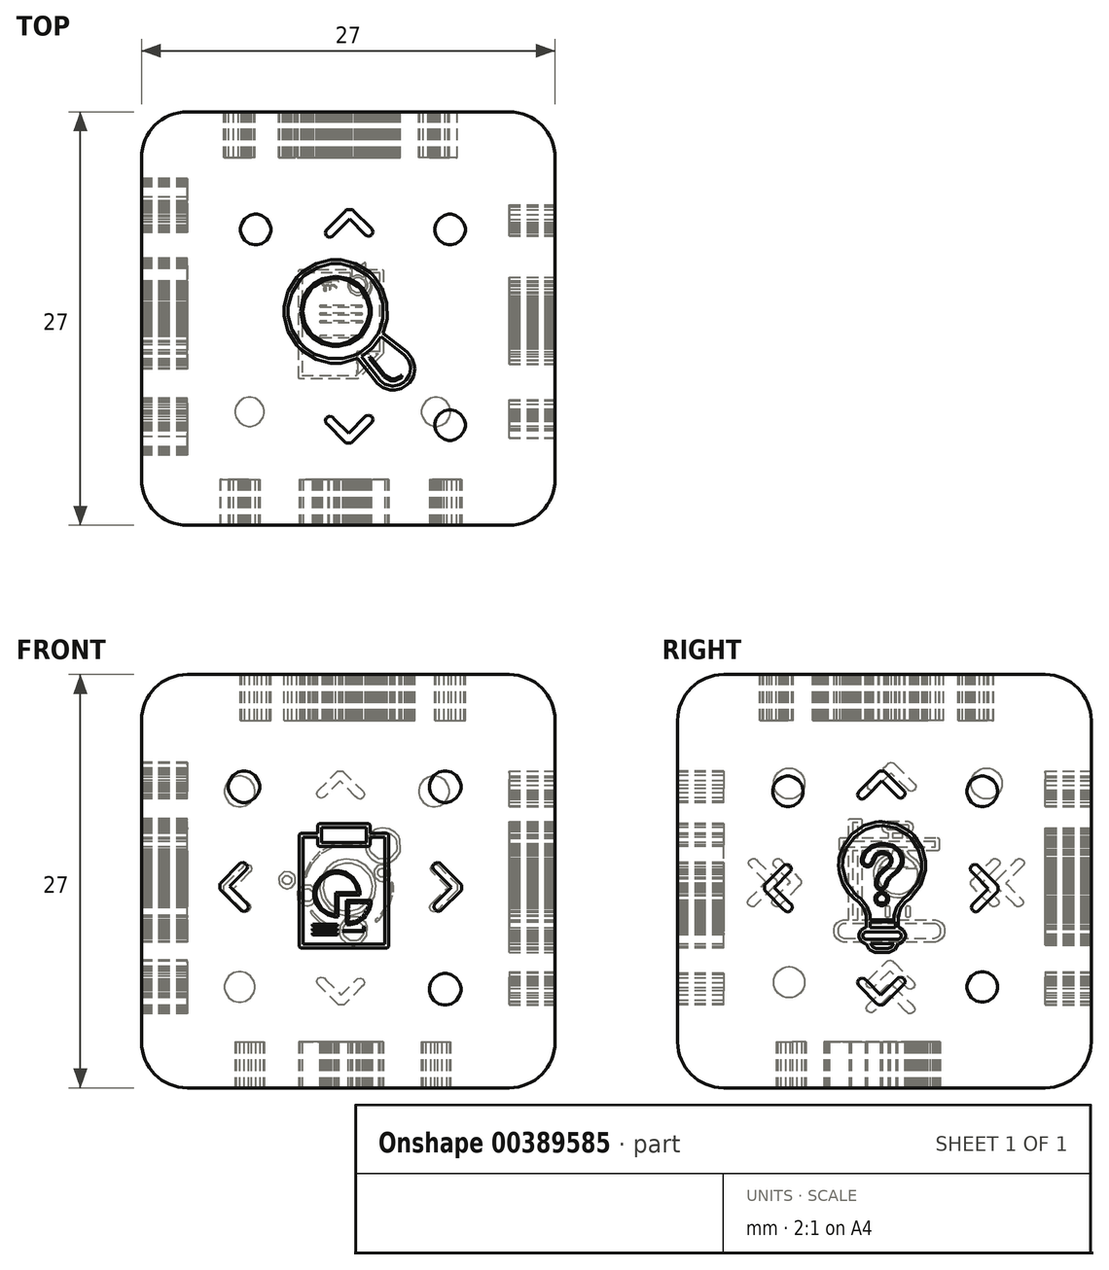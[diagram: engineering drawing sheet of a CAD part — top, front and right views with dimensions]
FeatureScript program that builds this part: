
annotation { "Feature Type Name" : "Feature", "Feature Type Description" : "" }
export const myFeature = defineFeature(function(context is Context, id is Id, definition is map)
    precondition{}
    {
        {
            var Q0;
            Q0=qCreatedBy(makeId("Front.planeOp"),FACE);
            var sketch = newSketch(context, id + "F0", { "sketchPlane" : qUnion([Q0])});
            skLineSegment(sketch, "E0.bottom", {"start": v(-13, 13.95) * mm, "end": v(14, 13.95) * mm});
            skLineSegment(sketch, "E0.top", {"start": v(-13, -13.05) * mm, "end": v(14, -13.05) * mm});
            skLineSegment(sketch, "E0.left", {"start": v(-13, 13.95) * mm, "end": v(-13, -13.05) * mm});
            skLineSegment(sketch, "E0.right", {"start": v(14, 13.95) * mm, "end": v(14, -13.05) * mm});
            skSolve(sketch);
        }
        {
            var Q0;
            Q0=makeQuery(id+"F0.imprint","IMPRINT",FACE,{"disambiguationData":[TD([[makeQuery(id+"F0.imprint","IMPRINT",EDGE,{"derivedFrom":sQuery(id+"F0.wireOp",EDGE,"E0.bottom")}),-1.0]])]});
            extrude(context, id + "F1", {"entities" : qUnion([Q0]), "depth" : 27 * mm});
        }
        {
            var Q0;
            Q0=makeQuery(id+"F1.opExtrude","SWEPT_EDGE",EDGE,{"disambiguationData":[OSD([sQuery(id+"F0.wireOp",EDGE,"E0.bottom"),sQuery(id+"F0.wireOp",EDGE,"E0.right")])]});
            var Q1;
            Q1=makeQuery(id+"F1.opExtrude","CAP_EDGE",EDGE,{"disambiguationData":[OSD([sQuery(id+"F0.wireOp",EDGE,"E0.bottom")])],"isStart":true});
            var Q2;
            Q2=makeQuery(id+"F1.opExtrude","CAP_EDGE",EDGE,{"disambiguationData":[OSD([sQuery(id+"F0.wireOp",EDGE,"E0.right")])],"isStart":true});
            var Q3;
            Q3=makeQuery(id+"F1.opExtrude","CAP_EDGE",EDGE,{"disambiguationData":[OSD([sQuery(id+"F0.wireOp",EDGE,"E0.left")])],"isStart":true});
            var Q4;
            Q4=makeQuery(id+"F1.opExtrude","CAP_EDGE",EDGE,{"disambiguationData":[OSD([sQuery(id+"F0.wireOp",EDGE,"E0.top")])],"isStart":true});
            var Q5;
            Q5=makeQuery(id+"F1.opExtrude","SWEPT_EDGE",EDGE,{"disambiguationData":[OSD([sQuery(id+"F0.wireOp",EDGE,"E0.top"),sQuery(id+"F0.wireOp",EDGE,"E0.left")])]});
            var Q6;
            Q6=makeQuery(id+"F1.opExtrude","SWEPT_EDGE",EDGE,{"disambiguationData":[OSD([sQuery(id+"F0.wireOp",EDGE,"E0.bottom"),sQuery(id+"F0.wireOp",EDGE,"E0.left")])]});
            var Q7;
            Q7=makeQuery(id+"F1.opExtrude","CAP_EDGE",EDGE,{"disambiguationData":[OSD([sQuery(id+"F0.wireOp",EDGE,"E0.left")])],"isStart":false});
            var Q8;
            Q8=makeQuery(id+"F1.opExtrude","CAP_EDGE",EDGE,{"disambiguationData":[OSD([sQuery(id+"F0.wireOp",EDGE,"E0.right")])],"isStart":false});
            var Q9;
            Q9=makeQuery(id+"F1.opExtrude","CAP_EDGE",EDGE,{"disambiguationData":[OSD([sQuery(id+"F0.wireOp",EDGE,"E0.top")])],"isStart":false});
            var Q10;
            Q10=makeQuery(id+"F1.opExtrude","SWEPT_EDGE",EDGE,{"disambiguationData":[OSD([sQuery(id+"F0.wireOp",EDGE,"E0.top"),sQuery(id+"F0.wireOp",EDGE,"E0.right")])]});
            var Q11;
            Q11=makeQuery(id+"F1.opExtrude","CAP_EDGE",EDGE,{"disambiguationData":[OSD([sQuery(id+"F0.wireOp",EDGE,"E0.bottom")])],"isStart":false});
            fillet(context, id + "F2", {"entities" : qUnion([Q0, Q1, Q2, Q3, Q4, Q5, Q6, Q7, Q8, Q9, Q10, Q11]), "radius" : 3 * mm, "tangentPropagation" : true, "allowEdgeOverflow" : false});
        }
        {
            var Q0;
            Q0=makeQuery(id+"F1.opExtrude","CAP_FACE",FACE,{"disambiguationData":[OSD([sQuery(id+"F0.wireOp",EDGE,"E0.bottom"),sQuery(id+"F0.wireOp",EDGE,"E0.top"),sQuery(id+"F0.wireOp",EDGE,"E0.left"),sQuery(id+"F0.wireOp",EDGE,"E0.right")])],"isStart":false});
            var sketch = newSketch(context, id + "F3", { "sketchPlane" : qUnion([Q0])});
            skLineSegment(sketch, "E1", {"start": v(-2.45, -3.67) * mm, "end": v(2.88, -3.67) * mm});
            skLineSegment(sketch, "E2", {"start": v(2.88, -3.67) * mm, "end": v(2.88, 3.33) * mm});
            skLineSegment(sketch, "E3", {"start": v(2.88, 3.33) * mm, "end": v(1.94, 3.33) * mm});
            skLineSegment(sketch, "E4", {"start": v(1.94, 3.33) * mm, "end": v(1.94, 2.84) * mm});
            skLineSegment(sketch, "E5", {"start": v(1.94, 2.84) * mm, "end": v(1.94, 2.8) * mm});
            skLineSegment(sketch, "E6", {"start": v(1.94, 2.8) * mm, "end": v(1.84, 2.7) * mm});
            skLineSegment(sketch, "E7", {"start": v(1.84, 2.7) * mm, "end": v(1.81, 2.7) * mm});
            skLineSegment(sketch, "E8", {"start": v(1.81, 2.7) * mm, "end": v(-1.38, 2.7) * mm});
            skLineSegment(sketch, "E9", {"start": v(-1.38, 2.7) * mm, "end": v(-1.4, 2.7) * mm});
            skLineSegment(sketch, "E10", {"start": v(-1.4, 2.7) * mm, "end": v(-1.5, 2.8) * mm});
            skLineSegment(sketch, "E11", {"start": v(-1.5, 2.8) * mm, "end": v(-1.5, 2.84) * mm});
            skLineSegment(sketch, "E12", {"start": v(-1.5, 2.84) * mm, "end": v(-1.5, 3.33) * mm});
            skLineSegment(sketch, "E13", {"start": v(-1.5, 3.33) * mm, "end": v(-2.45, 3.33) * mm});
            skLineSegment(sketch, "E14", {"start": v(-2.45, 3.33) * mm, "end": v(-2.45, -3.67) * mm});
            skLineSegment(sketch, "E15", {"start": v(3, -3.92) * mm, "end": v(-2.58, -3.92) * mm});
            skLineSegment(sketch, "E16", {"start": v(-2.58, -3.92) * mm, "end": v(-2.6, -3.92) * mm});
            skLineSegment(sketch, "E17", {"start": v(-2.6, -3.92) * mm, "end": v(-2.7, -3.83) * mm});
            skLineSegment(sketch, "E18", {"start": v(-2.7, -3.83) * mm, "end": v(-2.7, -3.8) * mm});
            skLineSegment(sketch, "E19", {"start": v(-2.7, -3.8) * mm, "end": v(-2.7, 3.46) * mm});
            skLineSegment(sketch, "E20", {"start": v(-2.7, 3.46) * mm, "end": v(-2.7, 3.49) * mm});
            skLineSegment(sketch, "E21", {"start": v(-2.7, 3.49) * mm, "end": v(-2.6, 3.59) * mm});
            skLineSegment(sketch, "E22", {"start": v(-2.6, 3.59) * mm, "end": v(-2.58, 3.59) * mm});
            skLineSegment(sketch, "E23", {"start": v(-2.58, 3.59) * mm, "end": v(-1.38, 3.59) * mm});
            skLineSegment(sketch, "E24", {"start": v(-1.38, 3.59) * mm, "end": v(-1.35, 3.59) * mm});
            skLineSegment(sketch, "E25", {"start": v(-1.35, 3.59) * mm, "end": v(-1.25, 3.49) * mm});
            skLineSegment(sketch, "E26", {"start": v(-1.25, 3.49) * mm, "end": v(-1.25, 3.46) * mm});
            skLineSegment(sketch, "E27", {"start": v(-1.25, 3.46) * mm, "end": v(-1.25, 2.97) * mm});
            skLineSegment(sketch, "E28", {"start": v(-1.25, 2.97) * mm, "end": v(1.68, 2.97) * mm});
            skLineSegment(sketch, "E29", {"start": v(1.68, 2.97) * mm, "end": v(1.68, 3.46) * mm});
            skLineSegment(sketch, "E30", {"start": v(1.68, 3.46) * mm, "end": v(1.68, 3.49) * mm});
            skLineSegment(sketch, "E31", {"start": v(1.68, 3.49) * mm, "end": v(1.78, 3.59) * mm});
            skLineSegment(sketch, "E32", {"start": v(1.78, 3.59) * mm, "end": v(1.81, 3.59) * mm});
            skLineSegment(sketch, "E33", {"start": v(1.81, 3.59) * mm, "end": v(3, 3.59) * mm});
            skLineSegment(sketch, "E34", {"start": v(3, 3.59) * mm, "end": v(3.04, 3.59) * mm});
            skLineSegment(sketch, "E35", {"start": v(3.04, 3.59) * mm, "end": v(3.14, 3.49) * mm});
            skLineSegment(sketch, "E36", {"start": v(3.14, 3.49) * mm, "end": v(3.14, 3.46) * mm});
            skLineSegment(sketch, "E37", {"start": v(3.14, 3.46) * mm, "end": v(3.14, -3.8) * mm});
            skLineSegment(sketch, "E38", {"start": v(3.14, -3.8) * mm, "end": v(3.14, -3.83) * mm});
            skLineSegment(sketch, "E39", {"start": v(3.14, -3.83) * mm, "end": v(3.04, -3.92) * mm});
            skLineSegment(sketch, "E40", {"start": v(3.04, -3.92) * mm, "end": v(3, -3.92) * mm});
            skLineSegment(sketch, "E41", {"start": v(1.68, 2.97) * mm, "end": v(1.68, 3.97) * mm});
            skLineSegment(sketch, "E42", {"start": v(1.68, 3.97) * mm, "end": v(-1.25, 3.97) * mm});
            skLineSegment(sketch, "E43", {"start": v(-1.25, 3.97) * mm, "end": v(-1.25, 2.97) * mm});
            skLineSegment(sketch, "E44", {"start": v(-1.5, 2.84) * mm, "end": v(-1.5, 4.1) * mm});
            skLineSegment(sketch, "E45", {"start": v(-1.5, 4.1) * mm, "end": v(-1.5, 4.13) * mm});
            skLineSegment(sketch, "E46", {"start": v(-1.5, 4.13) * mm, "end": v(-1.4, 4.23) * mm});
            skLineSegment(sketch, "E47", {"start": v(-1.4, 4.23) * mm, "end": v(-1.38, 4.23) * mm});
            skLineSegment(sketch, "E48", {"start": v(-1.38, 4.23) * mm, "end": v(1.81, 4.23) * mm});
            skLineSegment(sketch, "E49", {"start": v(1.81, 4.23) * mm, "end": v(1.84, 4.23) * mm});
            skLineSegment(sketch, "E50", {"start": v(1.84, 4.23) * mm, "end": v(1.94, 4.13) * mm});
            skLineSegment(sketch, "E51", {"start": v(1.94, 4.13) * mm, "end": v(1.94, 4.1) * mm});
            skLineSegment(sketch, "E52", {"start": v(1.94, 4.1) * mm, "end": v(1.94, 2.84) * mm});
            skLineSegment(sketch, "E53", {"start": v(-0.26, 0.99) * mm, "end": v(-0.39, 0.99) * mm});
            skLineSegment(sketch, "E54", {"start": v(-0.39, 0.99) * mm, "end": v(-0.78, 0.88) * mm});
            skLineSegment(sketch, "E55", {"start": v(-0.78, 0.88) * mm, "end": v(-1.22, 0.59) * mm});
            skLineSegment(sketch, "E56", {"start": v(-1.22, 0.59) * mm, "end": v(-1.5, 0.16) * mm});
            skLineSegment(sketch, "E57", {"start": v(-1.5, 0.16) * mm, "end": v(-1.61, -0.24) * mm});
            skLineSegment(sketch, "E58", {"start": v(-1.61, -0.24) * mm, "end": v(-1.61, -0.37) * mm});
            skLineSegment(sketch, "E59", {"start": v(-1.61, -0.37) * mm, "end": v(-1.61, -0.5) * mm});
            skLineSegment(sketch, "E60", {"start": v(-1.61, -0.5) * mm, "end": v(-1.51, -0.88) * mm});
            skLineSegment(sketch, "E61", {"start": v(-1.51, -0.88) * mm, "end": v(-1.24, -1.3) * mm});
            skLineSegment(sketch, "E62", {"start": v(-1.24, -1.3) * mm, "end": v(-0.83, -1.6) * mm});
            skLineSegment(sketch, "E63", {"start": v(-0.83, -1.6) * mm, "end": v(-0.46, -1.72) * mm});
            skLineSegment(sketch, "E64", {"start": v(-0.46, -1.72) * mm, "end": v(-0.33, -1.73) * mm});
            skLineSegment(sketch, "E65", {"start": v(-0.33, -1.73) * mm, "end": v(-0.33, -0.3) * mm});
            skLineSegment(sketch, "E66", {"start": v(-0.33, -0.3) * mm, "end": v(1.1, -0.3) * mm});
            skLineSegment(sketch, "E67", {"start": v(1.1, -0.3) * mm, "end": v(1.1, -0.17) * mm});
            skLineSegment(sketch, "E68", {"start": v(1.1, -0.17) * mm, "end": v(0.97, 0.2) * mm});
            skLineSegment(sketch, "E69", {"start": v(0.97, 0.2) * mm, "end": v(0.68, 0.61) * mm});
            skLineSegment(sketch, "E70", {"start": v(0.68, 0.61) * mm, "end": v(0.26, 0.89) * mm});
            skLineSegment(sketch, "E71", {"start": v(0.26, 0.89) * mm, "end": v(-0.13, 0.99) * mm});
            skLineSegment(sketch, "E72", {"start": v(-0.13, 0.99) * mm, "end": v(-0.26, 0.99) * mm});
            skLineSegment(sketch, "E73", {"start": v(-0.18, -1.88) * mm, "end": v(-0.26, -1.88) * mm});
            skLineSegment(sketch, "E74", {"start": v(-0.26, -1.88) * mm, "end": v(-0.4, -1.88) * mm});
            skLineSegment(sketch, "E75", {"start": v(-0.4, -1.88) * mm, "end": v(-0.84, -1.76) * mm});
            skLineSegment(sketch, "E76", {"start": v(-0.84, -1.76) * mm, "end": v(-1.32, -1.44) * mm});
            skLineSegment(sketch, "E77", {"start": v(-1.32, -1.44) * mm, "end": v(-1.65, -0.96) * mm});
            skLineSegment(sketch, "E78", {"start": v(-1.65, -0.96) * mm, "end": v(-1.77, -0.52) * mm});
            skLineSegment(sketch, "E79", {"start": v(-1.77, -0.52) * mm, "end": v(-1.77, -0.37) * mm});
            skLineSegment(sketch, "E80", {"start": v(-1.77, -0.37) * mm, "end": v(-1.77, -0.22) * mm});
            skLineSegment(sketch, "E81", {"start": v(-1.77, -0.22) * mm, "end": v(-1.65, 0.22) * mm});
            skLineSegment(sketch, "E82", {"start": v(-1.65, 0.22) * mm, "end": v(-1.32, 0.7) * mm});
            skLineSegment(sketch, "E83", {"start": v(-1.32, 0.7) * mm, "end": v(-0.84, 1.02) * mm});
            skLineSegment(sketch, "E84", {"start": v(-0.84, 1.02) * mm, "end": v(-0.4, 1.14) * mm});
            skLineSegment(sketch, "E85", {"start": v(-0.4, 1.14) * mm, "end": v(-0.26, 1.14) * mm});
            skLineSegment(sketch, "E86", {"start": v(-0.26, 1.14) * mm, "end": v(-0.1, 1.14) * mm});
            skLineSegment(sketch, "E87", {"start": v(-0.1, 1.14) * mm, "end": v(0.33, 1.02) * mm});
            skLineSegment(sketch, "E88", {"start": v(0.33, 1.02) * mm, "end": v(0.81, 0.7) * mm});
            skLineSegment(sketch, "E89", {"start": v(0.81, 0.7) * mm, "end": v(1.14, 0.22) * mm});
            skLineSegment(sketch, "E90", {"start": v(1.14, 0.22) * mm, "end": v(1.26, -0.22) * mm});
            skLineSegment(sketch, "E91", {"start": v(1.26, -0.22) * mm, "end": v(1.26, -0.37) * mm});
            skLineSegment(sketch, "E92", {"start": v(1.26, -0.37) * mm, "end": v(1.26, -0.45) * mm});
            skLineSegment(sketch, "E93", {"start": v(1.26, -0.45) * mm, "end": v(-0.18, -0.45) * mm});
            skLineSegment(sketch, "E94", {"start": v(-0.18, -0.45) * mm, "end": v(-0.18, -1.88) * mm});
            skLineSegment(sketch, "E95", {"start": v(-0.47, 1.34) * mm, "end": v(-0.48, 1.34) * mm});
            skLineSegment(sketch, "E96", {"start": v(-0.48, 1.34) * mm, "end": v(-0.5, 1.37) * mm});
            skLineSegment(sketch, "E97", {"start": v(-0.5, 1.37) * mm, "end": v(-0.5, 1.37) * mm});
            skLineSegment(sketch, "E98", {"start": v(-0.5, 1.37) * mm, "end": v(-0.5, 2.1) * mm});
            skLineSegment(sketch, "E99", {"start": v(-0.5, 2.1) * mm, "end": v(-0.17, 2.1) * mm});
            skLineSegment(sketch, "E100", {"start": v(-0.17, 2.1) * mm, "end": v(-0.16, 2.1) * mm});
            skLineSegment(sketch, "E101", {"start": v(-0.16, 2.1) * mm, "end": v(-0.14, 2.09) * mm});
            skLineSegment(sketch, "E102", {"start": v(-0.14, 2.09) * mm, "end": v(-0.14, 2.08) * mm});
            skLineSegment(sketch, "E103", {"start": v(-0.14, 2.08) * mm, "end": v(-0.14, 2.07) * mm});
            skLineSegment(sketch, "E104", {"start": v(-0.14, 2.07) * mm, "end": v(-0.16, 2.05) * mm});
            skLineSegment(sketch, "E105", {"start": v(-0.16, 2.05) * mm, "end": v(-0.17, 2.05) * mm});
            skLineSegment(sketch, "E106", {"start": v(-0.17, 2.05) * mm, "end": v(-0.44, 2.05) * mm});
            skLineSegment(sketch, "E107", {"start": v(-0.44, 2.05) * mm, "end": v(-0.44, 1.37) * mm});
            skLineSegment(sketch, "E108", {"start": v(-0.44, 1.37) * mm, "end": v(-0.44, 1.37) * mm});
            skLineSegment(sketch, "E109", {"start": v(-0.44, 1.37) * mm, "end": v(-0.46, 1.34) * mm});
            skLineSegment(sketch, "E110", {"start": v(-0.46, 1.34) * mm, "end": v(-0.47, 1.34) * mm});
            skLineSegment(sketch, "E111", {"start": v(1.54, -2.84) * mm, "end": v(0.16, -2.84) * mm});
            skLineSegment(sketch, "E112", {"start": v(0.16, -2.84) * mm, "end": v(0.16, -2.84) * mm});
            skLineSegment(sketch, "E113", {"start": v(0.16, -2.84) * mm, "end": v(0.13, -2.82) * mm});
            skLineSegment(sketch, "E114", {"start": v(0.13, -2.82) * mm, "end": v(0.13, -2.81) * mm});
            skLineSegment(sketch, "E115", {"start": v(0.13, -2.81) * mm, "end": v(0.13, -2.8) * mm});
            skLineSegment(sketch, "E116", {"start": v(0.13, -2.8) * mm, "end": v(0.16, -2.78) * mm});
            skLineSegment(sketch, "E117", {"start": v(0.16, -2.78) * mm, "end": v(0.16, -2.78) * mm});
            skLineSegment(sketch, "E118", {"start": v(0.16, -2.78) * mm, "end": v(1.49, -2.78) * mm});
            skLineSegment(sketch, "E119", {"start": v(1.49, -2.78) * mm, "end": v(1.49, -2.51) * mm});
            skLineSegment(sketch, "E120", {"start": v(1.49, -2.51) * mm, "end": v(1.49, -2.5) * mm});
            skLineSegment(sketch, "E121", {"start": v(1.49, -2.5) * mm, "end": v(1.5, -2.48) * mm});
            skLineSegment(sketch, "E122", {"start": v(1.5, -2.48) * mm, "end": v(1.51, -2.48) * mm});
            skLineSegment(sketch, "E123", {"start": v(1.51, -2.48) * mm, "end": v(1.52, -2.48) * mm});
            skLineSegment(sketch, "E124", {"start": v(1.52, -2.48) * mm, "end": v(1.54, -2.5) * mm});
            skLineSegment(sketch, "E125", {"start": v(1.54, -2.5) * mm, "end": v(1.54, -2.51) * mm});
            skLineSegment(sketch, "E126", {"start": v(1.54, -2.51) * mm, "end": v(1.54, -2.84) * mm});
            skLineSegment(sketch, "E127", {"start": v(1.93, 2) * mm, "end": v(0.4, 2) * mm});
            skLineSegment(sketch, "E128", {"start": v(0.4, 2) * mm, "end": v(0.38, 2) * mm});
            skLineSegment(sketch, "E129", {"start": v(0.38, 2) * mm, "end": v(0.33, 2.05) * mm});
            skLineSegment(sketch, "E130", {"start": v(0.33, 2.05) * mm, "end": v(0.33, 2.07) * mm});
            skLineSegment(sketch, "E131", {"start": v(0.33, 2.07) * mm, "end": v(0.33, 2.08) * mm});
            skLineSegment(sketch, "E132", {"start": v(0.33, 2.08) * mm, "end": v(0.38, 2.13) * mm});
            skLineSegment(sketch, "E133", {"start": v(0.38, 2.13) * mm, "end": v(0.4, 2.13) * mm});
            skLineSegment(sketch, "E134", {"start": v(0.4, 2.13) * mm, "end": v(1.93, 2.13) * mm});
            skLineSegment(sketch, "E135", {"start": v(1.93, 2.13) * mm, "end": v(1.95, 2.13) * mm});
            skLineSegment(sketch, "E136", {"start": v(1.95, 2.13) * mm, "end": v(2, 2.08) * mm});
            skLineSegment(sketch, "E137", {"start": v(2, 2.08) * mm, "end": v(2, 2.07) * mm});
            skLineSegment(sketch, "E138", {"start": v(2, 2.07) * mm, "end": v(2, 2.05) * mm});
            skLineSegment(sketch, "E139", {"start": v(2, 2.05) * mm, "end": v(1.95, 2) * mm});
            skLineSegment(sketch, "E140", {"start": v(1.95, 2) * mm, "end": v(1.93, 2) * mm});
            skLineSegment(sketch, "E141", {"start": v(1.93, 1.72) * mm, "end": v(0.4, 1.72) * mm});
            skLineSegment(sketch, "E142", {"start": v(0.4, 1.72) * mm, "end": v(0.38, 1.72) * mm});
            skLineSegment(sketch, "E143", {"start": v(0.38, 1.72) * mm, "end": v(0.33, 1.76) * mm});
            skLineSegment(sketch, "E144", {"start": v(0.33, 1.76) * mm, "end": v(0.33, 1.78) * mm});
            skLineSegment(sketch, "E145", {"start": v(0.33, 1.78) * mm, "end": v(0.33, 1.8) * mm});
            skLineSegment(sketch, "E146", {"start": v(0.33, 1.8) * mm, "end": v(0.38, 1.84) * mm});
            skLineSegment(sketch, "E147", {"start": v(0.38, 1.84) * mm, "end": v(0.4, 1.84) * mm});
            skLineSegment(sketch, "E148", {"start": v(0.4, 1.84) * mm, "end": v(1.93, 1.84) * mm});
            skLineSegment(sketch, "E149", {"start": v(1.93, 1.84) * mm, "end": v(1.95, 1.84) * mm});
            skLineSegment(sketch, "E150", {"start": v(1.95, 1.84) * mm, "end": v(2, 1.8) * mm});
            skLineSegment(sketch, "E151", {"start": v(2, 1.8) * mm, "end": v(2, 1.78) * mm});
            skLineSegment(sketch, "E152", {"start": v(2, 1.78) * mm, "end": v(2, 1.76) * mm});
            skLineSegment(sketch, "E153", {"start": v(2, 1.76) * mm, "end": v(1.95, 1.72) * mm});
            skLineSegment(sketch, "E154", {"start": v(1.95, 1.72) * mm, "end": v(1.93, 1.72) * mm});
            skLineSegment(sketch, "E155", {"start": v(1.93, 1.43) * mm, "end": v(0.4, 1.43) * mm});
            skLineSegment(sketch, "E156", {"start": v(0.4, 1.43) * mm, "end": v(0.38, 1.43) * mm});
            skLineSegment(sketch, "E157", {"start": v(0.38, 1.43) * mm, "end": v(0.33, 1.48) * mm});
            skLineSegment(sketch, "E158", {"start": v(0.33, 1.48) * mm, "end": v(0.33, 1.5) * mm});
            skLineSegment(sketch, "E159", {"start": v(0.33, 1.5) * mm, "end": v(0.33, 1.5) * mm});
            skLineSegment(sketch, "E160", {"start": v(0.33, 1.5) * mm, "end": v(0.38, 1.56) * mm});
            skLineSegment(sketch, "E161", {"start": v(0.38, 1.56) * mm, "end": v(0.4, 1.56) * mm});
            skLineSegment(sketch, "E162", {"start": v(0.4, 1.56) * mm, "end": v(1.93, 1.56) * mm});
            skLineSegment(sketch, "E163", {"start": v(1.93, 1.56) * mm, "end": v(1.95, 1.56) * mm});
            skLineSegment(sketch, "E164", {"start": v(1.95, 1.56) * mm, "end": v(2, 1.5) * mm});
            skLineSegment(sketch, "E165", {"start": v(2, 1.5) * mm, "end": v(2, 1.5) * mm});
            skLineSegment(sketch, "E166", {"start": v(2, 1.5) * mm, "end": v(2, 1.48) * mm});
            skLineSegment(sketch, "E167", {"start": v(2, 1.48) * mm, "end": v(1.95, 1.43) * mm});
            skLineSegment(sketch, "E168", {"start": v(1.95, 1.43) * mm, "end": v(1.93, 1.43) * mm});
            skLineSegment(sketch, "E169", {"start": v(-0.26, -2.5) * mm, "end": v(-1.8, -2.5) * mm});
            skLineSegment(sketch, "E170", {"start": v(-1.8, -2.5) * mm, "end": v(-1.8, -2.5) * mm});
            skLineSegment(sketch, "E171", {"start": v(-1.8, -2.5) * mm, "end": v(-1.85, -2.44) * mm});
            skLineSegment(sketch, "E172", {"start": v(-1.85, -2.44) * mm, "end": v(-1.85, -2.43) * mm});
            skLineSegment(sketch, "E173", {"start": v(-1.85, -2.43) * mm, "end": v(-1.85, -2.41) * mm});
            skLineSegment(sketch, "E174", {"start": v(-1.85, -2.41) * mm, "end": v(-1.8, -2.36) * mm});
            skLineSegment(sketch, "E175", {"start": v(-1.8, -2.36) * mm, "end": v(-1.8, -2.36) * mm});
            skLineSegment(sketch, "E176", {"start": v(-1.8, -2.36) * mm, "end": v(-0.26, -2.36) * mm});
            skLineSegment(sketch, "E177", {"start": v(-0.26, -2.36) * mm, "end": v(-0.24, -2.36) * mm});
            skLineSegment(sketch, "E178", {"start": v(-0.24, -2.36) * mm, "end": v(-0.2, -2.41) * mm});
            skLineSegment(sketch, "E179", {"start": v(-0.2, -2.41) * mm, "end": v(-0.2, -2.43) * mm});
            skLineSegment(sketch, "E180", {"start": v(-0.2, -2.43) * mm, "end": v(-0.2, -2.44) * mm});
            skLineSegment(sketch, "E181", {"start": v(-0.2, -2.44) * mm, "end": v(-0.24, -2.5) * mm});
            skLineSegment(sketch, "E182", {"start": v(-0.24, -2.5) * mm, "end": v(-0.26, -2.5) * mm});
            skLineSegment(sketch, "E183", {"start": v(-0.26, -2.78) * mm, "end": v(-1.8, -2.78) * mm});
            skLineSegment(sketch, "E184", {"start": v(-1.8, -2.78) * mm, "end": v(-1.8, -2.78) * mm});
            skLineSegment(sketch, "E185", {"start": v(-1.8, -2.78) * mm, "end": v(-1.85, -2.73) * mm});
            skLineSegment(sketch, "E186", {"start": v(-1.85, -2.73) * mm, "end": v(-1.85, -2.71) * mm});
            skLineSegment(sketch, "E187", {"start": v(-1.85, -2.71) * mm, "end": v(-1.85, -2.7) * mm});
            skLineSegment(sketch, "E188", {"start": v(-1.85, -2.7) * mm, "end": v(-1.8, -2.65) * mm});
            skLineSegment(sketch, "E189", {"start": v(-1.8, -2.65) * mm, "end": v(-1.8, -2.65) * mm});
            skLineSegment(sketch, "E190", {"start": v(-1.8, -2.65) * mm, "end": v(-0.26, -2.65) * mm});
            skLineSegment(sketch, "E191", {"start": v(-0.26, -2.65) * mm, "end": v(-0.24, -2.65) * mm});
            skLineSegment(sketch, "E192", {"start": v(-0.24, -2.65) * mm, "end": v(-0.2, -2.7) * mm});
            skLineSegment(sketch, "E193", {"start": v(-0.2, -2.7) * mm, "end": v(-0.2, -2.71) * mm});
            skLineSegment(sketch, "E194", {"start": v(-0.2, -2.71) * mm, "end": v(-0.2, -2.73) * mm});
            skLineSegment(sketch, "E195", {"start": v(-0.2, -2.73) * mm, "end": v(-0.24, -2.78) * mm});
            skLineSegment(sketch, "E196", {"start": v(-0.24, -2.78) * mm, "end": v(-0.26, -2.78) * mm});
            skLineSegment(sketch, "E197", {"start": v(-0.26, -3.07) * mm, "end": v(-1.8, -3.07) * mm});
            skLineSegment(sketch, "E198", {"start": v(-1.8, -3.07) * mm, "end": v(-1.8, -3.07) * mm});
            skLineSegment(sketch, "E199", {"start": v(-1.8, -3.07) * mm, "end": v(-1.85, -3.02) * mm});
            skLineSegment(sketch, "E200", {"start": v(-1.85, -3.02) * mm, "end": v(-1.85, -3) * mm});
            skLineSegment(sketch, "E201", {"start": v(-1.85, -3) * mm, "end": v(-1.85, -2.98) * mm});
            skLineSegment(sketch, "E202", {"start": v(-1.85, -2.98) * mm, "end": v(-1.8, -2.94) * mm});
            skLineSegment(sketch, "E203", {"start": v(-1.8, -2.94) * mm, "end": v(-1.8, -2.94) * mm});
            skLineSegment(sketch, "E204", {"start": v(-1.8, -2.94) * mm, "end": v(-0.26, -2.94) * mm});
            skLineSegment(sketch, "E205", {"start": v(-0.26, -2.94) * mm, "end": v(-0.24, -2.94) * mm});
            skLineSegment(sketch, "E206", {"start": v(-0.24, -2.94) * mm, "end": v(-0.2, -2.98) * mm});
            skLineSegment(sketch, "E207", {"start": v(-0.2, -2.98) * mm, "end": v(-0.2, -3) * mm});
            skLineSegment(sketch, "E208", {"start": v(-0.2, -3) * mm, "end": v(-0.2, -3.02) * mm});
            skLineSegment(sketch, "E209", {"start": v(-0.2, -3.02) * mm, "end": v(-0.24, -3.07) * mm});
            skLineSegment(sketch, "E210", {"start": v(-0.24, -3.07) * mm, "end": v(-0.26, -3.07) * mm});
            skLineSegment(sketch, "E211", {"start": v(0.52, -0.97) * mm, "end": v(0.52, -1.08) * mm});
            skLineSegment(sketch, "E212", {"start": v(0.52, -1.08) * mm, "end": v(0.53, -1.7) * mm});
            skLineSegment(sketch, "E213", {"start": v(0.53, -1.7) * mm, "end": v(0.53, -2.2) * mm});
            skLineSegment(sketch, "E214", {"start": v(0.53, -2.2) * mm, "end": v(0.54, -2.25) * mm});
            skLineSegment(sketch, "E215", {"start": v(0.54, -2.25) * mm, "end": v(0.66, -2.24) * mm});
            skLineSegment(sketch, "E216", {"start": v(0.66, -2.24) * mm, "end": v(1.03, -2.13) * mm});
            skLineSegment(sketch, "E217", {"start": v(1.03, -2.13) * mm, "end": v(1.43, -1.86) * mm});
            skLineSegment(sketch, "E218", {"start": v(1.43, -1.86) * mm, "end": v(1.7, -1.46) * mm});
            skLineSegment(sketch, "E219", {"start": v(1.7, -1.46) * mm, "end": v(1.82, -1.1) * mm});
            skLineSegment(sketch, "E220", {"start": v(1.82, -1.1) * mm, "end": v(1.83, -0.97) * mm});
            skLineSegment(sketch, "E221", {"start": v(1.83, -0.97) * mm, "end": v(0.52, -0.97) * mm});
            skLineSegment(sketch, "E222", {"start": v(0.47, -2.4) * mm, "end": v(0.44, -2.4) * mm});
            skLineSegment(sketch, "E223", {"start": v(0.44, -2.4) * mm, "end": v(0.42, -2.38) * mm});
            skLineSegment(sketch, "E224", {"start": v(0.42, -2.38) * mm, "end": v(0.4, -2.37) * mm});
            skLineSegment(sketch, "E225", {"start": v(0.4, -2.37) * mm, "end": v(0.4, -2.34) * mm});
            skLineSegment(sketch, "E226", {"start": v(0.4, -2.34) * mm, "end": v(0.38, -2.17) * mm});
            skLineSegment(sketch, "E227", {"start": v(0.38, -2.17) * mm, "end": v(0.37, -1.73) * mm});
            skLineSegment(sketch, "E228", {"start": v(0.37, -1.73) * mm, "end": v(0.37, -1.1) * mm});
            skLineSegment(sketch, "E229", {"start": v(0.37, -1.1) * mm, "end": v(0.37, -0.9) * mm});
            skLineSegment(sketch, "E230", {"start": v(0.37, -0.9) * mm, "end": v(0.37, -0.82) * mm});
            skLineSegment(sketch, "E231", {"start": v(0.37, -0.82) * mm, "end": v(1.98, -0.82) * mm});
            skLineSegment(sketch, "E232", {"start": v(1.98, -0.82) * mm, "end": v(1.98, -0.9) * mm});
            skLineSegment(sketch, "E233", {"start": v(1.98, -0.9) * mm, "end": v(1.98, -1.04) * mm});
            skLineSegment(sketch, "E234", {"start": v(1.98, -1.04) * mm, "end": v(1.86, -1.48) * mm});
            skLineSegment(sketch, "E235", {"start": v(1.86, -1.48) * mm, "end": v(1.54, -1.96) * mm});
            skLineSegment(sketch, "E236", {"start": v(1.54, -1.96) * mm, "end": v(1.06, -2.28) * mm});
            skLineSegment(sketch, "E237", {"start": v(1.06, -2.28) * mm, "end": v(0.62, -2.4) * mm});
            skLineSegment(sketch, "E238", {"start": v(0.62, -2.4) * mm, "end": v(0.47, -2.4) * mm});
            skLineSegment(sketch, "E239", {"start": v(0.76, -2.33) * mm, "end": v(0.75, -2.33) * mm});
            skLineSegment(sketch, "E240", {"start": v(0.75, -2.33) * mm, "end": v(0.74, -2.32) * mm});
            skLineSegment(sketch, "E241", {"start": v(0.74, -2.32) * mm, "end": v(0.74, -2.32) * mm});
            skLineSegment(sketch, "E242", {"start": v(0.74, -2.32) * mm, "end": v(0.42, -2) * mm});
            skLineSegment(sketch, "E243", {"start": v(0.42, -2) * mm, "end": v(0.42, -2) * mm});
            skLineSegment(sketch, "E244", {"start": v(0.42, -2) * mm, "end": v(0.42, -1.96) * mm});
            skLineSegment(sketch, "E245", {"start": v(0.42, -1.96) * mm, "end": v(0.42, -1.96) * mm});
            skLineSegment(sketch, "E246", {"start": v(0.42, -1.96) * mm, "end": v(0.46, -1.96) * mm});
            skLineSegment(sketch, "E247", {"start": v(0.46, -1.96) * mm, "end": v(0.46, -1.96) * mm});
            skLineSegment(sketch, "E248", {"start": v(0.46, -1.96) * mm, "end": v(0.78, -2.28) * mm});
            skLineSegment(sketch, "E249", {"start": v(0.78, -2.28) * mm, "end": v(0.78, -2.28) * mm});
            skLineSegment(sketch, "E250", {"start": v(0.78, -2.28) * mm, "end": v(0.78, -2.31) * mm});
            skLineSegment(sketch, "E251", {"start": v(0.78, -2.31) * mm, "end": v(0.78, -2.32) * mm});
            skLineSegment(sketch, "E252", {"start": v(0.78, -2.32) * mm, "end": v(0.78, -2.32) * mm});
            skLineSegment(sketch, "E253", {"start": v(0.78, -2.32) * mm, "end": v(0.76, -2.33) * mm});
            skLineSegment(sketch, "E254", {"start": v(0.76, -2.33) * mm, "end": v(0.76, -2.33) * mm});
            skLineSegment(sketch, "E255", {"start": v(1.83, -1.25) * mm, "end": v(1.82, -1.25) * mm});
            skLineSegment(sketch, "E256", {"start": v(1.82, -1.25) * mm, "end": v(1.8, -1.25) * mm});
            skLineSegment(sketch, "E257", {"start": v(1.8, -1.25) * mm, "end": v(1.8, -1.25) * mm});
            skLineSegment(sketch, "E258", {"start": v(1.8, -1.25) * mm, "end": v(1.5, -0.93) * mm});
            skLineSegment(sketch, "E259", {"start": v(1.5, -0.93) * mm, "end": v(1.49, -0.93) * mm});
            skLineSegment(sketch, "E260", {"start": v(1.49, -0.93) * mm, "end": v(1.49, -0.9) * mm});
            skLineSegment(sketch, "E261", {"start": v(1.49, -0.9) * mm, "end": v(1.5, -0.89) * mm});
            skLineSegment(sketch, "E262", {"start": v(1.5, -0.89) * mm, "end": v(1.5, -0.88) * mm});
            skLineSegment(sketch, "E263", {"start": v(1.5, -0.88) * mm, "end": v(1.53, -0.88) * mm});
            skLineSegment(sketch, "E264", {"start": v(1.53, -0.88) * mm, "end": v(1.53, -0.89) * mm});
            skLineSegment(sketch, "E265", {"start": v(1.53, -0.89) * mm, "end": v(1.85, -1.2) * mm});
            skLineSegment(sketch, "E266", {"start": v(1.85, -1.2) * mm, "end": v(1.85, -1.2) * mm});
            skLineSegment(sketch, "E267", {"start": v(1.85, -1.2) * mm, "end": v(1.85, -1.24) * mm});
            skLineSegment(sketch, "E268", {"start": v(1.85, -1.24) * mm, "end": v(1.85, -1.25) * mm});
            skLineSegment(sketch, "E269", {"start": v(1.85, -1.25) * mm, "end": v(1.85, -1.25) * mm});
            skLineSegment(sketch, "E270", {"start": v(1.85, -1.25) * mm, "end": v(1.83, -1.25) * mm});
            skLineSegment(sketch, "E271", {"start": v(1.83, -1.25) * mm, "end": v(1.83, -1.25) * mm});
            skLineSegment(sketch, "E272", {"start": v(1.04, -2.28) * mm, "end": v(1.04, -2.28) * mm});
            skLineSegment(sketch, "E273", {"start": v(1.04, -2.28) * mm, "end": v(1.02, -2.27) * mm});
            skLineSegment(sketch, "E274", {"start": v(1.02, -2.27) * mm, "end": v(1.02, -2.27) * mm});
            skLineSegment(sketch, "E275", {"start": v(1.02, -2.27) * mm, "end": v(0.48, -1.73) * mm});
            skLineSegment(sketch, "E276", {"start": v(0.48, -1.73) * mm, "end": v(0.48, -1.73) * mm});
            skLineSegment(sketch, "E277", {"start": v(0.48, -1.73) * mm, "end": v(0.48, -1.69) * mm});
            skLineSegment(sketch, "E278", {"start": v(0.48, -1.69) * mm, "end": v(0.48, -1.69) * mm});
            skLineSegment(sketch, "E279", {"start": v(0.48, -1.69) * mm, "end": v(0.49, -1.68) * mm});
            skLineSegment(sketch, "E280", {"start": v(0.49, -1.68) * mm, "end": v(0.52, -1.68) * mm});
            skLineSegment(sketch, "E281", {"start": v(0.52, -1.68) * mm, "end": v(0.53, -1.69) * mm});
            skLineSegment(sketch, "E282", {"start": v(0.53, -1.69) * mm, "end": v(1.06, -2.22) * mm});
            skLineSegment(sketch, "E283", {"start": v(1.06, -2.22) * mm, "end": v(1.07, -2.23) * mm});
            skLineSegment(sketch, "E284", {"start": v(1.07, -2.23) * mm, "end": v(1.07, -2.26) * mm});
            skLineSegment(sketch, "E285", {"start": v(1.07, -2.26) * mm, "end": v(1.06, -2.27) * mm});
            skLineSegment(sketch, "E286", {"start": v(1.06, -2.27) * mm, "end": v(1.06, -2.27) * mm});
            skLineSegment(sketch, "E287", {"start": v(1.06, -2.27) * mm, "end": v(1.05, -2.28) * mm});
            skLineSegment(sketch, "E288", {"start": v(1.05, -2.28) * mm, "end": v(1.04, -2.28) * mm});
            skLineSegment(sketch, "E289", {"start": v(1.25, -2.13) * mm, "end": v(1.25, -2.13) * mm});
            skLineSegment(sketch, "E290", {"start": v(1.25, -2.13) * mm, "end": v(1.23, -2.12) * mm});
            skLineSegment(sketch, "E291", {"start": v(1.23, -2.12) * mm, "end": v(1.23, -2.12) * mm});
            skLineSegment(sketch, "E292", {"start": v(1.23, -2.12) * mm, "end": v(0.43, -1.3) * mm});
            skLineSegment(sketch, "E293", {"start": v(0.43, -1.3) * mm, "end": v(0.43, -1.3) * mm});
            skLineSegment(sketch, "E294", {"start": v(0.43, -1.3) * mm, "end": v(0.43, -1.26) * mm});
            skLineSegment(sketch, "E295", {"start": v(0.43, -1.26) * mm, "end": v(0.43, -1.26) * mm});
            skLineSegment(sketch, "E296", {"start": v(0.43, -1.26) * mm, "end": v(0.44, -1.26) * mm});
            skLineSegment(sketch, "E297", {"start": v(0.44, -1.26) * mm, "end": v(0.47, -1.26) * mm});
            skLineSegment(sketch, "E298", {"start": v(0.47, -1.26) * mm, "end": v(0.48, -1.26) * mm});
            skLineSegment(sketch, "E299", {"start": v(0.48, -1.26) * mm, "end": v(1.28, -2.08) * mm});
            skLineSegment(sketch, "E300", {"start": v(1.28, -2.08) * mm, "end": v(1.28, -2.08) * mm});
            skLineSegment(sketch, "E301", {"start": v(1.28, -2.08) * mm, "end": v(1.28, -2.11) * mm});
            skLineSegment(sketch, "E302", {"start": v(1.28, -2.11) * mm, "end": v(1.28, -2.12) * mm});
            skLineSegment(sketch, "E303", {"start": v(1.28, -2.12) * mm, "end": v(1.27, -2.12) * mm});
            skLineSegment(sketch, "E304", {"start": v(1.27, -2.12) * mm, "end": v(1.26, -2.13) * mm});
            skLineSegment(sketch, "E305", {"start": v(1.26, -2.13) * mm, "end": v(1.25, -2.13) * mm});
            skLineSegment(sketch, "E306", {"start": v(1.47, -2) * mm, "end": v(1.46, -2) * mm});
            skLineSegment(sketch, "E307", {"start": v(1.46, -2) * mm, "end": v(1.45, -1.98) * mm});
            skLineSegment(sketch, "E308", {"start": v(1.45, -1.98) * mm, "end": v(1.45, -1.98) * mm});
            skLineSegment(sketch, "E309", {"start": v(1.45, -1.98) * mm, "end": v(0.47, -1) * mm});
            skLineSegment(sketch, "E310", {"start": v(0.47, -1) * mm, "end": v(0.47, -1) * mm});
            skLineSegment(sketch, "E311", {"start": v(0.47, -1) * mm, "end": v(0.47, -0.97) * mm});
            skLineSegment(sketch, "E312", {"start": v(0.47, -0.97) * mm, "end": v(0.47, -0.97) * mm});
            skLineSegment(sketch, "E313", {"start": v(0.47, -0.97) * mm, "end": v(0.47, -0.96) * mm});
            skLineSegment(sketch, "E314", {"start": v(0.47, -0.96) * mm, "end": v(0.5, -0.96) * mm});
            skLineSegment(sketch, "E315", {"start": v(0.5, -0.96) * mm, "end": v(0.51, -0.97) * mm});
            skLineSegment(sketch, "E316", {"start": v(0.51, -0.97) * mm, "end": v(1.49, -1.94) * mm});
            skLineSegment(sketch, "E317", {"start": v(1.49, -1.94) * mm, "end": v(1.5, -1.94) * mm});
            skLineSegment(sketch, "E318", {"start": v(1.5, -1.94) * mm, "end": v(1.5, -1.98) * mm});
            skLineSegment(sketch, "E319", {"start": v(1.5, -1.98) * mm, "end": v(1.49, -1.98) * mm});
            skLineSegment(sketch, "E320", {"start": v(1.49, -1.98) * mm, "end": v(1.49, -1.98) * mm});
            skLineSegment(sketch, "E321", {"start": v(1.49, -1.98) * mm, "end": v(1.47, -2) * mm});
            skLineSegment(sketch, "E322", {"start": v(1.47, -2) * mm, "end": v(1.47, -2) * mm});
            skLineSegment(sketch, "E323", {"start": v(1.66, -1.8) * mm, "end": v(1.65, -1.8) * mm});
            skLineSegment(sketch, "E324", {"start": v(1.65, -1.8) * mm, "end": v(1.64, -1.8) * mm});
            skLineSegment(sketch, "E325", {"start": v(1.64, -1.8) * mm, "end": v(1.63, -1.8) * mm});
            skLineSegment(sketch, "E326", {"start": v(1.63, -1.8) * mm, "end": v(0.85, -1) * mm});
            skLineSegment(sketch, "E327", {"start": v(0.85, -1) * mm, "end": v(0.84, -1) * mm});
            skLineSegment(sketch, "E328", {"start": v(0.84, -1) * mm, "end": v(0.84, -0.95) * mm});
            skLineSegment(sketch, "E329", {"start": v(0.84, -0.95) * mm, "end": v(0.85, -0.95) * mm});
            skLineSegment(sketch, "E330", {"start": v(0.85, -0.95) * mm, "end": v(0.85, -0.95) * mm});
            skLineSegment(sketch, "E331", {"start": v(0.85, -0.95) * mm, "end": v(0.89, -0.95) * mm});
            skLineSegment(sketch, "E332", {"start": v(0.89, -0.95) * mm, "end": v(0.89, -0.95) * mm});
            skLineSegment(sketch, "E333", {"start": v(0.89, -0.95) * mm, "end": v(1.68, -1.75) * mm});
            skLineSegment(sketch, "E334", {"start": v(1.68, -1.75) * mm, "end": v(1.68, -1.76) * mm});
            skLineSegment(sketch, "E335", {"start": v(1.68, -1.76) * mm, "end": v(1.68, -1.8) * mm});
            skLineSegment(sketch, "E336", {"start": v(1.68, -1.8) * mm, "end": v(1.68, -1.8) * mm});
            skLineSegment(sketch, "E337", {"start": v(1.68, -1.8) * mm, "end": v(1.67, -1.8) * mm});
            skLineSegment(sketch, "E338", {"start": v(1.67, -1.8) * mm, "end": v(1.66, -1.8) * mm});
            skLineSegment(sketch, "E339", {"start": v(1.66, -1.8) * mm, "end": v(1.66, -1.8) * mm});
            skLineSegment(sketch, "E340", {"start": v(1.78, -1.58) * mm, "end": v(1.77, -1.58) * mm});
            skLineSegment(sketch, "E341", {"start": v(1.77, -1.58) * mm, "end": v(1.76, -1.57) * mm});
            skLineSegment(sketch, "E342", {"start": v(1.76, -1.57) * mm, "end": v(1.76, -1.57) * mm});
            skLineSegment(sketch, "E343", {"start": v(1.76, -1.57) * mm, "end": v(1.09, -0.9) * mm});
            skLineSegment(sketch, "E344", {"start": v(1.09, -0.9) * mm, "end": v(1.08, -0.9) * mm});
            skLineSegment(sketch, "E345", {"start": v(1.08, -0.9) * mm, "end": v(1.08, -0.86) * mm});
            skLineSegment(sketch, "E346", {"start": v(1.08, -0.86) * mm, "end": v(1.09, -0.86) * mm});
            skLineSegment(sketch, "E347", {"start": v(1.09, -0.86) * mm, "end": v(1.09, -0.85) * mm});
            skLineSegment(sketch, "E348", {"start": v(1.09, -0.85) * mm, "end": v(1.12, -0.85) * mm});
            skLineSegment(sketch, "E349", {"start": v(1.12, -0.85) * mm, "end": v(1.13, -0.86) * mm});
            skLineSegment(sketch, "E350", {"start": v(1.13, -0.86) * mm, "end": v(1.8, -1.53) * mm});
            skLineSegment(sketch, "E351", {"start": v(1.8, -1.53) * mm, "end": v(1.8, -1.53) * mm});
            skLineSegment(sketch, "E352", {"start": v(1.8, -1.53) * mm, "end": v(1.8, -1.57) * mm});
            skLineSegment(sketch, "E353", {"start": v(1.8, -1.57) * mm, "end": v(1.8, -1.57) * mm});
            skLineSegment(sketch, "E354", {"start": v(1.8, -1.57) * mm, "end": v(1.78, -1.58) * mm});
            skLineSegment(sketch, "E355", {"start": v(1.78, -1.58) * mm, "end": v(1.78, -1.58) * mm});
            skLineSegment(sketch, "E356", {"start": v(-6.1, -1.03) * mm, "end": v(-6.2, -0.92) * mm});
            skLineSegment(sketch, "E357", {"start": v(-6.2, -0.92) * mm, "end": v(-7.33, 0.2) * mm});
            skLineSegment(sketch, "E358", {"start": v(-7.33, 0.2) * mm, "end": v(-7.44, 0.32) * mm});
            skLineSegment(sketch, "E359", {"start": v(-7.44, 0.32) * mm, "end": v(-7.44, -0.1) * mm});
            skLineSegment(sketch, "E360", {"start": v(-7.44, -0.1) * mm, "end": v(-6.16, 1.18) * mm});
            skLineSegment(sketch, "E361", {"start": v(-6.16, 1.18) * mm, "end": v(-6.13, 1.22) * mm});
            skLineSegment(sketch, "E362", {"start": v(-6.13, 1.22) * mm, "end": v(-6.08, 1.4) * mm});
            skLineSegment(sketch, "E363", {"start": v(-6.08, 1.4) * mm, "end": v(-6.17, 1.59) * mm});
            skLineSegment(sketch, "E364", {"start": v(-6.17, 1.59) * mm, "end": v(-6.36, 1.68) * mm});
            skLineSegment(sketch, "E365", {"start": v(-6.36, 1.68) * mm, "end": v(-6.54, 1.63) * mm});
            skLineSegment(sketch, "E366", {"start": v(-6.54, 1.63) * mm, "end": v(-6.58, 1.6) * mm});
            skLineSegment(sketch, "E367", {"start": v(-6.58, 1.6) * mm, "end": v(-7.86, 0.32) * mm});
            skLineSegment(sketch, "E368", {"start": v(-7.86, 0.32) * mm, "end": v(-7.89, 0.29) * mm});
            skLineSegment(sketch, "E369", {"start": v(-7.89, 0.29) * mm, "end": v(-7.89, -0.07) * mm});
            skLineSegment(sketch, "E370", {"start": v(-7.89, -0.07) * mm, "end": v(-7.86, -0.1) * mm});
            skLineSegment(sketch, "E371", {"start": v(-7.86, -0.1) * mm, "end": v(-7.75, -0.21) * mm});
            skLineSegment(sketch, "E372", {"start": v(-7.75, -0.21) * mm, "end": v(-6.62, -1.34) * mm});
            skLineSegment(sketch, "E373", {"start": v(-6.62, -1.34) * mm, "end": v(-6.51, -1.45) * mm});
            skLineSegment(sketch, "E374", {"start": v(-6.51, -1.45) * mm, "end": v(-6.47, -1.49) * mm});
            skLineSegment(sketch, "E375", {"start": v(-6.47, -1.49) * mm, "end": v(-6.3, -1.53) * mm});
            skLineSegment(sketch, "E376", {"start": v(-6.3, -1.53) * mm, "end": v(-6.1, -1.44) * mm});
            skLineSegment(sketch, "E377", {"start": v(-6.1, -1.44) * mm, "end": v(-6, -1.25) * mm});
            skLineSegment(sketch, "E378", {"start": v(-6, -1.25) * mm, "end": v(-6.06, -1.07) * mm});
            skLineSegment(sketch, "E379", {"start": v(-6.06, -1.07) * mm, "end": v(-6.1, -1.03) * mm});
            skLineSegment(sketch, "E380", {"start": v(6.1, 1.18) * mm, "end": v(6.2, 1.07) * mm});
            skLineSegment(sketch, "E381", {"start": v(6.2, 1.07) * mm, "end": v(7.33, -0.06) * mm});
            skLineSegment(sketch, "E382", {"start": v(7.33, -0.06) * mm, "end": v(7.44, -0.17) * mm});
            skLineSegment(sketch, "E383", {"start": v(7.44, -0.17) * mm, "end": v(7.44, 0.25) * mm});
            skLineSegment(sketch, "E384", {"start": v(7.44, 0.25) * mm, "end": v(6.16, -1.03) * mm});
            skLineSegment(sketch, "E385", {"start": v(6.16, -1.03) * mm, "end": v(6.13, -1.07) * mm});
            skLineSegment(sketch, "E386", {"start": v(6.13, -1.07) * mm, "end": v(6.08, -1.25) * mm});
            skLineSegment(sketch, "E387", {"start": v(6.08, -1.25) * mm, "end": v(6.17, -1.44) * mm});
            skLineSegment(sketch, "E388", {"start": v(6.17, -1.44) * mm, "end": v(6.36, -1.54) * mm});
            skLineSegment(sketch, "E389", {"start": v(6.36, -1.54) * mm, "end": v(6.54, -1.49) * mm});
            skLineSegment(sketch, "E390", {"start": v(6.54, -1.49) * mm, "end": v(6.58, -1.45) * mm});
            skLineSegment(sketch, "E391", {"start": v(6.58, -1.45) * mm, "end": v(7.86, -0.17) * mm});
            skLineSegment(sketch, "E392", {"start": v(7.86, -0.17) * mm, "end": v(7.89, -0.14) * mm});
            skLineSegment(sketch, "E393", {"start": v(7.89, -0.14) * mm, "end": v(7.89, 0.22) * mm});
            skLineSegment(sketch, "E394", {"start": v(7.89, 0.22) * mm, "end": v(7.86, 0.25) * mm});
            skLineSegment(sketch, "E395", {"start": v(7.86, 0.25) * mm, "end": v(7.75, 0.36) * mm});
            skLineSegment(sketch, "E396", {"start": v(7.75, 0.36) * mm, "end": v(6.62, 1.48) * mm});
            skLineSegment(sketch, "E397", {"start": v(6.62, 1.48) * mm, "end": v(6.51, 1.6) * mm});
            skLineSegment(sketch, "E398", {"start": v(6.51, 1.6) * mm, "end": v(6.47, 1.63) * mm});
            skLineSegment(sketch, "E399", {"start": v(6.47, 1.63) * mm, "end": v(6.3, 1.68) * mm});
            skLineSegment(sketch, "E400", {"start": v(6.3, 1.68) * mm, "end": v(6.1, 1.59) * mm});
            skLineSegment(sketch, "E401", {"start": v(6.1, 1.59) * mm, "end": v(6, 1.4) * mm});
            skLineSegment(sketch, "E402", {"start": v(6, 1.4) * mm, "end": v(6.06, 1.22) * mm});
            skLineSegment(sketch, "E403", {"start": v(6.06, 1.22) * mm, "end": v(6.1, 1.18) * mm});
            skLineSegment(sketch, "E404", {"start": v(-5.28, 6.6) * mm, "end": v(-5.28, 6.5) * mm});
            skLineSegment(sketch, "E405", {"start": v(-5.28, 6.5) * mm, "end": v(-5.36, 6.2) * mm});
            skLineSegment(sketch, "E406", {"start": v(-5.36, 6.2) * mm, "end": v(-5.58, 5.88) * mm});
            skLineSegment(sketch, "E407", {"start": v(-5.58, 5.88) * mm, "end": v(-5.9, 5.66) * mm});
            skLineSegment(sketch, "E408", {"start": v(-5.9, 5.66) * mm, "end": v(-6.2, 5.58) * mm});
            skLineSegment(sketch, "E409", {"start": v(-6.2, 5.58) * mm, "end": v(-6.3, 5.58) * mm});
            skLineSegment(sketch, "E410", {"start": v(-6.3, 5.58) * mm, "end": v(-6.41, 5.58) * mm});
            skLineSegment(sketch, "E411", {"start": v(-6.41, 5.58) * mm, "end": v(-6.71, 5.66) * mm});
            skLineSegment(sketch, "E412", {"start": v(-6.71, 5.66) * mm, "end": v(-7.04, 5.88) * mm});
            skLineSegment(sketch, "E413", {"start": v(-7.04, 5.88) * mm, "end": v(-7.26, 6.2) * mm});
            skLineSegment(sketch, "E414", {"start": v(-7.26, 6.2) * mm, "end": v(-7.34, 6.5) * mm});
            skLineSegment(sketch, "E415", {"start": v(-7.34, 6.5) * mm, "end": v(-7.34, 6.6) * mm});
            skLineSegment(sketch, "E416", {"start": v(-7.34, 6.6) * mm, "end": v(-7.34, 6.71) * mm});
            skLineSegment(sketch, "E417", {"start": v(-7.34, 6.71) * mm, "end": v(-7.26, 7.01) * mm});
            skLineSegment(sketch, "E418", {"start": v(-7.26, 7.01) * mm, "end": v(-7.04, 7.34) * mm});
            skLineSegment(sketch, "E419", {"start": v(-7.04, 7.34) * mm, "end": v(-6.71, 7.56) * mm});
            skLineSegment(sketch, "E420", {"start": v(-6.71, 7.56) * mm, "end": v(-6.41, 7.64) * mm});
            skLineSegment(sketch, "E421", {"start": v(-6.41, 7.64) * mm, "end": v(-6.3, 7.64) * mm});
            skLineSegment(sketch, "E422", {"start": v(-6.3, 7.64) * mm, "end": v(-6.2, 7.64) * mm});
            skLineSegment(sketch, "E423", {"start": v(-6.2, 7.64) * mm, "end": v(-5.9, 7.56) * mm});
            skLineSegment(sketch, "E424", {"start": v(-5.9, 7.56) * mm, "end": v(-5.58, 7.34) * mm});
            skLineSegment(sketch, "E425", {"start": v(-5.58, 7.34) * mm, "end": v(-5.36, 7.01) * mm});
            skLineSegment(sketch, "E426", {"start": v(-5.36, 7.01) * mm, "end": v(-5.28, 6.71) * mm});
            skLineSegment(sketch, "E427", {"start": v(-5.28, 6.71) * mm, "end": v(-5.28, 6.6) * mm});
            skLineSegment(sketch, "E428", {"start": v(7.85, 6.6) * mm, "end": v(7.85, 6.5) * mm});
            skLineSegment(sketch, "E429", {"start": v(7.85, 6.5) * mm, "end": v(7.77, 6.2) * mm});
            skLineSegment(sketch, "E430", {"start": v(7.77, 6.2) * mm, "end": v(7.55, 5.88) * mm});
            skLineSegment(sketch, "E431", {"start": v(7.55, 5.88) * mm, "end": v(7.22, 5.66) * mm});
            skLineSegment(sketch, "E432", {"start": v(7.22, 5.66) * mm, "end": v(6.92, 5.58) * mm});
            skLineSegment(sketch, "E433", {"start": v(6.92, 5.58) * mm, "end": v(6.82, 5.58) * mm});
            skLineSegment(sketch, "E434", {"start": v(6.82, 5.58) * mm, "end": v(6.72, 5.58) * mm});
            skLineSegment(sketch, "E435", {"start": v(6.72, 5.58) * mm, "end": v(6.42, 5.66) * mm});
            skLineSegment(sketch, "E436", {"start": v(6.42, 5.66) * mm, "end": v(6.1, 5.88) * mm});
            skLineSegment(sketch, "E437", {"start": v(6.1, 5.88) * mm, "end": v(5.87, 6.2) * mm});
            skLineSegment(sketch, "E438", {"start": v(5.87, 6.2) * mm, "end": v(5.79, 6.5) * mm});
            skLineSegment(sketch, "E439", {"start": v(5.79, 6.5) * mm, "end": v(5.79, 6.6) * mm});
            skLineSegment(sketch, "E440", {"start": v(5.79, 6.6) * mm, "end": v(5.79, 6.71) * mm});
            skLineSegment(sketch, "E441", {"start": v(5.79, 6.71) * mm, "end": v(5.87, 7.01) * mm});
            skLineSegment(sketch, "E442", {"start": v(5.87, 7.01) * mm, "end": v(6.1, 7.34) * mm});
            skLineSegment(sketch, "E443", {"start": v(6.1, 7.34) * mm, "end": v(6.42, 7.56) * mm});
            skLineSegment(sketch, "E444", {"start": v(6.42, 7.56) * mm, "end": v(6.72, 7.64) * mm});
            skLineSegment(sketch, "E445", {"start": v(6.72, 7.64) * mm, "end": v(6.82, 7.64) * mm});
            skLineSegment(sketch, "E446", {"start": v(6.82, 7.64) * mm, "end": v(6.92, 7.64) * mm});
            skLineSegment(sketch, "E447", {"start": v(6.92, 7.64) * mm, "end": v(7.22, 7.56) * mm});
            skLineSegment(sketch, "E448", {"start": v(7.22, 7.56) * mm, "end": v(7.55, 7.34) * mm});
            skLineSegment(sketch, "E449", {"start": v(7.55, 7.34) * mm, "end": v(7.77, 7.01) * mm});
            skLineSegment(sketch, "E450", {"start": v(7.77, 7.01) * mm, "end": v(7.85, 6.71) * mm});
            skLineSegment(sketch, "E451", {"start": v(7.85, 6.71) * mm, "end": v(7.85, 6.6) * mm});
            skLineSegment(sketch, "E452", {"start": v(7.85, -6.6) * mm, "end": v(7.85, -6.7) * mm});
            skLineSegment(sketch, "E453", {"start": v(7.85, -6.7) * mm, "end": v(7.77, -7) * mm});
            skLineSegment(sketch, "E454", {"start": v(7.77, -7) * mm, "end": v(7.55, -7.34) * mm});
            skLineSegment(sketch, "E455", {"start": v(7.55, -7.34) * mm, "end": v(7.22, -7.56) * mm});
            skLineSegment(sketch, "E456", {"start": v(7.22, -7.56) * mm, "end": v(6.92, -7.64) * mm});
            skLineSegment(sketch, "E457", {"start": v(6.92, -7.64) * mm, "end": v(6.82, -7.64) * mm});
            skLineSegment(sketch, "E458", {"start": v(6.82, -7.64) * mm, "end": v(6.72, -7.64) * mm});
            skLineSegment(sketch, "E459", {"start": v(6.72, -7.64) * mm, "end": v(6.42, -7.56) * mm});
            skLineSegment(sketch, "E460", {"start": v(6.42, -7.56) * mm, "end": v(6.1, -7.34) * mm});
            skLineSegment(sketch, "E461", {"start": v(6.1, -7.34) * mm, "end": v(5.87, -7) * mm});
            skLineSegment(sketch, "E462", {"start": v(5.87, -7) * mm, "end": v(5.79, -6.7) * mm});
            skLineSegment(sketch, "E463", {"start": v(5.79, -6.7) * mm, "end": v(5.79, -6.6) * mm});
            skLineSegment(sketch, "E464", {"start": v(5.79, -6.6) * mm, "end": v(5.79, -6.5) * mm});
            skLineSegment(sketch, "E465", {"start": v(5.79, -6.5) * mm, "end": v(5.87, -6.2) * mm});
            skLineSegment(sketch, "E466", {"start": v(5.87, -6.2) * mm, "end": v(6.1, -5.88) * mm});
            skLineSegment(sketch, "E467", {"start": v(6.1, -5.88) * mm, "end": v(6.42, -5.66) * mm});
            skLineSegment(sketch, "E468", {"start": v(6.42, -5.66) * mm, "end": v(6.72, -5.58) * mm});
            skLineSegment(sketch, "E469", {"start": v(6.72, -5.58) * mm, "end": v(6.82, -5.58) * mm});
            skLineSegment(sketch, "E470", {"start": v(6.82, -5.58) * mm, "end": v(6.92, -5.58) * mm});
            skLineSegment(sketch, "E471", {"start": v(6.92, -5.58) * mm, "end": v(7.22, -5.66) * mm});
            skLineSegment(sketch, "E472", {"start": v(7.22, -5.66) * mm, "end": v(7.55, -5.88) * mm});
            skLineSegment(sketch, "E473", {"start": v(7.55, -5.88) * mm, "end": v(7.77, -6.2) * mm});
            skLineSegment(sketch, "E474", {"start": v(7.77, -6.2) * mm, "end": v(7.85, -6.5) * mm});
            skLineSegment(sketch, "E475", {"start": v(7.85, -6.5) * mm, "end": v(7.85, -6.6) * mm});
            skSolve(sketch);
        }
        {
            var Q0;
            Q0 = qSketchRegion(id + "F3", true);
            var Q1;
            Q1=makeQuery(id+"F3.imprint","IMPRINT",FACE,{"disambiguationData":[TD([[makeQuery(id+"F3.imprint","IMPRINT",EDGE,{"derivedFrom":sQuery(id+"F3.wireOp",EDGE,"E53")}),-1.0]])]});
            var Q2;
            {var subQ71=sQuery(id+"F3.wireOp",EDGE,"E214");Q2=makeQuery(id+"F3.imprint","IMPRINT",FACE,{"disambiguationData":[TD([[makeQuery(id+"F3.imprint","IMPRINT",EDGE,{"derivedFrom":subQ71}),-1.0]])]});}
            var Q3;
            Q3=makeQuery(id+"F3.imprint","IMPRINT",FACE,{"disambiguationData":[TD([[makeQuery(id+"F3.imprint","IMPRINT",EDGE,{"derivedFrom":sQuery(id+"F3.wireOp",EDGE,"E169")}),-1.0]])]});
            var Q4;
            Q4=makeQuery(id+"F3.imprint","IMPRINT",FACE,{"disambiguationData":[TD([[makeQuery(id+"F3.imprint","IMPRINT",EDGE,{"derivedFrom":sQuery(id+"F3.wireOp",EDGE,"E183")}),-1.0]])]});
            var Q5;
            Q5=makeQuery(id+"F3.imprint","IMPRINT",FACE,{"disambiguationData":[TD([[makeQuery(id+"F3.imprint","IMPRINT",EDGE,{"derivedFrom":sQuery(id+"F3.wireOp",EDGE,"E197")}),-1.0]])]});
            var Q6;
            Q6=makeQuery(id+"F3.imprint","IMPRINT",FACE,{"disambiguationData":[TD([[makeQuery(id+"F3.imprint","IMPRINT",EDGE,{"derivedFrom":sQuery(id+"F3.wireOp",EDGE,"E111")}),-1.0]])]});
            extrude(context, id + "F4", {"entities" : qUnion([Q0, Q1, Q2, Q3, Q4, Q5, Q6]), "operationType" : NewBodyOperationType.REMOVE, "oppositeDirection" : true, "depth" : 3 * mm});
        }
        {
            var Q0;
            Q0=makeQuery(id+"F1.opExtrude","SWEPT_FACE",FACE,{"disambiguationData":[OSD([sQuery(id+"F0.wireOp",EDGE,"E0.left")])]});
            var sketch = newSketch(context, id + "F5", { "sketchPlane" : qUnion([Q0])});
            skLineSegment(sketch, "E476", {"start": v(16.54, -2.84) * mm, "end": v(16.54, -2.86) * mm});
            skLineSegment(sketch, "E477", {"start": v(16.54, -2.86) * mm, "end": v(16.53, -2.92) * mm});
            skLineSegment(sketch, "E478", {"start": v(16.53, -2.92) * mm, "end": v(16.5, -3) * mm});
            skLineSegment(sketch, "E479", {"start": v(16.5, -3) * mm, "end": v(16.47, -3.08) * mm});
            skLineSegment(sketch, "E480", {"start": v(16.47, -3.08) * mm, "end": v(16.42, -3.14) * mm});
            skLineSegment(sketch, "E481", {"start": v(16.42, -3.14) * mm, "end": v(16.35, -3.2) * mm});
            skLineSegment(sketch, "E482", {"start": v(16.35, -3.2) * mm, "end": v(16.28, -3.23) * mm});
            skLineSegment(sketch, "E483", {"start": v(16.28, -3.23) * mm, "end": v(16.2, -3.26) * mm});
            skLineSegment(sketch, "E484", {"start": v(16.2, -3.26) * mm, "end": v(16.13, -3.27) * mm});
            skLineSegment(sketch, "E485", {"start": v(16.13, -3.27) * mm, "end": v(16.11, -3.27) * mm});
            skLineSegment(sketch, "E486", {"start": v(16.11, -3.27) * mm, "end": v(10.25, -3.27) * mm});
            skLineSegment(sketch, "E487", {"start": v(10.25, -3.27) * mm, "end": v(10.23, -3.27) * mm});
            skLineSegment(sketch, "E488", {"start": v(10.23, -3.27) * mm, "end": v(10.17, -3.26) * mm});
            skLineSegment(sketch, "E489", {"start": v(10.17, -3.26) * mm, "end": v(10.08, -3.23) * mm});
            skLineSegment(sketch, "E490", {"start": v(10.08, -3.23) * mm, "end": v(10.01, -3.2) * mm});
            skLineSegment(sketch, "E491", {"start": v(10.01, -3.2) * mm, "end": v(9.95, -3.14) * mm});
            skLineSegment(sketch, "E492", {"start": v(9.95, -3.14) * mm, "end": v(9.9, -3.08) * mm});
            skLineSegment(sketch, "E493", {"start": v(9.9, -3.08) * mm, "end": v(9.86, -3) * mm});
            skLineSegment(sketch, "E494", {"start": v(9.86, -3) * mm, "end": v(9.83, -2.92) * mm});
            skLineSegment(sketch, "E495", {"start": v(9.83, -2.92) * mm, "end": v(9.82, -2.86) * mm});
            skLineSegment(sketch, "E496", {"start": v(9.82, -2.86) * mm, "end": v(9.82, -2.84) * mm});
            skLineSegment(sketch, "E497", {"start": v(9.82, -2.84) * mm, "end": v(9.82, -2.76) * mm});
            skLineSegment(sketch, "E498", {"start": v(9.82, -2.76) * mm, "end": v(9.82, -2.74) * mm});
            skLineSegment(sketch, "E499", {"start": v(9.82, -2.74) * mm, "end": v(9.83, -2.67) * mm});
            skLineSegment(sketch, "E500", {"start": v(9.83, -2.67) * mm, "end": v(9.86, -2.6) * mm});
            skLineSegment(sketch, "E501", {"start": v(9.86, -2.6) * mm, "end": v(9.9, -2.52) * mm});
            skLineSegment(sketch, "E502", {"start": v(9.9, -2.52) * mm, "end": v(9.95, -2.45) * mm});
            skLineSegment(sketch, "E503", {"start": v(9.95, -2.45) * mm, "end": v(10.01, -2.4) * mm});
            skLineSegment(sketch, "E504", {"start": v(10.01, -2.4) * mm, "end": v(10.08, -2.36) * mm});
            skLineSegment(sketch, "E505", {"start": v(10.08, -2.36) * mm, "end": v(10.17, -2.34) * mm});
            skLineSegment(sketch, "E506", {"start": v(10.17, -2.34) * mm, "end": v(10.23, -2.33) * mm});
            skLineSegment(sketch, "E507", {"start": v(10.23, -2.33) * mm, "end": v(10.25, -2.33) * mm});
            skLineSegment(sketch, "E508", {"start": v(10.25, -2.33) * mm, "end": v(15.08, -2.33) * mm});
            skLineSegment(sketch, "E509", {"start": v(15.08, -2.33) * mm, "end": v(15.7, -2.33) * mm});
            skLineSegment(sketch, "E510", {"start": v(15.7, -2.33) * mm, "end": v(16.11, -2.33) * mm});
            skLineSegment(sketch, "E511", {"start": v(16.11, -2.33) * mm, "end": v(16.13, -2.33) * mm});
            skLineSegment(sketch, "E512", {"start": v(16.13, -2.33) * mm, "end": v(16.2, -2.34) * mm});
            skLineSegment(sketch, "E513", {"start": v(16.2, -2.34) * mm, "end": v(16.28, -2.36) * mm});
            skLineSegment(sketch, "E514", {"start": v(16.28, -2.36) * mm, "end": v(16.35, -2.4) * mm});
            skLineSegment(sketch, "E515", {"start": v(16.35, -2.4) * mm, "end": v(16.42, -2.45) * mm});
            skLineSegment(sketch, "E516", {"start": v(16.42, -2.45) * mm, "end": v(16.47, -2.52) * mm});
            skLineSegment(sketch, "E517", {"start": v(16.47, -2.52) * mm, "end": v(16.5, -2.6) * mm});
            skLineSegment(sketch, "E518", {"start": v(16.5, -2.6) * mm, "end": v(16.53, -2.67) * mm});
            skLineSegment(sketch, "E519", {"start": v(16.53, -2.67) * mm, "end": v(16.54, -2.74) * mm});
            skLineSegment(sketch, "E520", {"start": v(16.54, -2.74) * mm, "end": v(16.54, -2.76) * mm});
            skLineSegment(sketch, "E521", {"start": v(16.54, -2.76) * mm, "end": v(16.54, -2.84) * mm});
            skLineSegment(sketch, "E522", {"start": v(15.21, 2.42) * mm, "end": v(15.58, 2.42) * mm});
            skLineSegment(sketch, "E523", {"start": v(15.58, 2.42) * mm, "end": v(15.58, -2.07) * mm});
            skLineSegment(sketch, "E524", {"start": v(15.58, -2.07) * mm, "end": v(15.21, -2.07) * mm});
            skLineSegment(sketch, "E525", {"start": v(15.21, -2.07) * mm, "end": v(15.21, 2.42) * mm});
            skLineSegment(sketch, "E526", {"start": v(13.31, 1.9) * mm, "end": v(13.36, 1.88) * mm});
            skLineSegment(sketch, "E527", {"start": v(13.36, 1.88) * mm, "end": v(13.5, 1.78) * mm});
            skLineSegment(sketch, "E528", {"start": v(13.5, 1.78) * mm, "end": v(13.64, 1.66) * mm});
            skLineSegment(sketch, "E529", {"start": v(13.64, 1.66) * mm, "end": v(13.75, 1.52) * mm});
            skLineSegment(sketch, "E530", {"start": v(13.75, 1.52) * mm, "end": v(13.82, 1.42) * mm});
            skLineSegment(sketch, "E531", {"start": v(13.82, 1.42) * mm, "end": v(13.84, 1.38) * mm});
            skLineSegment(sketch, "E532", {"start": v(13.84, 1.38) * mm, "end": v(11.41, 1.38) * mm});
            skLineSegment(sketch, "E533", {"start": v(11.41, 1.38) * mm, "end": v(11.43, 1.42) * mm});
            skLineSegment(sketch, "E534", {"start": v(11.43, 1.42) * mm, "end": v(11.5, 1.52) * mm});
            skLineSegment(sketch, "E535", {"start": v(11.5, 1.52) * mm, "end": v(11.61, 1.65) * mm});
            skLineSegment(sketch, "E536", {"start": v(11.61, 1.65) * mm, "end": v(11.75, 1.78) * mm});
            skLineSegment(sketch, "E537", {"start": v(11.75, 1.78) * mm, "end": v(11.88, 1.87) * mm});
            skLineSegment(sketch, "E538", {"start": v(11.88, 1.87) * mm, "end": v(11.92, 1.9) * mm});
            skLineSegment(sketch, "E539", {"start": v(11.92, 1.9) * mm, "end": v(11.96, 1.92) * mm});
            skLineSegment(sketch, "E540", {"start": v(11.96, 1.92) * mm, "end": v(12.06, 2) * mm});
            skLineSegment(sketch, "E541", {"start": v(12.06, 2) * mm, "end": v(12.16, 2.13) * mm});
            skLineSegment(sketch, "E542", {"start": v(12.16, 2.13) * mm, "end": v(12.24, 2.27) * mm});
            skLineSegment(sketch, "E543", {"start": v(12.24, 2.27) * mm, "end": v(12.27, 2.38) * mm});
            skLineSegment(sketch, "E544", {"start": v(12.27, 2.38) * mm, "end": v(12.28, 2.42) * mm});
            skLineSegment(sketch, "E545", {"start": v(12.28, 2.42) * mm, "end": v(12.97, 2.42) * mm});
            skLineSegment(sketch, "E546", {"start": v(12.97, 2.42) * mm, "end": v(12.98, 2.38) * mm});
            skLineSegment(sketch, "E547", {"start": v(12.98, 2.38) * mm, "end": v(13.01, 2.27) * mm});
            skLineSegment(sketch, "E548", {"start": v(13.01, 2.27) * mm, "end": v(13.09, 2.13) * mm});
            skLineSegment(sketch, "E549", {"start": v(13.09, 2.13) * mm, "end": v(13.19, 2) * mm});
            skLineSegment(sketch, "E550", {"start": v(13.19, 2) * mm, "end": v(13.28, 1.93) * mm});
            skLineSegment(sketch, "E551", {"start": v(13.28, 1.93) * mm, "end": v(13.31, 1.9) * mm});
            skLineSegment(sketch, "E552", {"start": v(13.52, -0.04) * mm, "end": v(13.47, -0.08) * mm});
            skLineSegment(sketch, "E553", {"start": v(13.47, -0.08) * mm, "end": v(13.3, -0.2) * mm});
            skLineSegment(sketch, "E554", {"start": v(13.3, -0.2) * mm, "end": v(13.06, -0.31) * mm});
            skLineSegment(sketch, "E555", {"start": v(13.06, -0.31) * mm, "end": v(12.8, -0.38) * mm});
            skLineSegment(sketch, "E556", {"start": v(12.8, -0.38) * mm, "end": v(12.6, -0.4) * mm});
            skLineSegment(sketch, "E557", {"start": v(12.6, -0.4) * mm, "end": v(12.53, -0.39) * mm});
            skLineSegment(sketch, "E558", {"start": v(12.53, -0.39) * mm, "end": v(12.47, -0.38) * mm});
            skLineSegment(sketch, "E559", {"start": v(12.47, -0.38) * mm, "end": v(12.3, -0.35) * mm});
            skLineSegment(sketch, "E560", {"start": v(12.3, -0.35) * mm, "end": v(12.07, -0.27) * mm});
            skLineSegment(sketch, "E561", {"start": v(12.07, -0.27) * mm, "end": v(11.87, -0.15) * mm});
            skLineSegment(sketch, "E562", {"start": v(11.87, -0.15) * mm, "end": v(11.7, 0) * mm});
            skLineSegment(sketch, "E563", {"start": v(11.7, 0) * mm, "end": v(11.55, 0.17) * mm});
            skLineSegment(sketch, "E564", {"start": v(11.55, 0.17) * mm, "end": v(11.43, 0.37) * mm});
            skLineSegment(sketch, "E565", {"start": v(11.43, 0.37) * mm, "end": v(11.35, 0.6) * mm});
            skLineSegment(sketch, "E566", {"start": v(11.35, 0.6) * mm, "end": v(11.32, 0.77) * mm});
            skLineSegment(sketch, "E567", {"start": v(11.32, 0.77) * mm, "end": v(11.31, 0.83) * mm});
            skLineSegment(sketch, "E568", {"start": v(11.31, 0.83) * mm, "end": v(11.31, 0.87) * mm});
            skLineSegment(sketch, "E569", {"start": v(11.31, 0.87) * mm, "end": v(11.32, 1.05) * mm});
            skLineSegment(sketch, "E570", {"start": v(11.32, 1.05) * mm, "end": v(11.35, 1.22) * mm});
            skLineSegment(sketch, "E571", {"start": v(11.35, 1.22) * mm, "end": v(11.36, 1.25) * mm});
            skLineSegment(sketch, "E572", {"start": v(11.36, 1.25) * mm, "end": v(13.9, 1.25) * mm});
            skLineSegment(sketch, "E573", {"start": v(13.9, 1.25) * mm, "end": v(13.9, 1.23) * mm});
            skLineSegment(sketch, "E574", {"start": v(13.9, 1.23) * mm, "end": v(13.93, 1.1) * mm});
            skLineSegment(sketch, "E575", {"start": v(13.93, 1.1) * mm, "end": v(13.94, 0.97) * mm});
            skLineSegment(sketch, "E576", {"start": v(13.94, 0.97) * mm, "end": v(13.94, 0.92) * mm});
            skLineSegment(sketch, "E577", {"start": v(13.94, 0.92) * mm, "end": v(13.94, 0.86) * mm});
            skLineSegment(sketch, "E578", {"start": v(13.94, 0.86) * mm, "end": v(13.91, 0.66) * mm});
            skLineSegment(sketch, "E579", {"start": v(13.91, 0.66) * mm, "end": v(13.83, 0.4) * mm});
            skLineSegment(sketch, "E580", {"start": v(13.83, 0.4) * mm, "end": v(13.7, 0.17) * mm});
            skLineSegment(sketch, "E581", {"start": v(13.7, 0.17) * mm, "end": v(13.57, 0) * mm});
            skLineSegment(sketch, "E582", {"start": v(13.57, 0) * mm, "end": v(13.52, -0.04) * mm});
            skLineSegment(sketch, "E583", {"start": v(10.18, 3.05) * mm, "end": v(12.16, 3.05) * mm});
            skLineSegment(sketch, "E584", {"start": v(12.16, 3.05) * mm, "end": v(13.09, 3.05) * mm});
            skLineSegment(sketch, "E585", {"start": v(13.09, 3.05) * mm, "end": v(15.08, 3.05) * mm});
            skLineSegment(sketch, "E586", {"start": v(15.08, 3.05) * mm, "end": v(15.7, 3.05) * mm});
            skLineSegment(sketch, "E587", {"start": v(15.7, 3.05) * mm, "end": v(16.18, 3.05) * mm});
            skLineSegment(sketch, "E588", {"start": v(16.18, 3.05) * mm, "end": v(16.18, 2.68) * mm});
            skLineSegment(sketch, "E589", {"start": v(16.18, 2.68) * mm, "end": v(15.7, 2.68) * mm});
            skLineSegment(sketch, "E590", {"start": v(15.7, 2.68) * mm, "end": v(15.08, 2.68) * mm});
            skLineSegment(sketch, "E591", {"start": v(15.08, 2.68) * mm, "end": v(13.09, 2.68) * mm});
            skLineSegment(sketch, "E592", {"start": v(13.09, 2.68) * mm, "end": v(12.16, 2.68) * mm});
            skLineSegment(sketch, "E593", {"start": v(12.16, 2.68) * mm, "end": v(10.18, 2.68) * mm});
            skLineSegment(sketch, "E594", {"start": v(10.18, 2.68) * mm, "end": v(10.18, 3.05) * mm});
            skLineSegment(sketch, "E595", {"start": v(12.3, 3.57) * mm, "end": v(12.96, 3.57) * mm});
            skLineSegment(sketch, "E596", {"start": v(12.96, 3.57) * mm, "end": v(12.96, 3.3) * mm});
            skLineSegment(sketch, "E597", {"start": v(12.96, 3.3) * mm, "end": v(12.3, 3.3) * mm});
            skLineSegment(sketch, "E598", {"start": v(12.3, 3.3) * mm, "end": v(12.3, 3.57) * mm});
            skLineSegment(sketch, "E599", {"start": v(11.88, 3.95) * mm, "end": v(11.88, 3.99) * mm});
            skLineSegment(sketch, "E600", {"start": v(11.88, 3.99) * mm, "end": v(11.88, 4) * mm});
            skLineSegment(sketch, "E601", {"start": v(11.88, 4) * mm, "end": v(11.89, 4.04) * mm});
            skLineSegment(sketch, "E602", {"start": v(11.89, 4.04) * mm, "end": v(11.92, 4.08) * mm});
            skLineSegment(sketch, "E603", {"start": v(11.92, 4.08) * mm, "end": v(11.96, 4.1) * mm});
            skLineSegment(sketch, "E604", {"start": v(11.96, 4.1) * mm, "end": v(12, 4.11) * mm});
            skLineSegment(sketch, "E605", {"start": v(12, 4.11) * mm, "end": v(12, 4.11) * mm});
            skLineSegment(sketch, "E606", {"start": v(12, 4.11) * mm, "end": v(13.25, 4.11) * mm});
            skLineSegment(sketch, "E607", {"start": v(13.25, 4.11) * mm, "end": v(13.26, 4.11) * mm});
            skLineSegment(sketch, "E608", {"start": v(13.26, 4.11) * mm, "end": v(13.3, 4.1) * mm});
            skLineSegment(sketch, "E609", {"start": v(13.3, 4.1) * mm, "end": v(13.33, 4.08) * mm});
            skLineSegment(sketch, "E610", {"start": v(13.33, 4.08) * mm, "end": v(13.36, 4.04) * mm});
            skLineSegment(sketch, "E611", {"start": v(13.36, 4.04) * mm, "end": v(13.37, 4) * mm});
            skLineSegment(sketch, "E612", {"start": v(13.37, 4) * mm, "end": v(13.37, 3.99) * mm});
            skLineSegment(sketch, "E613", {"start": v(13.37, 3.99) * mm, "end": v(13.37, 3.95) * mm});
            skLineSegment(sketch, "E614", {"start": v(13.37, 3.95) * mm, "end": v(13.37, 3.94) * mm});
            skLineSegment(sketch, "E615", {"start": v(13.37, 3.94) * mm, "end": v(13.36, 3.9) * mm});
            skLineSegment(sketch, "E616", {"start": v(13.36, 3.9) * mm, "end": v(13.33, 3.86) * mm});
            skLineSegment(sketch, "E617", {"start": v(13.33, 3.86) * mm, "end": v(13.3, 3.84) * mm});
            skLineSegment(sketch, "E618", {"start": v(13.3, 3.84) * mm, "end": v(13.26, 3.83) * mm});
            skLineSegment(sketch, "E619", {"start": v(13.26, 3.83) * mm, "end": v(13.25, 3.83) * mm});
            skLineSegment(sketch, "E620", {"start": v(13.25, 3.83) * mm, "end": v(13.09, 3.83) * mm});
            skLineSegment(sketch, "E621", {"start": v(13.09, 3.83) * mm, "end": v(12.16, 3.83) * mm});
            skLineSegment(sketch, "E622", {"start": v(12.16, 3.83) * mm, "end": v(12, 3.83) * mm});
            skLineSegment(sketch, "E623", {"start": v(12, 3.83) * mm, "end": v(12, 3.83) * mm});
            skLineSegment(sketch, "E624", {"start": v(12, 3.83) * mm, "end": v(11.96, 3.84) * mm});
            skLineSegment(sketch, "E625", {"start": v(11.96, 3.84) * mm, "end": v(11.92, 3.86) * mm});
            skLineSegment(sketch, "E626", {"start": v(11.92, 3.86) * mm, "end": v(11.89, 3.9) * mm});
            skLineSegment(sketch, "E627", {"start": v(11.89, 3.9) * mm, "end": v(11.88, 3.94) * mm});
            skLineSegment(sketch, "E628", {"start": v(11.88, 3.94) * mm, "end": v(11.88, 3.95) * mm});
            skLineSegment(sketch, "E629", {"start": v(15.21, 4.28) * mm, "end": v(15.58, 4.28) * mm});
            skLineSegment(sketch, "E630", {"start": v(15.58, 4.28) * mm, "end": v(15.58, 3.3) * mm});
            skLineSegment(sketch, "E631", {"start": v(15.58, 3.3) * mm, "end": v(15.21, 3.3) * mm});
            skLineSegment(sketch, "E632", {"start": v(15.21, 3.3) * mm, "end": v(15.21, 4.28) * mm});
            skLineSegment(sketch, "E633", {"start": v(16.11, -2.07) * mm, "end": v(15.83, -2.07) * mm});
            skLineSegment(sketch, "E634", {"start": v(15.83, -2.07) * mm, "end": v(15.83, 2.42) * mm});
            skLineSegment(sketch, "E635", {"start": v(15.83, 2.42) * mm, "end": v(16.3, 2.42) * mm});
            skLineSegment(sketch, "E636", {"start": v(16.3, 2.42) * mm, "end": v(16.32, 2.42) * mm});
            skLineSegment(sketch, "E637", {"start": v(16.32, 2.42) * mm, "end": v(16.36, 2.43) * mm});
            skLineSegment(sketch, "E638", {"start": v(16.36, 2.43) * mm, "end": v(16.4, 2.46) * mm});
            skLineSegment(sketch, "E639", {"start": v(16.4, 2.46) * mm, "end": v(16.42, 2.5) * mm});
            skLineSegment(sketch, "E640", {"start": v(16.42, 2.5) * mm, "end": v(16.43, 2.54) * mm});
            skLineSegment(sketch, "E641", {"start": v(16.43, 2.54) * mm, "end": v(16.43, 2.55) * mm});
            skLineSegment(sketch, "E642", {"start": v(16.43, 2.55) * mm, "end": v(16.43, 3.17) * mm});
            skLineSegment(sketch, "E643", {"start": v(16.43, 3.17) * mm, "end": v(16.43, 3.19) * mm});
            skLineSegment(sketch, "E644", {"start": v(16.43, 3.19) * mm, "end": v(16.42, 3.22) * mm});
            skLineSegment(sketch, "E645", {"start": v(16.42, 3.22) * mm, "end": v(16.4, 3.26) * mm});
            skLineSegment(sketch, "E646", {"start": v(16.4, 3.26) * mm, "end": v(16.36, 3.3) * mm});
            skLineSegment(sketch, "E647", {"start": v(16.36, 3.3) * mm, "end": v(16.32, 3.3) * mm});
            skLineSegment(sketch, "E648", {"start": v(16.32, 3.3) * mm, "end": v(16.3, 3.3) * mm});
            skLineSegment(sketch, "E649", {"start": v(16.3, 3.3) * mm, "end": v(15.83, 3.3) * mm});
            skLineSegment(sketch, "E650", {"start": v(15.83, 3.3) * mm, "end": v(15.83, 4.4) * mm});
            skLineSegment(sketch, "E651", {"start": v(15.83, 4.4) * mm, "end": v(15.83, 4.42) * mm});
            skLineSegment(sketch, "E652", {"start": v(15.83, 4.42) * mm, "end": v(15.82, 4.46) * mm});
            skLineSegment(sketch, "E653", {"start": v(15.82, 4.46) * mm, "end": v(15.8, 4.5) * mm});
            skLineSegment(sketch, "E654", {"start": v(15.8, 4.5) * mm, "end": v(15.76, 4.53) * mm});
            skLineSegment(sketch, "E655", {"start": v(15.76, 4.53) * mm, "end": v(15.72, 4.54) * mm});
            skLineSegment(sketch, "E656", {"start": v(15.72, 4.54) * mm, "end": v(15.7, 4.54) * mm});
            skLineSegment(sketch, "E657", {"start": v(15.7, 4.54) * mm, "end": v(15.08, 4.54) * mm});
            skLineSegment(sketch, "E658", {"start": v(15.08, 4.54) * mm, "end": v(15.07, 4.54) * mm});
            skLineSegment(sketch, "E659", {"start": v(15.07, 4.54) * mm, "end": v(15.03, 4.53) * mm});
            skLineSegment(sketch, "E660", {"start": v(15.03, 4.53) * mm, "end": v(15, 4.5) * mm});
            skLineSegment(sketch, "E661", {"start": v(15, 4.5) * mm, "end": v(14.97, 4.46) * mm});
            skLineSegment(sketch, "E662", {"start": v(14.97, 4.46) * mm, "end": v(14.96, 4.42) * mm});
            skLineSegment(sketch, "E663", {"start": v(14.96, 4.42) * mm, "end": v(14.96, 4.4) * mm});
            skLineSegment(sketch, "E664", {"start": v(14.96, 4.4) * mm, "end": v(14.96, 3.3) * mm});
            skLineSegment(sketch, "E665", {"start": v(14.96, 3.3) * mm, "end": v(13.21, 3.3) * mm});
            skLineSegment(sketch, "E666", {"start": v(13.21, 3.3) * mm, "end": v(13.21, 3.57) * mm});
            skLineSegment(sketch, "E667", {"start": v(13.21, 3.57) * mm, "end": v(13.25, 3.57) * mm});
            skLineSegment(sketch, "E668", {"start": v(13.25, 3.57) * mm, "end": v(13.28, 3.57) * mm});
            skLineSegment(sketch, "E669", {"start": v(13.28, 3.57) * mm, "end": v(13.4, 3.6) * mm});
            skLineSegment(sketch, "E670", {"start": v(13.4, 3.6) * mm, "end": v(13.51, 3.68) * mm});
            skLineSegment(sketch, "E671", {"start": v(13.51, 3.68) * mm, "end": v(13.6, 3.8) * mm});
            skLineSegment(sketch, "E672", {"start": v(13.6, 3.8) * mm, "end": v(13.62, 3.92) * mm});
            skLineSegment(sketch, "E673", {"start": v(13.62, 3.92) * mm, "end": v(13.62, 3.95) * mm});
            skLineSegment(sketch, "E674", {"start": v(13.62, 3.95) * mm, "end": v(13.62, 3.99) * mm});
            skLineSegment(sketch, "E675", {"start": v(13.62, 3.99) * mm, "end": v(13.62, 4.03) * mm});
            skLineSegment(sketch, "E676", {"start": v(13.62, 4.03) * mm, "end": v(13.6, 4.14) * mm});
            skLineSegment(sketch, "E677", {"start": v(13.6, 4.14) * mm, "end": v(13.51, 4.26) * mm});
            skLineSegment(sketch, "E678", {"start": v(13.51, 4.26) * mm, "end": v(13.4, 4.34) * mm});
            skLineSegment(sketch, "E679", {"start": v(13.4, 4.34) * mm, "end": v(13.28, 4.37) * mm});
            skLineSegment(sketch, "E680", {"start": v(13.28, 4.37) * mm, "end": v(13.25, 4.37) * mm});
            skLineSegment(sketch, "E681", {"start": v(13.25, 4.37) * mm, "end": v(12, 4.37) * mm});
            skLineSegment(sketch, "E682", {"start": v(12, 4.37) * mm, "end": v(11.97, 4.37) * mm});
            skLineSegment(sketch, "E683", {"start": v(11.97, 4.37) * mm, "end": v(11.86, 4.34) * mm});
            skLineSegment(sketch, "E684", {"start": v(11.86, 4.34) * mm, "end": v(11.74, 4.26) * mm});
            skLineSegment(sketch, "E685", {"start": v(11.74, 4.26) * mm, "end": v(11.66, 4.14) * mm});
            skLineSegment(sketch, "E686", {"start": v(11.66, 4.14) * mm, "end": v(11.63, 4.03) * mm});
            skLineSegment(sketch, "E687", {"start": v(11.63, 4.03) * mm, "end": v(11.63, 3.99) * mm});
            skLineSegment(sketch, "E688", {"start": v(11.63, 3.99) * mm, "end": v(11.63, 3.95) * mm});
            skLineSegment(sketch, "E689", {"start": v(11.63, 3.95) * mm, "end": v(11.63, 3.92) * mm});
            skLineSegment(sketch, "E690", {"start": v(11.63, 3.92) * mm, "end": v(11.66, 3.8) * mm});
            skLineSegment(sketch, "E691", {"start": v(11.66, 3.8) * mm, "end": v(11.74, 3.68) * mm});
            skLineSegment(sketch, "E692", {"start": v(11.74, 3.68) * mm, "end": v(11.86, 3.6) * mm});
            skLineSegment(sketch, "E693", {"start": v(11.86, 3.6) * mm, "end": v(11.97, 3.57) * mm});
            skLineSegment(sketch, "E694", {"start": v(11.97, 3.57) * mm, "end": v(12, 3.57) * mm});
            skLineSegment(sketch, "E695", {"start": v(12, 3.57) * mm, "end": v(12.04, 3.57) * mm});
            skLineSegment(sketch, "E696", {"start": v(12.04, 3.57) * mm, "end": v(12.04, 3.3) * mm});
            skLineSegment(sketch, "E697", {"start": v(12.04, 3.3) * mm, "end": v(10.06, 3.3) * mm});
            skLineSegment(sketch, "E698", {"start": v(10.06, 3.3) * mm, "end": v(10.04, 3.3) * mm});
            skLineSegment(sketch, "E699", {"start": v(10.04, 3.3) * mm, "end": v(10, 3.3) * mm});
            skLineSegment(sketch, "E700", {"start": v(10, 3.3) * mm, "end": v(9.97, 3.26) * mm});
            skLineSegment(sketch, "E701", {"start": v(9.97, 3.26) * mm, "end": v(9.94, 3.22) * mm});
            skLineSegment(sketch, "E702", {"start": v(9.94, 3.22) * mm, "end": v(9.93, 3.19) * mm});
            skLineSegment(sketch, "E703", {"start": v(9.93, 3.19) * mm, "end": v(9.93, 3.17) * mm});
            skLineSegment(sketch, "E704", {"start": v(9.93, 3.17) * mm, "end": v(9.93, 2.55) * mm});
            skLineSegment(sketch, "E705", {"start": v(9.93, 2.55) * mm, "end": v(9.93, 2.54) * mm});
            skLineSegment(sketch, "E706", {"start": v(9.93, 2.54) * mm, "end": v(9.94, 2.5) * mm});
            skLineSegment(sketch, "E707", {"start": v(9.94, 2.5) * mm, "end": v(9.97, 2.46) * mm});
            skLineSegment(sketch, "E708", {"start": v(9.97, 2.46) * mm, "end": v(10, 2.43) * mm});
            skLineSegment(sketch, "E709", {"start": v(10, 2.43) * mm, "end": v(10.04, 2.42) * mm});
            skLineSegment(sketch, "E710", {"start": v(10.04, 2.42) * mm, "end": v(10.06, 2.42) * mm});
            skLineSegment(sketch, "E711", {"start": v(10.06, 2.42) * mm, "end": v(12.02, 2.42) * mm});
            skLineSegment(sketch, "E712", {"start": v(12.02, 2.42) * mm, "end": v(12.01, 2.4) * mm});
            skLineSegment(sketch, "E713", {"start": v(12.01, 2.4) * mm, "end": v(11.94, 2.25) * mm});
            skLineSegment(sketch, "E714", {"start": v(11.94, 2.25) * mm, "end": v(11.82, 2.13) * mm});
            skLineSegment(sketch, "E715", {"start": v(11.82, 2.13) * mm, "end": v(11.79, 2.11) * mm});
            skLineSegment(sketch, "E716", {"start": v(11.79, 2.11) * mm, "end": v(11.7, 2.06) * mm});
            skLineSegment(sketch, "E717", {"start": v(11.7, 2.06) * mm, "end": v(11.45, 1.85) * mm});
            skLineSegment(sketch, "E718", {"start": v(11.45, 1.85) * mm, "end": v(11.21, 1.54) * mm});
            skLineSegment(sketch, "E719", {"start": v(11.21, 1.54) * mm, "end": v(11.09, 1.2) * mm});
            skLineSegment(sketch, "E720", {"start": v(11.09, 1.2) * mm, "end": v(11.05, 0.9) * mm});
            skLineSegment(sketch, "E721", {"start": v(11.05, 0.9) * mm, "end": v(11.06, 0.81) * mm});
            skLineSegment(sketch, "E722", {"start": v(11.06, 0.81) * mm, "end": v(11.07, 0.74) * mm});
            skLineSegment(sketch, "E723", {"start": v(11.07, 0.74) * mm, "end": v(11.1, 0.53) * mm});
            skLineSegment(sketch, "E724", {"start": v(11.1, 0.53) * mm, "end": v(11.2, 0.27) * mm});
            skLineSegment(sketch, "E725", {"start": v(11.2, 0.27) * mm, "end": v(11.34, 0.03) * mm});
            skLineSegment(sketch, "E726", {"start": v(11.34, 0.03) * mm, "end": v(11.52, -0.18) * mm});
            skLineSegment(sketch, "E727", {"start": v(11.52, -0.18) * mm, "end": v(11.73, -0.36) * mm});
            skLineSegment(sketch, "E728", {"start": v(11.73, -0.36) * mm, "end": v(11.97, -0.5) * mm});
            skLineSegment(sketch, "E729", {"start": v(11.97, -0.5) * mm, "end": v(12.23, -0.6) * mm});
            skLineSegment(sketch, "E730", {"start": v(12.23, -0.6) * mm, "end": v(12.44, -0.63) * mm});
            skLineSegment(sketch, "E731", {"start": v(12.44, -0.63) * mm, "end": v(12.51, -0.64) * mm});
            skLineSegment(sketch, "E732", {"start": v(12.51, -0.64) * mm, "end": v(12.52, -0.64) * mm});
            skLineSegment(sketch, "E733", {"start": v(12.52, -0.64) * mm, "end": v(12.6, -0.64) * mm});
            skLineSegment(sketch, "E734", {"start": v(12.6, -0.64) * mm, "end": v(12.63, -0.64) * mm});
            skLineSegment(sketch, "E735", {"start": v(12.63, -0.64) * mm, "end": v(12.7, -0.64) * mm});
            skLineSegment(sketch, "E736", {"start": v(12.7, -0.64) * mm, "end": v(12.92, -0.62) * mm});
            skLineSegment(sketch, "E737", {"start": v(12.92, -0.62) * mm, "end": v(13.2, -0.54) * mm});
            skLineSegment(sketch, "E738", {"start": v(13.2, -0.54) * mm, "end": v(13.46, -0.4) * mm});
            skLineSegment(sketch, "E739", {"start": v(13.46, -0.4) * mm, "end": v(13.64, -0.27) * mm});
            skLineSegment(sketch, "E740", {"start": v(13.64, -0.27) * mm, "end": v(13.7, -0.22) * mm});
            skLineSegment(sketch, "E741", {"start": v(13.7, -0.22) * mm, "end": v(13.75, -0.17) * mm});
            skLineSegment(sketch, "E742", {"start": v(13.75, -0.17) * mm, "end": v(13.9, 0.02) * mm});
            skLineSegment(sketch, "E743", {"start": v(13.9, 0.02) * mm, "end": v(14.06, 0.3) * mm});
            skLineSegment(sketch, "E744", {"start": v(14.06, 0.3) * mm, "end": v(14.16, 0.6) * mm});
            skLineSegment(sketch, "E745", {"start": v(14.16, 0.6) * mm, "end": v(14.2, 0.84) * mm});
            skLineSegment(sketch, "E746", {"start": v(14.2, 0.84) * mm, "end": v(14.2, 0.92) * mm});
            skLineSegment(sketch, "E747", {"start": v(14.2, 0.92) * mm, "end": v(14.2, 0.98) * mm});
            skLineSegment(sketch, "E748", {"start": v(14.2, 0.98) * mm, "end": v(14.17, 1.16) * mm});
            skLineSegment(sketch, "E749", {"start": v(14.17, 1.16) * mm, "end": v(14.12, 1.36) * mm});
            skLineSegment(sketch, "E750", {"start": v(14.12, 1.36) * mm, "end": v(14.04, 1.54) * mm});
            skLineSegment(sketch, "E751", {"start": v(14.04, 1.54) * mm, "end": v(13.94, 1.7) * mm});
            skLineSegment(sketch, "E752", {"start": v(13.94, 1.7) * mm, "end": v(13.82, 1.83) * mm});
            skLineSegment(sketch, "E753", {"start": v(13.82, 1.83) * mm, "end": v(13.7, 1.95) * mm});
            skLineSegment(sketch, "E754", {"start": v(13.7, 1.95) * mm, "end": v(13.57, 2.04) * mm});
            skLineSegment(sketch, "E755", {"start": v(13.57, 2.04) * mm, "end": v(13.48, 2.1) * mm});
            skLineSegment(sketch, "E756", {"start": v(13.48, 2.1) * mm, "end": v(13.45, 2.12) * mm});
            skLineSegment(sketch, "E757", {"start": v(13.45, 2.12) * mm, "end": v(13.42, 2.14) * mm});
            skLineSegment(sketch, "E758", {"start": v(13.42, 2.14) * mm, "end": v(13.3, 2.25) * mm});
            skLineSegment(sketch, "E759", {"start": v(13.3, 2.25) * mm, "end": v(13.24, 2.4) * mm});
            skLineSegment(sketch, "E760", {"start": v(13.24, 2.4) * mm, "end": v(13.23, 2.42) * mm});
            skLineSegment(sketch, "E761", {"start": v(13.23, 2.42) * mm, "end": v(14.96, 2.42) * mm});
            skLineSegment(sketch, "E762", {"start": v(14.96, 2.42) * mm, "end": v(14.96, -2.07) * mm});
            skLineSegment(sketch, "E763", {"start": v(14.96, -2.07) * mm, "end": v(10.25, -2.07) * mm});
            skLineSegment(sketch, "E764", {"start": v(10.25, -2.07) * mm, "end": v(10.19, -2.07) * mm});
            skLineSegment(sketch, "E765", {"start": v(10.19, -2.07) * mm, "end": v(9.99, -2.13) * mm});
            skLineSegment(sketch, "E766", {"start": v(9.99, -2.13) * mm, "end": v(9.77, -2.27) * mm});
            skLineSegment(sketch, "E767", {"start": v(9.77, -2.27) * mm, "end": v(9.62, -2.5) * mm});
            skLineSegment(sketch, "E768", {"start": v(9.62, -2.5) * mm, "end": v(9.57, -2.7) * mm});
            skLineSegment(sketch, "E769", {"start": v(9.57, -2.7) * mm, "end": v(9.57, -2.76) * mm});
            skLineSegment(sketch, "E770", {"start": v(9.57, -2.76) * mm, "end": v(9.57, -2.84) * mm});
            skLineSegment(sketch, "E771", {"start": v(9.57, -2.84) * mm, "end": v(9.57, -2.9) * mm});
            skLineSegment(sketch, "E772", {"start": v(9.57, -2.9) * mm, "end": v(9.62, -3.1) * mm});
            skLineSegment(sketch, "E773", {"start": v(9.62, -3.1) * mm, "end": v(9.77, -3.32) * mm});
            skLineSegment(sketch, "E774", {"start": v(9.77, -3.32) * mm, "end": v(9.99, -3.47) * mm});
            skLineSegment(sketch, "E775", {"start": v(9.99, -3.47) * mm, "end": v(10.19, -3.52) * mm});
            skLineSegment(sketch, "E776", {"start": v(10.19, -3.52) * mm, "end": v(10.25, -3.52) * mm});
            skLineSegment(sketch, "E777", {"start": v(10.25, -3.52) * mm, "end": v(16.11, -3.52) * mm});
            skLineSegment(sketch, "E778", {"start": v(16.11, -3.52) * mm, "end": v(16.18, -3.52) * mm});
            skLineSegment(sketch, "E779", {"start": v(16.18, -3.52) * mm, "end": v(16.38, -3.47) * mm});
            skLineSegment(sketch, "E780", {"start": v(16.38, -3.47) * mm, "end": v(16.6, -3.32) * mm});
            skLineSegment(sketch, "E781", {"start": v(16.6, -3.32) * mm, "end": v(16.74, -3.1) * mm});
            skLineSegment(sketch, "E782", {"start": v(16.74, -3.1) * mm, "end": v(16.8, -2.9) * mm});
            skLineSegment(sketch, "E783", {"start": v(16.8, -2.9) * mm, "end": v(16.8, -2.84) * mm});
            skLineSegment(sketch, "E784", {"start": v(16.8, -2.84) * mm, "end": v(16.8, -2.76) * mm});
            skLineSegment(sketch, "E785", {"start": v(16.8, -2.76) * mm, "end": v(16.8, -2.7) * mm});
            skLineSegment(sketch, "E786", {"start": v(16.8, -2.7) * mm, "end": v(16.74, -2.5) * mm});
            skLineSegment(sketch, "E787", {"start": v(16.74, -2.5) * mm, "end": v(16.6, -2.27) * mm});
            skLineSegment(sketch, "E788", {"start": v(16.6, -2.27) * mm, "end": v(16.38, -2.13) * mm});
            skLineSegment(sketch, "E789", {"start": v(16.38, -2.13) * mm, "end": v(16.18, -2.07) * mm});
            skLineSegment(sketch, "E790", {"start": v(16.18, -2.07) * mm, "end": v(16.11, -2.07) * mm});
            skLineSegment(sketch, "E791", {"start": v(13.42, -1.8) * mm, "end": v(13.42, -1.29) * mm});
            skLineSegment(sketch, "E792", {"start": v(13.42, -1.29) * mm, "end": v(13.42, -1.27) * mm});
            skLineSegment(sketch, "E793", {"start": v(13.42, -1.27) * mm, "end": v(13.4, -1.24) * mm});
            skLineSegment(sketch, "E794", {"start": v(13.4, -1.24) * mm, "end": v(13.38, -1.2) * mm});
            skLineSegment(sketch, "E795", {"start": v(13.38, -1.2) * mm, "end": v(13.34, -1.17) * mm});
            skLineSegment(sketch, "E796", {"start": v(13.34, -1.17) * mm, "end": v(13.3, -1.16) * mm});
            skLineSegment(sketch, "E797", {"start": v(13.3, -1.16) * mm, "end": v(13.3, -1.16) * mm});
            skLineSegment(sketch, "E798", {"start": v(13.3, -1.16) * mm, "end": v(13.28, -1.16) * mm});
            skLineSegment(sketch, "E799", {"start": v(13.28, -1.16) * mm, "end": v(13.24, -1.17) * mm});
            skLineSegment(sketch, "E800", {"start": v(13.24, -1.17) * mm, "end": v(13.2, -1.2) * mm});
            skLineSegment(sketch, "E801", {"start": v(13.2, -1.2) * mm, "end": v(13.18, -1.24) * mm});
            skLineSegment(sketch, "E802", {"start": v(13.18, -1.24) * mm, "end": v(13.17, -1.27) * mm});
            skLineSegment(sketch, "E803", {"start": v(13.17, -1.27) * mm, "end": v(13.17, -1.29) * mm});
            skLineSegment(sketch, "E804", {"start": v(13.17, -1.29) * mm, "end": v(13.17, -1.8) * mm});
            skLineSegment(sketch, "E805", {"start": v(13.17, -1.8) * mm, "end": v(13.17, -1.8) * mm});
            skLineSegment(sketch, "E806", {"start": v(13.17, -1.8) * mm, "end": v(13.18, -1.84) * mm});
            skLineSegment(sketch, "E807", {"start": v(13.18, -1.84) * mm, "end": v(13.2, -1.88) * mm});
            skLineSegment(sketch, "E808", {"start": v(13.2, -1.88) * mm, "end": v(13.24, -1.9) * mm});
            skLineSegment(sketch, "E809", {"start": v(13.24, -1.9) * mm, "end": v(13.28, -1.92) * mm});
            skLineSegment(sketch, "E810", {"start": v(13.28, -1.92) * mm, "end": v(13.3, -1.92) * mm});
            skLineSegment(sketch, "E811", {"start": v(13.3, -1.92) * mm, "end": v(13.3, -1.92) * mm});
            skLineSegment(sketch, "E812", {"start": v(13.3, -1.92) * mm, "end": v(13.34, -1.9) * mm});
            skLineSegment(sketch, "E813", {"start": v(13.34, -1.9) * mm, "end": v(13.38, -1.88) * mm});
            skLineSegment(sketch, "E814", {"start": v(13.38, -1.88) * mm, "end": v(13.4, -1.84) * mm});
            skLineSegment(sketch, "E815", {"start": v(13.4, -1.84) * mm, "end": v(13.42, -1.8) * mm});
            skLineSegment(sketch, "E816", {"start": v(13.42, -1.8) * mm, "end": v(13.42, -1.8) * mm});
            skLineSegment(sketch, "E817", {"start": v(12.75, -1.8) * mm, "end": v(12.75, -1.29) * mm});
            skLineSegment(sketch, "E818", {"start": v(12.75, -1.29) * mm, "end": v(12.75, -1.27) * mm});
            skLineSegment(sketch, "E819", {"start": v(12.75, -1.27) * mm, "end": v(12.74, -1.24) * mm});
            skLineSegment(sketch, "E820", {"start": v(12.74, -1.24) * mm, "end": v(12.71, -1.2) * mm});
            skLineSegment(sketch, "E821", {"start": v(12.71, -1.2) * mm, "end": v(12.67, -1.17) * mm});
            skLineSegment(sketch, "E822", {"start": v(12.67, -1.17) * mm, "end": v(12.64, -1.16) * mm});
            skLineSegment(sketch, "E823", {"start": v(12.64, -1.16) * mm, "end": v(12.63, -1.16) * mm});
            skLineSegment(sketch, "E824", {"start": v(12.63, -1.16) * mm, "end": v(12.61, -1.16) * mm});
            skLineSegment(sketch, "E825", {"start": v(12.61, -1.16) * mm, "end": v(12.58, -1.17) * mm});
            skLineSegment(sketch, "E826", {"start": v(12.58, -1.17) * mm, "end": v(12.54, -1.2) * mm});
            skLineSegment(sketch, "E827", {"start": v(12.54, -1.2) * mm, "end": v(12.5, -1.24) * mm});
            skLineSegment(sketch, "E828", {"start": v(12.5, -1.24) * mm, "end": v(12.5, -1.27) * mm});
            skLineSegment(sketch, "E829", {"start": v(12.5, -1.27) * mm, "end": v(12.5, -1.29) * mm});
            skLineSegment(sketch, "E830", {"start": v(12.5, -1.29) * mm, "end": v(12.5, -1.8) * mm});
            skLineSegment(sketch, "E831", {"start": v(12.5, -1.8) * mm, "end": v(12.5, -1.8) * mm});
            skLineSegment(sketch, "E832", {"start": v(12.5, -1.8) * mm, "end": v(12.5, -1.84) * mm});
            skLineSegment(sketch, "E833", {"start": v(12.5, -1.84) * mm, "end": v(12.54, -1.88) * mm});
            skLineSegment(sketch, "E834", {"start": v(12.54, -1.88) * mm, "end": v(12.58, -1.9) * mm});
            skLineSegment(sketch, "E835", {"start": v(12.58, -1.9) * mm, "end": v(12.61, -1.92) * mm});
            skLineSegment(sketch, "E836", {"start": v(12.61, -1.92) * mm, "end": v(12.63, -1.92) * mm});
            skLineSegment(sketch, "E837", {"start": v(12.63, -1.92) * mm, "end": v(12.64, -1.92) * mm});
            skLineSegment(sketch, "E838", {"start": v(12.64, -1.92) * mm, "end": v(12.67, -1.9) * mm});
            skLineSegment(sketch, "E839", {"start": v(12.67, -1.9) * mm, "end": v(12.71, -1.88) * mm});
            skLineSegment(sketch, "E840", {"start": v(12.71, -1.88) * mm, "end": v(12.74, -1.84) * mm});
            skLineSegment(sketch, "E841", {"start": v(12.74, -1.84) * mm, "end": v(12.75, -1.8) * mm});
            skLineSegment(sketch, "E842", {"start": v(12.75, -1.8) * mm, "end": v(12.75, -1.8) * mm});
            skLineSegment(sketch, "E843", {"start": v(12.08, -1.8) * mm, "end": v(12.08, -1.29) * mm});
            skLineSegment(sketch, "E844", {"start": v(12.08, -1.29) * mm, "end": v(12.08, -1.27) * mm});
            skLineSegment(sketch, "E845", {"start": v(12.08, -1.27) * mm, "end": v(12.07, -1.24) * mm});
            skLineSegment(sketch, "E846", {"start": v(12.07, -1.24) * mm, "end": v(12.05, -1.2) * mm});
            skLineSegment(sketch, "E847", {"start": v(12.05, -1.2) * mm, "end": v(12, -1.17) * mm});
            skLineSegment(sketch, "E848", {"start": v(12, -1.17) * mm, "end": v(11.97, -1.16) * mm});
            skLineSegment(sketch, "E849", {"start": v(11.97, -1.16) * mm, "end": v(11.96, -1.16) * mm});
            skLineSegment(sketch, "E850", {"start": v(11.96, -1.16) * mm, "end": v(11.95, -1.16) * mm});
            skLineSegment(sketch, "E851", {"start": v(11.95, -1.16) * mm, "end": v(11.9, -1.17) * mm});
            skLineSegment(sketch, "E852", {"start": v(11.9, -1.17) * mm, "end": v(11.87, -1.2) * mm});
            skLineSegment(sketch, "E853", {"start": v(11.87, -1.2) * mm, "end": v(11.84, -1.24) * mm});
            skLineSegment(sketch, "E854", {"start": v(11.84, -1.24) * mm, "end": v(11.83, -1.27) * mm});
            skLineSegment(sketch, "E855", {"start": v(11.83, -1.27) * mm, "end": v(11.83, -1.29) * mm});
            skLineSegment(sketch, "E856", {"start": v(11.83, -1.29) * mm, "end": v(11.83, -1.8) * mm});
            skLineSegment(sketch, "E857", {"start": v(11.83, -1.8) * mm, "end": v(11.83, -1.8) * mm});
            skLineSegment(sketch, "E858", {"start": v(11.83, -1.8) * mm, "end": v(11.84, -1.84) * mm});
            skLineSegment(sketch, "E859", {"start": v(11.84, -1.84) * mm, "end": v(11.87, -1.88) * mm});
            skLineSegment(sketch, "E860", {"start": v(11.87, -1.88) * mm, "end": v(11.9, -1.9) * mm});
            skLineSegment(sketch, "E861", {"start": v(11.9, -1.9) * mm, "end": v(11.95, -1.92) * mm});
            skLineSegment(sketch, "E862", {"start": v(11.95, -1.92) * mm, "end": v(11.96, -1.92) * mm});
            skLineSegment(sketch, "E863", {"start": v(11.96, -1.92) * mm, "end": v(11.97, -1.92) * mm});
            skLineSegment(sketch, "E864", {"start": v(11.97, -1.92) * mm, "end": v(12, -1.9) * mm});
            skLineSegment(sketch, "E865", {"start": v(12, -1.9) * mm, "end": v(12.05, -1.88) * mm});
            skLineSegment(sketch, "E866", {"start": v(12.05, -1.88) * mm, "end": v(12.07, -1.84) * mm});
            skLineSegment(sketch, "E867", {"start": v(12.07, -1.84) * mm, "end": v(12.08, -1.8) * mm});
            skLineSegment(sketch, "E868", {"start": v(12.08, -1.8) * mm, "end": v(12.08, -1.8) * mm});
            skLineSegment(sketch, "E869", {"start": v(11.94, 6.4) * mm, "end": v(12.03, 6.49) * mm});
            skLineSegment(sketch, "E870", {"start": v(12.03, 6.49) * mm, "end": v(12.97, 7.42) * mm});
            skLineSegment(sketch, "E871", {"start": v(12.97, 7.42) * mm, "end": v(13.06, 7.51) * mm});
            skLineSegment(sketch, "E872", {"start": v(13.06, 7.51) * mm, "end": v(13.15, 7.42) * mm});
            skLineSegment(sketch, "E873", {"start": v(13.15, 7.42) * mm, "end": v(14.02, 6.55) * mm});
            skLineSegment(sketch, "E874", {"start": v(14.02, 6.55) * mm, "end": v(14.11, 6.46) * mm});
            skLineSegment(sketch, "E875", {"start": v(14.11, 6.46) * mm, "end": v(14.13, 6.44) * mm});
            skLineSegment(sketch, "E876", {"start": v(14.13, 6.44) * mm, "end": v(14.22, 6.4) * mm});
            skLineSegment(sketch, "E877", {"start": v(14.22, 6.4) * mm, "end": v(14.32, 6.38) * mm});
            skLineSegment(sketch, "E878", {"start": v(14.32, 6.38) * mm, "end": v(14.43, 6.4) * mm});
            skLineSegment(sketch, "E879", {"start": v(14.43, 6.4) * mm, "end": v(14.51, 6.47) * mm});
            skLineSegment(sketch, "E880", {"start": v(14.51, 6.47) * mm, "end": v(14.58, 6.55) * mm});
            skLineSegment(sketch, "E881", {"start": v(14.58, 6.55) * mm, "end": v(14.6, 6.66) * mm});
            skLineSegment(sketch, "E882", {"start": v(14.6, 6.66) * mm, "end": v(14.59, 6.76) * mm});
            skLineSegment(sketch, "E883", {"start": v(14.59, 6.76) * mm, "end": v(14.54, 6.85) * mm});
            skLineSegment(sketch, "E884", {"start": v(14.54, 6.85) * mm, "end": v(14.52, 6.87) * mm});
            skLineSegment(sketch, "E885", {"start": v(14.52, 6.87) * mm, "end": v(14.42, 6.97) * mm});
            skLineSegment(sketch, "E886", {"start": v(14.42, 6.97) * mm, "end": v(13.37, 8.02) * mm});
            skLineSegment(sketch, "E887", {"start": v(13.37, 8.02) * mm, "end": v(13.26, 8.13) * mm});
            skLineSegment(sketch, "E888", {"start": v(13.26, 8.13) * mm, "end": v(13.24, 8.15) * mm});
            skLineSegment(sketch, "E889", {"start": v(13.24, 8.15) * mm, "end": v(13.17, 8.19) * mm});
            skLineSegment(sketch, "E890", {"start": v(13.17, 8.19) * mm, "end": v(13.06, 8.2) * mm});
            skLineSegment(sketch, "E891", {"start": v(13.06, 8.2) * mm, "end": v(12.95, 8.19) * mm});
            skLineSegment(sketch, "E892", {"start": v(12.95, 8.19) * mm, "end": v(12.87, 8.15) * mm});
            skLineSegment(sketch, "E893", {"start": v(12.87, 8.15) * mm, "end": v(12.86, 8.13) * mm});
            skLineSegment(sketch, "E894", {"start": v(12.86, 8.13) * mm, "end": v(12.74, 8.02) * mm});
            skLineSegment(sketch, "E895", {"start": v(12.74, 8.02) * mm, "end": v(11.64, 6.91) * mm});
            skLineSegment(sketch, "E896", {"start": v(11.64, 6.91) * mm, "end": v(11.53, 6.8) * mm});
            skLineSegment(sketch, "E897", {"start": v(11.53, 6.8) * mm, "end": v(11.5, 6.78) * mm});
            skLineSegment(sketch, "E898", {"start": v(11.5, 6.78) * mm, "end": v(11.46, 6.7) * mm});
            skLineSegment(sketch, "E899", {"start": v(11.46, 6.7) * mm, "end": v(11.45, 6.59) * mm});
            skLineSegment(sketch, "E900", {"start": v(11.45, 6.59) * mm, "end": v(11.47, 6.49) * mm});
            skLineSegment(sketch, "E901", {"start": v(11.47, 6.49) * mm, "end": v(11.54, 6.4) * mm});
            skLineSegment(sketch, "E902", {"start": v(11.54, 6.4) * mm, "end": v(11.62, 6.34) * mm});
            skLineSegment(sketch, "E903", {"start": v(11.62, 6.34) * mm, "end": v(11.73, 6.3) * mm});
            skLineSegment(sketch, "E904", {"start": v(11.73, 6.3) * mm, "end": v(11.83, 6.32) * mm});
            skLineSegment(sketch, "E905", {"start": v(11.83, 6.32) * mm, "end": v(11.92, 6.37) * mm});
            skLineSegment(sketch, "E906", {"start": v(11.92, 6.37) * mm, "end": v(11.94, 6.4) * mm});
            skLineSegment(sketch, "E907", {"start": v(6.83, 5.81) * mm, "end": v(6.88, 5.81) * mm});
            skLineSegment(sketch, "E908", {"start": v(6.88, 5.81) * mm, "end": v(7.03, 5.83) * mm});
            skLineSegment(sketch, "E909", {"start": v(7.03, 5.83) * mm, "end": v(7.22, 5.9) * mm});
            skLineSegment(sketch, "E910", {"start": v(7.22, 5.9) * mm, "end": v(7.4, 5.99) * mm});
            skLineSegment(sketch, "E911", {"start": v(7.4, 5.99) * mm, "end": v(7.55, 6.11) * mm});
            skLineSegment(sketch, "E912", {"start": v(7.55, 6.11) * mm, "end": v(7.67, 6.26) * mm});
            skLineSegment(sketch, "E913", {"start": v(7.67, 6.26) * mm, "end": v(7.76, 6.43) * mm});
            skLineSegment(sketch, "E914", {"start": v(7.76, 6.43) * mm, "end": v(7.82, 6.62) * mm});
            skLineSegment(sketch, "E915", {"start": v(7.82, 6.62) * mm, "end": v(7.84, 6.78) * mm});
            skLineSegment(sketch, "E916", {"start": v(7.84, 6.78) * mm, "end": v(7.84, 6.83) * mm});
            skLineSegment(sketch, "E917", {"start": v(7.84, 6.83) * mm, "end": v(7.84, 6.88) * mm});
            skLineSegment(sketch, "E918", {"start": v(7.84, 6.88) * mm, "end": v(7.82, 7.03) * mm});
            skLineSegment(sketch, "E919", {"start": v(7.82, 7.03) * mm, "end": v(7.76, 7.22) * mm});
            skLineSegment(sketch, "E920", {"start": v(7.76, 7.22) * mm, "end": v(7.67, 7.4) * mm});
            skLineSegment(sketch, "E921", {"start": v(7.67, 7.4) * mm, "end": v(7.55, 7.54) * mm});
            skLineSegment(sketch, "E922", {"start": v(7.55, 7.54) * mm, "end": v(7.4, 7.67) * mm});
            skLineSegment(sketch, "E923", {"start": v(7.4, 7.67) * mm, "end": v(7.22, 7.76) * mm});
            skLineSegment(sketch, "E924", {"start": v(7.22, 7.76) * mm, "end": v(7.03, 7.82) * mm});
            skLineSegment(sketch, "E925", {"start": v(7.03, 7.82) * mm, "end": v(6.88, 7.84) * mm});
            skLineSegment(sketch, "E926", {"start": v(6.88, 7.84) * mm, "end": v(6.83, 7.84) * mm});
            skLineSegment(sketch, "E927", {"start": v(6.83, 7.84) * mm, "end": v(6.78, 7.84) * mm});
            skLineSegment(sketch, "E928", {"start": v(6.78, 7.84) * mm, "end": v(6.63, 7.82) * mm});
            skLineSegment(sketch, "E929", {"start": v(6.63, 7.82) * mm, "end": v(6.44, 7.76) * mm});
            skLineSegment(sketch, "E930", {"start": v(6.44, 7.76) * mm, "end": v(6.26, 7.67) * mm});
            skLineSegment(sketch, "E931", {"start": v(6.26, 7.67) * mm, "end": v(6.11, 7.54) * mm});
            skLineSegment(sketch, "E932", {"start": v(6.11, 7.54) * mm, "end": v(6, 7.4) * mm});
            skLineSegment(sketch, "E933", {"start": v(6, 7.4) * mm, "end": v(5.9, 7.22) * mm});
            skLineSegment(sketch, "E934", {"start": v(5.9, 7.22) * mm, "end": v(5.84, 7.03) * mm});
            skLineSegment(sketch, "E935", {"start": v(5.84, 7.03) * mm, "end": v(5.82, 6.88) * mm});
            skLineSegment(sketch, "E936", {"start": v(5.82, 6.88) * mm, "end": v(5.82, 6.83) * mm});
            skLineSegment(sketch, "E937", {"start": v(5.82, 6.83) * mm, "end": v(5.82, 6.78) * mm});
            skLineSegment(sketch, "E938", {"start": v(5.82, 6.78) * mm, "end": v(5.84, 6.62) * mm});
            skLineSegment(sketch, "E939", {"start": v(5.84, 6.62) * mm, "end": v(5.9, 6.43) * mm});
            skLineSegment(sketch, "E940", {"start": v(5.9, 6.43) * mm, "end": v(6, 6.26) * mm});
            skLineSegment(sketch, "E941", {"start": v(6, 6.26) * mm, "end": v(6.11, 6.11) * mm});
            skLineSegment(sketch, "E942", {"start": v(6.11, 6.11) * mm, "end": v(6.26, 5.99) * mm});
            skLineSegment(sketch, "E943", {"start": v(6.26, 5.99) * mm, "end": v(6.44, 5.9) * mm});
            skLineSegment(sketch, "E944", {"start": v(6.44, 5.9) * mm, "end": v(6.63, 5.83) * mm});
            skLineSegment(sketch, "E945", {"start": v(6.63, 5.83) * mm, "end": v(6.78, 5.81) * mm});
            skLineSegment(sketch, "E946", {"start": v(6.78, 5.81) * mm, "end": v(6.83, 5.81) * mm});
            skLineSegment(sketch, "E947", {"start": v(19.72, 5.81) * mm, "end": v(19.77, 5.81) * mm});
            skLineSegment(sketch, "E948", {"start": v(19.77, 5.81) * mm, "end": v(19.93, 5.83) * mm});
            skLineSegment(sketch, "E949", {"start": v(19.93, 5.83) * mm, "end": v(20.12, 5.9) * mm});
            skLineSegment(sketch, "E950", {"start": v(20.12, 5.9) * mm, "end": v(20.29, 5.99) * mm});
            skLineSegment(sketch, "E951", {"start": v(20.29, 5.99) * mm, "end": v(20.44, 6.11) * mm});
            skLineSegment(sketch, "E952", {"start": v(20.44, 6.11) * mm, "end": v(20.56, 6.26) * mm});
            skLineSegment(sketch, "E953", {"start": v(20.56, 6.26) * mm, "end": v(20.65, 6.43) * mm});
            skLineSegment(sketch, "E954", {"start": v(20.65, 6.43) * mm, "end": v(20.71, 6.62) * mm});
            skLineSegment(sketch, "E955", {"start": v(20.71, 6.62) * mm, "end": v(20.73, 6.78) * mm});
            skLineSegment(sketch, "E956", {"start": v(20.73, 6.78) * mm, "end": v(20.73, 6.83) * mm});
            skLineSegment(sketch, "E957", {"start": v(20.73, 6.83) * mm, "end": v(20.73, 6.88) * mm});
            skLineSegment(sketch, "E958", {"start": v(20.73, 6.88) * mm, "end": v(20.71, 7.03) * mm});
            skLineSegment(sketch, "E959", {"start": v(20.71, 7.03) * mm, "end": v(20.65, 7.22) * mm});
            skLineSegment(sketch, "E960", {"start": v(20.65, 7.22) * mm, "end": v(20.56, 7.4) * mm});
            skLineSegment(sketch, "E961", {"start": v(20.56, 7.4) * mm, "end": v(20.44, 7.54) * mm});
            skLineSegment(sketch, "E962", {"start": v(20.44, 7.54) * mm, "end": v(20.29, 7.67) * mm});
            skLineSegment(sketch, "E963", {"start": v(20.29, 7.67) * mm, "end": v(20.12, 7.76) * mm});
            skLineSegment(sketch, "E964", {"start": v(20.12, 7.76) * mm, "end": v(19.93, 7.82) * mm});
            skLineSegment(sketch, "E965", {"start": v(19.93, 7.82) * mm, "end": v(19.77, 7.84) * mm});
            skLineSegment(sketch, "E966", {"start": v(19.77, 7.84) * mm, "end": v(19.72, 7.84) * mm});
            skLineSegment(sketch, "E967", {"start": v(19.72, 7.84) * mm, "end": v(19.67, 7.84) * mm});
            skLineSegment(sketch, "E968", {"start": v(19.67, 7.84) * mm, "end": v(19.52, 7.82) * mm});
            skLineSegment(sketch, "E969", {"start": v(19.52, 7.82) * mm, "end": v(19.33, 7.76) * mm});
            skLineSegment(sketch, "E970", {"start": v(19.33, 7.76) * mm, "end": v(19.16, 7.67) * mm});
            skLineSegment(sketch, "E971", {"start": v(19.16, 7.67) * mm, "end": v(19, 7.54) * mm});
            skLineSegment(sketch, "E972", {"start": v(19, 7.54) * mm, "end": v(18.88, 7.4) * mm});
            skLineSegment(sketch, "E973", {"start": v(18.88, 7.4) * mm, "end": v(18.79, 7.22) * mm});
            skLineSegment(sketch, "E974", {"start": v(18.79, 7.22) * mm, "end": v(18.73, 7.03) * mm});
            skLineSegment(sketch, "E975", {"start": v(18.73, 7.03) * mm, "end": v(18.71, 6.88) * mm});
            skLineSegment(sketch, "E976", {"start": v(18.71, 6.88) * mm, "end": v(18.71, 6.83) * mm});
            skLineSegment(sketch, "E977", {"start": v(18.71, 6.83) * mm, "end": v(18.71, 6.78) * mm});
            skLineSegment(sketch, "E978", {"start": v(18.71, 6.78) * mm, "end": v(18.73, 6.62) * mm});
            skLineSegment(sketch, "E979", {"start": v(18.73, 6.62) * mm, "end": v(18.79, 6.43) * mm});
            skLineSegment(sketch, "E980", {"start": v(18.79, 6.43) * mm, "end": v(18.88, 6.26) * mm});
            skLineSegment(sketch, "E981", {"start": v(18.88, 6.26) * mm, "end": v(19, 6.11) * mm});
            skLineSegment(sketch, "E982", {"start": v(19, 6.11) * mm, "end": v(19.16, 5.99) * mm});
            skLineSegment(sketch, "E983", {"start": v(19.16, 5.99) * mm, "end": v(19.33, 5.9) * mm});
            skLineSegment(sketch, "E984", {"start": v(19.33, 5.9) * mm, "end": v(19.52, 5.83) * mm});
            skLineSegment(sketch, "E985", {"start": v(19.52, 5.83) * mm, "end": v(19.67, 5.81) * mm});
            skLineSegment(sketch, "E986", {"start": v(19.67, 5.81) * mm, "end": v(19.72, 5.81) * mm});
            skLineSegment(sketch, "E987", {"start": v(19.72, -5.14) * mm, "end": v(19.67, -5.14) * mm});
            skLineSegment(sketch, "E988", {"start": v(19.67, -5.14) * mm, "end": v(19.52, -5.16) * mm});
            skLineSegment(sketch, "E989", {"start": v(19.52, -5.16) * mm, "end": v(19.33, -5.22) * mm});
            skLineSegment(sketch, "E990", {"start": v(19.33, -5.22) * mm, "end": v(19.16, -5.31) * mm});
            skLineSegment(sketch, "E991", {"start": v(19.16, -5.31) * mm, "end": v(19, -5.44) * mm});
            skLineSegment(sketch, "E992", {"start": v(19, -5.44) * mm, "end": v(18.88, -5.59) * mm});
            skLineSegment(sketch, "E993", {"start": v(18.88, -5.59) * mm, "end": v(18.79, -5.76) * mm});
            skLineSegment(sketch, "E994", {"start": v(18.79, -5.76) * mm, "end": v(18.73, -5.95) * mm});
            skLineSegment(sketch, "E995", {"start": v(18.73, -5.95) * mm, "end": v(18.71, -6.1) * mm});
            skLineSegment(sketch, "E996", {"start": v(18.71, -6.1) * mm, "end": v(18.71, -6.15) * mm});
            skLineSegment(sketch, "E997", {"start": v(18.71, -6.15) * mm, "end": v(18.71, -6.2) * mm});
            skLineSegment(sketch, "E998", {"start": v(18.71, -6.2) * mm, "end": v(18.73, -6.36) * mm});
            skLineSegment(sketch, "E999", {"start": v(18.73, -6.36) * mm, "end": v(18.79, -6.55) * mm});
            skLineSegment(sketch, "E1000", {"start": v(18.79, -6.55) * mm, "end": v(18.88, -6.72) * mm});
            skLineSegment(sketch, "E1001", {"start": v(18.88, -6.72) * mm, "end": v(19, -6.87) * mm});
            skLineSegment(sketch, "E1002", {"start": v(19, -6.87) * mm, "end": v(19.16, -7) * mm});
            skLineSegment(sketch, "E1003", {"start": v(19.16, -7) * mm, "end": v(19.33, -7.08) * mm});
            skLineSegment(sketch, "E1004", {"start": v(19.33, -7.08) * mm, "end": v(19.52, -7.14) * mm});
            skLineSegment(sketch, "E1005", {"start": v(19.52, -7.14) * mm, "end": v(19.67, -7.16) * mm});
            skLineSegment(sketch, "E1006", {"start": v(19.67, -7.16) * mm, "end": v(19.72, -7.16) * mm});
            skLineSegment(sketch, "E1007", {"start": v(19.72, -7.16) * mm, "end": v(19.77, -7.16) * mm});
            skLineSegment(sketch, "E1008", {"start": v(19.77, -7.16) * mm, "end": v(19.93, -7.14) * mm});
            skLineSegment(sketch, "E1009", {"start": v(19.93, -7.14) * mm, "end": v(20.12, -7.08) * mm});
            skLineSegment(sketch, "E1010", {"start": v(20.12, -7.08) * mm, "end": v(20.29, -7) * mm});
            skLineSegment(sketch, "E1011", {"start": v(20.29, -7) * mm, "end": v(20.44, -6.87) * mm});
            skLineSegment(sketch, "E1012", {"start": v(20.44, -6.87) * mm, "end": v(20.56, -6.72) * mm});
            skLineSegment(sketch, "E1013", {"start": v(20.56, -6.72) * mm, "end": v(20.65, -6.55) * mm});
            skLineSegment(sketch, "E1014", {"start": v(20.65, -6.55) * mm, "end": v(20.71, -6.36) * mm});
            skLineSegment(sketch, "E1015", {"start": v(20.71, -6.36) * mm, "end": v(20.73, -6.2) * mm});
            skLineSegment(sketch, "E1016", {"start": v(20.73, -6.2) * mm, "end": v(20.73, -6.15) * mm});
            skLineSegment(sketch, "E1017", {"start": v(20.73, -6.15) * mm, "end": v(20.73, -6.1) * mm});
            skLineSegment(sketch, "E1018", {"start": v(20.73, -6.1) * mm, "end": v(20.71, -5.95) * mm});
            skLineSegment(sketch, "E1019", {"start": v(20.71, -5.95) * mm, "end": v(20.65, -5.76) * mm});
            skLineSegment(sketch, "E1020", {"start": v(20.65, -5.76) * mm, "end": v(20.56, -5.59) * mm});
            skLineSegment(sketch, "E1021", {"start": v(20.56, -5.59) * mm, "end": v(20.44, -5.44) * mm});
            skLineSegment(sketch, "E1022", {"start": v(20.44, -5.44) * mm, "end": v(20.29, -5.31) * mm});
            skLineSegment(sketch, "E1023", {"start": v(20.29, -5.31) * mm, "end": v(20.12, -5.22) * mm});
            skLineSegment(sketch, "E1024", {"start": v(20.12, -5.22) * mm, "end": v(19.93, -5.16) * mm});
            skLineSegment(sketch, "E1025", {"start": v(19.93, -5.16) * mm, "end": v(19.77, -5.14) * mm});
            skLineSegment(sketch, "E1026", {"start": v(19.77, -5.14) * mm, "end": v(19.72, -5.14) * mm});
            skLineSegment(sketch, "E1027", {"start": v(13.34, -6.4) * mm, "end": v(13.32, -6.37) * mm});
            skLineSegment(sketch, "E1028", {"start": v(13.32, -6.37) * mm, "end": v(13.24, -6.33) * mm});
            skLineSegment(sketch, "E1029", {"start": v(13.24, -6.33) * mm, "end": v(13.13, -6.3) * mm});
            skLineSegment(sketch, "E1030", {"start": v(13.13, -6.3) * mm, "end": v(13.02, -6.33) * mm});
            skLineSegment(sketch, "E1031", {"start": v(13.02, -6.33) * mm, "end": v(12.95, -6.37) * mm});
            skLineSegment(sketch, "E1032", {"start": v(12.95, -6.37) * mm, "end": v(12.93, -6.4) * mm});
            skLineSegment(sketch, "E1033", {"start": v(12.93, -6.4) * mm, "end": v(12.82, -6.5) * mm});
            skLineSegment(sketch, "E1034", {"start": v(12.82, -6.5) * mm, "end": v(11.71, -7.6) * mm});
            skLineSegment(sketch, "E1035", {"start": v(11.71, -7.6) * mm, "end": v(11.6, -7.72) * mm});
            skLineSegment(sketch, "E1036", {"start": v(11.6, -7.72) * mm, "end": v(11.58, -7.74) * mm});
            skLineSegment(sketch, "E1037", {"start": v(11.58, -7.74) * mm, "end": v(11.54, -7.82) * mm});
            skLineSegment(sketch, "E1038", {"start": v(11.54, -7.82) * mm, "end": v(11.52, -7.93) * mm});
            skLineSegment(sketch, "E1039", {"start": v(11.52, -7.93) * mm, "end": v(11.55, -8.03) * mm});
            skLineSegment(sketch, "E1040", {"start": v(11.55, -8.03) * mm, "end": v(11.61, -8.12) * mm});
            skLineSegment(sketch, "E1041", {"start": v(11.61, -8.12) * mm, "end": v(11.7, -8.18) * mm});
            skLineSegment(sketch, "E1042", {"start": v(11.7, -8.18) * mm, "end": v(11.8, -8.2) * mm});
            skLineSegment(sketch, "E1043", {"start": v(11.8, -8.2) * mm, "end": v(11.9, -8.2) * mm});
            skLineSegment(sketch, "E1044", {"start": v(11.9, -8.2) * mm, "end": v(12, -8.15) * mm});
            skLineSegment(sketch, "E1045", {"start": v(12, -8.15) * mm, "end": v(12.01, -8.12) * mm});
            skLineSegment(sketch, "E1046", {"start": v(12.01, -8.12) * mm, "end": v(12.1, -8.03) * mm});
            skLineSegment(sketch, "E1047", {"start": v(12.1, -8.03) * mm, "end": v(13.04, -7.1) * mm});
            skLineSegment(sketch, "E1048", {"start": v(13.04, -7.1) * mm, "end": v(13.13, -7) * mm});
            skLineSegment(sketch, "E1049", {"start": v(13.13, -7) * mm, "end": v(13.22, -7.1) * mm});
            skLineSegment(sketch, "E1050", {"start": v(13.22, -7.1) * mm, "end": v(14.1, -7.97) * mm});
            skLineSegment(sketch, "E1051", {"start": v(14.1, -7.97) * mm, "end": v(14.19, -8.06) * mm});
            skLineSegment(sketch, "E1052", {"start": v(14.19, -8.06) * mm, "end": v(14.2, -8.08) * mm});
            skLineSegment(sketch, "E1053", {"start": v(14.2, -8.08) * mm, "end": v(14.3, -8.13) * mm});
            skLineSegment(sketch, "E1054", {"start": v(14.3, -8.13) * mm, "end": v(14.4, -8.14) * mm});
            skLineSegment(sketch, "E1055", {"start": v(14.4, -8.14) * mm, "end": v(14.5, -8.11) * mm});
            skLineSegment(sketch, "E1056", {"start": v(14.5, -8.11) * mm, "end": v(14.59, -8.05) * mm});
            skLineSegment(sketch, "E1057", {"start": v(14.59, -8.05) * mm, "end": v(14.65, -7.96) * mm});
            skLineSegment(sketch, "E1058", {"start": v(14.65, -7.96) * mm, "end": v(14.68, -7.86) * mm});
            skLineSegment(sketch, "E1059", {"start": v(14.68, -7.86) * mm, "end": v(14.66, -7.75) * mm});
            skLineSegment(sketch, "E1060", {"start": v(14.66, -7.75) * mm, "end": v(14.62, -7.67) * mm});
            skLineSegment(sketch, "E1061", {"start": v(14.62, -7.67) * mm, "end": v(14.6, -7.65) * mm});
            skLineSegment(sketch, "E1062", {"start": v(14.6, -7.65) * mm, "end": v(13.34, -6.4) * mm});
            skLineSegment(sketch, "E1063", {"start": v(12.01, -6.53) * mm, "end": v(12.1, -6.44) * mm});
            skLineSegment(sketch, "E1064", {"start": v(12.1, -6.44) * mm, "end": v(13.04, -5.5) * mm});
            skLineSegment(sketch, "E1065", {"start": v(13.04, -5.5) * mm, "end": v(13.13, -5.41) * mm});
            skLineSegment(sketch, "E1066", {"start": v(13.13, -5.41) * mm, "end": v(13.22, -5.5) * mm});
            skLineSegment(sketch, "E1067", {"start": v(13.22, -5.5) * mm, "end": v(14.1, -6.38) * mm});
            skLineSegment(sketch, "E1068", {"start": v(14.1, -6.38) * mm, "end": v(14.19, -6.46) * mm});
            skLineSegment(sketch, "E1069", {"start": v(14.19, -6.46) * mm, "end": v(14.2, -6.49) * mm});
            skLineSegment(sketch, "E1070", {"start": v(14.2, -6.49) * mm, "end": v(14.3, -6.53) * mm});
            skLineSegment(sketch, "E1071", {"start": v(14.3, -6.53) * mm, "end": v(14.4, -6.55) * mm});
            skLineSegment(sketch, "E1072", {"start": v(14.4, -6.55) * mm, "end": v(14.5, -6.52) * mm});
            skLineSegment(sketch, "E1073", {"start": v(14.5, -6.52) * mm, "end": v(14.59, -6.46) * mm});
            skLineSegment(sketch, "E1074", {"start": v(14.59, -6.46) * mm, "end": v(14.65, -6.37) * mm});
            skLineSegment(sketch, "E1075", {"start": v(14.65, -6.37) * mm, "end": v(14.68, -6.27) * mm});
            skLineSegment(sketch, "E1076", {"start": v(14.68, -6.27) * mm, "end": v(14.66, -6.16) * mm});
            skLineSegment(sketch, "E1077", {"start": v(14.66, -6.16) * mm, "end": v(14.62, -6.08) * mm});
            skLineSegment(sketch, "E1078", {"start": v(14.62, -6.08) * mm, "end": v(14.6, -6.06) * mm});
            skLineSegment(sketch, "E1079", {"start": v(14.6, -6.06) * mm, "end": v(14.5, -5.95) * mm});
            skLineSegment(sketch, "E1080", {"start": v(14.5, -5.95) * mm, "end": v(13.44, -4.9) * mm});
            skLineSegment(sketch, "E1081", {"start": v(13.44, -4.9) * mm, "end": v(13.34, -4.8) * mm});
            skLineSegment(sketch, "E1082", {"start": v(13.34, -4.8) * mm, "end": v(13.32, -4.78) * mm});
            skLineSegment(sketch, "E1083", {"start": v(13.32, -4.78) * mm, "end": v(13.24, -4.74) * mm});
            skLineSegment(sketch, "E1084", {"start": v(13.24, -4.74) * mm, "end": v(13.13, -4.72) * mm});
            skLineSegment(sketch, "E1085", {"start": v(13.13, -4.72) * mm, "end": v(13.02, -4.74) * mm});
            skLineSegment(sketch, "E1086", {"start": v(13.02, -4.74) * mm, "end": v(12.95, -4.78) * mm});
            skLineSegment(sketch, "E1087", {"start": v(12.95, -4.78) * mm, "end": v(12.93, -4.8) * mm});
            skLineSegment(sketch, "E1088", {"start": v(12.93, -4.8) * mm, "end": v(12.82, -4.9) * mm});
            skLineSegment(sketch, "E1089", {"start": v(12.82, -4.9) * mm, "end": v(11.71, -6.01) * mm});
            skLineSegment(sketch, "E1090", {"start": v(11.71, -6.01) * mm, "end": v(11.6, -6.12) * mm});
            skLineSegment(sketch, "E1091", {"start": v(11.6, -6.12) * mm, "end": v(11.58, -6.14) * mm});
            skLineSegment(sketch, "E1092", {"start": v(11.58, -6.14) * mm, "end": v(11.54, -6.23) * mm});
            skLineSegment(sketch, "E1093", {"start": v(11.54, -6.23) * mm, "end": v(11.52, -6.34) * mm});
            skLineSegment(sketch, "E1094", {"start": v(11.52, -6.34) * mm, "end": v(11.55, -6.44) * mm});
            skLineSegment(sketch, "E1095", {"start": v(11.55, -6.44) * mm, "end": v(11.61, -6.53) * mm});
            skLineSegment(sketch, "E1096", {"start": v(11.61, -6.53) * mm, "end": v(11.7, -6.59) * mm});
            skLineSegment(sketch, "E1097", {"start": v(11.7, -6.59) * mm, "end": v(11.8, -6.62) * mm});
            skLineSegment(sketch, "E1098", {"start": v(11.8, -6.62) * mm, "end": v(11.9, -6.6) * mm});
            skLineSegment(sketch, "E1099", {"start": v(11.9, -6.6) * mm, "end": v(12, -6.55) * mm});
            skLineSegment(sketch, "E1100", {"start": v(12, -6.55) * mm, "end": v(12.01, -6.53) * mm});
            skLineSegment(sketch, "E1101", {"start": v(6.2, 0.52) * mm, "end": v(6.08, 0.63) * mm});
            skLineSegment(sketch, "E1102", {"start": v(6.08, 0.63) * mm, "end": v(4.98, 1.73) * mm});
            skLineSegment(sketch, "E1103", {"start": v(4.98, 1.73) * mm, "end": v(4.87, 1.84) * mm});
            skLineSegment(sketch, "E1104", {"start": v(4.87, 1.84) * mm, "end": v(4.84, 1.87) * mm});
            skLineSegment(sketch, "E1105", {"start": v(4.84, 1.87) * mm, "end": v(4.76, 1.91) * mm});
            skLineSegment(sketch, "E1106", {"start": v(4.76, 1.91) * mm, "end": v(4.65, 1.93) * mm});
            skLineSegment(sketch, "E1107", {"start": v(4.65, 1.93) * mm, "end": v(4.55, 1.9) * mm});
            skLineSegment(sketch, "E1108", {"start": v(4.55, 1.9) * mm, "end": v(4.46, 1.84) * mm});
            skLineSegment(sketch, "E1109", {"start": v(4.46, 1.84) * mm, "end": v(4.4, 1.75) * mm});
            skLineSegment(sketch, "E1110", {"start": v(4.4, 1.75) * mm, "end": v(4.37, 1.65) * mm});
            skLineSegment(sketch, "E1111", {"start": v(4.37, 1.65) * mm, "end": v(4.39, 1.54) * mm});
            skLineSegment(sketch, "E1112", {"start": v(4.39, 1.54) * mm, "end": v(4.44, 1.46) * mm});
            skLineSegment(sketch, "E1113", {"start": v(4.44, 1.46) * mm, "end": v(4.46, 1.44) * mm});
            skLineSegment(sketch, "E1114", {"start": v(4.46, 1.44) * mm, "end": v(4.55, 1.34) * mm});
            skLineSegment(sketch, "E1115", {"start": v(4.55, 1.34) * mm, "end": v(5.49, 0.4) * mm});
            skLineSegment(sketch, "E1116", {"start": v(5.49, 0.4) * mm, "end": v(5.58, 0.32) * mm});
            skLineSegment(sketch, "E1117", {"start": v(5.58, 0.32) * mm, "end": v(5.5, 0.23) * mm});
            skLineSegment(sketch, "E1118", {"start": v(5.5, 0.23) * mm, "end": v(4.61, -0.65) * mm});
            skLineSegment(sketch, "E1119", {"start": v(4.61, -0.65) * mm, "end": v(4.53, -0.74) * mm});
            skLineSegment(sketch, "E1120", {"start": v(4.53, -0.74) * mm, "end": v(4.5, -0.76) * mm});
            skLineSegment(sketch, "E1121", {"start": v(4.5, -0.76) * mm, "end": v(4.46, -0.84) * mm});
            skLineSegment(sketch, "E1122", {"start": v(4.46, -0.84) * mm, "end": v(4.44, -0.95) * mm});
            skLineSegment(sketch, "E1123", {"start": v(4.44, -0.95) * mm, "end": v(4.47, -1.05) * mm});
            skLineSegment(sketch, "E1124", {"start": v(4.47, -1.05) * mm, "end": v(4.53, -1.14) * mm});
            skLineSegment(sketch, "E1125", {"start": v(4.53, -1.14) * mm, "end": v(4.62, -1.2) * mm});
            skLineSegment(sketch, "E1126", {"start": v(4.62, -1.2) * mm, "end": v(4.72, -1.23) * mm});
            skLineSegment(sketch, "E1127", {"start": v(4.72, -1.23) * mm, "end": v(4.83, -1.22) * mm});
            skLineSegment(sketch, "E1128", {"start": v(4.83, -1.22) * mm, "end": v(4.91, -1.17) * mm});
            skLineSegment(sketch, "E1129", {"start": v(4.91, -1.17) * mm, "end": v(4.93, -1.15) * mm});
            skLineSegment(sketch, "E1130", {"start": v(4.93, -1.15) * mm, "end": v(5.04, -1.04) * mm});
            skLineSegment(sketch, "E1131", {"start": v(5.04, -1.04) * mm, "end": v(6.09, 0) * mm});
            skLineSegment(sketch, "E1132", {"start": v(6.09, 0) * mm, "end": v(6.2, 0.11) * mm});
            skLineSegment(sketch, "E1133", {"start": v(6.2, 0.11) * mm, "end": v(6.21, 0.13) * mm});
            skLineSegment(sketch, "E1134", {"start": v(6.21, 0.13) * mm, "end": v(6.25, 0.2) * mm});
            skLineSegment(sketch, "E1135", {"start": v(6.25, 0.2) * mm, "end": v(6.27, 0.32) * mm});
            skLineSegment(sketch, "E1136", {"start": v(6.27, 0.32) * mm, "end": v(6.25, 0.42) * mm});
            skLineSegment(sketch, "E1137", {"start": v(6.25, 0.42) * mm, "end": v(6.21, 0.5) * mm});
            skLineSegment(sketch, "E1138", {"start": v(6.21, 0.5) * mm, "end": v(6.2, 0.52) * mm});
            skLineSegment(sketch, "E1139", {"start": v(6.46, 1.84) * mm, "end": v(6.44, 1.87) * mm});
            skLineSegment(sketch, "E1140", {"start": v(6.44, 1.87) * mm, "end": v(6.35, 1.91) * mm});
            skLineSegment(sketch, "E1141", {"start": v(6.35, 1.91) * mm, "end": v(6.25, 1.93) * mm});
            skLineSegment(sketch, "E1142", {"start": v(6.25, 1.93) * mm, "end": v(6.14, 1.9) * mm});
            skLineSegment(sketch, "E1143", {"start": v(6.14, 1.9) * mm, "end": v(6.06, 1.84) * mm});
            skLineSegment(sketch, "E1144", {"start": v(6.06, 1.84) * mm, "end": v(6, 1.75) * mm});
            skLineSegment(sketch, "E1145", {"start": v(6, 1.75) * mm, "end": v(5.97, 1.65) * mm});
            skLineSegment(sketch, "E1146", {"start": v(5.97, 1.65) * mm, "end": v(5.98, 1.54) * mm});
            skLineSegment(sketch, "E1147", {"start": v(5.98, 1.54) * mm, "end": v(6.03, 1.46) * mm});
            skLineSegment(sketch, "E1148", {"start": v(6.03, 1.46) * mm, "end": v(6.05, 1.44) * mm});
            skLineSegment(sketch, "E1149", {"start": v(6.05, 1.44) * mm, "end": v(6.14, 1.34) * mm});
            skLineSegment(sketch, "E1150", {"start": v(6.14, 1.34) * mm, "end": v(7.08, 0.4) * mm});
            skLineSegment(sketch, "E1151", {"start": v(7.08, 0.4) * mm, "end": v(7.17, 0.32) * mm});
            skLineSegment(sketch, "E1152", {"start": v(7.17, 0.32) * mm, "end": v(7.08, 0.23) * mm});
            skLineSegment(sketch, "E1153", {"start": v(7.08, 0.23) * mm, "end": v(6.2, -0.65) * mm});
            skLineSegment(sketch, "E1154", {"start": v(6.2, -0.65) * mm, "end": v(6.12, -0.74) * mm});
            skLineSegment(sketch, "E1155", {"start": v(6.12, -0.74) * mm, "end": v(6.1, -0.76) * mm});
            skLineSegment(sketch, "E1156", {"start": v(6.1, -0.76) * mm, "end": v(6.05, -0.84) * mm});
            skLineSegment(sketch, "E1157", {"start": v(6.05, -0.84) * mm, "end": v(6.03, -0.95) * mm});
            skLineSegment(sketch, "E1158", {"start": v(6.03, -0.95) * mm, "end": v(6.06, -1.05) * mm});
            skLineSegment(sketch, "E1159", {"start": v(6.06, -1.05) * mm, "end": v(6.12, -1.14) * mm});
            skLineSegment(sketch, "E1160", {"start": v(6.12, -1.14) * mm, "end": v(6.21, -1.2) * mm});
            skLineSegment(sketch, "E1161", {"start": v(6.21, -1.2) * mm, "end": v(6.31, -1.23) * mm});
            skLineSegment(sketch, "E1162", {"start": v(6.31, -1.23) * mm, "end": v(6.42, -1.22) * mm});
            skLineSegment(sketch, "E1163", {"start": v(6.42, -1.22) * mm, "end": v(6.5, -1.17) * mm});
            skLineSegment(sketch, "E1164", {"start": v(6.5, -1.17) * mm, "end": v(6.53, -1.15) * mm});
            skLineSegment(sketch, "E1165", {"start": v(6.53, -1.15) * mm, "end": v(6.63, -1.04) * mm});
            skLineSegment(sketch, "E1166", {"start": v(6.63, -1.04) * mm, "end": v(7.68, 0) * mm});
            skLineSegment(sketch, "E1167", {"start": v(7.68, 0) * mm, "end": v(7.78, 0.11) * mm});
            skLineSegment(sketch, "E1168", {"start": v(7.78, 0.11) * mm, "end": v(7.8, 0.13) * mm});
            skLineSegment(sketch, "E1169", {"start": v(7.8, 0.13) * mm, "end": v(7.85, 0.2) * mm});
            skLineSegment(sketch, "E1170", {"start": v(7.85, 0.2) * mm, "end": v(7.87, 0.32) * mm});
            skLineSegment(sketch, "E1171", {"start": v(7.87, 0.32) * mm, "end": v(7.85, 0.42) * mm});
            skLineSegment(sketch, "E1172", {"start": v(7.85, 0.42) * mm, "end": v(7.8, 0.5) * mm});
            skLineSegment(sketch, "E1173", {"start": v(7.8, 0.5) * mm, "end": v(7.78, 0.52) * mm});
            skLineSegment(sketch, "E1174", {"start": v(7.78, 0.52) * mm, "end": v(7.67, 0.63) * mm});
            skLineSegment(sketch, "E1175", {"start": v(7.67, 0.63) * mm, "end": v(6.57, 1.73) * mm});
            skLineSegment(sketch, "E1176", {"start": v(6.57, 1.73) * mm, "end": v(6.46, 1.84) * mm});
            skLineSegment(sketch, "E1177", {"start": v(22.34, -0.74) * mm, "end": v(22.25, -0.64) * mm});
            skLineSegment(sketch, "E1178", {"start": v(22.25, -0.64) * mm, "end": v(21.31, 0.29) * mm});
            skLineSegment(sketch, "E1179", {"start": v(21.31, 0.29) * mm, "end": v(21.22, 0.38) * mm});
            skLineSegment(sketch, "E1180", {"start": v(21.22, 0.38) * mm, "end": v(21.3, 0.47) * mm});
            skLineSegment(sketch, "E1181", {"start": v(21.3, 0.47) * mm, "end": v(22.18, 1.35) * mm});
            skLineSegment(sketch, "E1182", {"start": v(22.18, 1.35) * mm, "end": v(22.27, 1.44) * mm});
            skLineSegment(sketch, "E1183", {"start": v(22.27, 1.44) * mm, "end": v(22.3, 1.46) * mm});
            skLineSegment(sketch, "E1184", {"start": v(22.3, 1.46) * mm, "end": v(22.34, 1.54) * mm});
            skLineSegment(sketch, "E1185", {"start": v(22.34, 1.54) * mm, "end": v(22.36, 1.65) * mm});
            skLineSegment(sketch, "E1186", {"start": v(22.36, 1.65) * mm, "end": v(22.33, 1.75) * mm});
            skLineSegment(sketch, "E1187", {"start": v(22.33, 1.75) * mm, "end": v(22.26, 1.84) * mm});
            skLineSegment(sketch, "E1188", {"start": v(22.26, 1.84) * mm, "end": v(22.18, 1.9) * mm});
            skLineSegment(sketch, "E1189", {"start": v(22.18, 1.9) * mm, "end": v(22.07, 1.93) * mm});
            skLineSegment(sketch, "E1190", {"start": v(22.07, 1.93) * mm, "end": v(21.97, 1.91) * mm});
            skLineSegment(sketch, "E1191", {"start": v(21.97, 1.91) * mm, "end": v(21.88, 1.87) * mm});
            skLineSegment(sketch, "E1192", {"start": v(21.88, 1.87) * mm, "end": v(21.86, 1.84) * mm});
            skLineSegment(sketch, "E1193", {"start": v(21.86, 1.84) * mm, "end": v(21.76, 1.74) * mm});
            skLineSegment(sketch, "E1194", {"start": v(21.76, 1.74) * mm, "end": v(20.7, 0.7) * mm});
            skLineSegment(sketch, "E1195", {"start": v(20.7, 0.7) * mm, "end": v(20.6, 0.59) * mm});
            skLineSegment(sketch, "E1196", {"start": v(20.6, 0.59) * mm, "end": v(20.59, 0.57) * mm});
            skLineSegment(sketch, "E1197", {"start": v(20.59, 0.57) * mm, "end": v(20.54, 0.5) * mm});
            skLineSegment(sketch, "E1198", {"start": v(20.54, 0.5) * mm, "end": v(20.52, 0.38) * mm});
            skLineSegment(sketch, "E1199", {"start": v(20.52, 0.38) * mm, "end": v(20.54, 0.27) * mm});
            skLineSegment(sketch, "E1200", {"start": v(20.54, 0.27) * mm, "end": v(20.59, 0.2) * mm});
            skLineSegment(sketch, "E1201", {"start": v(20.59, 0.2) * mm, "end": v(20.6, 0.18) * mm});
            skLineSegment(sketch, "E1202", {"start": v(20.6, 0.18) * mm, "end": v(20.72, 0.07) * mm});
            skLineSegment(sketch, "E1203", {"start": v(20.72, 0.07) * mm, "end": v(21.82, -1.04) * mm});
            skLineSegment(sketch, "E1204", {"start": v(21.82, -1.04) * mm, "end": v(21.93, -1.15) * mm});
            skLineSegment(sketch, "E1205", {"start": v(21.93, -1.15) * mm, "end": v(21.95, -1.17) * mm});
            skLineSegment(sketch, "E1206", {"start": v(21.95, -1.17) * mm, "end": v(22.03, -1.22) * mm});
            skLineSegment(sketch, "E1207", {"start": v(22.03, -1.22) * mm, "end": v(22.14, -1.23) * mm});
            skLineSegment(sketch, "E1208", {"start": v(22.14, -1.23) * mm, "end": v(22.24, -1.2) * mm});
            skLineSegment(sketch, "E1209", {"start": v(22.24, -1.2) * mm, "end": v(22.33, -1.14) * mm});
            skLineSegment(sketch, "E1210", {"start": v(22.33, -1.14) * mm, "end": v(22.4, -1.05) * mm});
            skLineSegment(sketch, "E1211", {"start": v(22.4, -1.05) * mm, "end": v(22.42, -0.95) * mm});
            skLineSegment(sketch, "E1212", {"start": v(22.42, -0.95) * mm, "end": v(22.4, -0.84) * mm});
            skLineSegment(sketch, "E1213", {"start": v(22.4, -0.84) * mm, "end": v(22.36, -0.76) * mm});
            skLineSegment(sketch, "E1214", {"start": v(22.36, -0.76) * mm, "end": v(22.34, -0.74) * mm});
            skLineSegment(sketch, "E1215", {"start": v(19.63, 0.38) * mm, "end": v(19.71, 0.47) * mm});
            skLineSegment(sketch, "E1216", {"start": v(19.71, 0.47) * mm, "end": v(20.6, 1.35) * mm});
            skLineSegment(sketch, "E1217", {"start": v(20.6, 1.35) * mm, "end": v(20.68, 1.44) * mm});
            skLineSegment(sketch, "E1218", {"start": v(20.68, 1.44) * mm, "end": v(20.7, 1.46) * mm});
            skLineSegment(sketch, "E1219", {"start": v(20.7, 1.46) * mm, "end": v(20.75, 1.54) * mm});
            skLineSegment(sketch, "E1220", {"start": v(20.75, 1.54) * mm, "end": v(20.76, 1.65) * mm});
            skLineSegment(sketch, "E1221", {"start": v(20.76, 1.65) * mm, "end": v(20.73, 1.75) * mm});
            skLineSegment(sketch, "E1222", {"start": v(20.73, 1.75) * mm, "end": v(20.67, 1.84) * mm});
            skLineSegment(sketch, "E1223", {"start": v(20.67, 1.84) * mm, "end": v(20.58, 1.9) * mm});
            skLineSegment(sketch, "E1224", {"start": v(20.58, 1.9) * mm, "end": v(20.48, 1.93) * mm});
            skLineSegment(sketch, "E1225", {"start": v(20.48, 1.93) * mm, "end": v(20.37, 1.91) * mm});
            skLineSegment(sketch, "E1226", {"start": v(20.37, 1.91) * mm, "end": v(20.3, 1.87) * mm});
            skLineSegment(sketch, "E1227", {"start": v(20.3, 1.87) * mm, "end": v(20.27, 1.84) * mm});
            skLineSegment(sketch, "E1228", {"start": v(20.27, 1.84) * mm, "end": v(20.16, 1.74) * mm});
            skLineSegment(sketch, "E1229", {"start": v(20.16, 1.74) * mm, "end": v(19.12, 0.7) * mm});
            skLineSegment(sketch, "E1230", {"start": v(19.12, 0.7) * mm, "end": v(19.01, 0.59) * mm});
            skLineSegment(sketch, "E1231", {"start": v(19.01, 0.59) * mm, "end": v(19, 0.57) * mm});
            skLineSegment(sketch, "E1232", {"start": v(19, 0.57) * mm, "end": v(18.95, 0.5) * mm});
            skLineSegment(sketch, "E1233", {"start": v(18.95, 0.5) * mm, "end": v(18.93, 0.38) * mm});
            skLineSegment(sketch, "E1234", {"start": v(18.93, 0.38) * mm, "end": v(18.95, 0.27) * mm});
            skLineSegment(sketch, "E1235", {"start": v(18.95, 0.27) * mm, "end": v(19, 0.2) * mm});
            skLineSegment(sketch, "E1236", {"start": v(19, 0.2) * mm, "end": v(19.01, 0.18) * mm});
            skLineSegment(sketch, "E1237", {"start": v(19.01, 0.18) * mm, "end": v(19.12, 0.07) * mm});
            skLineSegment(sketch, "E1238", {"start": v(19.12, 0.07) * mm, "end": v(20.23, -1.04) * mm});
            skLineSegment(sketch, "E1239", {"start": v(20.23, -1.04) * mm, "end": v(20.34, -1.15) * mm});
            skLineSegment(sketch, "E1240", {"start": v(20.34, -1.15) * mm, "end": v(20.36, -1.17) * mm});
            skLineSegment(sketch, "E1241", {"start": v(20.36, -1.17) * mm, "end": v(20.44, -1.22) * mm});
            skLineSegment(sketch, "E1242", {"start": v(20.44, -1.22) * mm, "end": v(20.55, -1.23) * mm});
            skLineSegment(sketch, "E1243", {"start": v(20.55, -1.23) * mm, "end": v(20.65, -1.2) * mm});
            skLineSegment(sketch, "E1244", {"start": v(20.65, -1.2) * mm, "end": v(20.74, -1.14) * mm});
            skLineSegment(sketch, "E1245", {"start": v(20.74, -1.14) * mm, "end": v(20.8, -1.05) * mm});
            skLineSegment(sketch, "E1246", {"start": v(20.8, -1.05) * mm, "end": v(20.83, -0.95) * mm});
            skLineSegment(sketch, "E1247", {"start": v(20.83, -0.95) * mm, "end": v(20.82, -0.84) * mm});
            skLineSegment(sketch, "E1248", {"start": v(20.82, -0.84) * mm, "end": v(20.77, -0.76) * mm});
            skLineSegment(sketch, "E1249", {"start": v(20.77, -0.76) * mm, "end": v(20.75, -0.74) * mm});
            skLineSegment(sketch, "E1250", {"start": v(20.75, -0.74) * mm, "end": v(20.65, -0.64) * mm});
            skLineSegment(sketch, "E1251", {"start": v(20.65, -0.64) * mm, "end": v(19.72, 0.29) * mm});
            skLineSegment(sketch, "E1252", {"start": v(19.72, 0.29) * mm, "end": v(19.63, 0.38) * mm});
            skSolve(sketch);
        }
        {
            var Q0;
            Q0 = qSketchRegion(id + "F5", true);
            extrude(context, id + "F6", {"entities" : qUnion([Q0]), "operationType" : NewBodyOperationType.REMOVE, "oppositeDirection" : true, "depth" : 3 * mm});
        }
        {
            var Q0;
            Q0=makeQuery(id+"F1.opExtrude","CAP_FACE",FACE,{"disambiguationData":[OSD([sQuery(id+"F0.wireOp",EDGE,"E0.bottom"),sQuery(id+"F0.wireOp",EDGE,"E0.top"),sQuery(id+"F0.wireOp",EDGE,"E0.left"),sQuery(id+"F0.wireOp",EDGE,"E0.right")])],"isStart":true});
            var sketch = newSketch(context, id + "F7", { "sketchPlane" : qUnion([Q0])});
            skLineSegment(sketch, "E1253", {"start": v(-0.47, 1.64) * mm, "end": v(-0.68, 1.64) * mm});
            skLineSegment(sketch, "E1254", {"start": v(-0.68, 1.64) * mm, "end": v(-1.3, 1.4) * mm});
            skLineSegment(sketch, "E1255", {"start": v(-1.3, 1.4) * mm, "end": v(-1.83, 0.89) * mm});
            skLineSegment(sketch, "E1256", {"start": v(-1.83, 0.89) * mm, "end": v(-1.9, 0.74) * mm});
            skLineSegment(sketch, "E1257", {"start": v(-1.9, 0.74) * mm, "end": v(-1.94, 0.65) * mm});
            skLineSegment(sketch, "E1258", {"start": v(-1.94, 0.65) * mm, "end": v(-2.05, 0.14) * mm});
            skLineSegment(sketch, "E1259", {"start": v(-2.05, 0.14) * mm, "end": v(-2, -0.37) * mm});
            skLineSegment(sketch, "E1260", {"start": v(-2, -0.37) * mm, "end": v(-1.97, -0.47) * mm});
            skLineSegment(sketch, "E1261", {"start": v(-1.97, -0.47) * mm, "end": v(-1.93, -0.57) * mm});
            skLineSegment(sketch, "E1262", {"start": v(-1.93, -0.57) * mm, "end": v(-1.65, -1) * mm});
            skLineSegment(sketch, "E1263", {"start": v(-1.65, -1) * mm, "end": v(-1.25, -1.33) * mm});
            skLineSegment(sketch, "E1264", {"start": v(-1.25, -1.33) * mm, "end": v(-1.16, -1.37) * mm});
            skLineSegment(sketch, "E1265", {"start": v(-1.16, -1.37) * mm, "end": v(-1.06, -1.42) * mm});
            skLineSegment(sketch, "E1266", {"start": v(-1.06, -1.42) * mm, "end": v(-0.56, -1.53) * mm});
            skLineSegment(sketch, "E1267", {"start": v(-0.56, -1.53) * mm, "end": v(-0.05, -1.47) * mm});
            skLineSegment(sketch, "E1268", {"start": v(-0.05, -1.47) * mm, "end": v(0.05, -1.44) * mm});
            skLineSegment(sketch, "E1269", {"start": v(0.05, -1.44) * mm, "end": v(0.15, -1.4) * mm});
            skLineSegment(sketch, "E1270", {"start": v(0.15, -1.4) * mm, "end": v(0.59, -1.13) * mm});
            skLineSegment(sketch, "E1271", {"start": v(0.59, -1.13) * mm, "end": v(0.91, -0.73) * mm});
            skLineSegment(sketch, "E1272", {"start": v(0.91, -0.73) * mm, "end": v(0.96, -0.63) * mm});
            skLineSegment(sketch, "E1273", {"start": v(0.96, -0.63) * mm, "end": v(1, -0.54) * mm});
            skLineSegment(sketch, "E1274", {"start": v(1, -0.54) * mm, "end": v(1.11, -0.03) * mm});
            skLineSegment(sketch, "E1275", {"start": v(1.11, -0.03) * mm, "end": v(1.06, 0.48) * mm});
            skLineSegment(sketch, "E1276", {"start": v(1.06, 0.48) * mm, "end": v(1.03, 0.58) * mm});
            skLineSegment(sketch, "E1277", {"start": v(1.03, 0.58) * mm, "end": v(1, 0.68) * mm});
            skLineSegment(sketch, "E1278", {"start": v(1, 0.68) * mm, "end": v(0.71, 1.11) * mm});
            skLineSegment(sketch, "E1279", {"start": v(0.71, 1.11) * mm, "end": v(0.31, 1.44) * mm});
            skLineSegment(sketch, "E1280", {"start": v(0.31, 1.44) * mm, "end": v(0.22, 1.48) * mm});
            skLineSegment(sketch, "E1281", {"start": v(0.22, 1.48) * mm, "end": v(0.16, 1.51) * mm});
            skLineSegment(sketch, "E1282", {"start": v(0.16, 1.51) * mm, "end": v(-0.31, 1.64) * mm});
            skLineSegment(sketch, "E1283", {"start": v(-0.31, 1.64) * mm, "end": v(-0.47, 1.64) * mm});
            skLineSegment(sketch, "E1284", {"start": v(-0.47, -1.78) * mm, "end": v(-0.67, -1.78) * mm});
            skLineSegment(sketch, "E1285", {"start": v(-0.67, -1.78) * mm, "end": v(-1.2, -1.63) * mm});
            skLineSegment(sketch, "E1286", {"start": v(-1.2, -1.63) * mm, "end": v(-1.27, -1.6) * mm});
            skLineSegment(sketch, "E1287", {"start": v(-1.27, -1.6) * mm, "end": v(-1.43, -1.52) * mm});
            skLineSegment(sketch, "E1288", {"start": v(-1.43, -1.52) * mm, "end": v(-1.85, -1.16) * mm});
            skLineSegment(sketch, "E1289", {"start": v(-1.85, -1.16) * mm, "end": v(-2.2, -0.55) * mm});
            skLineSegment(sketch, "E1290", {"start": v(-2.2, -0.55) * mm, "end": v(-2.3, 0.15) * mm});
            skLineSegment(sketch, "E1291", {"start": v(-2.3, 0.15) * mm, "end": v(-2.2, 0.7) * mm});
            skLineSegment(sketch, "E1292", {"start": v(-2.2, 0.7) * mm, "end": v(-2.13, 0.85) * mm});
            skLineSegment(sketch, "E1293", {"start": v(-2.13, 0.85) * mm, "end": v(-2.05, 1.01) * mm});
            skLineSegment(sketch, "E1294", {"start": v(-2.05, 1.01) * mm, "end": v(-1.69, 1.43) * mm});
            skLineSegment(sketch, "E1295", {"start": v(-1.69, 1.43) * mm, "end": v(-1.08, 1.79) * mm});
            skLineSegment(sketch, "E1296", {"start": v(-1.08, 1.79) * mm, "end": v(-0.38, 1.9) * mm});
            skLineSegment(sketch, "E1297", {"start": v(-0.38, 1.9) * mm, "end": v(0.17, 1.79) * mm});
            skLineSegment(sketch, "E1298", {"start": v(0.17, 1.79) * mm, "end": v(0.33, 1.71) * mm});
            skLineSegment(sketch, "E1299", {"start": v(0.33, 1.71) * mm, "end": v(0.44, 1.66) * mm});
            skLineSegment(sketch, "E1300", {"start": v(0.44, 1.66) * mm, "end": v(0.9, 1.28) * mm});
            skLineSegment(sketch, "E1301", {"start": v(0.9, 1.28) * mm, "end": v(1.22, 0.78) * mm});
            skLineSegment(sketch, "E1302", {"start": v(1.22, 0.78) * mm, "end": v(1.26, 0.66) * mm});
            skLineSegment(sketch, "E1303", {"start": v(1.26, 0.66) * mm, "end": v(1.3, 0.55) * mm});
            skLineSegment(sketch, "E1304", {"start": v(1.3, 0.55) * mm, "end": v(1.36, -0.05) * mm});
            skLineSegment(sketch, "E1305", {"start": v(1.36, -0.05) * mm, "end": v(1.24, -0.63) * mm});
            skLineSegment(sketch, "E1306", {"start": v(1.24, -0.63) * mm, "end": v(1.19, -0.74) * mm});
            skLineSegment(sketch, "E1307", {"start": v(1.19, -0.74) * mm, "end": v(1.13, -0.85) * mm});
            skLineSegment(sketch, "E1308", {"start": v(1.13, -0.85) * mm, "end": v(0.76, -1.31) * mm});
            skLineSegment(sketch, "E1309", {"start": v(0.76, -1.31) * mm, "end": v(0.25, -1.64) * mm});
            skLineSegment(sketch, "E1310", {"start": v(0.25, -1.64) * mm, "end": v(0.14, -1.68) * mm});
            skLineSegment(sketch, "E1311", {"start": v(0.14, -1.68) * mm, "end": v(0.09, -1.7) * mm});
            skLineSegment(sketch, "E1312", {"start": v(0.09, -1.7) * mm, "end": v(-0.33, -1.78) * mm});
            skLineSegment(sketch, "E1313", {"start": v(-0.33, -1.78) * mm, "end": v(-0.47, -1.78) * mm});
            skLineSegment(sketch, "E1314", {"start": v(-0.47, -1.21) * mm, "end": v(-0.6, -1.21) * mm});
            skLineSegment(sketch, "E1315", {"start": v(-0.6, -1.21) * mm, "end": v(-0.98, -1.1) * mm});
            skLineSegment(sketch, "E1316", {"start": v(-0.98, -1.1) * mm, "end": v(-1.02, -1.09) * mm});
            skLineSegment(sketch, "E1317", {"start": v(-1.02, -1.09) * mm, "end": v(-1.1, -1.05) * mm});
            skLineSegment(sketch, "E1318", {"start": v(-1.1, -1.05) * mm, "end": v(-1.42, -0.8) * mm});
            skLineSegment(sketch, "E1319", {"start": v(-1.42, -0.8) * mm, "end": v(-1.64, -0.45) * mm});
            skLineSegment(sketch, "E1320", {"start": v(-1.64, -0.45) * mm, "end": v(-1.67, -0.37) * mm});
            skLineSegment(sketch, "E1321", {"start": v(-1.67, -0.37) * mm, "end": v(-1.67, -0.36) * mm});
            skLineSegment(sketch, "E1322", {"start": v(-1.67, -0.36) * mm, "end": v(-1.64, -0.29) * mm});
            skLineSegment(sketch, "E1323", {"start": v(-1.64, -0.29) * mm, "end": v(-1.63, -0.28) * mm});
            skLineSegment(sketch, "E1324", {"start": v(-1.63, -0.28) * mm, "end": v(-1.62, -0.28) * mm});
            skLineSegment(sketch, "E1325", {"start": v(-1.62, -0.28) * mm, "end": v(-1.55, -0.31) * mm});
            skLineSegment(sketch, "E1326", {"start": v(-1.55, -0.31) * mm, "end": v(-1.55, -0.32) * mm});
            skLineSegment(sketch, "E1327", {"start": v(-1.55, -0.32) * mm, "end": v(-1.52, -0.4) * mm});
            skLineSegment(sketch, "E1328", {"start": v(-1.52, -0.4) * mm, "end": v(-1.32, -0.7) * mm});
            skLineSegment(sketch, "E1329", {"start": v(-1.32, -0.7) * mm, "end": v(-1.04, -0.94) * mm});
            skLineSegment(sketch, "E1330", {"start": v(-1.04, -0.94) * mm, "end": v(-0.97, -0.98) * mm});
            skLineSegment(sketch, "E1331", {"start": v(-0.97, -0.98) * mm, "end": v(-0.93, -1) * mm});
            skLineSegment(sketch, "E1332", {"start": v(-0.93, -1) * mm, "end": v(-0.59, -1.09) * mm});
            skLineSegment(sketch, "E1333", {"start": v(-0.59, -1.09) * mm, "end": v(-0.47, -1.09) * mm});
            skLineSegment(sketch, "E1334", {"start": v(-0.47, -1.09) * mm, "end": v(-0.46, -1.09) * mm});
            skLineSegment(sketch, "E1335", {"start": v(-0.46, -1.09) * mm, "end": v(-0.4, -1.14) * mm});
            skLineSegment(sketch, "E1336", {"start": v(-0.4, -1.14) * mm, "end": v(-0.4, -1.15) * mm});
            skLineSegment(sketch, "E1337", {"start": v(-0.4, -1.15) * mm, "end": v(-0.4, -1.17) * mm});
            skLineSegment(sketch, "E1338", {"start": v(-0.4, -1.17) * mm, "end": v(-0.46, -1.21) * mm});
            skLineSegment(sketch, "E1339", {"start": v(-0.46, -1.21) * mm, "end": v(-0.47, -1.21) * mm});
            skLineSegment(sketch, "E1340", {"start": v(3.5, 0.82) * mm, "end": v(3.43, 0.82) * mm});
            skLineSegment(sketch, "E1341", {"start": v(3.43, 0.82) * mm, "end": v(3.24, 0.68) * mm});
            skLineSegment(sketch, "E1342", {"start": v(3.24, 0.68) * mm, "end": v(3.22, 0.65) * mm});
            skLineSegment(sketch, "E1343", {"start": v(3.22, 0.65) * mm, "end": v(3.21, 0.63) * mm});
            skLineSegment(sketch, "E1344", {"start": v(3.21, 0.63) * mm, "end": v(3.2, 0.44) * mm});
            skLineSegment(sketch, "E1345", {"start": v(3.2, 0.44) * mm, "end": v(3.21, 0.42) * mm});
            skLineSegment(sketch, "E1346", {"start": v(3.21, 0.42) * mm, "end": v(3.22, 0.4) * mm});
            skLineSegment(sketch, "E1347", {"start": v(3.22, 0.4) * mm, "end": v(3.35, 0.26) * mm});
            skLineSegment(sketch, "E1348", {"start": v(3.35, 0.26) * mm, "end": v(3.36, 0.25) * mm});
            skLineSegment(sketch, "E1349", {"start": v(3.36, 0.25) * mm, "end": v(3.4, 0.23) * mm});
            skLineSegment(sketch, "E1350", {"start": v(3.4, 0.23) * mm, "end": v(3.6, 0.24) * mm});
            skLineSegment(sketch, "E1351", {"start": v(3.6, 0.24) * mm, "end": v(3.75, 0.35) * mm});
            skLineSegment(sketch, "E1352", {"start": v(3.75, 0.35) * mm, "end": v(3.76, 0.4) * mm});
            skLineSegment(sketch, "E1353", {"start": v(3.76, 0.4) * mm, "end": v(3.77, 0.41) * mm});
            skLineSegment(sketch, "E1354", {"start": v(3.77, 0.41) * mm, "end": v(3.78, 0.6) * mm});
            skLineSegment(sketch, "E1355", {"start": v(3.78, 0.6) * mm, "end": v(3.78, 0.62) * mm});
            skLineSegment(sketch, "E1356", {"start": v(3.78, 0.62) * mm, "end": v(3.77, 0.64) * mm});
            skLineSegment(sketch, "E1357", {"start": v(3.77, 0.64) * mm, "end": v(3.64, 0.78) * mm});
            skLineSegment(sketch, "E1358", {"start": v(3.64, 0.78) * mm, "end": v(3.62, 0.8) * mm});
            skLineSegment(sketch, "E1359", {"start": v(3.62, 0.8) * mm, "end": v(3.61, 0.8) * mm});
            skLineSegment(sketch, "E1360", {"start": v(3.61, 0.8) * mm, "end": v(3.52, 0.82) * mm});
            skLineSegment(sketch, "E1361", {"start": v(3.52, 0.82) * mm, "end": v(3.5, 0.82) * mm});
            skLineSegment(sketch, "E1362", {"start": v(3.5, -0.03) * mm, "end": v(3.43, -0.03) * mm});
            skLineSegment(sketch, "E1363", {"start": v(3.43, -0.03) * mm, "end": v(3.27, 0.02) * mm});
            skLineSegment(sketch, "E1364", {"start": v(3.27, 0.02) * mm, "end": v(3.25, 0.02) * mm});
            skLineSegment(sketch, "E1365", {"start": v(3.25, 0.02) * mm, "end": v(3.19, 0.06) * mm});
            skLineSegment(sketch, "E1366", {"start": v(3.19, 0.06) * mm, "end": v(2.97, 0.34) * mm});
            skLineSegment(sketch, "E1367", {"start": v(2.97, 0.34) * mm, "end": v(2.96, 0.7) * mm});
            skLineSegment(sketch, "E1368", {"start": v(2.96, 0.7) * mm, "end": v(3, 0.76) * mm});
            skLineSegment(sketch, "E1369", {"start": v(3, 0.76) * mm, "end": v(3.03, 0.83) * mm});
            skLineSegment(sketch, "E1370", {"start": v(3.03, 0.83) * mm, "end": v(3.31, 1.04) * mm});
            skLineSegment(sketch, "E1371", {"start": v(3.31, 1.04) * mm, "end": v(3.66, 1.05) * mm});
            skLineSegment(sketch, "E1372", {"start": v(3.66, 1.05) * mm, "end": v(3.73, 1.02) * mm});
            skLineSegment(sketch, "E1373", {"start": v(3.73, 1.02) * mm, "end": v(3.77, 1) * mm});
            skLineSegment(sketch, "E1374", {"start": v(3.77, 1) * mm, "end": v(4, 0.74) * mm});
            skLineSegment(sketch, "E1375", {"start": v(4, 0.74) * mm, "end": v(4.01, 0.7) * mm});
            skLineSegment(sketch, "E1376", {"start": v(4.01, 0.7) * mm, "end": v(4.03, 0.67) * mm});
            skLineSegment(sketch, "E1377", {"start": v(4.03, 0.67) * mm, "end": v(4, 0.32) * mm});
            skLineSegment(sketch, "E1378", {"start": v(4, 0.32) * mm, "end": v(4, 0.28) * mm});
            skLineSegment(sketch, "E1379", {"start": v(4, 0.28) * mm, "end": v(3.97, 0.23) * mm});
            skLineSegment(sketch, "E1380", {"start": v(3.97, 0.23) * mm, "end": v(3.78, 0.05) * mm});
            skLineSegment(sketch, "E1381", {"start": v(3.78, 0.05) * mm, "end": v(3.56, -0.03) * mm});
            skLineSegment(sketch, "E1382", {"start": v(3.56, -0.03) * mm, "end": v(3.5, -0.03) * mm});
            skLineSegment(sketch, "E1383", {"start": v(-2.72, 1.3) * mm, "end": v(-2.79, 1.3) * mm});
            skLineSegment(sketch, "E1384", {"start": v(-2.79, 1.3) * mm, "end": v(-2.98, 1.15) * mm});
            skLineSegment(sketch, "E1385", {"start": v(-2.98, 1.15) * mm, "end": v(-3, 1.12) * mm});
            skLineSegment(sketch, "E1386", {"start": v(-3, 1.12) * mm, "end": v(-3, 1.1) * mm});
            skLineSegment(sketch, "E1387", {"start": v(-3, 1.1) * mm, "end": v(-3.01, 0.91) * mm});
            skLineSegment(sketch, "E1388", {"start": v(-3.01, 0.91) * mm, "end": v(-3, 0.9) * mm});
            skLineSegment(sketch, "E1389", {"start": v(-3, 0.9) * mm, "end": v(-3, 0.88) * mm});
            skLineSegment(sketch, "E1390", {"start": v(-3, 0.88) * mm, "end": v(-2.87, 0.73) * mm});
            skLineSegment(sketch, "E1391", {"start": v(-2.87, 0.73) * mm, "end": v(-2.85, 0.72) * mm});
            skLineSegment(sketch, "E1392", {"start": v(-2.85, 0.72) * mm, "end": v(-2.83, 0.71) * mm});
            skLineSegment(sketch, "E1393", {"start": v(-2.83, 0.71) * mm, "end": v(-2.64, 0.7) * mm});
            skLineSegment(sketch, "E1394", {"start": v(-2.64, 0.7) * mm, "end": v(-2.62, 0.71) * mm});
            skLineSegment(sketch, "E1395", {"start": v(-2.62, 0.71) * mm, "end": v(-2.6, 0.72) * mm});
            skLineSegment(sketch, "E1396", {"start": v(-2.6, 0.72) * mm, "end": v(-2.46, 0.85) * mm});
            skLineSegment(sketch, "E1397", {"start": v(-2.46, 0.85) * mm, "end": v(-2.45, 0.86) * mm});
            skLineSegment(sketch, "E1398", {"start": v(-2.45, 0.86) * mm, "end": v(-2.43, 0.9) * mm});
            skLineSegment(sketch, "E1399", {"start": v(-2.43, 0.9) * mm, "end": v(-2.44, 1.1) * mm});
            skLineSegment(sketch, "E1400", {"start": v(-2.44, 1.1) * mm, "end": v(-2.55, 1.25) * mm});
            skLineSegment(sketch, "E1401", {"start": v(-2.55, 1.25) * mm, "end": v(-2.6, 1.26) * mm});
            skLineSegment(sketch, "E1402", {"start": v(-2.6, 1.26) * mm, "end": v(-2.6, 1.27) * mm});
            skLineSegment(sketch, "E1403", {"start": v(-2.6, 1.27) * mm, "end": v(-2.7, 1.3) * mm});
            skLineSegment(sketch, "E1404", {"start": v(-2.7, 1.3) * mm, "end": v(-2.72, 1.3) * mm});
            skLineSegment(sketch, "E1405", {"start": v(-2.72, 0.44) * mm, "end": v(-2.78, 0.44) * mm});
            skLineSegment(sketch, "E1406", {"start": v(-2.78, 0.44) * mm, "end": v(-2.94, 0.49) * mm});
            skLineSegment(sketch, "E1407", {"start": v(-2.94, 0.49) * mm, "end": v(-2.96, 0.5) * mm});
            skLineSegment(sketch, "E1408", {"start": v(-2.96, 0.5) * mm, "end": v(-3, 0.51) * mm});
            skLineSegment(sketch, "E1409", {"start": v(-3, 0.51) * mm, "end": v(-3.23, 0.78) * mm});
            skLineSegment(sketch, "E1410", {"start": v(-3.23, 0.78) * mm, "end": v(-3.24, 0.81) * mm});
            skLineSegment(sketch, "E1411", {"start": v(-3.24, 0.81) * mm, "end": v(-3.25, 0.85) * mm});
            skLineSegment(sketch, "E1412", {"start": v(-3.25, 0.85) * mm, "end": v(-3.23, 1.2) * mm});
            skLineSegment(sketch, "E1413", {"start": v(-3.23, 1.2) * mm, "end": v(-3.22, 1.23) * mm});
            skLineSegment(sketch, "E1414", {"start": v(-3.22, 1.23) * mm, "end": v(-3.19, 1.3) * mm});
            skLineSegment(sketch, "E1415", {"start": v(-3.19, 1.3) * mm, "end": v(-2.9, 1.51) * mm});
            skLineSegment(sketch, "E1416", {"start": v(-2.9, 1.51) * mm, "end": v(-2.55, 1.52) * mm});
            skLineSegment(sketch, "E1417", {"start": v(-2.55, 1.52) * mm, "end": v(-2.48, 1.5) * mm});
            skLineSegment(sketch, "E1418", {"start": v(-2.48, 1.5) * mm, "end": v(-2.45, 1.47) * mm});
            skLineSegment(sketch, "E1419", {"start": v(-2.45, 1.47) * mm, "end": v(-2.21, 1.21) * mm});
            skLineSegment(sketch, "E1420", {"start": v(-2.21, 1.21) * mm, "end": v(-2.2, 1.18) * mm});
            skLineSegment(sketch, "E1421", {"start": v(-2.2, 1.18) * mm, "end": v(-2.19, 1.14) * mm});
            skLineSegment(sketch, "E1422", {"start": v(-2.19, 1.14) * mm, "end": v(-2.2, 0.79) * mm});
            skLineSegment(sketch, "E1423", {"start": v(-2.2, 0.79) * mm, "end": v(-2.22, 0.75) * mm});
            skLineSegment(sketch, "E1424", {"start": v(-2.22, 0.75) * mm, "end": v(-2.24, 0.72) * mm});
            skLineSegment(sketch, "E1425", {"start": v(-2.24, 0.72) * mm, "end": v(-2.5, 0.49) * mm});
            skLineSegment(sketch, "E1426", {"start": v(-2.5, 0.49) * mm, "end": v(-2.54, 0.47) * mm});
            skLineSegment(sketch, "E1427", {"start": v(-2.54, 0.47) * mm, "end": v(-2.55, 0.47) * mm});
            skLineSegment(sketch, "E1428", {"start": v(-2.55, 0.47) * mm, "end": v(-2.68, 0.44) * mm});
            skLineSegment(sketch, "E1429", {"start": v(-2.68, 0.44) * mm, "end": v(-2.72, 0.44) * mm});
            skLineSegment(sketch, "E1430", {"start": v(-0.84, -2.1) * mm, "end": v(-0.93, -2.1) * mm});
            skLineSegment(sketch, "E1431", {"start": v(-0.93, -2.1) * mm, "end": v(-1.2, -2.2) * mm});
            skLineSegment(sketch, "E1432", {"start": v(-1.2, -2.2) * mm, "end": v(-1.43, -2.42) * mm});
            skLineSegment(sketch, "E1433", {"start": v(-1.43, -2.42) * mm, "end": v(-1.46, -2.49) * mm});
            skLineSegment(sketch, "E1434", {"start": v(-1.46, -2.49) * mm, "end": v(-1.5, -2.57) * mm});
            skLineSegment(sketch, "E1435", {"start": v(-1.5, -2.57) * mm, "end": v(-1.49, -3) * mm});
            skLineSegment(sketch, "E1436", {"start": v(-1.49, -3) * mm, "end": v(-1.22, -3.36) * mm});
            skLineSegment(sketch, "E1437", {"start": v(-1.22, -3.36) * mm, "end": v(-1.14, -3.4) * mm});
            skLineSegment(sketch, "E1438", {"start": v(-1.14, -3.4) * mm, "end": v(-1.05, -3.44) * mm});
            skLineSegment(sketch, "E1439", {"start": v(-1.05, -3.44) * mm, "end": v(-0.61, -3.43) * mm});
            skLineSegment(sketch, "E1440", {"start": v(-0.61, -3.43) * mm, "end": v(-0.26, -3.17) * mm});
            skLineSegment(sketch, "E1441", {"start": v(-0.26, -3.17) * mm, "end": v(-0.22, -3.08) * mm});
            skLineSegment(sketch, "E1442", {"start": v(-0.22, -3.08) * mm, "end": v(-0.18, -3) * mm});
            skLineSegment(sketch, "E1443", {"start": v(-0.18, -3) * mm, "end": v(-0.2, -2.56) * mm});
            skLineSegment(sketch, "E1444", {"start": v(-0.2, -2.56) * mm, "end": v(-0.46, -2.2) * mm});
            skLineSegment(sketch, "E1445", {"start": v(-0.46, -2.2) * mm, "end": v(-0.54, -2.16) * mm});
            skLineSegment(sketch, "E1446", {"start": v(-0.54, -2.16) * mm, "end": v(-0.56, -2.15) * mm});
            skLineSegment(sketch, "E1447", {"start": v(-0.56, -2.15) * mm, "end": v(-0.77, -2.1) * mm});
            skLineSegment(sketch, "E1448", {"start": v(-0.77, -2.1) * mm, "end": v(-0.84, -2.1) * mm});
            skLineSegment(sketch, "E1449", {"start": v(-0.84, -3.72) * mm, "end": v(-0.94, -3.72) * mm});
            skLineSegment(sketch, "E1450", {"start": v(-0.94, -3.72) * mm, "end": v(-1.21, -3.65) * mm});
            skLineSegment(sketch, "E1451", {"start": v(-1.21, -3.65) * mm, "end": v(-1.25, -3.63) * mm});
            skLineSegment(sketch, "E1452", {"start": v(-1.25, -3.63) * mm, "end": v(-1.36, -3.57) * mm});
            skLineSegment(sketch, "E1453", {"start": v(-1.36, -3.57) * mm, "end": v(-1.72, -3.1) * mm});
            skLineSegment(sketch, "E1454", {"start": v(-1.72, -3.1) * mm, "end": v(-1.74, -2.5) * mm});
            skLineSegment(sketch, "E1455", {"start": v(-1.74, -2.5) * mm, "end": v(-1.68, -2.38) * mm});
            skLineSegment(sketch, "E1456", {"start": v(-1.68, -2.38) * mm, "end": v(-1.63, -2.26) * mm});
            skLineSegment(sketch, "E1457", {"start": v(-1.63, -2.26) * mm, "end": v(-1.15, -1.9) * mm});
            skLineSegment(sketch, "E1458", {"start": v(-1.15, -1.9) * mm, "end": v(-0.55, -1.88) * mm});
            skLineSegment(sketch, "E1459", {"start": v(-0.55, -1.88) * mm, "end": v(-0.43, -1.94) * mm});
            skLineSegment(sketch, "E1460", {"start": v(-0.43, -1.94) * mm, "end": v(-0.32, -2) * mm});
            skLineSegment(sketch, "E1461", {"start": v(-0.32, -2) * mm, "end": v(0.05, -2.47) * mm});
            skLineSegment(sketch, "E1462", {"start": v(0.05, -2.47) * mm, "end": v(0.06, -3.07) * mm});
            skLineSegment(sketch, "E1463", {"start": v(0.06, -3.07) * mm, "end": v(0, -3.19) * mm});
            skLineSegment(sketch, "E1464", {"start": v(0, -3.19) * mm, "end": v(-0.03, -3.27) * mm});
            skLineSegment(sketch, "E1465", {"start": v(-0.03, -3.27) * mm, "end": v(-0.35, -3.58) * mm});
            skLineSegment(sketch, "E1466", {"start": v(-0.35, -3.58) * mm, "end": v(-0.72, -3.72) * mm});
            skLineSegment(sketch, "E1467", {"start": v(-0.72, -3.72) * mm, "end": v(-0.84, -3.72) * mm});
            skLineSegment(sketch, "E1468", {"start": v(-2.79, 3.68) * mm, "end": v(-2.9, 3.68) * mm});
            skLineSegment(sketch, "E1469", {"start": v(-2.9, 3.68) * mm, "end": v(-3.27, 3.54) * mm});
            skLineSegment(sketch, "E1470", {"start": v(-3.27, 3.54) * mm, "end": v(-3.57, 3.24) * mm});
            skLineSegment(sketch, "E1471", {"start": v(-3.57, 3.24) * mm, "end": v(-3.6, 3.16) * mm});
            skLineSegment(sketch, "E1472", {"start": v(-3.6, 3.16) * mm, "end": v(-3.64, 3.1) * mm});
            skLineSegment(sketch, "E1473", {"start": v(-3.64, 3.1) * mm, "end": v(-3.67, 2.52) * mm});
            skLineSegment(sketch, "E1474", {"start": v(-3.67, 2.52) * mm, "end": v(-3.65, 2.46) * mm});
            skLineSegment(sketch, "E1475", {"start": v(-3.65, 2.46) * mm, "end": v(-3.63, 2.4) * mm});
            skLineSegment(sketch, "E1476", {"start": v(-3.63, 2.4) * mm, "end": v(-3.24, 1.97) * mm});
            skLineSegment(sketch, "E1477", {"start": v(-3.24, 1.97) * mm, "end": v(-3.18, 1.94) * mm});
            skLineSegment(sketch, "E1478", {"start": v(-3.18, 1.94) * mm, "end": v(-3.13, 1.92) * mm});
            skLineSegment(sketch, "E1479", {"start": v(-3.13, 1.92) * mm, "end": v(-2.54, 1.89) * mm});
            skLineSegment(sketch, "E1480", {"start": v(-2.54, 1.89) * mm, "end": v(-2.49, 1.9) * mm});
            skLineSegment(sketch, "E1481", {"start": v(-2.49, 1.9) * mm, "end": v(-2.43, 1.92) * mm});
            skLineSegment(sketch, "E1482", {"start": v(-2.43, 1.92) * mm, "end": v(-2, 2.32) * mm});
            skLineSegment(sketch, "E1483", {"start": v(-2, 2.32) * mm, "end": v(-1.97, 2.37) * mm});
            skLineSegment(sketch, "E1484", {"start": v(-1.97, 2.37) * mm, "end": v(-1.91, 2.48) * mm});
            skLineSegment(sketch, "E1485", {"start": v(-1.91, 2.48) * mm, "end": v(-1.93, 3.07) * mm});
            skLineSegment(sketch, "E1486", {"start": v(-1.93, 3.07) * mm, "end": v(-2.28, 3.53) * mm});
            skLineSegment(sketch, "E1487", {"start": v(-2.28, 3.53) * mm, "end": v(-2.4, 3.59) * mm});
            skLineSegment(sketch, "E1488", {"start": v(-2.4, 3.59) * mm, "end": v(-2.42, 3.6) * mm});
            skLineSegment(sketch, "E1489", {"start": v(-2.42, 3.6) * mm, "end": v(-2.7, 3.68) * mm});
            skLineSegment(sketch, "E1490", {"start": v(-2.7, 3.68) * mm, "end": v(-2.79, 3.68) * mm});
            skLineSegment(sketch, "E1491", {"start": v(-2.79, 1.6) * mm, "end": v(-2.91, 1.6) * mm});
            skLineSegment(sketch, "E1492", {"start": v(-2.91, 1.6) * mm, "end": v(-3.25, 1.7) * mm});
            skLineSegment(sketch, "E1493", {"start": v(-3.25, 1.7) * mm, "end": v(-3.3, 1.72) * mm});
            skLineSegment(sketch, "E1494", {"start": v(-3.3, 1.72) * mm, "end": v(-3.36, 1.75) * mm});
            skLineSegment(sketch, "E1495", {"start": v(-3.36, 1.75) * mm, "end": v(-3.66, 2) * mm});
            skLineSegment(sketch, "E1496", {"start": v(-3.66, 2) * mm, "end": v(-3.86, 2.3) * mm});
            skLineSegment(sketch, "E1497", {"start": v(-3.86, 2.3) * mm, "end": v(-3.89, 2.38) * mm});
            skLineSegment(sketch, "E1498", {"start": v(-3.89, 2.38) * mm, "end": v(-3.91, 2.45) * mm});
            skLineSegment(sketch, "E1499", {"start": v(-3.91, 2.45) * mm, "end": v(-3.87, 3.2) * mm});
            skLineSegment(sketch, "E1500", {"start": v(-3.87, 3.2) * mm, "end": v(-3.84, 3.27) * mm});
            skLineSegment(sketch, "E1501", {"start": v(-3.84, 3.27) * mm, "end": v(-3.79, 3.37) * mm});
            skLineSegment(sketch, "E1502", {"start": v(-3.79, 3.37) * mm, "end": v(-3.56, 3.64) * mm});
            skLineSegment(sketch, "E1503", {"start": v(-3.56, 3.64) * mm, "end": v(-3.17, 3.86) * mm});
            skLineSegment(sketch, "E1504", {"start": v(-3.17, 3.86) * mm, "end": v(-2.73, 3.93) * mm});
            skLineSegment(sketch, "E1505", {"start": v(-2.73, 3.93) * mm, "end": v(-2.39, 3.86) * mm});
            skLineSegment(sketch, "E1506", {"start": v(-2.39, 3.86) * mm, "end": v(-2.28, 3.81) * mm});
            skLineSegment(sketch, "E1507", {"start": v(-2.28, 3.81) * mm, "end": v(-2.18, 3.77) * mm});
            skLineSegment(sketch, "E1508", {"start": v(-2.18, 3.77) * mm, "end": v(-1.92, 3.54) * mm});
            skLineSegment(sketch, "E1509", {"start": v(-1.92, 3.54) * mm, "end": v(-1.7, 3.15) * mm});
            skLineSegment(sketch, "E1510", {"start": v(-1.7, 3.15) * mm, "end": v(-1.63, 2.7) * mm});
            skLineSegment(sketch, "E1511", {"start": v(-1.63, 2.7) * mm, "end": v(-1.69, 2.36) * mm});
            skLineSegment(sketch, "E1512", {"start": v(-1.69, 2.36) * mm, "end": v(-1.74, 2.26) * mm});
            skLineSegment(sketch, "E1513", {"start": v(-1.74, 2.26) * mm, "end": v(-1.77, 2.2) * mm});
            skLineSegment(sketch, "E1514", {"start": v(-1.77, 2.2) * mm, "end": v(-2.01, 1.9) * mm});
            skLineSegment(sketch, "E1515", {"start": v(-2.01, 1.9) * mm, "end": v(-2.33, 1.7) * mm});
            skLineSegment(sketch, "E1516", {"start": v(-2.33, 1.7) * mm, "end": v(-2.4, 1.67) * mm});
            skLineSegment(sketch, "E1517", {"start": v(-2.4, 1.67) * mm, "end": v(-2.44, 1.66) * mm});
            skLineSegment(sketch, "E1518", {"start": v(-2.44, 1.66) * mm, "end": v(-2.7, 1.6) * mm});
            skLineSegment(sketch, "E1519", {"start": v(-2.7, 1.6) * mm, "end": v(-2.79, 1.6) * mm});
            skLineSegment(sketch, "E1520", {"start": v(2.18, -0.04) * mm, "end": v(2.14, -0.04) * mm});
            skLineSegment(sketch, "E1521", {"start": v(2.14, -0.04) * mm, "end": v(2.04, -0.06) * mm});
            skLineSegment(sketch, "E1522", {"start": v(2.04, -0.06) * mm, "end": v(2.03, -0.06) * mm});
            skLineSegment(sketch, "E1523", {"start": v(2.03, -0.06) * mm, "end": v(2, -0.07) * mm});
            skLineSegment(sketch, "E1524", {"start": v(2, -0.07) * mm, "end": v(1.8, -0.25) * mm});
            skLineSegment(sketch, "E1525", {"start": v(1.8, -0.25) * mm, "end": v(1.79, -0.28) * mm});
            skLineSegment(sketch, "E1526", {"start": v(1.79, -0.28) * mm, "end": v(1.78, -0.3) * mm});
            skLineSegment(sketch, "E1527", {"start": v(1.78, -0.3) * mm, "end": v(1.76, -0.58) * mm});
            skLineSegment(sketch, "E1528", {"start": v(1.76, -0.58) * mm, "end": v(1.77, -0.6) * mm});
            skLineSegment(sketch, "E1529", {"start": v(1.77, -0.6) * mm, "end": v(1.78, -0.63) * mm});
            skLineSegment(sketch, "E1530", {"start": v(1.78, -0.63) * mm, "end": v(1.96, -0.84) * mm});
            skLineSegment(sketch, "E1531", {"start": v(1.96, -0.84) * mm, "end": v(1.99, -0.85) * mm});
            skLineSegment(sketch, "E1532", {"start": v(1.99, -0.85) * mm, "end": v(2.04, -0.88) * mm});
            skLineSegment(sketch, "E1533", {"start": v(2.04, -0.88) * mm, "end": v(2.32, -0.87) * mm});
            skLineSegment(sketch, "E1534", {"start": v(2.32, -0.87) * mm, "end": v(2.53, -0.7) * mm});
            skLineSegment(sketch, "E1535", {"start": v(2.53, -0.7) * mm, "end": v(2.56, -0.65) * mm});
            skLineSegment(sketch, "E1536", {"start": v(2.56, -0.65) * mm, "end": v(2.57, -0.63) * mm});
            skLineSegment(sketch, "E1537", {"start": v(2.57, -0.63) * mm, "end": v(2.59, -0.35) * mm});
            skLineSegment(sketch, "E1538", {"start": v(2.59, -0.35) * mm, "end": v(2.58, -0.33) * mm});
            skLineSegment(sketch, "E1539", {"start": v(2.58, -0.33) * mm, "end": v(2.57, -0.3) * mm});
            skLineSegment(sketch, "E1540", {"start": v(2.57, -0.3) * mm, "end": v(2.39, -0.1) * mm});
            skLineSegment(sketch, "E1541", {"start": v(2.39, -0.1) * mm, "end": v(2.36, -0.08) * mm});
            skLineSegment(sketch, "E1542", {"start": v(2.36, -0.08) * mm, "end": v(2.34, -0.07) * mm});
            skLineSegment(sketch, "E1543", {"start": v(2.34, -0.07) * mm, "end": v(2.22, -0.04) * mm});
            skLineSegment(sketch, "E1544", {"start": v(2.22, -0.04) * mm, "end": v(2.18, -0.04) * mm});
            skLineSegment(sketch, "E1545", {"start": v(2.17, -1.15) * mm, "end": v(2.1, -1.15) * mm});
            skLineSegment(sketch, "E1546", {"start": v(2.1, -1.15) * mm, "end": v(1.9, -1.1) * mm});
            skLineSegment(sketch, "E1547", {"start": v(1.9, -1.1) * mm, "end": v(1.88, -1.08) * mm});
            skLineSegment(sketch, "E1548", {"start": v(1.88, -1.08) * mm, "end": v(1.84, -1.06) * mm});
            skLineSegment(sketch, "E1549", {"start": v(1.84, -1.06) * mm, "end": v(1.55, -0.73) * mm});
            skLineSegment(sketch, "E1550", {"start": v(1.55, -0.73) * mm, "end": v(1.53, -0.7) * mm});
            skLineSegment(sketch, "E1551", {"start": v(1.53, -0.7) * mm, "end": v(1.52, -0.65) * mm});
            skLineSegment(sketch, "E1552", {"start": v(1.52, -0.65) * mm, "end": v(1.54, -0.21) * mm});
            skLineSegment(sketch, "E1553", {"start": v(1.54, -0.21) * mm, "end": v(1.56, -0.17) * mm});
            skLineSegment(sketch, "E1554", {"start": v(1.56, -0.17) * mm, "end": v(1.58, -0.13) * mm});
            skLineSegment(sketch, "E1555", {"start": v(1.58, -0.13) * mm, "end": v(1.9, 0.16) * mm});
            skLineSegment(sketch, "E1556", {"start": v(1.9, 0.16) * mm, "end": v(1.95, 0.18) * mm});
            skLineSegment(sketch, "E1557", {"start": v(1.95, 0.18) * mm, "end": v(2, 0.2) * mm});
            skLineSegment(sketch, "E1558", {"start": v(2, 0.2) * mm, "end": v(2.43, 0.17) * mm});
            skLineSegment(sketch, "E1559", {"start": v(2.43, 0.17) * mm, "end": v(2.47, 0.15) * mm});
            skLineSegment(sketch, "E1560", {"start": v(2.47, 0.15) * mm, "end": v(2.51, 0.13) * mm});
            skLineSegment(sketch, "E1561", {"start": v(2.51, 0.13) * mm, "end": v(2.8, -0.2) * mm});
            skLineSegment(sketch, "E1562", {"start": v(2.8, -0.2) * mm, "end": v(2.82, -0.24) * mm});
            skLineSegment(sketch, "E1563", {"start": v(2.82, -0.24) * mm, "end": v(2.83, -0.28) * mm});
            skLineSegment(sketch, "E1564", {"start": v(2.83, -0.28) * mm, "end": v(2.8, -0.72) * mm});
            skLineSegment(sketch, "E1565", {"start": v(2.8, -0.72) * mm, "end": v(2.79, -0.76) * mm});
            skLineSegment(sketch, "E1566", {"start": v(2.79, -0.76) * mm, "end": v(2.77, -0.8) * mm});
            skLineSegment(sketch, "E1567", {"start": v(2.77, -0.8) * mm, "end": v(2.44, -1.1) * mm});
            skLineSegment(sketch, "E1568", {"start": v(2.44, -1.1) * mm, "end": v(2.4, -1.1) * mm});
            skLineSegment(sketch, "E1569", {"start": v(2.4, -1.1) * mm, "end": v(2.38, -1.11) * mm});
            skLineSegment(sketch, "E1570", {"start": v(2.38, -1.11) * mm, "end": v(2.23, -1.15) * mm});
            skLineSegment(sketch, "E1571", {"start": v(2.23, -1.15) * mm, "end": v(2.17, -1.15) * mm});
            skLineSegment(sketch, "E1572", {"start": v(-2.32, -2.2) * mm, "end": v(-2.33, -2.2) * mm});
            skLineSegment(sketch, "E1573", {"start": v(-2.33, -2.2) * mm, "end": v(-2.36, -2.19) * mm});
            skLineSegment(sketch, "E1574", {"start": v(-2.36, -2.19) * mm, "end": v(-2.37, -2.19) * mm});
            skLineSegment(sketch, "E1575", {"start": v(-2.37, -2.19) * mm, "end": v(-2.54, -2.05) * mm});
            skLineSegment(sketch, "E1576", {"start": v(-2.54, -2.05) * mm, "end": v(-3.16, -1.19) * mm});
            skLineSegment(sketch, "E1577", {"start": v(-3.16, -1.19) * mm, "end": v(-3.44, -0.26) * mm});
            skLineSegment(sketch, "E1578", {"start": v(-3.44, -0.26) * mm, "end": v(-3.44, 0.05) * mm});
            skLineSegment(sketch, "E1579", {"start": v(-3.44, 0.05) * mm, "end": v(-3.44, 0.12) * mm});
            skLineSegment(sketch, "E1580", {"start": v(-3.44, 0.12) * mm, "end": v(-3.43, 0.29) * mm});
            skLineSegment(sketch, "E1581", {"start": v(-3.43, 0.29) * mm, "end": v(-3.43, 0.3) * mm});
            skLineSegment(sketch, "E1582", {"start": v(-3.43, 0.3) * mm, "end": v(-3.43, 0.32) * mm});
            skLineSegment(sketch, "E1583", {"start": v(-3.43, 0.32) * mm, "end": v(-3.36, 0.37) * mm});
            skLineSegment(sketch, "E1584", {"start": v(-3.36, 0.37) * mm, "end": v(-3.35, 0.37) * mm});
            skLineSegment(sketch, "E1585", {"start": v(-3.35, 0.37) * mm, "end": v(-3.34, 0.37) * mm});
            skLineSegment(sketch, "E1586", {"start": v(-3.34, 0.37) * mm, "end": v(-3.28, 0.3) * mm});
            skLineSegment(sketch, "E1587", {"start": v(-3.28, 0.3) * mm, "end": v(-3.28, 0.3) * mm});
            skLineSegment(sketch, "E1588", {"start": v(-3.28, 0.3) * mm, "end": v(-3.28, 0.27) * mm});
            skLineSegment(sketch, "E1589", {"start": v(-3.28, 0.27) * mm, "end": v(-3.29, 0.1) * mm});
            skLineSegment(sketch, "E1590", {"start": v(-3.29, 0.1) * mm, "end": v(-3.29, 0.05) * mm});
            skLineSegment(sketch, "E1591", {"start": v(-3.29, 0.05) * mm, "end": v(-3.29, -0.24) * mm});
            skLineSegment(sketch, "E1592", {"start": v(-3.29, -0.24) * mm, "end": v(-3.02, -1.12) * mm});
            skLineSegment(sketch, "E1593", {"start": v(-3.02, -1.12) * mm, "end": v(-2.44, -1.94) * mm});
            skLineSegment(sketch, "E1594", {"start": v(-2.44, -1.94) * mm, "end": v(-2.27, -2.07) * mm});
            skLineSegment(sketch, "E1595", {"start": v(-2.27, -2.07) * mm, "end": v(-2.26, -2.07) * mm});
            skLineSegment(sketch, "E1596", {"start": v(-2.26, -2.07) * mm, "end": v(-2.26, -2.17) * mm});
            skLineSegment(sketch, "E1597", {"start": v(-2.26, -2.17) * mm, "end": v(-2.26, -2.18) * mm});
            skLineSegment(sketch, "E1598", {"start": v(-2.26, -2.18) * mm, "end": v(-2.27, -2.18) * mm});
            skLineSegment(sketch, "E1599", {"start": v(-2.27, -2.18) * mm, "end": v(-2.3, -2.2) * mm});
            skLineSegment(sketch, "E1600", {"start": v(-2.3, -2.2) * mm, "end": v(-2.32, -2.2) * mm});
            skLineSegment(sketch, "E1601", {"start": v(0.59, -2.67) * mm, "end": v(0.57, -2.67) * mm});
            skLineSegment(sketch, "E1602", {"start": v(0.57, -2.67) * mm, "end": v(0.52, -2.63) * mm});
            skLineSegment(sketch, "E1603", {"start": v(0.52, -2.63) * mm, "end": v(0.52, -2.62) * mm});
            skLineSegment(sketch, "E1604", {"start": v(0.52, -2.62) * mm, "end": v(0.51, -2.61) * mm});
            skLineSegment(sketch, "E1605", {"start": v(0.51, -2.61) * mm, "end": v(0.55, -2.53) * mm});
            skLineSegment(sketch, "E1606", {"start": v(0.55, -2.53) * mm, "end": v(0.56, -2.52) * mm});
            skLineSegment(sketch, "E1607", {"start": v(0.56, -2.52) * mm, "end": v(0.69, -2.47) * mm});
            skLineSegment(sketch, "E1608", {"start": v(0.69, -2.47) * mm, "end": v(1.27, -2.12) * mm});
            skLineSegment(sketch, "E1609", {"start": v(1.27, -2.12) * mm, "end": v(1.75, -1.63) * mm});
            skLineSegment(sketch, "E1610", {"start": v(1.75, -1.63) * mm, "end": v(1.83, -1.51) * mm});
            skLineSegment(sketch, "E1611", {"start": v(1.83, -1.51) * mm, "end": v(1.84, -1.5) * mm});
            skLineSegment(sketch, "E1612", {"start": v(1.84, -1.5) * mm, "end": v(1.93, -1.49) * mm});
            skLineSegment(sketch, "E1613", {"start": v(1.93, -1.49) * mm, "end": v(1.94, -1.5) * mm});
            skLineSegment(sketch, "E1614", {"start": v(1.94, -1.5) * mm, "end": v(1.95, -1.5) * mm});
            skLineSegment(sketch, "E1615", {"start": v(1.95, -1.5) * mm, "end": v(1.96, -1.59) * mm});
            skLineSegment(sketch, "E1616", {"start": v(1.96, -1.59) * mm, "end": v(1.96, -1.6) * mm});
            skLineSegment(sketch, "E1617", {"start": v(1.96, -1.6) * mm, "end": v(1.87, -1.72) * mm});
            skLineSegment(sketch, "E1618", {"start": v(1.87, -1.72) * mm, "end": v(1.37, -2.24) * mm});
            skLineSegment(sketch, "E1619", {"start": v(1.37, -2.24) * mm, "end": v(0.75, -2.61) * mm});
            skLineSegment(sketch, "E1620", {"start": v(0.75, -2.61) * mm, "end": v(0.62, -2.67) * mm});
            skLineSegment(sketch, "E1621", {"start": v(0.62, -2.67) * mm, "end": v(0.61, -2.67) * mm});
            skLineSegment(sketch, "E1622", {"start": v(0.61, -2.67) * mm, "end": v(0.6, -2.67) * mm});
            skLineSegment(sketch, "E1623", {"start": v(0.6, -2.67) * mm, "end": v(0.59, -2.67) * mm});
            skLineSegment(sketch, "E1624", {"start": v(2.28, 0.72) * mm, "end": v(2.26, 0.72) * mm});
            skLineSegment(sketch, "E1625", {"start": v(2.26, 0.72) * mm, "end": v(2.21, 0.77) * mm});
            skLineSegment(sketch, "E1626", {"start": v(2.21, 0.77) * mm, "end": v(2.2, 0.78) * mm});
            skLineSegment(sketch, "E1627", {"start": v(2.2, 0.78) * mm, "end": v(2.16, 1) * mm});
            skLineSegment(sketch, "E1628", {"start": v(2.16, 1) * mm, "end": v(1.85, 1.61) * mm});
            skLineSegment(sketch, "E1629", {"start": v(1.85, 1.61) * mm, "end": v(1.25, 2.27) * mm});
            skLineSegment(sketch, "E1630", {"start": v(1.25, 2.27) * mm, "end": v(0.47, 2.7) * mm});
            skLineSegment(sketch, "E1631", {"start": v(0.47, 2.7) * mm, "end": v(-0.2, 2.85) * mm});
            skLineSegment(sketch, "E1632", {"start": v(-0.2, 2.85) * mm, "end": v(-0.43, 2.85) * mm});
            skLineSegment(sketch, "E1633", {"start": v(-0.43, 2.85) * mm, "end": v(-0.65, 2.85) * mm});
            skLineSegment(sketch, "E1634", {"start": v(-0.65, 2.85) * mm, "end": v(-1.22, 2.73) * mm});
            skLineSegment(sketch, "E1635", {"start": v(-1.22, 2.73) * mm, "end": v(-1.29, 2.7) * mm});
            skLineSegment(sketch, "E1636", {"start": v(-1.29, 2.7) * mm, "end": v(-1.3, 2.7) * mm});
            skLineSegment(sketch, "E1637", {"start": v(-1.3, 2.7) * mm, "end": v(-1.38, 2.75) * mm});
            skLineSegment(sketch, "E1638", {"start": v(-1.38, 2.75) * mm, "end": v(-1.38, 2.76) * mm});
            skLineSegment(sketch, "E1639", {"start": v(-1.38, 2.76) * mm, "end": v(-1.39, 2.77) * mm});
            skLineSegment(sketch, "E1640", {"start": v(-1.39, 2.77) * mm, "end": v(-1.35, 2.85) * mm});
            skLineSegment(sketch, "E1641", {"start": v(-1.35, 2.85) * mm, "end": v(-1.34, 2.85) * mm});
            skLineSegment(sketch, "E1642", {"start": v(-1.34, 2.85) * mm, "end": v(-1.26, 2.88) * mm});
            skLineSegment(sketch, "E1643", {"start": v(-1.26, 2.88) * mm, "end": v(-0.64, 3) * mm});
            skLineSegment(sketch, "E1644", {"start": v(-0.64, 3) * mm, "end": v(-0.43, 3) * mm});
            skLineSegment(sketch, "E1645", {"start": v(-0.43, 3) * mm, "end": v(-0.2, 3) * mm});
            skLineSegment(sketch, "E1646", {"start": v(-0.2, 3) * mm, "end": v(0.52, 2.84) * mm});
            skLineSegment(sketch, "E1647", {"start": v(0.52, 2.84) * mm, "end": v(1.34, 2.39) * mm});
            skLineSegment(sketch, "E1648", {"start": v(1.34, 2.39) * mm, "end": v(1.97, 1.7) * mm});
            skLineSegment(sketch, "E1649", {"start": v(1.97, 1.7) * mm, "end": v(2.3, 1.04) * mm});
            skLineSegment(sketch, "E1650", {"start": v(2.3, 1.04) * mm, "end": v(2.36, 0.81) * mm});
            skLineSegment(sketch, "E1651", {"start": v(2.36, 0.81) * mm, "end": v(2.36, 0.8) * mm});
            skLineSegment(sketch, "E1652", {"start": v(2.36, 0.8) * mm, "end": v(2.31, 0.72) * mm});
            skLineSegment(sketch, "E1653", {"start": v(2.31, 0.72) * mm, "end": v(2.3, 0.72) * mm});
            skLineSegment(sketch, "E1654", {"start": v(2.3, 0.72) * mm, "end": v(2.3, 0.72) * mm});
            skLineSegment(sketch, "E1655", {"start": v(2.3, 0.72) * mm, "end": v(2.29, 0.72) * mm});
            skLineSegment(sketch, "E1656", {"start": v(2.29, 0.72) * mm, "end": v(2.28, 0.72) * mm});
            skLineSegment(sketch, "E1657", {"start": v(-1.07, 5.89) * mm, "end": v(-0.96, 6) * mm});
            skLineSegment(sketch, "E1658", {"start": v(-0.96, 6) * mm, "end": v(0.13, 7.08) * mm});
            skLineSegment(sketch, "E1659", {"start": v(0.13, 7.08) * mm, "end": v(0.24, 7.2) * mm});
            skLineSegment(sketch, "E1660", {"start": v(0.24, 7.2) * mm, "end": v(-0.17, 7.2) * mm});
            skLineSegment(sketch, "E1661", {"start": v(-0.17, 7.2) * mm, "end": v(1.07, 5.96) * mm});
            skLineSegment(sketch, "E1662", {"start": v(1.07, 5.96) * mm, "end": v(1.1, 5.92) * mm});
            skLineSegment(sketch, "E1663", {"start": v(1.1, 5.92) * mm, "end": v(1.28, 5.87) * mm});
            skLineSegment(sketch, "E1664", {"start": v(1.28, 5.87) * mm, "end": v(1.47, 5.96) * mm});
            skLineSegment(sketch, "E1665", {"start": v(1.47, 5.96) * mm, "end": v(1.55, 6.15) * mm});
            skLineSegment(sketch, "E1666", {"start": v(1.55, 6.15) * mm, "end": v(1.5, 6.32) * mm});
            skLineSegment(sketch, "E1667", {"start": v(1.5, 6.32) * mm, "end": v(1.47, 6.36) * mm});
            skLineSegment(sketch, "E1668", {"start": v(1.47, 6.36) * mm, "end": v(0.24, 7.6) * mm});
            skLineSegment(sketch, "E1669", {"start": v(0.24, 7.6) * mm, "end": v(0.2, 7.62) * mm});
            skLineSegment(sketch, "E1670", {"start": v(0.2, 7.62) * mm, "end": v(-0.14, 7.62) * mm});
            skLineSegment(sketch, "E1671", {"start": v(-0.14, 7.62) * mm, "end": v(-0.17, 7.6) * mm});
            skLineSegment(sketch, "E1672", {"start": v(-0.17, 7.6) * mm, "end": v(-1.47, 6.3) * mm});
            skLineSegment(sketch, "E1673", {"start": v(-1.47, 6.3) * mm, "end": v(-1.5, 6.26) * mm});
            skLineSegment(sketch, "E1674", {"start": v(-1.5, 6.26) * mm, "end": v(-1.56, 6.08) * mm});
            skLineSegment(sketch, "E1675", {"start": v(-1.56, 6.08) * mm, "end": v(-1.47, 5.9) * mm});
            skLineSegment(sketch, "E1676", {"start": v(-1.47, 5.9) * mm, "end": v(-1.28, 5.8) * mm});
            skLineSegment(sketch, "E1677", {"start": v(-1.28, 5.8) * mm, "end": v(-1.1, 5.85) * mm});
            skLineSegment(sketch, "E1678", {"start": v(-1.1, 5.85) * mm, "end": v(-1.07, 5.89) * mm});
            skLineSegment(sketch, "E1679", {"start": v(1.07, -5.9) * mm, "end": v(0.96, -6) * mm});
            skLineSegment(sketch, "E1680", {"start": v(0.96, -6) * mm, "end": v(-0.13, -7.09) * mm});
            skLineSegment(sketch, "E1681", {"start": v(-0.13, -7.09) * mm, "end": v(-0.24, -7.2) * mm});
            skLineSegment(sketch, "E1682", {"start": v(-0.24, -7.2) * mm, "end": v(0.17, -7.2) * mm});
            skLineSegment(sketch, "E1683", {"start": v(0.17, -7.2) * mm, "end": v(0.06, -7.1) * mm});
            skLineSegment(sketch, "E1684", {"start": v(0.06, -7.1) * mm, "end": v(-0.97, -6.06) * mm});
            skLineSegment(sketch, "E1685", {"start": v(-0.97, -6.06) * mm, "end": v(-1.07, -5.96) * mm});
            skLineSegment(sketch, "E1686", {"start": v(-1.07, -5.96) * mm, "end": v(-1.1, -5.92) * mm});
            skLineSegment(sketch, "E1687", {"start": v(-1.1, -5.92) * mm, "end": v(-1.28, -5.87) * mm});
            skLineSegment(sketch, "E1688", {"start": v(-1.28, -5.87) * mm, "end": v(-1.47, -5.96) * mm});
            skLineSegment(sketch, "E1689", {"start": v(-1.47, -5.96) * mm, "end": v(-1.56, -6.15) * mm});
            skLineSegment(sketch, "E1690", {"start": v(-1.56, -6.15) * mm, "end": v(-1.5, -6.32) * mm});
            skLineSegment(sketch, "E1691", {"start": v(-1.5, -6.32) * mm, "end": v(-1.47, -6.36) * mm});
            skLineSegment(sketch, "E1692", {"start": v(-1.47, -6.36) * mm, "end": v(-1.37, -6.46) * mm});
            skLineSegment(sketch, "E1693", {"start": v(-1.37, -6.46) * mm, "end": v(-0.34, -7.5) * mm});
            skLineSegment(sketch, "E1694", {"start": v(-0.34, -7.5) * mm, "end": v(-0.24, -7.6) * mm});
            skLineSegment(sketch, "E1695", {"start": v(-0.24, -7.6) * mm, "end": v(-0.2, -7.62) * mm});
            skLineSegment(sketch, "E1696", {"start": v(-0.2, -7.62) * mm, "end": v(0.14, -7.62) * mm});
            skLineSegment(sketch, "E1697", {"start": v(0.14, -7.62) * mm, "end": v(0.17, -7.6) * mm});
            skLineSegment(sketch, "E1698", {"start": v(0.17, -7.6) * mm, "end": v(0.28, -7.49) * mm});
            skLineSegment(sketch, "E1699", {"start": v(0.28, -7.49) * mm, "end": v(1.36, -6.4) * mm});
            skLineSegment(sketch, "E1700", {"start": v(1.36, -6.4) * mm, "end": v(1.47, -6.3) * mm});
            skLineSegment(sketch, "E1701", {"start": v(1.47, -6.3) * mm, "end": v(1.5, -6.26) * mm});
            skLineSegment(sketch, "E1702", {"start": v(1.5, -6.26) * mm, "end": v(1.55, -6.08) * mm});
            skLineSegment(sketch, "E1703", {"start": v(1.55, -6.08) * mm, "end": v(1.47, -5.9) * mm});
            skLineSegment(sketch, "E1704", {"start": v(1.47, -5.9) * mm, "end": v(1.28, -5.8) * mm});
            skLineSegment(sketch, "E1705", {"start": v(1.28, -5.8) * mm, "end": v(1.1, -5.85) * mm});
            skLineSegment(sketch, "E1706", {"start": v(1.1, -5.85) * mm, "end": v(1.07, -5.9) * mm});
            skLineSegment(sketch, "E1707", {"start": v(-5.9, -1.07) * mm, "end": v(-6, -0.96) * mm});
            skLineSegment(sketch, "E1708", {"start": v(-6, -0.96) * mm, "end": v(-7.09, 0.13) * mm});
            skLineSegment(sketch, "E1709", {"start": v(-7.09, 0.13) * mm, "end": v(-7.2, 0.23) * mm});
            skLineSegment(sketch, "E1710", {"start": v(-7.2, 0.23) * mm, "end": v(-7.2, -0.17) * mm});
            skLineSegment(sketch, "E1711", {"start": v(-7.2, -0.17) * mm, "end": v(-5.96, 1.07) * mm});
            skLineSegment(sketch, "E1712", {"start": v(-5.96, 1.07) * mm, "end": v(-5.92, 1.1) * mm});
            skLineSegment(sketch, "E1713", {"start": v(-5.92, 1.1) * mm, "end": v(-5.87, 1.28) * mm});
            skLineSegment(sketch, "E1714", {"start": v(-5.87, 1.28) * mm, "end": v(-5.96, 1.47) * mm});
            skLineSegment(sketch, "E1715", {"start": v(-5.96, 1.47) * mm, "end": v(-6.15, 1.55) * mm});
            skLineSegment(sketch, "E1716", {"start": v(-6.15, 1.55) * mm, "end": v(-6.32, 1.5) * mm});
            skLineSegment(sketch, "E1717", {"start": v(-6.32, 1.5) * mm, "end": v(-6.36, 1.47) * mm});
            skLineSegment(sketch, "E1718", {"start": v(-6.36, 1.47) * mm, "end": v(-7.6, 0.23) * mm});
            skLineSegment(sketch, "E1719", {"start": v(-7.6, 0.23) * mm, "end": v(-7.62, 0.2) * mm});
            skLineSegment(sketch, "E1720", {"start": v(-7.62, 0.2) * mm, "end": v(-7.62, -0.14) * mm});
            skLineSegment(sketch, "E1721", {"start": v(-7.62, -0.14) * mm, "end": v(-7.6, -0.17) * mm});
            skLineSegment(sketch, "E1722", {"start": v(-7.6, -0.17) * mm, "end": v(-7.49, -0.28) * mm});
            skLineSegment(sketch, "E1723", {"start": v(-7.49, -0.28) * mm, "end": v(-6.4, -1.36) * mm});
            skLineSegment(sketch, "E1724", {"start": v(-6.4, -1.36) * mm, "end": v(-6.3, -1.47) * mm});
            skLineSegment(sketch, "E1725", {"start": v(-6.3, -1.47) * mm, "end": v(-6.26, -1.5) * mm});
            skLineSegment(sketch, "E1726", {"start": v(-6.26, -1.5) * mm, "end": v(-6.08, -1.56) * mm});
            skLineSegment(sketch, "E1727", {"start": v(-6.08, -1.56) * mm, "end": v(-5.9, -1.47) * mm});
            skLineSegment(sketch, "E1728", {"start": v(-5.9, -1.47) * mm, "end": v(-5.8, -1.28) * mm});
            skLineSegment(sketch, "E1729", {"start": v(-5.8, -1.28) * mm, "end": v(-5.85, -1.1) * mm});
            skLineSegment(sketch, "E1730", {"start": v(-5.85, -1.1) * mm, "end": v(-5.9, -1.07) * mm});
            skLineSegment(sketch, "E1731", {"start": v(5.9, 1.07) * mm, "end": v(6, 0.96) * mm});
            skLineSegment(sketch, "E1732", {"start": v(6, 0.96) * mm, "end": v(7.09, -0.13) * mm});
            skLineSegment(sketch, "E1733", {"start": v(7.09, -0.13) * mm, "end": v(7.2, -0.24) * mm});
            skLineSegment(sketch, "E1734", {"start": v(7.2, -0.24) * mm, "end": v(7.2, 0.17) * mm});
            skLineSegment(sketch, "E1735", {"start": v(7.2, 0.17) * mm, "end": v(5.96, -1.07) * mm});
            skLineSegment(sketch, "E1736", {"start": v(5.96, -1.07) * mm, "end": v(5.92, -1.1) * mm});
            skLineSegment(sketch, "E1737", {"start": v(5.92, -1.1) * mm, "end": v(5.87, -1.28) * mm});
            skLineSegment(sketch, "E1738", {"start": v(5.87, -1.28) * mm, "end": v(5.96, -1.47) * mm});
            skLineSegment(sketch, "E1739", {"start": v(5.96, -1.47) * mm, "end": v(6.15, -1.56) * mm});
            skLineSegment(sketch, "E1740", {"start": v(6.15, -1.56) * mm, "end": v(6.32, -1.5) * mm});
            skLineSegment(sketch, "E1741", {"start": v(6.32, -1.5) * mm, "end": v(6.36, -1.47) * mm});
            skLineSegment(sketch, "E1742", {"start": v(6.36, -1.47) * mm, "end": v(7.6, -0.24) * mm});
            skLineSegment(sketch, "E1743", {"start": v(7.6, -0.24) * mm, "end": v(7.62, -0.2) * mm});
            skLineSegment(sketch, "E1744", {"start": v(7.62, -0.2) * mm, "end": v(7.62, 0.14) * mm});
            skLineSegment(sketch, "E1745", {"start": v(7.62, 0.14) * mm, "end": v(7.6, 0.17) * mm});
            skLineSegment(sketch, "E1746", {"start": v(7.6, 0.17) * mm, "end": v(7.49, 0.28) * mm});
            skLineSegment(sketch, "E1747", {"start": v(7.49, 0.28) * mm, "end": v(6.4, 1.36) * mm});
            skLineSegment(sketch, "E1748", {"start": v(6.4, 1.36) * mm, "end": v(6.3, 1.47) * mm});
            skLineSegment(sketch, "E1749", {"start": v(6.3, 1.47) * mm, "end": v(6.26, 1.5) * mm});
            skLineSegment(sketch, "E1750", {"start": v(6.26, 1.5) * mm, "end": v(6.08, 1.55) * mm});
            skLineSegment(sketch, "E1751", {"start": v(6.08, 1.55) * mm, "end": v(5.9, 1.47) * mm});
            skLineSegment(sketch, "E1752", {"start": v(5.9, 1.47) * mm, "end": v(5.8, 1.28) * mm});
            skLineSegment(sketch, "E1753", {"start": v(5.8, 1.28) * mm, "end": v(5.85, 1.1) * mm});
            skLineSegment(sketch, "E1754", {"start": v(5.85, 1.1) * mm, "end": v(5.9, 1.07) * mm});
            skLineSegment(sketch, "E1755", {"start": v(-5.1, 6.32) * mm, "end": v(-5.1, 6.22) * mm});
            skLineSegment(sketch, "E1756", {"start": v(-5.1, 6.22) * mm, "end": v(-5.18, 5.93) * mm});
            skLineSegment(sketch, "E1757", {"start": v(-5.18, 5.93) * mm, "end": v(-5.4, 5.61) * mm});
            skLineSegment(sketch, "E1758", {"start": v(-5.4, 5.61) * mm, "end": v(-5.71, 5.4) * mm});
            skLineSegment(sketch, "E1759", {"start": v(-5.71, 5.4) * mm, "end": v(-6, 5.32) * mm});
            skLineSegment(sketch, "E1760", {"start": v(-6, 5.32) * mm, "end": v(-6.1, 5.32) * mm});
            skLineSegment(sketch, "E1761", {"start": v(-6.1, 5.32) * mm, "end": v(-6.2, 5.32) * mm});
            skLineSegment(sketch, "E1762", {"start": v(-6.2, 5.32) * mm, "end": v(-6.49, 5.4) * mm});
            skLineSegment(sketch, "E1763", {"start": v(-6.49, 5.4) * mm, "end": v(-6.8, 5.61) * mm});
            skLineSegment(sketch, "E1764", {"start": v(-6.8, 5.61) * mm, "end": v(-7.02, 5.93) * mm});
            skLineSegment(sketch, "E1765", {"start": v(-7.02, 5.93) * mm, "end": v(-7.1, 6.22) * mm});
            skLineSegment(sketch, "E1766", {"start": v(-7.1, 6.22) * mm, "end": v(-7.1, 6.32) * mm});
            skLineSegment(sketch, "E1767", {"start": v(-7.1, 6.32) * mm, "end": v(-7.1, 6.41) * mm});
            skLineSegment(sketch, "E1768", {"start": v(-7.1, 6.41) * mm, "end": v(-7.02, 6.7) * mm});
            skLineSegment(sketch, "E1769", {"start": v(-7.02, 6.7) * mm, "end": v(-6.8, 7.02) * mm});
            skLineSegment(sketch, "E1770", {"start": v(-6.8, 7.02) * mm, "end": v(-6.49, 7.24) * mm});
            skLineSegment(sketch, "E1771", {"start": v(-6.49, 7.24) * mm, "end": v(-6.2, 7.31) * mm});
            skLineSegment(sketch, "E1772", {"start": v(-6.2, 7.31) * mm, "end": v(-6.1, 7.31) * mm});
            skLineSegment(sketch, "E1773", {"start": v(-6.1, 7.31) * mm, "end": v(-6, 7.31) * mm});
            skLineSegment(sketch, "E1774", {"start": v(-6, 7.31) * mm, "end": v(-5.71, 7.24) * mm});
            skLineSegment(sketch, "E1775", {"start": v(-5.71, 7.24) * mm, "end": v(-5.4, 7.02) * mm});
            skLineSegment(sketch, "E1776", {"start": v(-5.4, 7.02) * mm, "end": v(-5.18, 6.7) * mm});
            skLineSegment(sketch, "E1777", {"start": v(-5.18, 6.7) * mm, "end": v(-5.1, 6.41) * mm});
            skLineSegment(sketch, "E1778", {"start": v(-5.1, 6.41) * mm, "end": v(-5.1, 6.32) * mm});
            skLineSegment(sketch, "E1779", {"start": v(7.59, 6.32) * mm, "end": v(7.59, 6.22) * mm});
            skLineSegment(sketch, "E1780", {"start": v(7.59, 6.22) * mm, "end": v(7.5, 5.93) * mm});
            skLineSegment(sketch, "E1781", {"start": v(7.5, 5.93) * mm, "end": v(7.3, 5.61) * mm});
            skLineSegment(sketch, "E1782", {"start": v(7.3, 5.61) * mm, "end": v(6.98, 5.4) * mm});
            skLineSegment(sketch, "E1783", {"start": v(6.98, 5.4) * mm, "end": v(6.69, 5.32) * mm});
            skLineSegment(sketch, "E1784", {"start": v(6.69, 5.32) * mm, "end": v(6.6, 5.32) * mm});
            skLineSegment(sketch, "E1785", {"start": v(6.6, 5.32) * mm, "end": v(6.5, 5.32) * mm});
            skLineSegment(sketch, "E1786", {"start": v(6.5, 5.32) * mm, "end": v(6.2, 5.4) * mm});
            skLineSegment(sketch, "E1787", {"start": v(6.2, 5.4) * mm, "end": v(5.89, 5.61) * mm});
            skLineSegment(sketch, "E1788", {"start": v(5.89, 5.61) * mm, "end": v(5.67, 5.93) * mm});
            skLineSegment(sketch, "E1789", {"start": v(5.67, 5.93) * mm, "end": v(5.6, 6.22) * mm});
            skLineSegment(sketch, "E1790", {"start": v(5.6, 6.22) * mm, "end": v(5.6, 6.32) * mm});
            skLineSegment(sketch, "E1791", {"start": v(5.6, 6.32) * mm, "end": v(5.6, 6.41) * mm});
            skLineSegment(sketch, "E1792", {"start": v(5.6, 6.41) * mm, "end": v(5.67, 6.7) * mm});
            skLineSegment(sketch, "E1793", {"start": v(5.67, 6.7) * mm, "end": v(5.89, 7.02) * mm});
            skLineSegment(sketch, "E1794", {"start": v(5.89, 7.02) * mm, "end": v(6.2, 7.24) * mm});
            skLineSegment(sketch, "E1795", {"start": v(6.2, 7.24) * mm, "end": v(6.5, 7.31) * mm});
            skLineSegment(sketch, "E1796", {"start": v(6.5, 7.31) * mm, "end": v(6.6, 7.31) * mm});
            skLineSegment(sketch, "E1797", {"start": v(6.6, 7.31) * mm, "end": v(6.69, 7.31) * mm});
            skLineSegment(sketch, "E1798", {"start": v(6.69, 7.31) * mm, "end": v(6.98, 7.24) * mm});
            skLineSegment(sketch, "E1799", {"start": v(6.98, 7.24) * mm, "end": v(7.3, 7.02) * mm});
            skLineSegment(sketch, "E1800", {"start": v(7.3, 7.02) * mm, "end": v(7.5, 6.7) * mm});
            skLineSegment(sketch, "E1801", {"start": v(7.5, 6.7) * mm, "end": v(7.59, 6.41) * mm});
            skLineSegment(sketch, "E1802", {"start": v(7.59, 6.41) * mm, "end": v(7.59, 6.32) * mm});
            skLineSegment(sketch, "E1803", {"start": v(7.59, -6.46) * mm, "end": v(7.59, -6.56) * mm});
            skLineSegment(sketch, "E1804", {"start": v(7.59, -6.56) * mm, "end": v(7.5, -6.85) * mm});
            skLineSegment(sketch, "E1805", {"start": v(7.5, -6.85) * mm, "end": v(7.3, -7.16) * mm});
            skLineSegment(sketch, "E1806", {"start": v(7.3, -7.16) * mm, "end": v(6.98, -7.38) * mm});
            skLineSegment(sketch, "E1807", {"start": v(6.98, -7.38) * mm, "end": v(6.69, -7.46) * mm});
            skLineSegment(sketch, "E1808", {"start": v(6.69, -7.46) * mm, "end": v(6.6, -7.46) * mm});
            skLineSegment(sketch, "E1809", {"start": v(6.6, -7.46) * mm, "end": v(6.5, -7.46) * mm});
            skLineSegment(sketch, "E1810", {"start": v(6.5, -7.46) * mm, "end": v(6.2, -7.38) * mm});
            skLineSegment(sketch, "E1811", {"start": v(6.2, -7.38) * mm, "end": v(5.89, -7.16) * mm});
            skLineSegment(sketch, "E1812", {"start": v(5.89, -7.16) * mm, "end": v(5.67, -6.85) * mm});
            skLineSegment(sketch, "E1813", {"start": v(5.67, -6.85) * mm, "end": v(5.6, -6.56) * mm});
            skLineSegment(sketch, "E1814", {"start": v(5.6, -6.56) * mm, "end": v(5.6, -6.46) * mm});
            skLineSegment(sketch, "E1815", {"start": v(5.6, -6.46) * mm, "end": v(5.6, -6.36) * mm});
            skLineSegment(sketch, "E1816", {"start": v(5.6, -6.36) * mm, "end": v(5.67, -6.07) * mm});
            skLineSegment(sketch, "E1817", {"start": v(5.67, -6.07) * mm, "end": v(5.89, -5.75) * mm});
            skLineSegment(sketch, "E1818", {"start": v(5.89, -5.75) * mm, "end": v(6.2, -5.54) * mm});
            skLineSegment(sketch, "E1819", {"start": v(6.2, -5.54) * mm, "end": v(6.5, -5.46) * mm});
            skLineSegment(sketch, "E1820", {"start": v(6.5, -5.46) * mm, "end": v(6.6, -5.46) * mm});
            skLineSegment(sketch, "E1821", {"start": v(6.6, -5.46) * mm, "end": v(6.69, -5.46) * mm});
            skLineSegment(sketch, "E1822", {"start": v(6.69, -5.46) * mm, "end": v(6.98, -5.54) * mm});
            skLineSegment(sketch, "E1823", {"start": v(6.98, -5.54) * mm, "end": v(7.3, -5.75) * mm});
            skLineSegment(sketch, "E1824", {"start": v(7.3, -5.75) * mm, "end": v(7.5, -6.07) * mm});
            skLineSegment(sketch, "E1825", {"start": v(7.5, -6.07) * mm, "end": v(7.59, -6.36) * mm});
            skLineSegment(sketch, "E1826", {"start": v(7.59, -6.36) * mm, "end": v(7.59, -6.46) * mm});
            skSolve(sketch);
        }
        {
            var Q0;
            Q0 = qSketchRegion(id + "F7", true);
            extrude(context, id + "F8", {"entities" : qUnion([Q0]), "operationType" : NewBodyOperationType.REMOVE, "oppositeDirection" : true, "depth" : 3 * mm});
        }
        {
            var Q0;
            Q0=makeQuery(id+"F1.opExtrude","SWEPT_FACE",FACE,{"disambiguationData":[OSD([sQuery(id+"F0.wireOp",EDGE,"E0.right")])]});
            var sketch = newSketch(context, id + "F9", { "sketchPlane" : qUnion([Q0])});
            skLineSegment(sketch, "E1827", {"start": v(-14.43, -2.6) * mm, "end": v(-12.86, -2.6) * mm});
            skLineSegment(sketch, "E1828", {"start": v(-12.86, -2.6) * mm, "end": v(-12.86, -1.97) * mm});
            skLineSegment(sketch, "E1829", {"start": v(-12.86, -1.97) * mm, "end": v(-12.86, -1.78) * mm});
            skLineSegment(sketch, "E1830", {"start": v(-12.86, -1.78) * mm, "end": v(-12.68, -1.2) * mm});
            skLineSegment(sketch, "E1831", {"start": v(-12.68, -1.2) * mm, "end": v(-12.28, -0.7) * mm});
            skLineSegment(sketch, "E1832", {"start": v(-12.28, -0.7) * mm, "end": v(-12.18, -0.63) * mm});
            skLineSegment(sketch, "E1833", {"start": v(-12.18, -0.63) * mm, "end": v(-12, -0.5) * mm});
            skLineSegment(sketch, "E1834", {"start": v(-12, -0.5) * mm, "end": v(-11.37, 0.3) * mm});
            skLineSegment(sketch, "E1835", {"start": v(-11.37, 0.3) * mm, "end": v(-11.07, 1.2) * mm});
            skLineSegment(sketch, "E1836", {"start": v(-11.07, 1.2) * mm, "end": v(-11.07, 1.49) * mm});
            skLineSegment(sketch, "E1837", {"start": v(-11.07, 1.49) * mm, "end": v(-11.07, 1.75) * mm});
            skLineSegment(sketch, "E1838", {"start": v(-11.07, 1.75) * mm, "end": v(-11.29, 2.51) * mm});
            skLineSegment(sketch, "E1839", {"start": v(-11.29, 2.51) * mm, "end": v(-11.76, 3.25) * mm});
            skLineSegment(sketch, "E1840", {"start": v(-11.76, 3.25) * mm, "end": v(-11.9, 3.37) * mm});
            skLineSegment(sketch, "E1841", {"start": v(-11.9, 3.37) * mm, "end": v(-12.02, 3.5) * mm});
            skLineSegment(sketch, "E1842", {"start": v(-12.02, 3.5) * mm, "end": v(-12.79, 3.92) * mm});
            skLineSegment(sketch, "E1843", {"start": v(-12.79, 3.92) * mm, "end": v(-13.65, 4.07) * mm});
            skLineSegment(sketch, "E1844", {"start": v(-13.65, 4.07) * mm, "end": v(-13.83, 4.06) * mm});
            skLineSegment(sketch, "E1845", {"start": v(-13.83, 4.06) * mm, "end": v(-14.06, 4.04) * mm});
            skLineSegment(sketch, "E1846", {"start": v(-14.06, 4.04) * mm, "end": v(-14.72, 3.83) * mm});
            skLineSegment(sketch, "E1847", {"start": v(-14.72, 3.83) * mm, "end": v(-15.46, 3.31) * mm});
            skLineSegment(sketch, "E1848", {"start": v(-15.46, 3.31) * mm, "end": v(-15.98, 2.58) * mm});
            skLineSegment(sketch, "E1849", {"start": v(-15.98, 2.58) * mm, "end": v(-16.2, 1.91) * mm});
            skLineSegment(sketch, "E1850", {"start": v(-16.2, 1.91) * mm, "end": v(-16.21, 1.69) * mm});
            skLineSegment(sketch, "E1851", {"start": v(-16.21, 1.69) * mm, "end": v(-16.23, 1.46) * mm});
            skLineSegment(sketch, "E1852", {"start": v(-16.23, 1.46) * mm, "end": v(-15.98, 0.4) * mm});
            skLineSegment(sketch, "E1853", {"start": v(-15.98, 0.4) * mm, "end": v(-15.32, -0.48) * mm});
            skLineSegment(sketch, "E1854", {"start": v(-15.32, -0.48) * mm, "end": v(-15.14, -0.6) * mm});
            skLineSegment(sketch, "E1855", {"start": v(-15.14, -0.6) * mm, "end": v(-15.03, -0.69) * mm});
            skLineSegment(sketch, "E1856", {"start": v(-15.03, -0.69) * mm, "end": v(-14.62, -1.2) * mm});
            skLineSegment(sketch, "E1857", {"start": v(-14.62, -1.2) * mm, "end": v(-14.43, -1.77) * mm});
            skLineSegment(sketch, "E1858", {"start": v(-14.43, -1.77) * mm, "end": v(-14.43, -1.96) * mm});
            skLineSegment(sketch, "E1859", {"start": v(-14.43, -1.96) * mm, "end": v(-14.43, -2.6) * mm});
            skLineSegment(sketch, "E1860", {"start": v(-12.73, -2.87) * mm, "end": v(-14.56, -2.87) * mm});
            skLineSegment(sketch, "E1861", {"start": v(-14.56, -2.87) * mm, "end": v(-14.6, -2.87) * mm});
            skLineSegment(sketch, "E1862", {"start": v(-14.6, -2.87) * mm, "end": v(-14.7, -2.77) * mm});
            skLineSegment(sketch, "E1863", {"start": v(-14.7, -2.77) * mm, "end": v(-14.7, -2.73) * mm});
            skLineSegment(sketch, "E1864", {"start": v(-14.7, -2.73) * mm, "end": v(-14.7, -1.96) * mm});
            skLineSegment(sketch, "E1865", {"start": v(-14.7, -1.96) * mm, "end": v(-14.7, -1.8) * mm});
            skLineSegment(sketch, "E1866", {"start": v(-14.7, -1.8) * mm, "end": v(-14.85, -1.33) * mm});
            skLineSegment(sketch, "E1867", {"start": v(-14.85, -1.33) * mm, "end": v(-15.2, -0.9) * mm});
            skLineSegment(sketch, "E1868", {"start": v(-15.2, -0.9) * mm, "end": v(-15.3, -0.83) * mm});
            skLineSegment(sketch, "E1869", {"start": v(-15.3, -0.83) * mm, "end": v(-15.44, -0.72) * mm});
            skLineSegment(sketch, "E1870", {"start": v(-15.44, -0.72) * mm, "end": v(-15.83, -0.33) * mm});
            skLineSegment(sketch, "E1871", {"start": v(-15.83, -0.33) * mm, "end": v(-16.22, 0.28) * mm});
            skLineSegment(sketch, "E1872", {"start": v(-16.22, 0.28) * mm, "end": v(-16.44, 0.97) * mm});
            skLineSegment(sketch, "E1873", {"start": v(-16.44, 0.97) * mm, "end": v(-16.5, 1.52) * mm});
            skLineSegment(sketch, "E1874", {"start": v(-16.5, 1.52) * mm, "end": v(-16.48, 1.7) * mm});
            skLineSegment(sketch, "E1875", {"start": v(-16.48, 1.7) * mm, "end": v(-16.46, 1.96) * mm});
            skLineSegment(sketch, "E1876", {"start": v(-16.46, 1.96) * mm, "end": v(-16.22, 2.7) * mm});
            skLineSegment(sketch, "E1877", {"start": v(-16.22, 2.7) * mm, "end": v(-15.65, 3.5) * mm});
            skLineSegment(sketch, "E1878", {"start": v(-15.65, 3.5) * mm, "end": v(-14.83, 4.07) * mm});
            skLineSegment(sketch, "E1879", {"start": v(-14.83, 4.07) * mm, "end": v(-14.1, 4.3) * mm});
            skLineSegment(sketch, "E1880", {"start": v(-14.1, 4.3) * mm, "end": v(-13.85, 4.32) * mm});
            skLineSegment(sketch, "E1881", {"start": v(-13.85, 4.32) * mm, "end": v(-13.65, 4.34) * mm});
            skLineSegment(sketch, "E1882", {"start": v(-13.65, 4.34) * mm, "end": v(-12.7, 4.17) * mm});
            skLineSegment(sketch, "E1883", {"start": v(-12.7, 4.17) * mm, "end": v(-11.85, 3.7) * mm});
            skLineSegment(sketch, "E1884", {"start": v(-11.85, 3.7) * mm, "end": v(-11.7, 3.57) * mm});
            skLineSegment(sketch, "E1885", {"start": v(-11.7, 3.57) * mm, "end": v(-11.56, 3.43) * mm});
            skLineSegment(sketch, "E1886", {"start": v(-11.56, 3.43) * mm, "end": v(-11.04, 2.62) * mm});
            skLineSegment(sketch, "E1887", {"start": v(-11.04, 2.62) * mm, "end": v(-10.8, 1.77) * mm});
            skLineSegment(sketch, "E1888", {"start": v(-10.8, 1.77) * mm, "end": v(-10.8, 1.49) * mm});
            skLineSegment(sketch, "E1889", {"start": v(-10.8, 1.49) * mm, "end": v(-10.8, 1.16) * mm});
            skLineSegment(sketch, "E1890", {"start": v(-10.8, 1.16) * mm, "end": v(-11.13, 0.17) * mm});
            skLineSegment(sketch, "E1891", {"start": v(-11.13, 0.17) * mm, "end": v(-11.83, -0.71) * mm});
            skLineSegment(sketch, "E1892", {"start": v(-11.83, -0.71) * mm, "end": v(-12.02, -0.85) * mm});
            skLineSegment(sketch, "E1893", {"start": v(-12.02, -0.85) * mm, "end": v(-12.11, -0.9) * mm});
            skLineSegment(sketch, "E1894", {"start": v(-12.11, -0.9) * mm, "end": v(-12.44, -1.33) * mm});
            skLineSegment(sketch, "E1895", {"start": v(-12.44, -1.33) * mm, "end": v(-12.6, -1.8) * mm});
            skLineSegment(sketch, "E1896", {"start": v(-12.6, -1.8) * mm, "end": v(-12.6, -1.97) * mm});
            skLineSegment(sketch, "E1897", {"start": v(-12.6, -1.97) * mm, "end": v(-12.6, -2.73) * mm});
            skLineSegment(sketch, "E1898", {"start": v(-12.6, -2.73) * mm, "end": v(-12.6, -2.77) * mm});
            skLineSegment(sketch, "E1899", {"start": v(-12.6, -2.77) * mm, "end": v(-12.7, -2.87) * mm});
            skLineSegment(sketch, "E1900", {"start": v(-12.7, -2.87) * mm, "end": v(-12.73, -2.87) * mm});
            skLineSegment(sketch, "E1901", {"start": v(-14.4, -3.63) * mm, "end": v(-14.4, -3.67) * mm});
            skLineSegment(sketch, "E1902", {"start": v(-14.4, -3.67) * mm, "end": v(-14.25, -3.86) * mm});
            skLineSegment(sketch, "E1903", {"start": v(-14.25, -3.86) * mm, "end": v(-14.04, -3.95) * mm});
            skLineSegment(sketch, "E1904", {"start": v(-14.04, -3.95) * mm, "end": v(-13.97, -3.95) * mm});
            skLineSegment(sketch, "E1905", {"start": v(-13.97, -3.95) * mm, "end": v(-13.32, -3.95) * mm});
            skLineSegment(sketch, "E1906", {"start": v(-13.32, -3.95) * mm, "end": v(-13.25, -3.95) * mm});
            skLineSegment(sketch, "E1907", {"start": v(-13.25, -3.95) * mm, "end": v(-13.05, -3.86) * mm});
            skLineSegment(sketch, "E1908", {"start": v(-13.05, -3.86) * mm, "end": v(-12.9, -3.67) * mm});
            skLineSegment(sketch, "E1909", {"start": v(-12.9, -3.67) * mm, "end": v(-12.88, -3.63) * mm});
            skLineSegment(sketch, "E1910", {"start": v(-12.88, -3.63) * mm, "end": v(-14.4, -3.63) * mm});
            skLineSegment(sketch, "E1911", {"start": v(-13.32, -4.22) * mm, "end": v(-13.97, -4.22) * mm});
            skLineSegment(sketch, "E1912", {"start": v(-13.97, -4.22) * mm, "end": v(-14.1, -4.22) * mm});
            skLineSegment(sketch, "E1913", {"start": v(-14.1, -4.22) * mm, "end": v(-14.49, -4) * mm});
            skLineSegment(sketch, "E1914", {"start": v(-14.49, -4) * mm, "end": v(-14.7, -3.62) * mm});
            skLineSegment(sketch, "E1915", {"start": v(-14.7, -3.62) * mm, "end": v(-14.7, -3.5) * mm});
            skLineSegment(sketch, "E1916", {"start": v(-14.7, -3.5) * mm, "end": v(-14.7, -3.46) * mm});
            skLineSegment(sketch, "E1917", {"start": v(-14.7, -3.46) * mm, "end": v(-14.6, -3.36) * mm});
            skLineSegment(sketch, "E1918", {"start": v(-14.6, -3.36) * mm, "end": v(-14.56, -3.36) * mm});
            skLineSegment(sketch, "E1919", {"start": v(-14.56, -3.36) * mm, "end": v(-12.73, -3.36) * mm});
            skLineSegment(sketch, "E1920", {"start": v(-12.73, -3.36) * mm, "end": v(-12.7, -3.36) * mm});
            skLineSegment(sketch, "E1921", {"start": v(-12.7, -3.36) * mm, "end": v(-12.6, -3.46) * mm});
            skLineSegment(sketch, "E1922", {"start": v(-12.6, -3.46) * mm, "end": v(-12.6, -3.5) * mm});
            skLineSegment(sketch, "E1923", {"start": v(-12.6, -3.5) * mm, "end": v(-12.6, -3.62) * mm});
            skLineSegment(sketch, "E1924", {"start": v(-12.6, -3.62) * mm, "end": v(-12.8, -4) * mm});
            skLineSegment(sketch, "E1925", {"start": v(-12.8, -4) * mm, "end": v(-13.19, -4.22) * mm});
            skLineSegment(sketch, "E1926", {"start": v(-13.19, -4.22) * mm, "end": v(-13.32, -4.22) * mm});
            skLineSegment(sketch, "E1927", {"start": v(-14.66, -2.87) * mm, "end": v(-14.7, -2.87) * mm});
            skLineSegment(sketch, "E1928", {"start": v(-14.7, -2.87) * mm, "end": v(-14.83, -2.94) * mm});
            skLineSegment(sketch, "E1929", {"start": v(-14.83, -2.94) * mm, "end": v(-14.9, -3.07) * mm});
            skLineSegment(sketch, "E1930", {"start": v(-14.9, -3.07) * mm, "end": v(-14.9, -3.11) * mm});
            skLineSegment(sketch, "E1931", {"start": v(-14.9, -3.11) * mm, "end": v(-14.9, -3.16) * mm});
            skLineSegment(sketch, "E1932", {"start": v(-14.9, -3.16) * mm, "end": v(-14.83, -3.29) * mm});
            skLineSegment(sketch, "E1933", {"start": v(-14.83, -3.29) * mm, "end": v(-14.7, -3.36) * mm});
            skLineSegment(sketch, "E1934", {"start": v(-14.7, -3.36) * mm, "end": v(-14.66, -3.36) * mm});
            skLineSegment(sketch, "E1935", {"start": v(-14.66, -3.36) * mm, "end": v(-12.63, -3.36) * mm});
            skLineSegment(sketch, "E1936", {"start": v(-12.63, -3.36) * mm, "end": v(-12.59, -3.36) * mm});
            skLineSegment(sketch, "E1937", {"start": v(-12.59, -3.36) * mm, "end": v(-12.46, -3.29) * mm});
            skLineSegment(sketch, "E1938", {"start": v(-12.46, -3.29) * mm, "end": v(-12.39, -3.16) * mm});
            skLineSegment(sketch, "E1939", {"start": v(-12.39, -3.16) * mm, "end": v(-12.39, -3.11) * mm});
            skLineSegment(sketch, "E1940", {"start": v(-12.39, -3.11) * mm, "end": v(-12.39, -3.07) * mm});
            skLineSegment(sketch, "E1941", {"start": v(-12.39, -3.07) * mm, "end": v(-12.46, -2.94) * mm});
            skLineSegment(sketch, "E1942", {"start": v(-12.46, -2.94) * mm, "end": v(-12.59, -2.87) * mm});
            skLineSegment(sketch, "E1943", {"start": v(-12.59, -2.87) * mm, "end": v(-12.63, -2.87) * mm});
            skLineSegment(sketch, "E1944", {"start": v(-12.63, -2.87) * mm, "end": v(-14.66, -2.87) * mm});
            skLineSegment(sketch, "E1945", {"start": v(-12.63, -3.63) * mm, "end": v(-14.66, -3.63) * mm});
            skLineSegment(sketch, "E1946", {"start": v(-14.66, -3.63) * mm, "end": v(-14.75, -3.63) * mm});
            skLineSegment(sketch, "E1947", {"start": v(-14.75, -3.63) * mm, "end": v(-15.02, -3.48) * mm});
            skLineSegment(sketch, "E1948", {"start": v(-15.02, -3.48) * mm, "end": v(-15.17, -3.2) * mm});
            skLineSegment(sketch, "E1949", {"start": v(-15.17, -3.2) * mm, "end": v(-15.17, -3.11) * mm});
            skLineSegment(sketch, "E1950", {"start": v(-15.17, -3.11) * mm, "end": v(-15.17, -3.02) * mm});
            skLineSegment(sketch, "E1951", {"start": v(-15.17, -3.02) * mm, "end": v(-15.02, -2.75) * mm});
            skLineSegment(sketch, "E1952", {"start": v(-15.02, -2.75) * mm, "end": v(-14.75, -2.6) * mm});
            skLineSegment(sketch, "E1953", {"start": v(-14.75, -2.6) * mm, "end": v(-14.66, -2.6) * mm});
            skLineSegment(sketch, "E1954", {"start": v(-14.66, -2.6) * mm, "end": v(-12.63, -2.6) * mm});
            skLineSegment(sketch, "E1955", {"start": v(-12.63, -2.6) * mm, "end": v(-12.54, -2.6) * mm});
            skLineSegment(sketch, "E1956", {"start": v(-12.54, -2.6) * mm, "end": v(-12.27, -2.75) * mm});
            skLineSegment(sketch, "E1957", {"start": v(-12.27, -2.75) * mm, "end": v(-12.12, -3.02) * mm});
            skLineSegment(sketch, "E1958", {"start": v(-12.12, -3.02) * mm, "end": v(-12.12, -3.11) * mm});
            skLineSegment(sketch, "E1959", {"start": v(-12.12, -3.11) * mm, "end": v(-12.12, -3.2) * mm});
            skLineSegment(sketch, "E1960", {"start": v(-12.12, -3.2) * mm, "end": v(-12.27, -3.48) * mm});
            skLineSegment(sketch, "E1961", {"start": v(-12.27, -3.48) * mm, "end": v(-12.54, -3.63) * mm});
            skLineSegment(sketch, "E1962", {"start": v(-12.54, -3.63) * mm, "end": v(-12.63, -3.63) * mm});
            skLineSegment(sketch, "E1963", {"start": v(-14.5, -2.67) * mm, "end": v(-12.8, -2.67) * mm});
            skLineSegment(sketch, "E1964", {"start": v(-12.8, -2.67) * mm, "end": v(-12.8, -2.21) * mm});
            skLineSegment(sketch, "E1965", {"start": v(-12.8, -2.21) * mm, "end": v(-14.5, -2.21) * mm});
            skLineSegment(sketch, "E1966", {"start": v(-14.5, -2.21) * mm, "end": v(-14.5, -2.67) * mm});
            skLineSegment(sketch, "E1967", {"start": v(-12.73, -2.8) * mm, "end": v(-14.56, -2.8) * mm});
            skLineSegment(sketch, "E1968", {"start": v(-14.56, -2.8) * mm, "end": v(-14.58, -2.8) * mm});
            skLineSegment(sketch, "E1969", {"start": v(-14.58, -2.8) * mm, "end": v(-14.63, -2.75) * mm});
            skLineSegment(sketch, "E1970", {"start": v(-14.63, -2.75) * mm, "end": v(-14.63, -2.73) * mm});
            skLineSegment(sketch, "E1971", {"start": v(-14.63, -2.73) * mm, "end": v(-14.63, -2.15) * mm});
            skLineSegment(sketch, "E1972", {"start": v(-14.63, -2.15) * mm, "end": v(-14.63, -2.13) * mm});
            skLineSegment(sketch, "E1973", {"start": v(-14.63, -2.13) * mm, "end": v(-14.58, -2.08) * mm});
            skLineSegment(sketch, "E1974", {"start": v(-14.58, -2.08) * mm, "end": v(-14.56, -2.08) * mm});
            skLineSegment(sketch, "E1975", {"start": v(-14.56, -2.08) * mm, "end": v(-12.73, -2.08) * mm});
            skLineSegment(sketch, "E1976", {"start": v(-12.73, -2.08) * mm, "end": v(-12.71, -2.08) * mm});
            skLineSegment(sketch, "E1977", {"start": v(-12.71, -2.08) * mm, "end": v(-12.66, -2.13) * mm});
            skLineSegment(sketch, "E1978", {"start": v(-12.66, -2.13) * mm, "end": v(-12.66, -2.15) * mm});
            skLineSegment(sketch, "E1979", {"start": v(-12.66, -2.15) * mm, "end": v(-12.66, -2.73) * mm});
            skLineSegment(sketch, "E1980", {"start": v(-12.66, -2.73) * mm, "end": v(-12.66, -2.75) * mm});
            skLineSegment(sketch, "E1981", {"start": v(-12.66, -2.75) * mm, "end": v(-12.71, -2.8) * mm});
            skLineSegment(sketch, "E1982", {"start": v(-12.71, -2.8) * mm, "end": v(-12.73, -2.8) * mm});
            skLineSegment(sketch, "E1983", {"start": v(-13.6, 2.37) * mm, "end": v(-13.5, 2.37) * mm});
            skLineSegment(sketch, "E1984", {"start": v(-13.5, 2.37) * mm, "end": v(-13.2, 2.24) * mm});
            skLineSegment(sketch, "E1985", {"start": v(-13.2, 2.24) * mm, "end": v(-13.16, 2.21) * mm});
            skLineSegment(sketch, "E1986", {"start": v(-13.16, 2.21) * mm, "end": v(-13.13, 2.18) * mm});
            skLineSegment(sketch, "E1987", {"start": v(-13.13, 2.18) * mm, "end": v(-12.99, 1.9) * mm});
            skLineSegment(sketch, "E1988", {"start": v(-12.99, 1.9) * mm, "end": v(-12.99, 1.81) * mm});
            skLineSegment(sketch, "E1989", {"start": v(-12.99, 1.81) * mm, "end": v(-12.99, 1.76) * mm});
            skLineSegment(sketch, "E1990", {"start": v(-12.99, 1.76) * mm, "end": v(-13.04, 1.6) * mm});
            skLineSegment(sketch, "E1991", {"start": v(-13.04, 1.6) * mm, "end": v(-13.05, 1.59) * mm});
            skLineSegment(sketch, "E1992", {"start": v(-13.05, 1.59) * mm, "end": v(-13.06, 1.57) * mm});
            skLineSegment(sketch, "E1993", {"start": v(-13.06, 1.57) * mm, "end": v(-13.17, 1.42) * mm});
            skLineSegment(sketch, "E1994", {"start": v(-13.17, 1.42) * mm, "end": v(-13.18, 1.4) * mm});
            skLineSegment(sketch, "E1995", {"start": v(-13.18, 1.4) * mm, "end": v(-13.2, 1.4) * mm});
            skLineSegment(sketch, "E1996", {"start": v(-13.2, 1.4) * mm, "end": v(-13.4, 1.2) * mm});
            skLineSegment(sketch, "E1997", {"start": v(-13.4, 1.2) * mm, "end": v(-13.43, 1.18) * mm});
            skLineSegment(sketch, "E1998", {"start": v(-13.43, 1.18) * mm, "end": v(-13.46, 1.16) * mm});
            skLineSegment(sketch, "E1999", {"start": v(-13.46, 1.16) * mm, "end": v(-13.7, 0.92) * mm});
            skLineSegment(sketch, "E2000", {"start": v(-13.7, 0.92) * mm, "end": v(-13.73, 0.9) * mm});
            skLineSegment(sketch, "E2001", {"start": v(-13.73, 0.9) * mm, "end": v(-13.74, 0.88) * mm});
            skLineSegment(sketch, "E2002", {"start": v(-13.74, 0.88) * mm, "end": v(-13.88, 0.66) * mm});
            skLineSegment(sketch, "E2003", {"start": v(-13.88, 0.66) * mm, "end": v(-13.9, 0.63) * mm});
            skLineSegment(sketch, "E2004", {"start": v(-13.9, 0.63) * mm, "end": v(-13.9, 0.6) * mm});
            skLineSegment(sketch, "E2005", {"start": v(-13.9, 0.6) * mm, "end": v(-13.96, 0.36) * mm});
            skLineSegment(sketch, "E2006", {"start": v(-13.96, 0.36) * mm, "end": v(-13.96, 0.28) * mm});
            skLineSegment(sketch, "E2007", {"start": v(-13.96, 0.28) * mm, "end": v(-13.96, 0.22) * mm});
            skLineSegment(sketch, "E2008", {"start": v(-13.96, 0.22) * mm, "end": v(-13.9, 0.07) * mm});
            skLineSegment(sketch, "E2009", {"start": v(-13.9, 0.07) * mm, "end": v(-13.88, 0.06) * mm});
            skLineSegment(sketch, "E2010", {"start": v(-13.88, 0.06) * mm, "end": v(-13.87, 0.05) * mm});
            skLineSegment(sketch, "E2011", {"start": v(-13.87, 0.05) * mm, "end": v(-13.74, -0.01) * mm});
            skLineSegment(sketch, "E2012", {"start": v(-13.74, -0.01) * mm, "end": v(-13.7, -0.01) * mm});
            skLineSegment(sketch, "E2013", {"start": v(-13.7, -0.01) * mm, "end": v(-13.64, -0.01) * mm});
            skLineSegment(sketch, "E2014", {"start": v(-13.64, -0.01) * mm, "end": v(-13.45, 0.17) * mm});
            skLineSegment(sketch, "E2015", {"start": v(-13.45, 0.17) * mm, "end": v(-13.45, 0.2) * mm});
            skLineSegment(sketch, "E2016", {"start": v(-13.45, 0.2) * mm, "end": v(-13.44, 0.23) * mm});
            skLineSegment(sketch, "E2017", {"start": v(-13.44, 0.23) * mm, "end": v(-13.4, 0.38) * mm});
            skLineSegment(sketch, "E2018", {"start": v(-13.4, 0.38) * mm, "end": v(-13.4, 0.4) * mm});
            skLineSegment(sketch, "E2019", {"start": v(-13.4, 0.4) * mm, "end": v(-13.4, 0.4) * mm});
            skLineSegment(sketch, "E2020", {"start": v(-13.4, 0.4) * mm, "end": v(-13.36, 0.5) * mm});
            skLineSegment(sketch, "E2021", {"start": v(-13.36, 0.5) * mm, "end": v(-13.36, 0.5) * mm});
            skLineSegment(sketch, "E2022", {"start": v(-13.36, 0.5) * mm, "end": v(-13.35, 0.52) * mm});
            skLineSegment(sketch, "E2023", {"start": v(-13.35, 0.52) * mm, "end": v(-13.28, 0.62) * mm});
            skLineSegment(sketch, "E2024", {"start": v(-13.28, 0.62) * mm, "end": v(-13.27, 0.63) * mm});
            skLineSegment(sketch, "E2025", {"start": v(-13.27, 0.63) * mm, "end": v(-13.26, 0.64) * mm});
            skLineSegment(sketch, "E2026", {"start": v(-13.26, 0.64) * mm, "end": v(-13.14, 0.76) * mm});
            skLineSegment(sketch, "E2027", {"start": v(-13.14, 0.76) * mm, "end": v(-13.12, 0.78) * mm});
            skLineSegment(sketch, "E2028", {"start": v(-13.12, 0.78) * mm, "end": v(-13.07, 0.82) * mm});
            skLineSegment(sketch, "E2029", {"start": v(-13.07, 0.82) * mm, "end": v(-12.7, 1.16) * mm});
            skLineSegment(sketch, "E2030", {"start": v(-12.7, 1.16) * mm, "end": v(-12.68, 1.18) * mm});
            skLineSegment(sketch, "E2031", {"start": v(-12.68, 1.18) * mm, "end": v(-12.66, 1.2) * mm});
            skLineSegment(sketch, "E2032", {"start": v(-12.66, 1.2) * mm, "end": v(-12.49, 1.43) * mm});
            skLineSegment(sketch, "E2033", {"start": v(-12.49, 1.43) * mm, "end": v(-12.47, 1.46) * mm});
            skLineSegment(sketch, "E2034", {"start": v(-12.47, 1.46) * mm, "end": v(-12.46, 1.48) * mm});
            skLineSegment(sketch, "E2035", {"start": v(-12.46, 1.48) * mm, "end": v(-12.4, 1.73) * mm});
            skLineSegment(sketch, "E2036", {"start": v(-12.4, 1.73) * mm, "end": v(-12.4, 1.82) * mm});
            skLineSegment(sketch, "E2037", {"start": v(-12.4, 1.82) * mm, "end": v(-12.4, 1.94) * mm});
            skLineSegment(sketch, "E2038", {"start": v(-12.4, 1.94) * mm, "end": v(-12.52, 2.27) * mm});
            skLineSegment(sketch, "E2039", {"start": v(-12.52, 2.27) * mm, "end": v(-12.54, 2.3) * mm});
            skLineSegment(sketch, "E2040", {"start": v(-12.54, 2.3) * mm, "end": v(-12.57, 2.35) * mm});
            skLineSegment(sketch, "E2041", {"start": v(-12.57, 2.35) * mm, "end": v(-12.92, 2.65) * mm});
            skLineSegment(sketch, "E2042", {"start": v(-12.92, 2.65) * mm, "end": v(-12.96, 2.67) * mm});
            skLineSegment(sketch, "E2043", {"start": v(-12.96, 2.67) * mm, "end": v(-13, 2.69) * mm});
            skLineSegment(sketch, "E2044", {"start": v(-13, 2.69) * mm, "end": v(-13.46, 2.8) * mm});
            skLineSegment(sketch, "E2045", {"start": v(-13.46, 2.8) * mm, "end": v(-13.6, 2.8) * mm});
            skLineSegment(sketch, "E2046", {"start": v(-13.6, 2.8) * mm, "end": v(-13.78, 2.8) * mm});
            skLineSegment(sketch, "E2047", {"start": v(-13.78, 2.8) * mm, "end": v(-14.24, 2.67) * mm});
            skLineSegment(sketch, "E2048", {"start": v(-14.24, 2.67) * mm, "end": v(-14.29, 2.64) * mm});
            skLineSegment(sketch, "E2049", {"start": v(-14.29, 2.64) * mm, "end": v(-14.34, 2.61) * mm});
            skLineSegment(sketch, "E2050", {"start": v(-14.34, 2.61) * mm, "end": v(-14.7, 2.28) * mm});
            skLineSegment(sketch, "E2051", {"start": v(-14.7, 2.28) * mm, "end": v(-14.73, 2.24) * mm});
            skLineSegment(sketch, "E2052", {"start": v(-14.73, 2.24) * mm, "end": v(-14.76, 2.2) * mm});
            skLineSegment(sketch, "E2053", {"start": v(-14.76, 2.2) * mm, "end": v(-14.88, 1.88) * mm});
            skLineSegment(sketch, "E2054", {"start": v(-14.88, 1.88) * mm, "end": v(-14.88, 1.77) * mm});
            skLineSegment(sketch, "E2055", {"start": v(-14.88, 1.77) * mm, "end": v(-14.88, 1.72) * mm});
            skLineSegment(sketch, "E2056", {"start": v(-14.88, 1.72) * mm, "end": v(-14.81, 1.6) * mm});
            skLineSegment(sketch, "E2057", {"start": v(-14.81, 1.6) * mm, "end": v(-14.8, 1.59) * mm});
            skLineSegment(sketch, "E2058", {"start": v(-14.8, 1.59) * mm, "end": v(-14.79, 1.57) * mm});
            skLineSegment(sketch, "E2059", {"start": v(-14.79, 1.57) * mm, "end": v(-14.64, 1.5) * mm});
            skLineSegment(sketch, "E2060", {"start": v(-14.64, 1.5) * mm, "end": v(-14.6, 1.5) * mm});
            skLineSegment(sketch, "E2061", {"start": v(-14.6, 1.5) * mm, "end": v(-14.56, 1.5) * mm});
            skLineSegment(sketch, "E2062", {"start": v(-14.56, 1.5) * mm, "end": v(-14.45, 1.55) * mm});
            skLineSegment(sketch, "E2063", {"start": v(-14.45, 1.55) * mm, "end": v(-14.33, 1.7) * mm});
            skLineSegment(sketch, "E2064", {"start": v(-14.33, 1.7) * mm, "end": v(-14.32, 1.76) * mm});
            skLineSegment(sketch, "E2065", {"start": v(-14.32, 1.76) * mm, "end": v(-14.3, 1.8) * mm});
            skLineSegment(sketch, "E2066", {"start": v(-14.3, 1.8) * mm, "end": v(-14.1, 2.18) * mm});
            skLineSegment(sketch, "E2067", {"start": v(-14.1, 2.18) * mm, "end": v(-14.07, 2.2) * mm});
            skLineSegment(sketch, "E2068", {"start": v(-14.07, 2.2) * mm, "end": v(-14.05, 2.23) * mm});
            skLineSegment(sketch, "E2069", {"start": v(-14.05, 2.23) * mm, "end": v(-13.72, 2.37) * mm});
            skLineSegment(sketch, "E2070", {"start": v(-13.72, 2.37) * mm, "end": v(-13.6, 2.37) * mm});
            skLineSegment(sketch, "E2071", {"start": v(-13.7, -0.14) * mm, "end": v(-13.77, -0.14) * mm});
            skLineSegment(sketch, "E2072", {"start": v(-13.77, -0.14) * mm, "end": v(-13.95, -0.05) * mm});
            skLineSegment(sketch, "E2073", {"start": v(-13.95, -0.05) * mm, "end": v(-13.97, -0.03) * mm});
            skLineSegment(sketch, "E2074", {"start": v(-13.97, -0.03) * mm, "end": v(-13.99, -0.01) * mm});
            skLineSegment(sketch, "E2075", {"start": v(-13.99, -0.01) * mm, "end": v(-14.08, 0.2) * mm});
            skLineSegment(sketch, "E2076", {"start": v(-14.08, 0.2) * mm, "end": v(-14.08, 0.28) * mm});
            skLineSegment(sketch, "E2077", {"start": v(-14.08, 0.28) * mm, "end": v(-14.08, 0.38) * mm});
            skLineSegment(sketch, "E2078", {"start": v(-14.08, 0.38) * mm, "end": v(-14.02, 0.65) * mm});
            skLineSegment(sketch, "E2079", {"start": v(-14.02, 0.65) * mm, "end": v(-14, 0.68) * mm});
            skLineSegment(sketch, "E2080", {"start": v(-14, 0.68) * mm, "end": v(-14, 0.7) * mm});
            skLineSegment(sketch, "E2081", {"start": v(-14, 0.7) * mm, "end": v(-13.83, 0.96) * mm});
            skLineSegment(sketch, "E2082", {"start": v(-13.83, 0.96) * mm, "end": v(-13.81, 0.98) * mm});
            skLineSegment(sketch, "E2083", {"start": v(-13.81, 0.98) * mm, "end": v(-13.8, 1) * mm});
            skLineSegment(sketch, "E2084", {"start": v(-13.8, 1) * mm, "end": v(-13.54, 1.25) * mm});
            skLineSegment(sketch, "E2085", {"start": v(-13.54, 1.25) * mm, "end": v(-13.5, 1.27) * mm});
            skLineSegment(sketch, "E2086", {"start": v(-13.5, 1.27) * mm, "end": v(-13.48, 1.3) * mm});
            skLineSegment(sketch, "E2087", {"start": v(-13.48, 1.3) * mm, "end": v(-13.28, 1.48) * mm});
            skLineSegment(sketch, "E2088", {"start": v(-13.28, 1.48) * mm, "end": v(-13.27, 1.5) * mm});
            skLineSegment(sketch, "E2089", {"start": v(-13.27, 1.5) * mm, "end": v(-13.26, 1.5) * mm});
            skLineSegment(sketch, "E2090", {"start": v(-13.26, 1.5) * mm, "end": v(-13.16, 1.63) * mm});
            skLineSegment(sketch, "E2091", {"start": v(-13.16, 1.63) * mm, "end": v(-13.15, 1.64) * mm});
            skLineSegment(sketch, "E2092", {"start": v(-13.15, 1.64) * mm, "end": v(-13.15, 1.66) * mm});
            skLineSegment(sketch, "E2093", {"start": v(-13.15, 1.66) * mm, "end": v(-13.11, 1.78) * mm});
            skLineSegment(sketch, "E2094", {"start": v(-13.11, 1.78) * mm, "end": v(-13.11, 1.81) * mm});
            skLineSegment(sketch, "E2095", {"start": v(-13.11, 1.81) * mm, "end": v(-13.11, 1.9) * mm});
            skLineSegment(sketch, "E2096", {"start": v(-13.11, 1.9) * mm, "end": v(-13.22, 2.1) * mm});
            skLineSegment(sketch, "E2097", {"start": v(-13.22, 2.1) * mm, "end": v(-13.25, 2.12) * mm});
            skLineSegment(sketch, "E2098", {"start": v(-13.25, 2.12) * mm, "end": v(-13.27, 2.14) * mm});
            skLineSegment(sketch, "E2099", {"start": v(-13.27, 2.14) * mm, "end": v(-13.52, 2.25) * mm});
            skLineSegment(sketch, "E2100", {"start": v(-13.52, 2.25) * mm, "end": v(-13.6, 2.25) * mm});
            skLineSegment(sketch, "E2101", {"start": v(-13.6, 2.25) * mm, "end": v(-13.7, 2.25) * mm});
            skLineSegment(sketch, "E2102", {"start": v(-13.7, 2.25) * mm, "end": v(-13.96, 2.14) * mm});
            skLineSegment(sketch, "E2103", {"start": v(-13.96, 2.14) * mm, "end": v(-13.98, 2.12) * mm});
            skLineSegment(sketch, "E2104", {"start": v(-13.98, 2.12) * mm, "end": v(-14, 2.1) * mm});
            skLineSegment(sketch, "E2105", {"start": v(-14, 2.1) * mm, "end": v(-14.19, 1.76) * mm});
            skLineSegment(sketch, "E2106", {"start": v(-14.19, 1.76) * mm, "end": v(-14.2, 1.72) * mm});
            skLineSegment(sketch, "E2107", {"start": v(-14.2, 1.72) * mm, "end": v(-14.22, 1.65) * mm});
            skLineSegment(sketch, "E2108", {"start": v(-14.22, 1.65) * mm, "end": v(-14.38, 1.45) * mm});
            skLineSegment(sketch, "E2109", {"start": v(-14.38, 1.45) * mm, "end": v(-14.54, 1.38) * mm});
            skLineSegment(sketch, "E2110", {"start": v(-14.54, 1.38) * mm, "end": v(-14.6, 1.38) * mm});
            skLineSegment(sketch, "E2111", {"start": v(-14.6, 1.38) * mm, "end": v(-14.67, 1.38) * mm});
            skLineSegment(sketch, "E2112", {"start": v(-14.67, 1.38) * mm, "end": v(-14.87, 1.48) * mm});
            skLineSegment(sketch, "E2113", {"start": v(-14.87, 1.48) * mm, "end": v(-14.89, 1.5) * mm});
            skLineSegment(sketch, "E2114", {"start": v(-14.89, 1.5) * mm, "end": v(-14.9, 1.52) * mm});
            skLineSegment(sketch, "E2115", {"start": v(-14.9, 1.52) * mm, "end": v(-15, 1.7) * mm});
            skLineSegment(sketch, "E2116", {"start": v(-15, 1.7) * mm, "end": v(-15, 1.77) * mm});
            skLineSegment(sketch, "E2117", {"start": v(-15, 1.77) * mm, "end": v(-15, 1.9) * mm});
            skLineSegment(sketch, "E2118", {"start": v(-15, 1.9) * mm, "end": v(-14.86, 2.26) * mm});
            skLineSegment(sketch, "E2119", {"start": v(-14.86, 2.26) * mm, "end": v(-14.83, 2.3) * mm});
            skLineSegment(sketch, "E2120", {"start": v(-14.83, 2.3) * mm, "end": v(-14.8, 2.35) * mm});
            skLineSegment(sketch, "E2121", {"start": v(-14.8, 2.35) * mm, "end": v(-14.4, 2.72) * mm});
            skLineSegment(sketch, "E2122", {"start": v(-14.4, 2.72) * mm, "end": v(-14.35, 2.75) * mm});
            skLineSegment(sketch, "E2123", {"start": v(-14.35, 2.75) * mm, "end": v(-14.3, 2.78) * mm});
            skLineSegment(sketch, "E2124", {"start": v(-14.3, 2.78) * mm, "end": v(-13.78, 2.92) * mm});
            skLineSegment(sketch, "E2125", {"start": v(-13.78, 2.92) * mm, "end": v(-13.6, 2.92) * mm});
            skLineSegment(sketch, "E2126", {"start": v(-13.6, 2.92) * mm, "end": v(-13.43, 2.92) * mm});
            skLineSegment(sketch, "E2127", {"start": v(-13.43, 2.92) * mm, "end": v(-12.96, 2.8) * mm});
            skLineSegment(sketch, "E2128", {"start": v(-12.96, 2.8) * mm, "end": v(-12.91, 2.78) * mm});
            skLineSegment(sketch, "E2129", {"start": v(-12.91, 2.78) * mm, "end": v(-12.86, 2.75) * mm});
            skLineSegment(sketch, "E2130", {"start": v(-12.86, 2.75) * mm, "end": v(-12.47, 2.42) * mm});
            skLineSegment(sketch, "E2131", {"start": v(-12.47, 2.42) * mm, "end": v(-12.44, 2.37) * mm});
            skLineSegment(sketch, "E2132", {"start": v(-12.44, 2.37) * mm, "end": v(-12.41, 2.33) * mm});
            skLineSegment(sketch, "E2133", {"start": v(-12.41, 2.33) * mm, "end": v(-12.27, 1.95) * mm});
            skLineSegment(sketch, "E2134", {"start": v(-12.27, 1.95) * mm, "end": v(-12.27, 1.82) * mm});
            skLineSegment(sketch, "E2135", {"start": v(-12.27, 1.82) * mm, "end": v(-12.27, 1.71) * mm});
            skLineSegment(sketch, "E2136", {"start": v(-12.27, 1.71) * mm, "end": v(-12.35, 1.43) * mm});
            skLineSegment(sketch, "E2137", {"start": v(-12.35, 1.43) * mm, "end": v(-12.37, 1.4) * mm});
            skLineSegment(sketch, "E2138", {"start": v(-12.37, 1.4) * mm, "end": v(-12.38, 1.37) * mm});
            skLineSegment(sketch, "E2139", {"start": v(-12.38, 1.37) * mm, "end": v(-12.57, 1.12) * mm});
            skLineSegment(sketch, "E2140", {"start": v(-12.57, 1.12) * mm, "end": v(-12.6, 1.1) * mm});
            skLineSegment(sketch, "E2141", {"start": v(-12.6, 1.1) * mm, "end": v(-12.61, 1.08) * mm});
            skLineSegment(sketch, "E2142", {"start": v(-12.61, 1.08) * mm, "end": v(-12.99, 0.73) * mm});
            skLineSegment(sketch, "E2143", {"start": v(-12.99, 0.73) * mm, "end": v(-13.04, 0.69) * mm});
            skLineSegment(sketch, "E2144", {"start": v(-13.04, 0.69) * mm, "end": v(-13.05, 0.67) * mm});
            skLineSegment(sketch, "E2145", {"start": v(-13.05, 0.67) * mm, "end": v(-13.17, 0.56) * mm});
            skLineSegment(sketch, "E2146", {"start": v(-13.17, 0.56) * mm, "end": v(-13.18, 0.55) * mm});
            skLineSegment(sketch, "E2147", {"start": v(-13.18, 0.55) * mm, "end": v(-13.19, 0.54) * mm});
            skLineSegment(sketch, "E2148", {"start": v(-13.19, 0.54) * mm, "end": v(-13.24, 0.46) * mm});
            skLineSegment(sketch, "E2149", {"start": v(-13.24, 0.46) * mm, "end": v(-13.25, 0.45) * mm});
            skLineSegment(sketch, "E2150", {"start": v(-13.25, 0.45) * mm, "end": v(-13.25, 0.44) * mm});
            skLineSegment(sketch, "E2151", {"start": v(-13.25, 0.44) * mm, "end": v(-13.28, 0.37) * mm});
            skLineSegment(sketch, "E2152", {"start": v(-13.28, 0.37) * mm, "end": v(-13.28, 0.36) * mm});
            skLineSegment(sketch, "E2153", {"start": v(-13.28, 0.36) * mm, "end": v(-13.29, 0.35) * mm});
            skLineSegment(sketch, "E2154", {"start": v(-13.29, 0.35) * mm, "end": v(-13.32, 0.2) * mm});
            skLineSegment(sketch, "E2155", {"start": v(-13.32, 0.2) * mm, "end": v(-13.33, 0.18) * mm});
            skLineSegment(sketch, "E2156", {"start": v(-13.33, 0.18) * mm, "end": v(-13.34, 0.13) * mm});
            skLineSegment(sketch, "E2157", {"start": v(-13.34, 0.13) * mm, "end": v(-13.6, -0.14) * mm});
            skLineSegment(sketch, "E2158", {"start": v(-13.6, -0.14) * mm, "end": v(-13.7, -0.14) * mm});
            skLineSegment(sketch, "E2159", {"start": v(-13.67, -0.37) * mm, "end": v(-13.73, -0.37) * mm});
            skLineSegment(sketch, "E2160", {"start": v(-13.73, -0.37) * mm, "end": v(-13.9, -0.45) * mm});
            skLineSegment(sketch, "E2161", {"start": v(-13.9, -0.45) * mm, "end": v(-13.9, -0.47) * mm});
            skLineSegment(sketch, "E2162", {"start": v(-13.9, -0.47) * mm, "end": v(-13.92, -0.48) * mm});
            skLineSegment(sketch, "E2163", {"start": v(-13.92, -0.48) * mm, "end": v(-14, -0.65) * mm});
            skLineSegment(sketch, "E2164", {"start": v(-14, -0.65) * mm, "end": v(-14, -0.7) * mm});
            skLineSegment(sketch, "E2165", {"start": v(-14, -0.7) * mm, "end": v(-14, -0.76) * mm});
            skLineSegment(sketch, "E2166", {"start": v(-14, -0.76) * mm, "end": v(-13.92, -0.93) * mm});
            skLineSegment(sketch, "E2167", {"start": v(-13.92, -0.93) * mm, "end": v(-13.9, -0.94) * mm});
            skLineSegment(sketch, "E2168", {"start": v(-13.9, -0.94) * mm, "end": v(-13.87, -0.97) * mm});
            skLineSegment(sketch, "E2169", {"start": v(-13.87, -0.97) * mm, "end": v(-13.47, -0.97) * mm});
            skLineSegment(sketch, "E2170", {"start": v(-13.47, -0.97) * mm, "end": v(-13.44, -0.94) * mm});
            skLineSegment(sketch, "E2171", {"start": v(-13.44, -0.94) * mm, "end": v(-13.42, -0.93) * mm});
            skLineSegment(sketch, "E2172", {"start": v(-13.42, -0.93) * mm, "end": v(-13.34, -0.76) * mm});
            skLineSegment(sketch, "E2173", {"start": v(-13.34, -0.76) * mm, "end": v(-13.34, -0.7) * mm});
            skLineSegment(sketch, "E2174", {"start": v(-13.34, -0.7) * mm, "end": v(-13.34, -0.64) * mm});
            skLineSegment(sketch, "E2175", {"start": v(-13.34, -0.64) * mm, "end": v(-13.42, -0.48) * mm});
            skLineSegment(sketch, "E2176", {"start": v(-13.42, -0.48) * mm, "end": v(-13.43, -0.47) * mm});
            skLineSegment(sketch, "E2177", {"start": v(-13.43, -0.47) * mm, "end": v(-13.45, -0.45) * mm});
            skLineSegment(sketch, "E2178", {"start": v(-13.45, -0.45) * mm, "end": v(-13.61, -0.37) * mm});
            skLineSegment(sketch, "E2179", {"start": v(-13.61, -0.37) * mm, "end": v(-13.67, -0.37) * mm});
            skLineSegment(sketch, "E2180", {"start": v(-13.67, -1.15) * mm, "end": v(-13.75, -1.15) * mm});
            skLineSegment(sketch, "E2181", {"start": v(-13.75, -1.15) * mm, "end": v(-13.96, -1.06) * mm});
            skLineSegment(sketch, "E2182", {"start": v(-13.96, -1.06) * mm, "end": v(-13.99, -1.04) * mm});
            skLineSegment(sketch, "E2183", {"start": v(-13.99, -1.04) * mm, "end": v(-14.01, -1.02) * mm});
            skLineSegment(sketch, "E2184", {"start": v(-14.01, -1.02) * mm, "end": v(-14.13, -0.78) * mm});
            skLineSegment(sketch, "E2185", {"start": v(-14.13, -0.78) * mm, "end": v(-14.13, -0.7) * mm});
            skLineSegment(sketch, "E2186", {"start": v(-14.13, -0.7) * mm, "end": v(-14.13, -0.62) * mm});
            skLineSegment(sketch, "E2187", {"start": v(-14.13, -0.62) * mm, "end": v(-14.01, -0.4) * mm});
            skLineSegment(sketch, "E2188", {"start": v(-14.01, -0.4) * mm, "end": v(-14, -0.38) * mm});
            skLineSegment(sketch, "E2189", {"start": v(-14, -0.38) * mm, "end": v(-13.97, -0.36) * mm});
            skLineSegment(sketch, "E2190", {"start": v(-13.97, -0.36) * mm, "end": v(-13.74, -0.25) * mm});
            skLineSegment(sketch, "E2191", {"start": v(-13.74, -0.25) * mm, "end": v(-13.67, -0.25) * mm});
            skLineSegment(sketch, "E2192", {"start": v(-13.67, -0.25) * mm, "end": v(-13.59, -0.25) * mm});
            skLineSegment(sketch, "E2193", {"start": v(-13.59, -0.25) * mm, "end": v(-13.37, -0.36) * mm});
            skLineSegment(sketch, "E2194", {"start": v(-13.37, -0.36) * mm, "end": v(-13.35, -0.38) * mm});
            skLineSegment(sketch, "E2195", {"start": v(-13.35, -0.38) * mm, "end": v(-13.33, -0.4) * mm});
            skLineSegment(sketch, "E2196", {"start": v(-13.33, -0.4) * mm, "end": v(-13.22, -0.63) * mm});
            skLineSegment(sketch, "E2197", {"start": v(-13.22, -0.63) * mm, "end": v(-13.22, -0.7) * mm});
            skLineSegment(sketch, "E2198", {"start": v(-13.22, -0.7) * mm, "end": v(-13.22, -0.79) * mm});
            skLineSegment(sketch, "E2199", {"start": v(-13.22, -0.79) * mm, "end": v(-13.33, -1.01) * mm});
            skLineSegment(sketch, "E2200", {"start": v(-13.33, -1.01) * mm, "end": v(-13.36, -1.03) * mm});
            skLineSegment(sketch, "E2201", {"start": v(-13.36, -1.03) * mm, "end": v(-13.38, -1.05) * mm});
            skLineSegment(sketch, "E2202", {"start": v(-13.38, -1.05) * mm, "end": v(-13.6, -1.15) * mm});
            skLineSegment(sketch, "E2203", {"start": v(-13.6, -1.15) * mm, "end": v(-13.67, -1.15) * mm});
            skLineSegment(sketch, "E2204", {"start": v(-14.77, 5.89) * mm, "end": v(-14.66, 6) * mm});
            skLineSegment(sketch, "E2205", {"start": v(-14.66, 6) * mm, "end": v(-13.57, 7.08) * mm});
            skLineSegment(sketch, "E2206", {"start": v(-13.57, 7.08) * mm, "end": v(-13.46, 7.2) * mm});
            skLineSegment(sketch, "E2207", {"start": v(-13.46, 7.2) * mm, "end": v(-13.87, 7.2) * mm});
            skLineSegment(sketch, "E2208", {"start": v(-13.87, 7.2) * mm, "end": v(-12.63, 5.96) * mm});
            skLineSegment(sketch, "E2209", {"start": v(-12.63, 5.96) * mm, "end": v(-12.6, 5.92) * mm});
            skLineSegment(sketch, "E2210", {"start": v(-12.6, 5.92) * mm, "end": v(-12.42, 5.87) * mm});
            skLineSegment(sketch, "E2211", {"start": v(-12.42, 5.87) * mm, "end": v(-12.23, 5.96) * mm});
            skLineSegment(sketch, "E2212", {"start": v(-12.23, 5.96) * mm, "end": v(-12.15, 6.15) * mm});
            skLineSegment(sketch, "E2213", {"start": v(-12.15, 6.15) * mm, "end": v(-12.2, 6.32) * mm});
            skLineSegment(sketch, "E2214", {"start": v(-12.2, 6.32) * mm, "end": v(-12.23, 6.36) * mm});
            skLineSegment(sketch, "E2215", {"start": v(-12.23, 6.36) * mm, "end": v(-13.46, 7.6) * mm});
            skLineSegment(sketch, "E2216", {"start": v(-13.46, 7.6) * mm, "end": v(-13.5, 7.62) * mm});
            skLineSegment(sketch, "E2217", {"start": v(-13.5, 7.62) * mm, "end": v(-13.84, 7.62) * mm});
            skLineSegment(sketch, "E2218", {"start": v(-13.84, 7.62) * mm, "end": v(-13.87, 7.6) * mm});
            skLineSegment(sketch, "E2219", {"start": v(-13.87, 7.6) * mm, "end": v(-15.17, 6.3) * mm});
            skLineSegment(sketch, "E2220", {"start": v(-15.17, 6.3) * mm, "end": v(-15.2, 6.26) * mm});
            skLineSegment(sketch, "E2221", {"start": v(-15.2, 6.26) * mm, "end": v(-15.26, 6.08) * mm});
            skLineSegment(sketch, "E2222", {"start": v(-15.26, 6.08) * mm, "end": v(-15.17, 5.9) * mm});
            skLineSegment(sketch, "E2223", {"start": v(-15.17, 5.9) * mm, "end": v(-14.98, 5.8) * mm});
            skLineSegment(sketch, "E2224", {"start": v(-14.98, 5.8) * mm, "end": v(-14.8, 5.85) * mm});
            skLineSegment(sketch, "E2225", {"start": v(-14.8, 5.85) * mm, "end": v(-14.77, 5.89) * mm});
            skLineSegment(sketch, "E2226", {"start": v(-12.63, -5.9) * mm, "end": v(-12.74, -6) * mm});
            skLineSegment(sketch, "E2227", {"start": v(-12.74, -6) * mm, "end": v(-13.83, -7.09) * mm});
            skLineSegment(sketch, "E2228", {"start": v(-13.83, -7.09) * mm, "end": v(-13.94, -7.2) * mm});
            skLineSegment(sketch, "E2229", {"start": v(-13.94, -7.2) * mm, "end": v(-13.53, -7.2) * mm});
            skLineSegment(sketch, "E2230", {"start": v(-13.53, -7.2) * mm, "end": v(-13.64, -7.1) * mm});
            skLineSegment(sketch, "E2231", {"start": v(-13.64, -7.1) * mm, "end": v(-14.67, -6.06) * mm});
            skLineSegment(sketch, "E2232", {"start": v(-14.67, -6.06) * mm, "end": v(-14.77, -5.96) * mm});
            skLineSegment(sketch, "E2233", {"start": v(-14.77, -5.96) * mm, "end": v(-14.8, -5.92) * mm});
            skLineSegment(sketch, "E2234", {"start": v(-14.8, -5.92) * mm, "end": v(-14.98, -5.87) * mm});
            skLineSegment(sketch, "E2235", {"start": v(-14.98, -5.87) * mm, "end": v(-15.17, -5.96) * mm});
            skLineSegment(sketch, "E2236", {"start": v(-15.17, -5.96) * mm, "end": v(-15.26, -6.15) * mm});
            skLineSegment(sketch, "E2237", {"start": v(-15.26, -6.15) * mm, "end": v(-15.2, -6.32) * mm});
            skLineSegment(sketch, "E2238", {"start": v(-15.2, -6.32) * mm, "end": v(-15.17, -6.36) * mm});
            skLineSegment(sketch, "E2239", {"start": v(-15.17, -6.36) * mm, "end": v(-15.07, -6.46) * mm});
            skLineSegment(sketch, "E2240", {"start": v(-15.07, -6.46) * mm, "end": v(-14.04, -7.5) * mm});
            skLineSegment(sketch, "E2241", {"start": v(-14.04, -7.5) * mm, "end": v(-13.94, -7.6) * mm});
            skLineSegment(sketch, "E2242", {"start": v(-13.94, -7.6) * mm, "end": v(-13.9, -7.62) * mm});
            skLineSegment(sketch, "E2243", {"start": v(-13.9, -7.62) * mm, "end": v(-13.56, -7.62) * mm});
            skLineSegment(sketch, "E2244", {"start": v(-13.56, -7.62) * mm, "end": v(-13.53, -7.6) * mm});
            skLineSegment(sketch, "E2245", {"start": v(-13.53, -7.6) * mm, "end": v(-13.42, -7.49) * mm});
            skLineSegment(sketch, "E2246", {"start": v(-13.42, -7.49) * mm, "end": v(-12.34, -6.4) * mm});
            skLineSegment(sketch, "E2247", {"start": v(-12.34, -6.4) * mm, "end": v(-12.23, -6.3) * mm});
            skLineSegment(sketch, "E2248", {"start": v(-12.23, -6.3) * mm, "end": v(-12.2, -6.26) * mm});
            skLineSegment(sketch, "E2249", {"start": v(-12.2, -6.26) * mm, "end": v(-12.15, -6.08) * mm});
            skLineSegment(sketch, "E2250", {"start": v(-12.15, -6.08) * mm, "end": v(-12.23, -5.9) * mm});
            skLineSegment(sketch, "E2251", {"start": v(-12.23, -5.9) * mm, "end": v(-12.42, -5.8) * mm});
            skLineSegment(sketch, "E2252", {"start": v(-12.42, -5.8) * mm, "end": v(-12.6, -5.85) * mm});
            skLineSegment(sketch, "E2253", {"start": v(-12.6, -5.85) * mm, "end": v(-12.63, -5.9) * mm});
            skLineSegment(sketch, "E2254", {"start": v(-19.6, -1.07) * mm, "end": v(-19.7, -0.96) * mm});
            skLineSegment(sketch, "E2255", {"start": v(-19.7, -0.96) * mm, "end": v(-20.79, 0.13) * mm});
            skLineSegment(sketch, "E2256", {"start": v(-20.79, 0.13) * mm, "end": v(-20.9, 0.23) * mm});
            skLineSegment(sketch, "E2257", {"start": v(-20.9, 0.23) * mm, "end": v(-20.9, -0.17) * mm});
            skLineSegment(sketch, "E2258", {"start": v(-20.9, -0.17) * mm, "end": v(-19.66, 1.07) * mm});
            skLineSegment(sketch, "E2259", {"start": v(-19.66, 1.07) * mm, "end": v(-19.62, 1.1) * mm});
            skLineSegment(sketch, "E2260", {"start": v(-19.62, 1.1) * mm, "end": v(-19.57, 1.28) * mm});
            skLineSegment(sketch, "E2261", {"start": v(-19.57, 1.28) * mm, "end": v(-19.66, 1.47) * mm});
            skLineSegment(sketch, "E2262", {"start": v(-19.66, 1.47) * mm, "end": v(-19.85, 1.55) * mm});
            skLineSegment(sketch, "E2263", {"start": v(-19.85, 1.55) * mm, "end": v(-20.02, 1.5) * mm});
            skLineSegment(sketch, "E2264", {"start": v(-20.02, 1.5) * mm, "end": v(-20.06, 1.47) * mm});
            skLineSegment(sketch, "E2265", {"start": v(-20.06, 1.47) * mm, "end": v(-21.3, 0.23) * mm});
            skLineSegment(sketch, "E2266", {"start": v(-21.3, 0.23) * mm, "end": v(-21.32, 0.2) * mm});
            skLineSegment(sketch, "E2267", {"start": v(-21.32, 0.2) * mm, "end": v(-21.32, -0.14) * mm});
            skLineSegment(sketch, "E2268", {"start": v(-21.32, -0.14) * mm, "end": v(-21.3, -0.17) * mm});
            skLineSegment(sketch, "E2269", {"start": v(-21.3, -0.17) * mm, "end": v(-21.19, -0.28) * mm});
            skLineSegment(sketch, "E2270", {"start": v(-21.19, -0.28) * mm, "end": v(-20.1, -1.36) * mm});
            skLineSegment(sketch, "E2271", {"start": v(-20.1, -1.36) * mm, "end": v(-20, -1.47) * mm});
            skLineSegment(sketch, "E2272", {"start": v(-20, -1.47) * mm, "end": v(-19.96, -1.5) * mm});
            skLineSegment(sketch, "E2273", {"start": v(-19.96, -1.5) * mm, "end": v(-19.78, -1.56) * mm});
            skLineSegment(sketch, "E2274", {"start": v(-19.78, -1.56) * mm, "end": v(-19.6, -1.47) * mm});
            skLineSegment(sketch, "E2275", {"start": v(-19.6, -1.47) * mm, "end": v(-19.5, -1.28) * mm});
            skLineSegment(sketch, "E2276", {"start": v(-19.5, -1.28) * mm, "end": v(-19.55, -1.1) * mm});
            skLineSegment(sketch, "E2277", {"start": v(-19.55, -1.1) * mm, "end": v(-19.6, -1.07) * mm});
            skLineSegment(sketch, "E2278", {"start": v(-7.8, 1.07) * mm, "end": v(-7.7, 0.96) * mm});
            skLineSegment(sketch, "E2279", {"start": v(-7.7, 0.96) * mm, "end": v(-6.61, -0.13) * mm});
            skLineSegment(sketch, "E2280", {"start": v(-6.61, -0.13) * mm, "end": v(-6.5, -0.24) * mm});
            skLineSegment(sketch, "E2281", {"start": v(-6.5, -0.24) * mm, "end": v(-6.5, 0.17) * mm});
            skLineSegment(sketch, "E2282", {"start": v(-6.5, 0.17) * mm, "end": v(-7.74, -1.07) * mm});
            skLineSegment(sketch, "E2283", {"start": v(-7.74, -1.07) * mm, "end": v(-7.78, -1.1) * mm});
            skLineSegment(sketch, "E2284", {"start": v(-7.78, -1.1) * mm, "end": v(-7.83, -1.28) * mm});
            skLineSegment(sketch, "E2285", {"start": v(-7.83, -1.28) * mm, "end": v(-7.74, -1.47) * mm});
            skLineSegment(sketch, "E2286", {"start": v(-7.74, -1.47) * mm, "end": v(-7.55, -1.56) * mm});
            skLineSegment(sketch, "E2287", {"start": v(-7.55, -1.56) * mm, "end": v(-7.38, -1.5) * mm});
            skLineSegment(sketch, "E2288", {"start": v(-7.38, -1.5) * mm, "end": v(-7.34, -1.47) * mm});
            skLineSegment(sketch, "E2289", {"start": v(-7.34, -1.47) * mm, "end": v(-6.1, -0.24) * mm});
            skLineSegment(sketch, "E2290", {"start": v(-6.1, -0.24) * mm, "end": v(-6.08, -0.2) * mm});
            skLineSegment(sketch, "E2291", {"start": v(-6.08, -0.2) * mm, "end": v(-6.08, 0.14) * mm});
            skLineSegment(sketch, "E2292", {"start": v(-6.08, 0.14) * mm, "end": v(-6.1, 0.17) * mm});
            skLineSegment(sketch, "E2293", {"start": v(-6.1, 0.17) * mm, "end": v(-6.21, 0.28) * mm});
            skLineSegment(sketch, "E2294", {"start": v(-6.21, 0.28) * mm, "end": v(-7.3, 1.36) * mm});
            skLineSegment(sketch, "E2295", {"start": v(-7.3, 1.36) * mm, "end": v(-7.4, 1.47) * mm});
            skLineSegment(sketch, "E2296", {"start": v(-7.4, 1.47) * mm, "end": v(-7.44, 1.5) * mm});
            skLineSegment(sketch, "E2297", {"start": v(-7.44, 1.5) * mm, "end": v(-7.62, 1.55) * mm});
            skLineSegment(sketch, "E2298", {"start": v(-7.62, 1.55) * mm, "end": v(-7.8, 1.47) * mm});
            skLineSegment(sketch, "E2299", {"start": v(-7.8, 1.47) * mm, "end": v(-7.9, 1.28) * mm});
            skLineSegment(sketch, "E2300", {"start": v(-7.9, 1.28) * mm, "end": v(-7.85, 1.1) * mm});
            skLineSegment(sketch, "E2301", {"start": v(-7.85, 1.1) * mm, "end": v(-7.8, 1.07) * mm});
            skLineSegment(sketch, "E2302", {"start": v(-18.8, 6.32) * mm, "end": v(-18.8, 6.22) * mm});
            skLineSegment(sketch, "E2303", {"start": v(-18.8, 6.22) * mm, "end": v(-18.88, 5.93) * mm});
            skLineSegment(sketch, "E2304", {"start": v(-18.88, 5.93) * mm, "end": v(-19.1, 5.61) * mm});
            skLineSegment(sketch, "E2305", {"start": v(-19.1, 5.61) * mm, "end": v(-19.41, 5.4) * mm});
            skLineSegment(sketch, "E2306", {"start": v(-19.41, 5.4) * mm, "end": v(-19.7, 5.32) * mm});
            skLineSegment(sketch, "E2307", {"start": v(-19.7, 5.32) * mm, "end": v(-19.8, 5.32) * mm});
            skLineSegment(sketch, "E2308", {"start": v(-19.8, 5.32) * mm, "end": v(-19.9, 5.32) * mm});
            skLineSegment(sketch, "E2309", {"start": v(-19.9, 5.32) * mm, "end": v(-20.19, 5.4) * mm});
            skLineSegment(sketch, "E2310", {"start": v(-20.19, 5.4) * mm, "end": v(-20.5, 5.61) * mm});
            skLineSegment(sketch, "E2311", {"start": v(-20.5, 5.61) * mm, "end": v(-20.72, 5.93) * mm});
            skLineSegment(sketch, "E2312", {"start": v(-20.72, 5.93) * mm, "end": v(-20.8, 6.22) * mm});
            skLineSegment(sketch, "E2313", {"start": v(-20.8, 6.22) * mm, "end": v(-20.8, 6.32) * mm});
            skLineSegment(sketch, "E2314", {"start": v(-20.8, 6.32) * mm, "end": v(-20.8, 6.41) * mm});
            skLineSegment(sketch, "E2315", {"start": v(-20.8, 6.41) * mm, "end": v(-20.72, 6.7) * mm});
            skLineSegment(sketch, "E2316", {"start": v(-20.72, 6.7) * mm, "end": v(-20.5, 7.02) * mm});
            skLineSegment(sketch, "E2317", {"start": v(-20.5, 7.02) * mm, "end": v(-20.19, 7.24) * mm});
            skLineSegment(sketch, "E2318", {"start": v(-20.19, 7.24) * mm, "end": v(-19.9, 7.31) * mm});
            skLineSegment(sketch, "E2319", {"start": v(-19.9, 7.31) * mm, "end": v(-19.8, 7.31) * mm});
            skLineSegment(sketch, "E2320", {"start": v(-19.8, 7.31) * mm, "end": v(-19.7, 7.31) * mm});
            skLineSegment(sketch, "E2321", {"start": v(-19.7, 7.31) * mm, "end": v(-19.41, 7.24) * mm});
            skLineSegment(sketch, "E2322", {"start": v(-19.41, 7.24) * mm, "end": v(-19.1, 7.02) * mm});
            skLineSegment(sketch, "E2323", {"start": v(-19.1, 7.02) * mm, "end": v(-18.88, 6.7) * mm});
            skLineSegment(sketch, "E2324", {"start": v(-18.88, 6.7) * mm, "end": v(-18.8, 6.41) * mm});
            skLineSegment(sketch, "E2325", {"start": v(-18.8, 6.41) * mm, "end": v(-18.8, 6.32) * mm});
            skLineSegment(sketch, "E2326", {"start": v(-6.11, 6.32) * mm, "end": v(-6.11, 6.22) * mm});
            skLineSegment(sketch, "E2327", {"start": v(-6.11, 6.22) * mm, "end": v(-6.2, 5.93) * mm});
            skLineSegment(sketch, "E2328", {"start": v(-6.2, 5.93) * mm, "end": v(-6.4, 5.61) * mm});
            skLineSegment(sketch, "E2329", {"start": v(-6.4, 5.61) * mm, "end": v(-6.72, 5.4) * mm});
            skLineSegment(sketch, "E2330", {"start": v(-6.72, 5.4) * mm, "end": v(-7.01, 5.32) * mm});
            skLineSegment(sketch, "E2331", {"start": v(-7.01, 5.32) * mm, "end": v(-7.1, 5.32) * mm});
            skLineSegment(sketch, "E2332", {"start": v(-7.1, 5.32) * mm, "end": v(-7.2, 5.32) * mm});
            skLineSegment(sketch, "E2333", {"start": v(-7.2, 5.32) * mm, "end": v(-7.5, 5.4) * mm});
            skLineSegment(sketch, "E2334", {"start": v(-7.5, 5.4) * mm, "end": v(-7.81, 5.61) * mm});
            skLineSegment(sketch, "E2335", {"start": v(-7.81, 5.61) * mm, "end": v(-8.03, 5.93) * mm});
            skLineSegment(sketch, "E2336", {"start": v(-8.03, 5.93) * mm, "end": v(-8.1, 6.22) * mm});
            skLineSegment(sketch, "E2337", {"start": v(-8.1, 6.22) * mm, "end": v(-8.1, 6.32) * mm});
            skLineSegment(sketch, "E2338", {"start": v(-8.1, 6.32) * mm, "end": v(-8.1, 6.41) * mm});
            skLineSegment(sketch, "E2339", {"start": v(-8.1, 6.41) * mm, "end": v(-8.03, 6.7) * mm});
            skLineSegment(sketch, "E2340", {"start": v(-8.03, 6.7) * mm, "end": v(-7.81, 7.02) * mm});
            skLineSegment(sketch, "E2341", {"start": v(-7.81, 7.02) * mm, "end": v(-7.5, 7.24) * mm});
            skLineSegment(sketch, "E2342", {"start": v(-7.5, 7.24) * mm, "end": v(-7.2, 7.31) * mm});
            skLineSegment(sketch, "E2343", {"start": v(-7.2, 7.31) * mm, "end": v(-7.1, 7.31) * mm});
            skLineSegment(sketch, "E2344", {"start": v(-7.1, 7.31) * mm, "end": v(-7.01, 7.31) * mm});
            skLineSegment(sketch, "E2345", {"start": v(-7.01, 7.31) * mm, "end": v(-6.72, 7.24) * mm});
            skLineSegment(sketch, "E2346", {"start": v(-6.72, 7.24) * mm, "end": v(-6.4, 7.02) * mm});
            skLineSegment(sketch, "E2347", {"start": v(-6.4, 7.02) * mm, "end": v(-6.2, 6.7) * mm});
            skLineSegment(sketch, "E2348", {"start": v(-6.2, 6.7) * mm, "end": v(-6.11, 6.41) * mm});
            skLineSegment(sketch, "E2349", {"start": v(-6.11, 6.41) * mm, "end": v(-6.11, 6.32) * mm});
            skLineSegment(sketch, "E2350", {"start": v(-6.11, -6.46) * mm, "end": v(-6.11, -6.56) * mm});
            skLineSegment(sketch, "E2351", {"start": v(-6.11, -6.56) * mm, "end": v(-6.2, -6.85) * mm});
            skLineSegment(sketch, "E2352", {"start": v(-6.2, -6.85) * mm, "end": v(-6.4, -7.16) * mm});
            skLineSegment(sketch, "E2353", {"start": v(-6.4, -7.16) * mm, "end": v(-6.72, -7.38) * mm});
            skLineSegment(sketch, "E2354", {"start": v(-6.72, -7.38) * mm, "end": v(-7.01, -7.46) * mm});
            skLineSegment(sketch, "E2355", {"start": v(-7.01, -7.46) * mm, "end": v(-7.1, -7.46) * mm});
            skLineSegment(sketch, "E2356", {"start": v(-7.1, -7.46) * mm, "end": v(-7.2, -7.46) * mm});
            skLineSegment(sketch, "E2357", {"start": v(-7.2, -7.46) * mm, "end": v(-7.5, -7.38) * mm});
            skLineSegment(sketch, "E2358", {"start": v(-7.5, -7.38) * mm, "end": v(-7.81, -7.16) * mm});
            skLineSegment(sketch, "E2359", {"start": v(-7.81, -7.16) * mm, "end": v(-8.03, -6.85) * mm});
            skLineSegment(sketch, "E2360", {"start": v(-8.03, -6.85) * mm, "end": v(-8.1, -6.56) * mm});
            skLineSegment(sketch, "E2361", {"start": v(-8.1, -6.56) * mm, "end": v(-8.1, -6.46) * mm});
            skLineSegment(sketch, "E2362", {"start": v(-8.1, -6.46) * mm, "end": v(-8.1, -6.36) * mm});
            skLineSegment(sketch, "E2363", {"start": v(-8.1, -6.36) * mm, "end": v(-8.03, -6.07) * mm});
            skLineSegment(sketch, "E2364", {"start": v(-8.03, -6.07) * mm, "end": v(-7.81, -5.75) * mm});
            skLineSegment(sketch, "E2365", {"start": v(-7.81, -5.75) * mm, "end": v(-7.5, -5.54) * mm});
            skLineSegment(sketch, "E2366", {"start": v(-7.5, -5.54) * mm, "end": v(-7.2, -5.46) * mm});
            skLineSegment(sketch, "E2367", {"start": v(-7.2, -5.46) * mm, "end": v(-7.1, -5.46) * mm});
            skLineSegment(sketch, "E2368", {"start": v(-7.1, -5.46) * mm, "end": v(-7.01, -5.46) * mm});
            skLineSegment(sketch, "E2369", {"start": v(-7.01, -5.46) * mm, "end": v(-6.72, -5.54) * mm});
            skLineSegment(sketch, "E2370", {"start": v(-6.72, -5.54) * mm, "end": v(-6.4, -5.75) * mm});
            skLineSegment(sketch, "E2371", {"start": v(-6.4, -5.75) * mm, "end": v(-6.2, -6.07) * mm});
            skLineSegment(sketch, "E2372", {"start": v(-6.2, -6.07) * mm, "end": v(-6.11, -6.36) * mm});
            skLineSegment(sketch, "E2373", {"start": v(-6.11, -6.36) * mm, "end": v(-6.11, -6.46) * mm});
            skSolve(sketch);
        }
        {
            var Q0;
            Q0 = qSketchRegion(id + "F9", true);
            var Q1;
            {var subQ1=sQuery(id+"F9.wireOp",EDGE,"E1963");Q1=makeQuery(id+"F9.imprint","IMPRINT",FACE,{"disambiguationData":[TD([[makeQuery(id+"F9.imprint","IMPRINT",EDGE,{"derivedFrom":subQ1}),-1.0]])]});}
            var Q2;
            {var subQ12=sQuery(id+"F9.wireOp",EDGE,"E1972");Q2=makeQuery(id+"F9.imprint","IMPRINT",FACE,{"disambiguationData":[TD([[makeQuery(id+"F9.imprint","IMPRINT",EDGE,{"derivedFrom":subQ12}),-1.0]])]});}
            var Q3;
            {var subQ11=sQuery(id+"F9.wireOp",EDGE,"E1976");Q3=makeQuery(id+"F9.imprint","IMPRINT",FACE,{"disambiguationData":[TD([[makeQuery(id+"F9.imprint","IMPRINT",EDGE,{"derivedFrom":subQ11}),-1.0]])]});}
            var Q4;
            {var subQ0=sQuery(id+"F9.wireOp",EDGE,"E1965");var subQ1=sQuery(id+"F9.wireOp",EDGE,"E1828");var subQ2=makeQuery(id+"F9.imprint","INTERSECT",VERTEX,{"derivedFrom":[subQ1,subQ0]});Q4=makeQuery(id+"F9.imprint","IMPRINT",FACE,{"disambiguationData":[TD([[makeQuery(id+"F9.imprint","IMPRINT",EDGE,{"disambiguationData":[TD([[subQ2,-1.0]])],"derivedFrom":subQ1}),1.0]])]});}
            var Q5;
            {var subQ5=sQuery(id+"F9.wireOp",EDGE,"E1963");Q5=makeQuery(id+"F9.imprint","IMPRINT",FACE,{"disambiguationData":[TD([[makeQuery(id+"F9.imprint","IMPRINT",EDGE,{"derivedFrom":subQ5}),1.0]])]});}
            var Q6;
            {var subQ0=sQuery(id+"F9.wireOp",EDGE,"E1954");var subQ1=sQuery(id+"F9.wireOp",EDGE,"E1859");var subQ2=makeQuery(id+"F9.imprint","INTERSECT",VERTEX,{"derivedFrom":[subQ1,subQ0]});Q6=makeQuery(id+"F9.imprint","IMPRINT",FACE,{"disambiguationData":[TD([[makeQuery(id+"F9.imprint","IMPRINT",EDGE,{"disambiguationData":[TD([[subQ2,1.0]])],"derivedFrom":subQ1}),-1.0]])]});}
            var Q7;
            Q7=makeQuery(id+"F9.imprint","IMPRINT",FACE,{"disambiguationData":[TD([[makeQuery(id+"F9.imprint","IMPRINT",EDGE,{"derivedFrom":sQuery(id+"F9.wireOp",EDGE,"E1983")}),-1.0]])]});
            var Q8;
            Q8=makeQuery(id+"F9.imprint","IMPRINT",FACE,{"disambiguationData":[TD([[makeQuery(id+"F9.imprint","IMPRINT",EDGE,{"derivedFrom":sQuery(id+"F9.wireOp",EDGE,"E2159")}),-1.0]])]});
            extrude(context, id + "F10", {"entities" : qUnion([Q0, Q1, Q2, Q3, Q4, Q5, Q6, Q7, Q8]), "operationType" : NewBodyOperationType.REMOVE, "oppositeDirection" : true, "depth" : 3 * mm});
        }
        {
            var Q0;
            Q0=makeQuery(id+"F1.opExtrude","SWEPT_FACE",FACE,{"disambiguationData":[OSD([sQuery(id+"F0.wireOp",EDGE,"E0.bottom")])]});
            var sketch = newSketch(context, id + "F11", { "sketchPlane" : qUnion([Q0])});
            skLineSegment(sketch, "E2374", {"start": v(-0.31, -9.92) * mm, "end": v(-0.61, -9.92) * mm});
            skLineSegment(sketch, "E2375", {"start": v(-0.61, -9.92) * mm, "end": v(-1.5, -10.15) * mm});
            skLineSegment(sketch, "E2376", {"start": v(-1.5, -10.15) * mm, "end": v(-2.36, -10.68) * mm});
            skLineSegment(sketch, "E2377", {"start": v(-2.36, -10.68) * mm, "end": v(-2.51, -10.83) * mm});
            skLineSegment(sketch, "E2378", {"start": v(-2.51, -10.83) * mm, "end": v(-2.66, -10.98) * mm});
            skLineSegment(sketch, "E2379", {"start": v(-2.66, -10.98) * mm, "end": v(-3.19, -11.84) * mm});
            skLineSegment(sketch, "E2380", {"start": v(-3.19, -11.84) * mm, "end": v(-3.42, -12.73) * mm});
            skLineSegment(sketch, "E2381", {"start": v(-3.42, -12.73) * mm, "end": v(-3.42, -13.03) * mm});
            skLineSegment(sketch, "E2382", {"start": v(-3.42, -13.03) * mm, "end": v(-3.42, -13.33) * mm});
            skLineSegment(sketch, "E2383", {"start": v(-3.42, -13.33) * mm, "end": v(-3.19, -14.22) * mm});
            skLineSegment(sketch, "E2384", {"start": v(-3.19, -14.22) * mm, "end": v(-2.66, -15.08) * mm});
            skLineSegment(sketch, "E2385", {"start": v(-2.66, -15.08) * mm, "end": v(-2.51, -15.23) * mm});
            skLineSegment(sketch, "E2386", {"start": v(-2.51, -15.23) * mm, "end": v(-2.34, -15.4) * mm});
            skLineSegment(sketch, "E2387", {"start": v(-2.34, -15.4) * mm, "end": v(-1.72, -15.8) * mm});
            skLineSegment(sketch, "E2388", {"start": v(-1.72, -15.8) * mm, "end": v(-0.8, -16.1) * mm});
            skLineSegment(sketch, "E2389", {"start": v(-0.8, -16.1) * mm, "end": v(0.15, -16.1) * mm});
            skLineSegment(sketch, "E2390", {"start": v(0.15, -16.1) * mm, "end": v(0.86, -15.92) * mm});
            skLineSegment(sketch, "E2391", {"start": v(0.86, -15.92) * mm, "end": v(1.08, -15.81) * mm});
            skLineSegment(sketch, "E2392", {"start": v(1.08, -15.81) * mm, "end": v(1.15, -15.77) * mm});
            skLineSegment(sketch, "E2393", {"start": v(1.15, -15.77) * mm, "end": v(1.83, -15.29) * mm});
            skLineSegment(sketch, "E2394", {"start": v(1.83, -15.29) * mm, "end": v(1.89, -15.23) * mm});
            skLineSegment(sketch, "E2395", {"start": v(1.89, -15.23) * mm, "end": v(1.95, -15.17) * mm});
            skLineSegment(sketch, "E2396", {"start": v(1.95, -15.17) * mm, "end": v(2.43, -14.5) * mm});
            skLineSegment(sketch, "E2397", {"start": v(2.43, -14.5) * mm, "end": v(2.47, -14.42) * mm});
            skLineSegment(sketch, "E2398", {"start": v(2.47, -14.42) * mm, "end": v(2.58, -14.2) * mm});
            skLineSegment(sketch, "E2399", {"start": v(2.58, -14.2) * mm, "end": v(2.77, -13.49) * mm});
            skLineSegment(sketch, "E2400", {"start": v(2.77, -13.49) * mm, "end": v(2.76, -12.53) * mm});
            skLineSegment(sketch, "E2401", {"start": v(2.76, -12.53) * mm, "end": v(2.46, -11.62) * mm});
            skLineSegment(sketch, "E2402", {"start": v(2.46, -11.62) * mm, "end": v(2.06, -11) * mm});
            skLineSegment(sketch, "E2403", {"start": v(2.06, -11) * mm, "end": v(1.89, -10.83) * mm});
            skLineSegment(sketch, "E2404", {"start": v(1.89, -10.83) * mm, "end": v(1.74, -10.68) * mm});
            skLineSegment(sketch, "E2405", {"start": v(1.74, -10.68) * mm, "end": v(0.88, -10.15) * mm});
            skLineSegment(sketch, "E2406", {"start": v(0.88, -10.15) * mm, "end": v(-0.01, -9.92) * mm});
            skLineSegment(sketch, "E2407", {"start": v(-0.01, -9.92) * mm, "end": v(-0.31, -9.92) * mm});
            skLineSegment(sketch, "E2408", {"start": v(-0.31, -16.41) * mm, "end": v(-0.63, -16.41) * mm});
            skLineSegment(sketch, "E2409", {"start": v(-0.63, -16.41) * mm, "end": v(-1.6, -16.16) * mm});
            skLineSegment(sketch, "E2410", {"start": v(-1.6, -16.16) * mm, "end": v(-2.54, -15.58) * mm});
            skLineSegment(sketch, "E2411", {"start": v(-2.54, -15.58) * mm, "end": v(-2.7, -15.42) * mm});
            skLineSegment(sketch, "E2412", {"start": v(-2.7, -15.42) * mm, "end": v(-2.86, -15.26) * mm});
            skLineSegment(sketch, "E2413", {"start": v(-2.86, -15.26) * mm, "end": v(-3.44, -14.32) * mm});
            skLineSegment(sketch, "E2414", {"start": v(-3.44, -14.32) * mm, "end": v(-3.69, -13.35) * mm});
            skLineSegment(sketch, "E2415", {"start": v(-3.69, -13.35) * mm, "end": v(-3.69, -13.03) * mm});
            skLineSegment(sketch, "E2416", {"start": v(-3.69, -13.03) * mm, "end": v(-3.69, -12.7) * mm});
            skLineSegment(sketch, "E2417", {"start": v(-3.69, -12.7) * mm, "end": v(-3.44, -11.74) * mm});
            skLineSegment(sketch, "E2418", {"start": v(-3.44, -11.74) * mm, "end": v(-2.86, -10.8) * mm});
            skLineSegment(sketch, "E2419", {"start": v(-2.86, -10.8) * mm, "end": v(-2.7, -10.64) * mm});
            skLineSegment(sketch, "E2420", {"start": v(-2.7, -10.64) * mm, "end": v(-2.54, -10.48) * mm});
            skLineSegment(sketch, "E2421", {"start": v(-2.54, -10.48) * mm, "end": v(-1.6, -9.9) * mm});
            skLineSegment(sketch, "E2422", {"start": v(-1.6, -9.9) * mm, "end": v(-0.64, -9.65) * mm});
            skLineSegment(sketch, "E2423", {"start": v(-0.64, -9.65) * mm, "end": v(-0.31, -9.65) * mm});
            skLineSegment(sketch, "E2424", {"start": v(-0.31, -9.65) * mm, "end": v(0.01, -9.65) * mm});
            skLineSegment(sketch, "E2425", {"start": v(0.01, -9.65) * mm, "end": v(0.98, -9.9) * mm});
            skLineSegment(sketch, "E2426", {"start": v(0.98, -9.9) * mm, "end": v(1.92, -10.48) * mm});
            skLineSegment(sketch, "E2427", {"start": v(1.92, -10.48) * mm, "end": v(2.08, -10.64) * mm});
            skLineSegment(sketch, "E2428", {"start": v(2.08, -10.64) * mm, "end": v(2.26, -10.83) * mm});
            skLineSegment(sketch, "E2429", {"start": v(2.26, -10.83) * mm, "end": v(2.7, -11.5) * mm});
            skLineSegment(sketch, "E2430", {"start": v(2.7, -11.5) * mm, "end": v(3.02, -12.49) * mm});
            skLineSegment(sketch, "E2431", {"start": v(3.02, -12.49) * mm, "end": v(3.03, -13.53) * mm});
            skLineSegment(sketch, "E2432", {"start": v(3.03, -13.53) * mm, "end": v(2.83, -14.3) * mm});
            skLineSegment(sketch, "E2433", {"start": v(2.83, -14.3) * mm, "end": v(2.71, -14.54) * mm});
            skLineSegment(sketch, "E2434", {"start": v(2.71, -14.54) * mm, "end": v(2.67, -14.62) * mm});
            skLineSegment(sketch, "E2435", {"start": v(2.67, -14.62) * mm, "end": v(2.14, -15.35) * mm});
            skLineSegment(sketch, "E2436", {"start": v(2.14, -15.35) * mm, "end": v(2.08, -15.42) * mm});
            skLineSegment(sketch, "E2437", {"start": v(2.08, -15.42) * mm, "end": v(2.01, -15.48) * mm});
            skLineSegment(sketch, "E2438", {"start": v(2.01, -15.48) * mm, "end": v(1.28, -16.01) * mm});
            skLineSegment(sketch, "E2439", {"start": v(1.28, -16.01) * mm, "end": v(1.2, -16.05) * mm});
            skLineSegment(sketch, "E2440", {"start": v(1.2, -16.05) * mm, "end": v(1.08, -16.11) * mm});
            skLineSegment(sketch, "E2441", {"start": v(1.08, -16.11) * mm, "end": v(0.04, -16.41) * mm});
            skLineSegment(sketch, "E2442", {"start": v(0.04, -16.41) * mm, "end": v(-0.31, -16.41) * mm});
            skLineSegment(sketch, "E2443", {"start": v(1.35, -15.97) * mm, "end": v(2.52, -17.47) * mm});
            skLineSegment(sketch, "E2444", {"start": v(2.52, -17.47) * mm, "end": v(2.57, -17.53) * mm});
            skLineSegment(sketch, "E2445", {"start": v(2.57, -17.53) * mm, "end": v(2.9, -17.78) * mm});
            skLineSegment(sketch, "E2446", {"start": v(2.9, -17.78) * mm, "end": v(3.27, -17.9) * mm});
            skLineSegment(sketch, "E2447", {"start": v(3.27, -17.9) * mm, "end": v(3.35, -17.9) * mm});
            skLineSegment(sketch, "E2448", {"start": v(3.35, -17.9) * mm, "end": v(3.44, -17.9) * mm});
            skLineSegment(sketch, "E2449", {"start": v(3.44, -17.9) * mm, "end": v(3.83, -17.83) * mm});
            skLineSegment(sketch, "E2450", {"start": v(3.83, -17.83) * mm, "end": v(4.17, -17.63) * mm});
            skLineSegment(sketch, "E2451", {"start": v(4.17, -17.63) * mm, "end": v(4.23, -17.57) * mm});
            skLineSegment(sketch, "E2452", {"start": v(4.23, -17.57) * mm, "end": v(4.29, -17.51) * mm});
            skLineSegment(sketch, "E2453", {"start": v(4.29, -17.51) * mm, "end": v(4.49, -17.17) * mm});
            skLineSegment(sketch, "E2454", {"start": v(4.49, -17.17) * mm, "end": v(4.57, -16.78) * mm});
            skLineSegment(sketch, "E2455", {"start": v(4.57, -16.78) * mm, "end": v(4.56, -16.7) * mm});
            skLineSegment(sketch, "E2456", {"start": v(4.56, -16.7) * mm, "end": v(4.56, -16.61) * mm});
            skLineSegment(sketch, "E2457", {"start": v(4.56, -16.61) * mm, "end": v(4.43, -16.23) * mm});
            skLineSegment(sketch, "E2458", {"start": v(4.43, -16.23) * mm, "end": v(4.2, -15.92) * mm});
            skLineSegment(sketch, "E2459", {"start": v(4.2, -15.92) * mm, "end": v(4.13, -15.87) * mm});
            skLineSegment(sketch, "E2460", {"start": v(4.13, -15.87) * mm, "end": v(2.63, -14.69) * mm});
            skLineSegment(sketch, "E2461", {"start": v(2.63, -14.69) * mm, "end": v(2.6, -14.75) * mm});
            skLineSegment(sketch, "E2462", {"start": v(2.6, -14.75) * mm, "end": v(2.13, -15.36) * mm});
            skLineSegment(sketch, "E2463", {"start": v(2.13, -15.36) * mm, "end": v(2.08, -15.42) * mm});
            skLineSegment(sketch, "E2464", {"start": v(2.08, -15.42) * mm, "end": v(2.02, -15.47) * mm});
            skLineSegment(sketch, "E2465", {"start": v(2.02, -15.47) * mm, "end": v(1.41, -15.94) * mm});
            skLineSegment(sketch, "E2466", {"start": v(1.41, -15.94) * mm, "end": v(1.35, -15.97) * mm});
            skLineSegment(sketch, "E2467", {"start": v(3.42, -18.17) * mm, "end": v(3.4, -18.17) * mm});
            skLineSegment(sketch, "E2468", {"start": v(3.4, -18.17) * mm, "end": v(3.34, -18.17) * mm});
            skLineSegment(sketch, "E2469", {"start": v(3.34, -18.17) * mm, "end": v(3.34, -18.17) * mm});
            skLineSegment(sketch, "E2470", {"start": v(3.34, -18.17) * mm, "end": v(3.24, -18.17) * mm});
            skLineSegment(sketch, "E2471", {"start": v(3.24, -18.17) * mm, "end": v(2.77, -18.01) * mm});
            skLineSegment(sketch, "E2472", {"start": v(2.77, -18.01) * mm, "end": v(2.37, -17.72) * mm});
            skLineSegment(sketch, "E2473", {"start": v(2.37, -17.72) * mm, "end": v(2.31, -17.64) * mm});
            skLineSegment(sketch, "E2474", {"start": v(2.31, -17.64) * mm, "end": v(1.04, -16.02) * mm});
            skLineSegment(sketch, "E2475", {"start": v(1.04, -16.02) * mm, "end": v(1.03, -16) * mm});
            skLineSegment(sketch, "E2476", {"start": v(1.03, -16) * mm, "end": v(1, -15.91) * mm});
            skLineSegment(sketch, "E2477", {"start": v(1, -15.91) * mm, "end": v(1, -15.9) * mm});
            skLineSegment(sketch, "E2478", {"start": v(1, -15.9) * mm, "end": v(1.01, -15.9) * mm});
            skLineSegment(sketch, "E2479", {"start": v(1.01, -15.9) * mm, "end": v(1.07, -15.81) * mm});
            skLineSegment(sketch, "E2480", {"start": v(1.07, -15.81) * mm, "end": v(1.08, -15.81) * mm});
            skLineSegment(sketch, "E2481", {"start": v(2.47, -14.42) * mm, "end": v(2.47, -14.41) * mm});
            skLineSegment(sketch, "E2482", {"start": v(2.47, -14.41) * mm, "end": v(2.55, -14.35) * mm});
            skLineSegment(sketch, "E2483", {"start": v(2.55, -14.35) * mm, "end": v(2.56, -14.35) * mm});
            skLineSegment(sketch, "E2484", {"start": v(2.56, -14.35) * mm, "end": v(2.57, -14.35) * mm});
            skLineSegment(sketch, "E2485", {"start": v(2.57, -14.35) * mm, "end": v(2.66, -14.37) * mm});
            skLineSegment(sketch, "E2486", {"start": v(2.66, -14.37) * mm, "end": v(2.67, -14.38) * mm});
            skLineSegment(sketch, "E2487", {"start": v(2.67, -14.38) * mm, "end": v(4.3, -15.65) * mm});
            skLineSegment(sketch, "E2488", {"start": v(4.3, -15.65) * mm, "end": v(4.37, -15.72) * mm});
            skLineSegment(sketch, "E2489", {"start": v(4.37, -15.72) * mm, "end": v(4.67, -16.1) * mm});
            skLineSegment(sketch, "E2490", {"start": v(4.67, -16.1) * mm, "end": v(4.83, -16.58) * mm});
            skLineSegment(sketch, "E2491", {"start": v(4.83, -16.58) * mm, "end": v(4.83, -16.68) * mm});
            skLineSegment(sketch, "E2492", {"start": v(4.83, -16.68) * mm, "end": v(4.84, -16.78) * mm});
            skLineSegment(sketch, "E2493", {"start": v(4.84, -16.78) * mm, "end": v(4.74, -17.26) * mm});
            skLineSegment(sketch, "E2494", {"start": v(4.74, -17.26) * mm, "end": v(4.5, -17.7) * mm});
            skLineSegment(sketch, "E2495", {"start": v(4.5, -17.7) * mm, "end": v(4.42, -17.76) * mm});
            skLineSegment(sketch, "E2496", {"start": v(4.42, -17.76) * mm, "end": v(4.35, -17.83) * mm});
            skLineSegment(sketch, "E2497", {"start": v(4.35, -17.83) * mm, "end": v(3.96, -18.07) * mm});
            skLineSegment(sketch, "E2498", {"start": v(3.96, -18.07) * mm, "end": v(3.56, -18.17) * mm});
            skLineSegment(sketch, "E2499", {"start": v(3.56, -18.17) * mm, "end": v(3.42, -18.17) * mm});
            skLineSegment(sketch, "E2500", {"start": v(3.42, -17.57) * mm, "end": v(3.26, -17.57) * mm});
            skLineSegment(sketch, "E2501", {"start": v(3.26, -17.57) * mm, "end": v(2.83, -17.31) * mm});
            skLineSegment(sketch, "E2502", {"start": v(2.83, -17.31) * mm, "end": v(2.79, -17.26) * mm});
            skLineSegment(sketch, "E2503", {"start": v(2.79, -17.26) * mm, "end": v(1.88, -16.11) * mm});
            skLineSegment(sketch, "E2504", {"start": v(1.88, -16.11) * mm, "end": v(1.88, -16.1) * mm});
            skLineSegment(sketch, "E2505", {"start": v(1.88, -16.1) * mm, "end": v(1.88, -16.02) * mm});
            skLineSegment(sketch, "E2506", {"start": v(1.88, -16.02) * mm, "end": v(1.9, -16.02) * mm});
            skLineSegment(sketch, "E2507", {"start": v(1.9, -16.02) * mm, "end": v(1.9, -16.01) * mm});
            skLineSegment(sketch, "E2508", {"start": v(1.9, -16.01) * mm, "end": v(1.98, -16.02) * mm});
            skLineSegment(sketch, "E2509", {"start": v(1.98, -16.02) * mm, "end": v(1.99, -16.03) * mm});
            skLineSegment(sketch, "E2510", {"start": v(1.99, -16.03) * mm, "end": v(2.9, -17.18) * mm});
            skLineSegment(sketch, "E2511", {"start": v(2.9, -17.18) * mm, "end": v(2.92, -17.22) * mm});
            skLineSegment(sketch, "E2512", {"start": v(2.92, -17.22) * mm, "end": v(3.3, -17.44) * mm});
            skLineSegment(sketch, "E2513", {"start": v(3.3, -17.44) * mm, "end": v(3.42, -17.44) * mm});
            skLineSegment(sketch, "E2514", {"start": v(3.42, -17.44) * mm, "end": v(3.54, -17.44) * mm});
            skLineSegment(sketch, "E2515", {"start": v(3.54, -17.44) * mm, "end": v(3.87, -17.27) * mm});
            skLineSegment(sketch, "E2516", {"start": v(3.87, -17.27) * mm, "end": v(3.9, -17.24) * mm});
            skLineSegment(sketch, "E2517", {"start": v(3.9, -17.24) * mm, "end": v(3.9, -17.23) * mm});
            skLineSegment(sketch, "E2518", {"start": v(3.9, -17.23) * mm, "end": v(3.99, -17.23) * mm});
            skLineSegment(sketch, "E2519", {"start": v(3.99, -17.23) * mm, "end": v(4, -17.24) * mm});
            skLineSegment(sketch, "E2520", {"start": v(4, -17.24) * mm, "end": v(4, -17.25) * mm});
            skLineSegment(sketch, "E2521", {"start": v(4, -17.25) * mm, "end": v(4, -17.33) * mm});
            skLineSegment(sketch, "E2522", {"start": v(4, -17.33) * mm, "end": v(4, -17.33) * mm});
            skLineSegment(sketch, "E2523", {"start": v(4, -17.33) * mm, "end": v(3.95, -17.37) * mm});
            skLineSegment(sketch, "E2524", {"start": v(3.95, -17.37) * mm, "end": v(3.55, -17.57) * mm});
            skLineSegment(sketch, "E2525", {"start": v(3.55, -17.57) * mm, "end": v(3.42, -17.57) * mm});
            skLineSegment(sketch, "E2526", {"start": v(-0.31, -10.87) * mm, "end": v(-0.52, -10.87) * mm});
            skLineSegment(sketch, "E2527", {"start": v(-0.52, -10.87) * mm, "end": v(-1.13, -11.03) * mm});
            skLineSegment(sketch, "E2528", {"start": v(-1.13, -11.03) * mm, "end": v(-1.74, -11.4) * mm});
            skLineSegment(sketch, "E2529", {"start": v(-1.74, -11.4) * mm, "end": v(-1.84, -11.5) * mm});
            skLineSegment(sketch, "E2530", {"start": v(-1.84, -11.5) * mm, "end": v(-1.99, -11.65) * mm});
            skLineSegment(sketch, "E2531", {"start": v(-1.99, -11.65) * mm, "end": v(-2.32, -12.22) * mm});
            skLineSegment(sketch, "E2532", {"start": v(-2.32, -12.22) * mm, "end": v(-2.47, -13.03) * mm});
            skLineSegment(sketch, "E2533", {"start": v(-2.47, -13.03) * mm, "end": v(-2.32, -13.84) * mm});
            skLineSegment(sketch, "E2534", {"start": v(-2.32, -13.84) * mm, "end": v(-1.99, -14.4) * mm});
            skLineSegment(sketch, "E2535", {"start": v(-1.99, -14.4) * mm, "end": v(-1.84, -14.56) * mm});
            skLineSegment(sketch, "E2536", {"start": v(-1.84, -14.56) * mm, "end": v(-1.74, -14.66) * mm});
            skLineSegment(sketch, "E2537", {"start": v(-1.74, -14.66) * mm, "end": v(-1.14, -15.03) * mm});
            skLineSegment(sketch, "E2538", {"start": v(-1.14, -15.03) * mm, "end": v(-0.52, -15.2) * mm});
            skLineSegment(sketch, "E2539", {"start": v(-0.52, -15.2) * mm, "end": v(-0.31, -15.2) * mm});
            skLineSegment(sketch, "E2540", {"start": v(-0.31, -15.2) * mm, "end": v(-0.1, -15.2) * mm});
            skLineSegment(sketch, "E2541", {"start": v(-0.1, -15.2) * mm, "end": v(0.51, -15.03) * mm});
            skLineSegment(sketch, "E2542", {"start": v(0.51, -15.03) * mm, "end": v(1.11, -14.66) * mm});
            skLineSegment(sketch, "E2543", {"start": v(1.11, -14.66) * mm, "end": v(1.22, -14.56) * mm});
            skLineSegment(sketch, "E2544", {"start": v(1.22, -14.56) * mm, "end": v(1.32, -14.46) * mm});
            skLineSegment(sketch, "E2545", {"start": v(1.32, -14.46) * mm, "end": v(1.69, -13.86) * mm});
            skLineSegment(sketch, "E2546", {"start": v(1.69, -13.86) * mm, "end": v(1.85, -13.24) * mm});
            skLineSegment(sketch, "E2547", {"start": v(1.85, -13.24) * mm, "end": v(1.85, -13.03) * mm});
            skLineSegment(sketch, "E2548", {"start": v(1.85, -13.03) * mm, "end": v(1.85, -12.82) * mm});
            skLineSegment(sketch, "E2549", {"start": v(1.85, -12.82) * mm, "end": v(1.69, -12.2) * mm});
            skLineSegment(sketch, "E2550", {"start": v(1.69, -12.2) * mm, "end": v(1.32, -11.6) * mm});
            skLineSegment(sketch, "E2551", {"start": v(1.32, -11.6) * mm, "end": v(1.22, -11.5) * mm});
            skLineSegment(sketch, "E2552", {"start": v(1.22, -11.5) * mm, "end": v(1.11, -11.4) * mm});
            skLineSegment(sketch, "E2553", {"start": v(1.11, -11.4) * mm, "end": v(0.5, -11.03) * mm});
            skLineSegment(sketch, "E2554", {"start": v(0.5, -11.03) * mm, "end": v(-0.1, -10.87) * mm});
            skLineSegment(sketch, "E2555", {"start": v(-0.1, -10.87) * mm, "end": v(-0.31, -10.87) * mm});
            skLineSegment(sketch, "E2556", {"start": v(-0.31, -15.33) * mm, "end": v(-0.53, -15.33) * mm});
            skLineSegment(sketch, "E2557", {"start": v(-0.53, -15.33) * mm, "end": v(-1.2, -15.15) * mm});
            skLineSegment(sketch, "E2558", {"start": v(-1.2, -15.15) * mm, "end": v(-1.83, -14.76) * mm});
            skLineSegment(sketch, "E2559", {"start": v(-1.83, -14.76) * mm, "end": v(-1.94, -14.65) * mm});
            skLineSegment(sketch, "E2560", {"start": v(-1.94, -14.65) * mm, "end": v(-2.1, -14.5) * mm});
            skLineSegment(sketch, "E2561", {"start": v(-2.1, -14.5) * mm, "end": v(-2.44, -13.9) * mm});
            skLineSegment(sketch, "E2562", {"start": v(-2.44, -13.9) * mm, "end": v(-2.6, -13.03) * mm});
            skLineSegment(sketch, "E2563", {"start": v(-2.6, -13.03) * mm, "end": v(-2.44, -12.16) * mm});
            skLineSegment(sketch, "E2564", {"start": v(-2.44, -12.16) * mm, "end": v(-2.1, -11.56) * mm});
            skLineSegment(sketch, "E2565", {"start": v(-2.1, -11.56) * mm, "end": v(-1.94, -11.4) * mm});
            skLineSegment(sketch, "E2566", {"start": v(-1.94, -11.4) * mm, "end": v(-1.78, -11.25) * mm});
            skLineSegment(sketch, "E2567", {"start": v(-1.78, -11.25) * mm, "end": v(-1.18, -10.9) * mm});
            skLineSegment(sketch, "E2568", {"start": v(-1.18, -10.9) * mm, "end": v(-0.31, -10.73) * mm});
            skLineSegment(sketch, "E2569", {"start": v(-0.31, -10.73) * mm, "end": v(0.55, -10.9) * mm});
            skLineSegment(sketch, "E2570", {"start": v(0.55, -10.9) * mm, "end": v(1.15, -11.25) * mm});
            skLineSegment(sketch, "E2571", {"start": v(1.15, -11.25) * mm, "end": v(1.31, -11.4) * mm});
            skLineSegment(sketch, "E2572", {"start": v(1.31, -11.4) * mm, "end": v(1.42, -11.51) * mm});
            skLineSegment(sketch, "E2573", {"start": v(1.42, -11.51) * mm, "end": v(1.81, -12.15) * mm});
            skLineSegment(sketch, "E2574", {"start": v(1.81, -12.15) * mm, "end": v(1.98, -12.8) * mm});
            skLineSegment(sketch, "E2575", {"start": v(1.98, -12.8) * mm, "end": v(1.98, -13.03) * mm});
            skLineSegment(sketch, "E2576", {"start": v(1.98, -13.03) * mm, "end": v(1.98, -13.25) * mm});
            skLineSegment(sketch, "E2577", {"start": v(1.98, -13.25) * mm, "end": v(1.81, -13.9) * mm});
            skLineSegment(sketch, "E2578", {"start": v(1.81, -13.9) * mm, "end": v(1.42, -14.55) * mm});
            skLineSegment(sketch, "E2579", {"start": v(1.42, -14.55) * mm, "end": v(1.31, -14.65) * mm});
            skLineSegment(sketch, "E2580", {"start": v(1.31, -14.65) * mm, "end": v(1.2, -14.76) * mm});
            skLineSegment(sketch, "E2581", {"start": v(1.2, -14.76) * mm, "end": v(0.57, -15.15) * mm});
            skLineSegment(sketch, "E2582", {"start": v(0.57, -15.15) * mm, "end": v(-0.1, -15.33) * mm});
            skLineSegment(sketch, "E2583", {"start": v(-0.1, -15.33) * mm, "end": v(-0.31, -15.33) * mm});
            skLineSegment(sketch, "E2584", {"start": v(-0.52, -8.11) * mm, "end": v(-0.4, -8) * mm});
            skLineSegment(sketch, "E2585", {"start": v(-0.4, -8) * mm, "end": v(0.68, -6.92) * mm});
            skLineSegment(sketch, "E2586", {"start": v(0.68, -6.92) * mm, "end": v(0.79, -6.8) * mm});
            skLineSegment(sketch, "E2587", {"start": v(0.79, -6.8) * mm, "end": v(0.39, -6.8) * mm});
            skLineSegment(sketch, "E2588", {"start": v(0.39, -6.8) * mm, "end": v(1.62, -8.04) * mm});
            skLineSegment(sketch, "E2589", {"start": v(1.62, -8.04) * mm, "end": v(1.66, -8.08) * mm});
            skLineSegment(sketch, "E2590", {"start": v(1.66, -8.08) * mm, "end": v(1.83, -8.13) * mm});
            skLineSegment(sketch, "E2591", {"start": v(1.83, -8.13) * mm, "end": v(2.02, -8.04) * mm});
            skLineSegment(sketch, "E2592", {"start": v(2.02, -8.04) * mm, "end": v(2.1, -7.85) * mm});
            skLineSegment(sketch, "E2593", {"start": v(2.1, -7.85) * mm, "end": v(2.06, -7.68) * mm});
            skLineSegment(sketch, "E2594", {"start": v(2.06, -7.68) * mm, "end": v(2.03, -7.64) * mm});
            skLineSegment(sketch, "E2595", {"start": v(2.03, -7.64) * mm, "end": v(1.92, -7.54) * mm});
            skLineSegment(sketch, "E2596", {"start": v(1.92, -7.54) * mm, "end": v(0.9, -6.5) * mm});
            skLineSegment(sketch, "E2597", {"start": v(0.9, -6.5) * mm, "end": v(0.79, -6.4) * mm});
            skLineSegment(sketch, "E2598", {"start": v(0.79, -6.4) * mm, "end": v(0.76, -6.38) * mm});
            skLineSegment(sketch, "E2599", {"start": v(0.76, -6.38) * mm, "end": v(0.41, -6.38) * mm});
            skLineSegment(sketch, "E2600", {"start": v(0.41, -6.38) * mm, "end": v(0.39, -6.4) * mm});
            skLineSegment(sketch, "E2601", {"start": v(0.39, -6.4) * mm, "end": v(0.28, -6.51) * mm});
            skLineSegment(sketch, "E2602", {"start": v(0.28, -6.51) * mm, "end": v(-0.8, -7.6) * mm});
            skLineSegment(sketch, "E2603", {"start": v(-0.8, -7.6) * mm, "end": v(-0.92, -7.7) * mm});
            skLineSegment(sketch, "E2604", {"start": v(-0.92, -7.7) * mm, "end": v(-0.96, -7.74) * mm});
            skLineSegment(sketch, "E2605", {"start": v(-0.96, -7.74) * mm, "end": v(-1, -7.92) * mm});
            skLineSegment(sketch, "E2606", {"start": v(-1, -7.92) * mm, "end": v(-0.91, -8.1) * mm});
            skLineSegment(sketch, "E2607", {"start": v(-0.91, -8.1) * mm, "end": v(-0.72, -8.2) * mm});
            skLineSegment(sketch, "E2608", {"start": v(-0.72, -8.2) * mm, "end": v(-0.55, -8.15) * mm});
            skLineSegment(sketch, "E2609", {"start": v(-0.55, -8.15) * mm, "end": v(-0.52, -8.11) * mm});
            skLineSegment(sketch, "E2610", {"start": v(1.62, -19.9) * mm, "end": v(1.51, -20) * mm});
            skLineSegment(sketch, "E2611", {"start": v(1.51, -20) * mm, "end": v(0.43, -21.09) * mm});
            skLineSegment(sketch, "E2612", {"start": v(0.43, -21.09) * mm, "end": v(0.32, -21.2) * mm});
            skLineSegment(sketch, "E2613", {"start": v(0.32, -21.2) * mm, "end": v(0.72, -21.2) * mm});
            skLineSegment(sketch, "E2614", {"start": v(0.72, -21.2) * mm, "end": v(0.62, -21.1) * mm});
            skLineSegment(sketch, "E2615", {"start": v(0.62, -21.1) * mm, "end": v(-0.41, -20.06) * mm});
            skLineSegment(sketch, "E2616", {"start": v(-0.41, -20.06) * mm, "end": v(-0.52, -19.96) * mm});
            skLineSegment(sketch, "E2617", {"start": v(-0.52, -19.96) * mm, "end": v(-0.55, -19.92) * mm});
            skLineSegment(sketch, "E2618", {"start": v(-0.55, -19.92) * mm, "end": v(-0.73, -19.87) * mm});
            skLineSegment(sketch, "E2619", {"start": v(-0.73, -19.87) * mm, "end": v(-0.91, -19.96) * mm});
            skLineSegment(sketch, "E2620", {"start": v(-0.91, -19.96) * mm, "end": v(-1, -20.15) * mm});
            skLineSegment(sketch, "E2621", {"start": v(-1, -20.15) * mm, "end": v(-0.96, -20.32) * mm});
            skLineSegment(sketch, "E2622", {"start": v(-0.96, -20.32) * mm, "end": v(-0.92, -20.36) * mm});
            skLineSegment(sketch, "E2623", {"start": v(-0.92, -20.36) * mm, "end": v(-0.82, -20.46) * mm});
            skLineSegment(sketch, "E2624", {"start": v(-0.82, -20.46) * mm, "end": v(0.22, -21.5) * mm});
            skLineSegment(sketch, "E2625", {"start": v(0.22, -21.5) * mm, "end": v(0.32, -21.6) * mm});
            skLineSegment(sketch, "E2626", {"start": v(0.32, -21.6) * mm, "end": v(0.35, -21.62) * mm});
            skLineSegment(sketch, "E2627", {"start": v(0.35, -21.62) * mm, "end": v(0.7, -21.62) * mm});
            skLineSegment(sketch, "E2628", {"start": v(0.7, -21.62) * mm, "end": v(0.72, -21.6) * mm});
            skLineSegment(sketch, "E2629", {"start": v(0.72, -21.6) * mm, "end": v(0.83, -21.49) * mm});
            skLineSegment(sketch, "E2630", {"start": v(0.83, -21.49) * mm, "end": v(1.92, -20.4) * mm});
            skLineSegment(sketch, "E2631", {"start": v(1.92, -20.4) * mm, "end": v(2.03, -20.3) * mm});
            skLineSegment(sketch, "E2632", {"start": v(2.03, -20.3) * mm, "end": v(2.06, -20.26) * mm});
            skLineSegment(sketch, "E2633", {"start": v(2.06, -20.26) * mm, "end": v(2.1, -20.08) * mm});
            skLineSegment(sketch, "E2634", {"start": v(2.1, -20.08) * mm, "end": v(2.02, -19.9) * mm});
            skLineSegment(sketch, "E2635", {"start": v(2.02, -19.9) * mm, "end": v(1.83, -19.8) * mm});
            skLineSegment(sketch, "E2636", {"start": v(1.83, -19.8) * mm, "end": v(1.66, -19.85) * mm});
            skLineSegment(sketch, "E2637", {"start": v(1.66, -19.85) * mm, "end": v(1.62, -19.9) * mm});
            skLineSegment(sketch, "E2638", {"start": v(-4.55, -7.68) * mm, "end": v(-4.55, -7.78) * mm});
            skLineSegment(sketch, "E2639", {"start": v(-4.55, -7.78) * mm, "end": v(-4.63, -8.07) * mm});
            skLineSegment(sketch, "E2640", {"start": v(-4.63, -8.07) * mm, "end": v(-4.84, -8.39) * mm});
            skLineSegment(sketch, "E2641", {"start": v(-4.84, -8.39) * mm, "end": v(-5.16, -8.6) * mm});
            skLineSegment(sketch, "E2642", {"start": v(-5.16, -8.6) * mm, "end": v(-5.45, -8.68) * mm});
            skLineSegment(sketch, "E2643", {"start": v(-5.45, -8.68) * mm, "end": v(-5.55, -8.68) * mm});
            skLineSegment(sketch, "E2644", {"start": v(-5.55, -8.68) * mm, "end": v(-5.64, -8.68) * mm});
            skLineSegment(sketch, "E2645", {"start": v(-5.64, -8.68) * mm, "end": v(-5.93, -8.6) * mm});
            skLineSegment(sketch, "E2646", {"start": v(-5.93, -8.6) * mm, "end": v(-6.25, -8.39) * mm});
            skLineSegment(sketch, "E2647", {"start": v(-6.25, -8.39) * mm, "end": v(-6.46, -8.07) * mm});
            skLineSegment(sketch, "E2648", {"start": v(-6.46, -8.07) * mm, "end": v(-6.54, -7.78) * mm});
            skLineSegment(sketch, "E2649", {"start": v(-6.54, -7.78) * mm, "end": v(-6.54, -7.68) * mm});
            skLineSegment(sketch, "E2650", {"start": v(-6.54, -7.68) * mm, "end": v(-6.54, -7.59) * mm});
            skLineSegment(sketch, "E2651", {"start": v(-6.54, -7.59) * mm, "end": v(-6.46, -7.3) * mm});
            skLineSegment(sketch, "E2652", {"start": v(-6.46, -7.3) * mm, "end": v(-6.25, -6.98) * mm});
            skLineSegment(sketch, "E2653", {"start": v(-6.25, -6.98) * mm, "end": v(-5.93, -6.76) * mm});
            skLineSegment(sketch, "E2654", {"start": v(-5.93, -6.76) * mm, "end": v(-5.64, -6.69) * mm});
            skLineSegment(sketch, "E2655", {"start": v(-5.64, -6.69) * mm, "end": v(-5.55, -6.69) * mm});
            skLineSegment(sketch, "E2656", {"start": v(-5.55, -6.69) * mm, "end": v(-5.45, -6.69) * mm});
            skLineSegment(sketch, "E2657", {"start": v(-5.45, -6.69) * mm, "end": v(-5.16, -6.76) * mm});
            skLineSegment(sketch, "E2658", {"start": v(-5.16, -6.76) * mm, "end": v(-4.84, -6.98) * mm});
            skLineSegment(sketch, "E2659", {"start": v(-4.84, -6.98) * mm, "end": v(-4.63, -7.3) * mm});
            skLineSegment(sketch, "E2660", {"start": v(-4.63, -7.3) * mm, "end": v(-4.55, -7.59) * mm});
            skLineSegment(sketch, "E2661", {"start": v(-4.55, -7.59) * mm, "end": v(-4.55, -7.68) * mm});
            skLineSegment(sketch, "E2662", {"start": v(8.14, -7.68) * mm, "end": v(8.14, -7.78) * mm});
            skLineSegment(sketch, "E2663", {"start": v(8.14, -7.78) * mm, "end": v(8.06, -8.07) * mm});
            skLineSegment(sketch, "E2664", {"start": v(8.06, -8.07) * mm, "end": v(7.85, -8.39) * mm});
            skLineSegment(sketch, "E2665", {"start": v(7.85, -8.39) * mm, "end": v(7.53, -8.6) * mm});
            skLineSegment(sketch, "E2666", {"start": v(7.53, -8.6) * mm, "end": v(7.24, -8.68) * mm});
            skLineSegment(sketch, "E2667", {"start": v(7.24, -8.68) * mm, "end": v(7.15, -8.68) * mm});
            skLineSegment(sketch, "E2668", {"start": v(7.15, -8.68) * mm, "end": v(7.05, -8.68) * mm});
            skLineSegment(sketch, "E2669", {"start": v(7.05, -8.68) * mm, "end": v(6.76, -8.6) * mm});
            skLineSegment(sketch, "E2670", {"start": v(6.76, -8.6) * mm, "end": v(6.44, -8.39) * mm});
            skLineSegment(sketch, "E2671", {"start": v(6.44, -8.39) * mm, "end": v(6.23, -8.07) * mm});
            skLineSegment(sketch, "E2672", {"start": v(6.23, -8.07) * mm, "end": v(6.15, -7.78) * mm});
            skLineSegment(sketch, "E2673", {"start": v(6.15, -7.78) * mm, "end": v(6.15, -7.68) * mm});
            skLineSegment(sketch, "E2674", {"start": v(6.15, -7.68) * mm, "end": v(6.15, -7.59) * mm});
            skLineSegment(sketch, "E2675", {"start": v(6.15, -7.59) * mm, "end": v(6.23, -7.3) * mm});
            skLineSegment(sketch, "E2676", {"start": v(6.23, -7.3) * mm, "end": v(6.44, -6.98) * mm});
            skLineSegment(sketch, "E2677", {"start": v(6.44, -6.98) * mm, "end": v(6.76, -6.76) * mm});
            skLineSegment(sketch, "E2678", {"start": v(6.76, -6.76) * mm, "end": v(7.05, -6.69) * mm});
            skLineSegment(sketch, "E2679", {"start": v(7.05, -6.69) * mm, "end": v(7.15, -6.69) * mm});
            skLineSegment(sketch, "E2680", {"start": v(7.15, -6.69) * mm, "end": v(7.24, -6.69) * mm});
            skLineSegment(sketch, "E2681", {"start": v(7.24, -6.69) * mm, "end": v(7.53, -6.76) * mm});
            skLineSegment(sketch, "E2682", {"start": v(7.53, -6.76) * mm, "end": v(7.85, -6.98) * mm});
            skLineSegment(sketch, "E2683", {"start": v(7.85, -6.98) * mm, "end": v(8.06, -7.3) * mm});
            skLineSegment(sketch, "E2684", {"start": v(8.06, -7.3) * mm, "end": v(8.14, -7.59) * mm});
            skLineSegment(sketch, "E2685", {"start": v(8.14, -7.59) * mm, "end": v(8.14, -7.68) * mm});
            skLineSegment(sketch, "E2686", {"start": v(8.14, -20.46) * mm, "end": v(8.14, -20.56) * mm});
            skLineSegment(sketch, "E2687", {"start": v(8.14, -20.56) * mm, "end": v(8.06, -20.85) * mm});
            skLineSegment(sketch, "E2688", {"start": v(8.06, -20.85) * mm, "end": v(7.85, -21.16) * mm});
            skLineSegment(sketch, "E2689", {"start": v(7.85, -21.16) * mm, "end": v(7.53, -21.38) * mm});
            skLineSegment(sketch, "E2690", {"start": v(7.53, -21.38) * mm, "end": v(7.24, -21.46) * mm});
            skLineSegment(sketch, "E2691", {"start": v(7.24, -21.46) * mm, "end": v(7.15, -21.46) * mm});
            skLineSegment(sketch, "E2692", {"start": v(7.15, -21.46) * mm, "end": v(7.05, -21.46) * mm});
            skLineSegment(sketch, "E2693", {"start": v(7.05, -21.46) * mm, "end": v(6.76, -21.38) * mm});
            skLineSegment(sketch, "E2694", {"start": v(6.76, -21.38) * mm, "end": v(6.44, -21.16) * mm});
            skLineSegment(sketch, "E2695", {"start": v(6.44, -21.16) * mm, "end": v(6.23, -20.85) * mm});
            skLineSegment(sketch, "E2696", {"start": v(6.23, -20.85) * mm, "end": v(6.15, -20.56) * mm});
            skLineSegment(sketch, "E2697", {"start": v(6.15, -20.56) * mm, "end": v(6.15, -20.46) * mm});
            skLineSegment(sketch, "E2698", {"start": v(6.15, -20.46) * mm, "end": v(6.15, -20.36) * mm});
            skLineSegment(sketch, "E2699", {"start": v(6.15, -20.36) * mm, "end": v(6.23, -20.07) * mm});
            skLineSegment(sketch, "E2700", {"start": v(6.23, -20.07) * mm, "end": v(6.44, -19.75) * mm});
            skLineSegment(sketch, "E2701", {"start": v(6.44, -19.75) * mm, "end": v(6.76, -19.54) * mm});
            skLineSegment(sketch, "E2702", {"start": v(6.76, -19.54) * mm, "end": v(7.05, -19.46) * mm});
            skLineSegment(sketch, "E2703", {"start": v(7.05, -19.46) * mm, "end": v(7.15, -19.46) * mm});
            skLineSegment(sketch, "E2704", {"start": v(7.15, -19.46) * mm, "end": v(7.24, -19.46) * mm});
            skLineSegment(sketch, "E2705", {"start": v(7.24, -19.46) * mm, "end": v(7.53, -19.54) * mm});
            skLineSegment(sketch, "E2706", {"start": v(7.53, -19.54) * mm, "end": v(7.85, -19.75) * mm});
            skLineSegment(sketch, "E2707", {"start": v(7.85, -19.75) * mm, "end": v(8.06, -20.07) * mm});
            skLineSegment(sketch, "E2708", {"start": v(8.06, -20.07) * mm, "end": v(8.14, -20.36) * mm});
            skLineSegment(sketch, "E2709", {"start": v(8.14, -20.36) * mm, "end": v(8.14, -20.46) * mm});
            skSolve(sketch);
        }
        {
            var Q0;
            Q0 = qSketchRegion(id + "F11", true);
            var Q1;
            Q1=makeQuery(id+"F11.imprint","IMPRINT",FACE,{"disambiguationData":[TD([[makeQuery(id+"F11.imprint","IMPRINT",EDGE,{"derivedFrom":sQuery(id+"F11.wireOp",EDGE,"E2526")}),-1.0]])]});
            var Q2;
            Q2=makeQuery(id+"F11.imprint","IMPRINT",FACE,{"disambiguationData":[TD([[makeQuery(id+"F11.imprint","IMPRINT",EDGE,{"derivedFrom":sQuery(id+"F11.wireOp",EDGE,"E2500")}),-1.0]])]});
            extrude(context, id + "F12", {"entities" : qUnion([Q0, Q1, Q2]), "operationType" : NewBodyOperationType.REMOVE, "oppositeDirection" : true, "depth" : 3 * mm});
        }
        {
            var Q0;
            Q0=makeQuery(id+"F1.opExtrude","SWEPT_FACE",FACE,{"disambiguationData":[OSD([sQuery(id+"F0.wireOp",EDGE,"E0.top")])]});
            var sketch = newSketch(context, id + "F13", { "sketchPlane" : qUnion([Q0])});
            skLineSegment(sketch, "E2710", {"start": v(1.14, 15.79) * mm, "end": v(2.55, 15.79) * mm});
            skLineSegment(sketch, "E2711", {"start": v(2.55, 15.79) * mm, "end": v(1.14, 17.2) * mm});
            skLineSegment(sketch, "E2712", {"start": v(1.14, 17.2) * mm, "end": v(1.14, 15.79) * mm});
            skLineSegment(sketch, "E2713", {"start": v(2.69, 15.67) * mm, "end": v(1.09, 15.67) * mm});
            skLineSegment(sketch, "E2714", {"start": v(1.09, 15.67) * mm, "end": v(1.07, 15.67) * mm});
            skLineSegment(sketch, "E2715", {"start": v(1.07, 15.67) * mm, "end": v(1.03, 15.72) * mm});
            skLineSegment(sketch, "E2716", {"start": v(1.03, 15.72) * mm, "end": v(1.03, 15.73) * mm});
            skLineSegment(sketch, "E2717", {"start": v(1.03, 15.73) * mm, "end": v(1.03, 17.33) * mm});
            skLineSegment(sketch, "E2718", {"start": v(1.03, 17.33) * mm, "end": v(1.03, 17.34) * mm});
            skLineSegment(sketch, "E2719", {"start": v(1.03, 17.34) * mm, "end": v(1.06, 17.38) * mm});
            skLineSegment(sketch, "E2720", {"start": v(1.06, 17.38) * mm, "end": v(1.06, 17.38) * mm});
            skLineSegment(sketch, "E2721", {"start": v(1.06, 17.38) * mm, "end": v(1.07, 17.38) * mm});
            skLineSegment(sketch, "E2722", {"start": v(1.07, 17.38) * mm, "end": v(1.12, 17.37) * mm});
            skLineSegment(sketch, "E2723", {"start": v(1.12, 17.37) * mm, "end": v(1.13, 17.37) * mm});
            skLineSegment(sketch, "E2724", {"start": v(1.13, 17.37) * mm, "end": v(2.72, 15.77) * mm});
            skLineSegment(sketch, "E2725", {"start": v(2.72, 15.77) * mm, "end": v(2.73, 15.77) * mm});
            skLineSegment(sketch, "E2726", {"start": v(2.73, 15.77) * mm, "end": v(2.74, 15.71) * mm});
            skLineSegment(sketch, "E2727", {"start": v(2.74, 15.71) * mm, "end": v(2.74, 15.7) * mm});
            skLineSegment(sketch, "E2728", {"start": v(2.74, 15.7) * mm, "end": v(2.73, 15.7) * mm});
            skLineSegment(sketch, "E2729", {"start": v(2.73, 15.7) * mm, "end": v(2.7, 15.67) * mm});
            skLineSegment(sketch, "E2730", {"start": v(2.7, 15.67) * mm, "end": v(2.69, 15.67) * mm});
            skLineSegment(sketch, "E2731", {"start": v(1.4, 13.65) * mm, "end": v(-1.31, 13.65) * mm});
            skLineSegment(sketch, "E2732", {"start": v(-1.31, 13.65) * mm, "end": v(-1.33, 13.65) * mm});
            skLineSegment(sketch, "E2733", {"start": v(-1.33, 13.65) * mm, "end": v(-1.37, 13.7) * mm});
            skLineSegment(sketch, "E2734", {"start": v(-1.37, 13.7) * mm, "end": v(-1.37, 13.7) * mm});
            skLineSegment(sketch, "E2735", {"start": v(-1.37, 13.7) * mm, "end": v(-1.37, 13.72) * mm});
            skLineSegment(sketch, "E2736", {"start": v(-1.37, 13.72) * mm, "end": v(-1.33, 13.76) * mm});
            skLineSegment(sketch, "E2737", {"start": v(-1.33, 13.76) * mm, "end": v(-1.31, 13.76) * mm});
            skLineSegment(sketch, "E2738", {"start": v(-1.31, 13.76) * mm, "end": v(1.4, 13.76) * mm});
            skLineSegment(sketch, "E2739", {"start": v(1.4, 13.76) * mm, "end": v(1.41, 13.76) * mm});
            skLineSegment(sketch, "E2740", {"start": v(1.41, 13.76) * mm, "end": v(1.45, 13.72) * mm});
            skLineSegment(sketch, "E2741", {"start": v(1.45, 13.72) * mm, "end": v(1.45, 13.7) * mm});
            skLineSegment(sketch, "E2742", {"start": v(1.45, 13.7) * mm, "end": v(1.45, 13.7) * mm});
            skLineSegment(sketch, "E2743", {"start": v(1.45, 13.7) * mm, "end": v(1.41, 13.65) * mm});
            skLineSegment(sketch, "E2744", {"start": v(1.41, 13.65) * mm, "end": v(1.4, 13.65) * mm});
            skLineSegment(sketch, "E2745", {"start": v(1.4, 14.62) * mm, "end": v(-1.31, 14.62) * mm});
            skLineSegment(sketch, "E2746", {"start": v(-1.31, 14.62) * mm, "end": v(-1.33, 14.62) * mm});
            skLineSegment(sketch, "E2747", {"start": v(-1.33, 14.62) * mm, "end": v(-1.37, 14.67) * mm});
            skLineSegment(sketch, "E2748", {"start": v(-1.37, 14.67) * mm, "end": v(-1.37, 14.68) * mm});
            skLineSegment(sketch, "E2749", {"start": v(-1.37, 14.68) * mm, "end": v(-1.37, 14.7) * mm});
            skLineSegment(sketch, "E2750", {"start": v(-1.37, 14.7) * mm, "end": v(-1.33, 14.74) * mm});
            skLineSegment(sketch, "E2751", {"start": v(-1.33, 14.74) * mm, "end": v(-1.31, 14.74) * mm});
            skLineSegment(sketch, "E2752", {"start": v(-1.31, 14.74) * mm, "end": v(1.4, 14.74) * mm});
            skLineSegment(sketch, "E2753", {"start": v(1.4, 14.74) * mm, "end": v(1.41, 14.74) * mm});
            skLineSegment(sketch, "E2754", {"start": v(1.41, 14.74) * mm, "end": v(1.45, 14.7) * mm});
            skLineSegment(sketch, "E2755", {"start": v(1.45, 14.7) * mm, "end": v(1.45, 14.68) * mm});
            skLineSegment(sketch, "E2756", {"start": v(1.45, 14.68) * mm, "end": v(1.45, 14.67) * mm});
            skLineSegment(sketch, "E2757", {"start": v(1.45, 14.67) * mm, "end": v(1.41, 14.62) * mm});
            skLineSegment(sketch, "E2758", {"start": v(1.41, 14.62) * mm, "end": v(1.4, 14.62) * mm});
            skLineSegment(sketch, "E2759", {"start": v(1.38, 13.14) * mm, "end": v(-1.33, 13.14) * mm});
            skLineSegment(sketch, "E2760", {"start": v(-1.33, 13.14) * mm, "end": v(-1.35, 13.14) * mm});
            skLineSegment(sketch, "E2761", {"start": v(-1.35, 13.14) * mm, "end": v(-1.39, 13.19) * mm});
            skLineSegment(sketch, "E2762", {"start": v(-1.39, 13.19) * mm, "end": v(-1.39, 13.2) * mm});
            skLineSegment(sketch, "E2763", {"start": v(-1.39, 13.2) * mm, "end": v(-1.39, 13.22) * mm});
            skLineSegment(sketch, "E2764", {"start": v(-1.39, 13.22) * mm, "end": v(-1.35, 13.26) * mm});
            skLineSegment(sketch, "E2765", {"start": v(-1.35, 13.26) * mm, "end": v(-1.33, 13.26) * mm});
            skLineSegment(sketch, "E2766", {"start": v(-1.33, 13.26) * mm, "end": v(1.38, 13.26) * mm});
            skLineSegment(sketch, "E2767", {"start": v(1.38, 13.26) * mm, "end": v(1.4, 13.26) * mm});
            skLineSegment(sketch, "E2768", {"start": v(1.4, 13.26) * mm, "end": v(1.44, 13.22) * mm});
            skLineSegment(sketch, "E2769", {"start": v(1.44, 13.22) * mm, "end": v(1.44, 13.2) * mm});
            skLineSegment(sketch, "E2770", {"start": v(1.44, 13.2) * mm, "end": v(1.44, 13.19) * mm});
            skLineSegment(sketch, "E2771", {"start": v(1.44, 13.19) * mm, "end": v(1.4, 13.14) * mm});
            skLineSegment(sketch, "E2772", {"start": v(1.4, 13.14) * mm, "end": v(1.38, 13.14) * mm});
            skLineSegment(sketch, "E2773", {"start": v(1.38, 12.64) * mm, "end": v(-1.33, 12.64) * mm});
            skLineSegment(sketch, "E2774", {"start": v(-1.33, 12.64) * mm, "end": v(-1.35, 12.64) * mm});
            skLineSegment(sketch, "E2775", {"start": v(-1.35, 12.64) * mm, "end": v(-1.39, 12.68) * mm});
            skLineSegment(sketch, "E2776", {"start": v(-1.39, 12.68) * mm, "end": v(-1.39, 12.7) * mm});
            skLineSegment(sketch, "E2777", {"start": v(-1.39, 12.7) * mm, "end": v(-1.39, 12.71) * mm});
            skLineSegment(sketch, "E2778", {"start": v(-1.39, 12.71) * mm, "end": v(-1.35, 12.75) * mm});
            skLineSegment(sketch, "E2779", {"start": v(-1.35, 12.75) * mm, "end": v(-1.33, 12.75) * mm});
            skLineSegment(sketch, "E2780", {"start": v(-1.33, 12.75) * mm, "end": v(1.38, 12.75) * mm});
            skLineSegment(sketch, "E2781", {"start": v(1.38, 12.75) * mm, "end": v(1.4, 12.75) * mm});
            skLineSegment(sketch, "E2782", {"start": v(1.4, 12.75) * mm, "end": v(1.44, 12.71) * mm});
            skLineSegment(sketch, "E2783", {"start": v(1.44, 12.71) * mm, "end": v(1.44, 12.7) * mm});
            skLineSegment(sketch, "E2784", {"start": v(1.44, 12.7) * mm, "end": v(1.44, 12.68) * mm});
            skLineSegment(sketch, "E2785", {"start": v(1.44, 12.68) * mm, "end": v(1.4, 12.64) * mm});
            skLineSegment(sketch, "E2786", {"start": v(1.4, 12.64) * mm, "end": v(1.38, 12.64) * mm});
            skLineSegment(sketch, "E2787", {"start": v(-0.19, 11.03) * mm, "end": v(-1.3, 11.03) * mm});
            skLineSegment(sketch, "E2788", {"start": v(-1.3, 11.03) * mm, "end": v(-1.32, 11.03) * mm});
            skLineSegment(sketch, "E2789", {"start": v(-1.32, 11.03) * mm, "end": v(-1.35, 11.06) * mm});
            skLineSegment(sketch, "E2790", {"start": v(-1.35, 11.06) * mm, "end": v(-1.35, 11.07) * mm});
            skLineSegment(sketch, "E2791", {"start": v(-1.35, 11.07) * mm, "end": v(-1.35, 11.08) * mm});
            skLineSegment(sketch, "E2792", {"start": v(-1.35, 11.08) * mm, "end": v(-1.32, 11.1) * mm});
            skLineSegment(sketch, "E2793", {"start": v(-1.32, 11.1) * mm, "end": v(-1.3, 11.1) * mm});
            skLineSegment(sketch, "E2794", {"start": v(-1.3, 11.1) * mm, "end": v(-0.19, 11.1) * mm});
            skLineSegment(sketch, "E2795", {"start": v(-0.19, 11.1) * mm, "end": v(-0.18, 11.1) * mm});
            skLineSegment(sketch, "E2796", {"start": v(-0.18, 11.1) * mm, "end": v(-0.15, 11.08) * mm});
            skLineSegment(sketch, "E2797", {"start": v(-0.15, 11.08) * mm, "end": v(-0.15, 11.07) * mm});
            skLineSegment(sketch, "E2798", {"start": v(-0.15, 11.07) * mm, "end": v(-0.15, 11.06) * mm});
            skLineSegment(sketch, "E2799", {"start": v(-0.15, 11.06) * mm, "end": v(-0.18, 11.03) * mm});
            skLineSegment(sketch, "E2800", {"start": v(-0.18, 11.03) * mm, "end": v(-0.19, 11.03) * mm});
            skLineSegment(sketch, "E2801", {"start": v(-1, 11.66) * mm, "end": v(-1.02, 11.66) * mm});
            skLineSegment(sketch, "E2802", {"start": v(-1.02, 11.66) * mm, "end": v(-1.04, 11.65) * mm});
            skLineSegment(sketch, "E2803", {"start": v(-1.04, 11.65) * mm, "end": v(-1.04, 11.65) * mm});
            skLineSegment(sketch, "E2804", {"start": v(-1.04, 11.65) * mm, "end": v(-1.07, 11.58) * mm});
            skLineSegment(sketch, "E2805", {"start": v(-1.07, 11.58) * mm, "end": v(-1.07, 11.57) * mm});
            skLineSegment(sketch, "E2806", {"start": v(-1.07, 11.57) * mm, "end": v(-1.07, 11.57) * mm});
            skLineSegment(sketch, "E2807", {"start": v(-1.07, 11.57) * mm, "end": v(-1.04, 11.49) * mm});
            skLineSegment(sketch, "E2808", {"start": v(-1.04, 11.49) * mm, "end": v(-1.04, 11.48) * mm});
            skLineSegment(sketch, "E2809", {"start": v(-1.04, 11.48) * mm, "end": v(-1.04, 11.48) * mm});
            skLineSegment(sketch, "E2810", {"start": v(-1.04, 11.48) * mm, "end": v(-1.02, 11.46) * mm});
            skLineSegment(sketch, "E2811", {"start": v(-1.02, 11.46) * mm, "end": v(-1.02, 11.45) * mm});
            skLineSegment(sketch, "E2812", {"start": v(-1.02, 11.45) * mm, "end": v(-1.02, 11.46) * mm});
            skLineSegment(sketch, "E2813", {"start": v(-1.02, 11.46) * mm, "end": v(-0.98, 11.54) * mm});
            skLineSegment(sketch, "E2814", {"start": v(-0.98, 11.54) * mm, "end": v(-0.98, 11.54) * mm});
            skLineSegment(sketch, "E2815", {"start": v(-0.98, 11.54) * mm, "end": v(-0.97, 11.56) * mm});
            skLineSegment(sketch, "E2816", {"start": v(-0.97, 11.56) * mm, "end": v(-0.97, 11.64) * mm});
            skLineSegment(sketch, "E2817", {"start": v(-0.97, 11.64) * mm, "end": v(-0.97, 11.64) * mm});
            skLineSegment(sketch, "E2818", {"start": v(-0.97, 11.64) * mm, "end": v(-0.97, 11.65) * mm});
            skLineSegment(sketch, "E2819", {"start": v(-0.97, 11.65) * mm, "end": v(-1, 11.66) * mm});
            skLineSegment(sketch, "E2820", {"start": v(-1, 11.66) * mm, "end": v(-1, 11.66) * mm});
            skLineSegment(sketch, "E2821", {"start": v(-1.2, 11.26) * mm, "end": v(-1.2, 11.26) * mm});
            skLineSegment(sketch, "E2822", {"start": v(-1.2, 11.26) * mm, "end": v(-1.23, 11.28) * mm});
            skLineSegment(sketch, "E2823", {"start": v(-1.23, 11.28) * mm, "end": v(-1.23, 11.28) * mm});
            skLineSegment(sketch, "E2824", {"start": v(-1.23, 11.28) * mm, "end": v(-1.23, 11.29) * mm});
            skLineSegment(sketch, "E2825", {"start": v(-1.23, 11.29) * mm, "end": v(-1.2, 11.31) * mm});
            skLineSegment(sketch, "E2826", {"start": v(-1.2, 11.31) * mm, "end": v(-1.2, 11.31) * mm});
            skLineSegment(sketch, "E2827", {"start": v(-1.2, 11.31) * mm, "end": v(-1.07, 11.38) * mm});
            skLineSegment(sketch, "E2828", {"start": v(-1.07, 11.38) * mm, "end": v(-1.06, 11.39) * mm});
            skLineSegment(sketch, "E2829", {"start": v(-1.06, 11.39) * mm, "end": v(-1.06, 11.4) * mm});
            skLineSegment(sketch, "E2830", {"start": v(-1.06, 11.4) * mm, "end": v(-1.05, 11.4) * mm});
            skLineSegment(sketch, "E2831", {"start": v(-1.05, 11.4) * mm, "end": v(-1.05, 11.4) * mm});
            skLineSegment(sketch, "E2832", {"start": v(-1.05, 11.4) * mm, "end": v(-1.05, 11.41) * mm});
            skLineSegment(sketch, "E2833", {"start": v(-1.05, 11.41) * mm, "end": v(-1.08, 11.45) * mm});
            skLineSegment(sketch, "E2834", {"start": v(-1.08, 11.45) * mm, "end": v(-1.08, 11.45) * mm});
            skLineSegment(sketch, "E2835", {"start": v(-1.08, 11.45) * mm, "end": v(-1.1, 11.46) * mm});
            skLineSegment(sketch, "E2836", {"start": v(-1.1, 11.46) * mm, "end": v(-1.13, 11.56) * mm});
            skLineSegment(sketch, "E2837", {"start": v(-1.13, 11.56) * mm, "end": v(-1.13, 11.57) * mm});
            skLineSegment(sketch, "E2838", {"start": v(-1.13, 11.57) * mm, "end": v(-1.13, 11.58) * mm});
            skLineSegment(sketch, "E2839", {"start": v(-1.13, 11.58) * mm, "end": v(-1.08, 11.69) * mm});
            skLineSegment(sketch, "E2840", {"start": v(-1.08, 11.69) * mm, "end": v(-1.07, 11.7) * mm});
            skLineSegment(sketch, "E2841", {"start": v(-1.07, 11.7) * mm, "end": v(-1.06, 11.7) * mm});
            skLineSegment(sketch, "E2842", {"start": v(-1.06, 11.7) * mm, "end": v(-0.94, 11.68) * mm});
            skLineSegment(sketch, "E2843", {"start": v(-0.94, 11.68) * mm, "end": v(-0.93, 11.67) * mm});
            skLineSegment(sketch, "E2844", {"start": v(-0.93, 11.67) * mm, "end": v(-0.92, 11.66) * mm});
            skLineSegment(sketch, "E2845", {"start": v(-0.92, 11.66) * mm, "end": v(-0.93, 11.53) * mm});
            skLineSegment(sketch, "E2846", {"start": v(-0.93, 11.53) * mm, "end": v(-0.93, 11.52) * mm});
            skLineSegment(sketch, "E2847", {"start": v(-0.93, 11.52) * mm, "end": v(-0.94, 11.51) * mm});
            skLineSegment(sketch, "E2848", {"start": v(-0.94, 11.51) * mm, "end": v(-0.98, 11.42) * mm});
            skLineSegment(sketch, "E2849", {"start": v(-0.98, 11.42) * mm, "end": v(-0.99, 11.41) * mm});
            skLineSegment(sketch, "E2850", {"start": v(-0.99, 11.41) * mm, "end": v(-0.98, 11.4) * mm});
            skLineSegment(sketch, "E2851", {"start": v(-0.98, 11.4) * mm, "end": v(-0.93, 11.37) * mm});
            skLineSegment(sketch, "E2852", {"start": v(-0.93, 11.37) * mm, "end": v(-0.92, 11.36) * mm});
            skLineSegment(sketch, "E2853", {"start": v(-0.92, 11.36) * mm, "end": v(-0.91, 11.36) * mm});
            skLineSegment(sketch, "E2854", {"start": v(-0.91, 11.36) * mm, "end": v(-0.82, 11.33) * mm});
            skLineSegment(sketch, "E2855", {"start": v(-0.82, 11.33) * mm, "end": v(-0.81, 11.33) * mm});
            skLineSegment(sketch, "E2856", {"start": v(-0.81, 11.33) * mm, "end": v(-0.8, 11.33) * mm});
            skLineSegment(sketch, "E2857", {"start": v(-0.8, 11.33) * mm, "end": v(-0.73, 11.4) * mm});
            skLineSegment(sketch, "E2858", {"start": v(-0.73, 11.4) * mm, "end": v(-0.73, 11.41) * mm});
            skLineSegment(sketch, "E2859", {"start": v(-0.73, 11.41) * mm, "end": v(-0.73, 11.41) * mm});
            skLineSegment(sketch, "E2860", {"start": v(-0.73, 11.41) * mm, "end": v(-0.72, 11.44) * mm});
            skLineSegment(sketch, "E2861", {"start": v(-0.72, 11.44) * mm, "end": v(-0.72, 11.45) * mm});
            skLineSegment(sketch, "E2862", {"start": v(-0.72, 11.45) * mm, "end": v(-0.72, 11.46) * mm});
            skLineSegment(sketch, "E2863", {"start": v(-0.72, 11.46) * mm, "end": v(-0.73, 11.6) * mm});
            skLineSegment(sketch, "E2864", {"start": v(-0.73, 11.6) * mm, "end": v(-0.73, 11.62) * mm});
            skLineSegment(sketch, "E2865", {"start": v(-0.73, 11.62) * mm, "end": v(-0.73, 11.65) * mm});
            skLineSegment(sketch, "E2866", {"start": v(-0.73, 11.65) * mm, "end": v(-0.7, 11.64) * mm});
            skLineSegment(sketch, "E2867", {"start": v(-0.7, 11.64) * mm, "end": v(-0.7, 11.64) * mm});
            skLineSegment(sketch, "E2868", {"start": v(-0.7, 11.64) * mm, "end": v(-0.65, 11.56) * mm});
            skLineSegment(sketch, "E2869", {"start": v(-0.65, 11.56) * mm, "end": v(-0.65, 11.54) * mm});
            skLineSegment(sketch, "E2870", {"start": v(-0.65, 11.54) * mm, "end": v(-0.65, 11.53) * mm});
            skLineSegment(sketch, "E2871", {"start": v(-0.65, 11.53) * mm, "end": v(-0.66, 11.46) * mm});
            skLineSegment(sketch, "E2872", {"start": v(-0.66, 11.46) * mm, "end": v(-0.66, 11.45) * mm});
            skLineSegment(sketch, "E2873", {"start": v(-0.66, 11.45) * mm, "end": v(-0.66, 11.45) * mm});
            skLineSegment(sketch, "E2874", {"start": v(-0.66, 11.45) * mm, "end": v(-0.66, 11.43) * mm});
            skLineSegment(sketch, "E2875", {"start": v(-0.66, 11.43) * mm, "end": v(-0.66, 11.43) * mm});
            skLineSegment(sketch, "E2876", {"start": v(-0.66, 11.43) * mm, "end": v(-0.65, 11.42) * mm});
            skLineSegment(sketch, "E2877", {"start": v(-0.65, 11.42) * mm, "end": v(-0.61, 11.36) * mm});
            skLineSegment(sketch, "E2878", {"start": v(-0.61, 11.36) * mm, "end": v(-0.6, 11.36) * mm});
            skLineSegment(sketch, "E2879", {"start": v(-0.6, 11.36) * mm, "end": v(-0.6, 11.35) * mm});
            skLineSegment(sketch, "E2880", {"start": v(-0.6, 11.35) * mm, "end": v(-0.45, 11.35) * mm});
            skLineSegment(sketch, "E2881", {"start": v(-0.45, 11.35) * mm, "end": v(-0.44, 11.36) * mm});
            skLineSegment(sketch, "E2882", {"start": v(-0.44, 11.36) * mm, "end": v(-0.42, 11.36) * mm});
            skLineSegment(sketch, "E2883", {"start": v(-0.42, 11.36) * mm, "end": v(-0.3, 11.47) * mm});
            skLineSegment(sketch, "E2884", {"start": v(-0.3, 11.47) * mm, "end": v(-0.29, 11.49) * mm});
            skLineSegment(sketch, "E2885", {"start": v(-0.29, 11.49) * mm, "end": v(-0.28, 11.49) * mm});
            skLineSegment(sketch, "E2886", {"start": v(-0.28, 11.49) * mm, "end": v(-0.25, 11.5) * mm});
            skLineSegment(sketch, "E2887", {"start": v(-0.25, 11.5) * mm, "end": v(-0.25, 11.49) * mm});
            skLineSegment(sketch, "E2888", {"start": v(-0.25, 11.49) * mm, "end": v(-0.25, 11.48) * mm});
            skLineSegment(sketch, "E2889", {"start": v(-0.25, 11.48) * mm, "end": v(-0.24, 11.45) * mm});
            skLineSegment(sketch, "E2890", {"start": v(-0.24, 11.45) * mm, "end": v(-0.25, 11.45) * mm});
            skLineSegment(sketch, "E2891", {"start": v(-0.25, 11.45) * mm, "end": v(-0.26, 11.44) * mm});
            skLineSegment(sketch, "E2892", {"start": v(-0.26, 11.44) * mm, "end": v(-0.4, 11.32) * mm});
            skLineSegment(sketch, "E2893", {"start": v(-0.4, 11.32) * mm, "end": v(-0.41, 11.3) * mm});
            skLineSegment(sketch, "E2894", {"start": v(-0.41, 11.3) * mm, "end": v(-0.43, 11.3) * mm});
            skLineSegment(sketch, "E2895", {"start": v(-0.43, 11.3) * mm, "end": v(-0.63, 11.3) * mm});
            skLineSegment(sketch, "E2896", {"start": v(-0.63, 11.3) * mm, "end": v(-0.64, 11.32) * mm});
            skLineSegment(sketch, "E2897", {"start": v(-0.64, 11.32) * mm, "end": v(-0.64, 11.32) * mm});
            skLineSegment(sketch, "E2898", {"start": v(-0.64, 11.32) * mm, "end": v(-0.69, 11.37) * mm});
            skLineSegment(sketch, "E2899", {"start": v(-0.69, 11.37) * mm, "end": v(-0.69, 11.38) * mm});
            skLineSegment(sketch, "E2900", {"start": v(-0.69, 11.38) * mm, "end": v(-0.7, 11.36) * mm});
            skLineSegment(sketch, "E2901", {"start": v(-0.7, 11.36) * mm, "end": v(-0.8, 11.28) * mm});
            skLineSegment(sketch, "E2902", {"start": v(-0.8, 11.28) * mm, "end": v(-0.8, 11.28) * mm});
            skLineSegment(sketch, "E2903", {"start": v(-0.8, 11.28) * mm, "end": v(-0.82, 11.28) * mm});
            skLineSegment(sketch, "E2904", {"start": v(-0.82, 11.28) * mm, "end": v(-0.94, 11.3) * mm});
            skLineSegment(sketch, "E2905", {"start": v(-0.94, 11.3) * mm, "end": v(-0.95, 11.32) * mm});
            skLineSegment(sketch, "E2906", {"start": v(-0.95, 11.32) * mm, "end": v(-0.96, 11.32) * mm});
            skLineSegment(sketch, "E2907", {"start": v(-0.96, 11.32) * mm, "end": v(-1.01, 11.36) * mm});
            skLineSegment(sketch, "E2908", {"start": v(-1.01, 11.36) * mm, "end": v(-1.01, 11.37) * mm});
            skLineSegment(sketch, "E2909", {"start": v(-1.01, 11.37) * mm, "end": v(-1.02, 11.37) * mm});
            skLineSegment(sketch, "E2910", {"start": v(-1.02, 11.37) * mm, "end": v(-1.02, 11.36) * mm});
            skLineSegment(sketch, "E2911", {"start": v(-1.02, 11.36) * mm, "end": v(-1.02, 11.36) * mm});
            skLineSegment(sketch, "E2912", {"start": v(-1.02, 11.36) * mm, "end": v(-1.04, 11.34) * mm});
            skLineSegment(sketch, "E2913", {"start": v(-1.04, 11.34) * mm, "end": v(-1.18, 11.26) * mm});
            skLineSegment(sketch, "E2914", {"start": v(-1.18, 11.26) * mm, "end": v(-1.2, 11.26) * mm});
            skLineSegment(sketch, "E2915", {"start": v(2.76, 15.81) * mm, "end": v(1.17, 17.4) * mm});
            skLineSegment(sketch, "E2916", {"start": v(1.17, 17.4) * mm, "end": v(1.16, 17.42) * mm});
            skLineSegment(sketch, "E2917", {"start": v(1.16, 17.42) * mm, "end": v(1.1, 17.44) * mm});
            skLineSegment(sketch, "E2918", {"start": v(1.1, 17.44) * mm, "end": v(1.09, 17.44) * mm});
            skLineSegment(sketch, "E2919", {"start": v(1.09, 17.44) * mm, "end": v(-2.63, 17.44) * mm});
            skLineSegment(sketch, "E2920", {"start": v(-2.63, 17.44) * mm, "end": v(-2.66, 17.44) * mm});
            skLineSegment(sketch, "E2921", {"start": v(-2.66, 17.44) * mm, "end": v(-2.75, 17.36) * mm});
            skLineSegment(sketch, "E2922", {"start": v(-2.75, 17.36) * mm, "end": v(-2.75, 17.33) * mm});
            skLineSegment(sketch, "E2923", {"start": v(-2.75, 17.33) * mm, "end": v(-2.75, 10.4) * mm});
            skLineSegment(sketch, "E2924", {"start": v(-2.75, 10.4) * mm, "end": v(-2.75, 10.37) * mm});
            skLineSegment(sketch, "E2925", {"start": v(-2.75, 10.37) * mm, "end": v(-2.66, 10.29) * mm});
            skLineSegment(sketch, "E2926", {"start": v(-2.66, 10.29) * mm, "end": v(-2.63, 10.29) * mm});
            skLineSegment(sketch, "E2927", {"start": v(-2.63, 10.29) * mm, "end": v(0.62, 10.29) * mm});
            skLineSegment(sketch, "E2928", {"start": v(0.62, 10.29) * mm, "end": v(0.62, 10.51) * mm});
            skLineSegment(sketch, "E2929", {"start": v(0.62, 10.51) * mm, "end": v(-2.52, 10.51) * mm});
            skLineSegment(sketch, "E2930", {"start": v(-2.52, 10.51) * mm, "end": v(-2.52, 17.22) * mm});
            skLineSegment(sketch, "E2931", {"start": v(-2.52, 17.22) * mm, "end": v(1.04, 17.22) * mm});
            skLineSegment(sketch, "E2932", {"start": v(1.04, 17.22) * mm, "end": v(2.57, 15.68) * mm});
            skLineSegment(sketch, "E2933", {"start": v(2.57, 15.68) * mm, "end": v(2.57, 10.51) * mm});
            skLineSegment(sketch, "E2934", {"start": v(2.57, 10.51) * mm, "end": v(1.65, 10.51) * mm});
            skLineSegment(sketch, "E2935", {"start": v(1.65, 10.51) * mm, "end": v(1.65, 10.29) * mm});
            skLineSegment(sketch, "E2936", {"start": v(1.65, 10.29) * mm, "end": v(2.69, 10.29) * mm});
            skLineSegment(sketch, "E2937", {"start": v(2.69, 10.29) * mm, "end": v(2.71, 10.29) * mm});
            skLineSegment(sketch, "E2938", {"start": v(2.71, 10.29) * mm, "end": v(2.8, 10.37) * mm});
            skLineSegment(sketch, "E2939", {"start": v(2.8, 10.37) * mm, "end": v(2.8, 10.4) * mm});
            skLineSegment(sketch, "E2940", {"start": v(2.8, 10.4) * mm, "end": v(2.8, 15.73) * mm});
            skLineSegment(sketch, "E2941", {"start": v(2.8, 15.73) * mm, "end": v(2.8, 15.75) * mm});
            skLineSegment(sketch, "E2942", {"start": v(2.8, 15.75) * mm, "end": v(2.77, 15.8) * mm});
            skLineSegment(sketch, "E2943", {"start": v(2.77, 15.8) * mm, "end": v(2.76, 15.81) * mm});
            skLineSegment(sketch, "E2944", {"start": v(1.12, 11.82) * mm, "end": v(1.03, 11.82) * mm});
            skLineSegment(sketch, "E2945", {"start": v(1.03, 11.82) * mm, "end": v(0.76, 11.68) * mm});
            skLineSegment(sketch, "E2946", {"start": v(0.76, 11.68) * mm, "end": v(0.61, 11.4) * mm});
            skLineSegment(sketch, "E2947", {"start": v(0.61, 11.4) * mm, "end": v(0.61, 11.32) * mm});
            skLineSegment(sketch, "E2948", {"start": v(0.61, 11.32) * mm, "end": v(0.61, 11.23) * mm});
            skLineSegment(sketch, "E2949", {"start": v(0.61, 11.23) * mm, "end": v(0.76, 10.96) * mm});
            skLineSegment(sketch, "E2950", {"start": v(0.76, 10.96) * mm, "end": v(1.03, 10.81) * mm});
            skLineSegment(sketch, "E2951", {"start": v(1.03, 10.81) * mm, "end": v(1.12, 10.81) * mm});
            skLineSegment(sketch, "E2952", {"start": v(1.12, 10.81) * mm, "end": v(1.2, 10.81) * mm});
            skLineSegment(sketch, "E2953", {"start": v(1.2, 10.81) * mm, "end": v(1.48, 10.96) * mm});
            skLineSegment(sketch, "E2954", {"start": v(1.48, 10.96) * mm, "end": v(1.63, 11.23) * mm});
            skLineSegment(sketch, "E2955", {"start": v(1.63, 11.23) * mm, "end": v(1.63, 11.32) * mm});
            skLineSegment(sketch, "E2956", {"start": v(1.63, 11.32) * mm, "end": v(1.63, 11.4) * mm});
            skLineSegment(sketch, "E2957", {"start": v(1.63, 11.4) * mm, "end": v(1.48, 11.68) * mm});
            skLineSegment(sketch, "E2958", {"start": v(1.48, 11.68) * mm, "end": v(1.2, 11.82) * mm});
            skLineSegment(sketch, "E2959", {"start": v(1.2, 11.82) * mm, "end": v(1.12, 11.82) * mm});
            skLineSegment(sketch, "E2960", {"start": v(1.12, 10.67) * mm, "end": v(1, 10.67) * mm});
            skLineSegment(sketch, "E2961", {"start": v(1, 10.67) * mm, "end": v(0.66, 10.86) * mm});
            skLineSegment(sketch, "E2962", {"start": v(0.66, 10.86) * mm, "end": v(0.48, 11.2) * mm});
            skLineSegment(sketch, "E2963", {"start": v(0.48, 11.2) * mm, "end": v(0.48, 11.32) * mm});
            skLineSegment(sketch, "E2964", {"start": v(0.48, 11.32) * mm, "end": v(0.48, 11.43) * mm});
            skLineSegment(sketch, "E2965", {"start": v(0.48, 11.43) * mm, "end": v(0.66, 11.77) * mm});
            skLineSegment(sketch, "E2966", {"start": v(0.66, 11.77) * mm, "end": v(1, 11.96) * mm});
            skLineSegment(sketch, "E2967", {"start": v(1, 11.96) * mm, "end": v(1.12, 11.96) * mm});
            skLineSegment(sketch, "E2968", {"start": v(1.12, 11.96) * mm, "end": v(1.23, 11.96) * mm});
            skLineSegment(sketch, "E2969", {"start": v(1.23, 11.96) * mm, "end": v(1.57, 11.77) * mm});
            skLineSegment(sketch, "E2970", {"start": v(1.57, 11.77) * mm, "end": v(1.76, 11.43) * mm});
            skLineSegment(sketch, "E2971", {"start": v(1.76, 11.43) * mm, "end": v(1.76, 11.32) * mm});
            skLineSegment(sketch, "E2972", {"start": v(1.76, 11.32) * mm, "end": v(1.76, 11.2) * mm});
            skLineSegment(sketch, "E2973", {"start": v(1.76, 11.2) * mm, "end": v(1.57, 10.86) * mm});
            skLineSegment(sketch, "E2974", {"start": v(1.57, 10.86) * mm, "end": v(1.23, 10.67) * mm});
            skLineSegment(sketch, "E2975", {"start": v(1.23, 10.67) * mm, "end": v(1.12, 10.67) * mm});
            skLineSegment(sketch, "E2976", {"start": v(1.95, 11.1) * mm, "end": v(1.95, 11.1) * mm});
            skLineSegment(sketch, "E2977", {"start": v(1.95, 11.1) * mm, "end": v(1.93, 11.1) * mm});
            skLineSegment(sketch, "E2978", {"start": v(1.93, 11.1) * mm, "end": v(1.93, 11.1) * mm});
            skLineSegment(sketch, "E2979", {"start": v(1.93, 11.1) * mm, "end": v(1.92, 11.1) * mm});
            skLineSegment(sketch, "E2980", {"start": v(1.92, 11.1) * mm, "end": v(1.88, 11.18) * mm});
            skLineSegment(sketch, "E2981", {"start": v(1.88, 11.18) * mm, "end": v(1.89, 11.18) * mm});
            skLineSegment(sketch, "E2982", {"start": v(1.89, 11.18) * mm, "end": v(1.9, 11.2) * mm});
            skLineSegment(sketch, "E2983", {"start": v(1.9, 11.2) * mm, "end": v(1.9, 11.22) * mm});
            skLineSegment(sketch, "E2984", {"start": v(1.9, 11.22) * mm, "end": v(1.97, 11.26) * mm});
            skLineSegment(sketch, "E2985", {"start": v(1.97, 11.26) * mm, "end": v(1.98, 11.26) * mm});
            skLineSegment(sketch, "E2986", {"start": v(1.98, 11.26) * mm, "end": v(1.99, 11.25) * mm});
            skLineSegment(sketch, "E2987", {"start": v(1.99, 11.25) * mm, "end": v(2.03, 11.18) * mm});
            skLineSegment(sketch, "E2988", {"start": v(2.03, 11.18) * mm, "end": v(2.03, 11.17) * mm});
            skLineSegment(sketch, "E2989", {"start": v(2.03, 11.17) * mm, "end": v(2.02, 11.14) * mm});
            skLineSegment(sketch, "E2990", {"start": v(2.02, 11.14) * mm, "end": v(2.02, 11.14) * mm});
            skLineSegment(sketch, "E2991", {"start": v(2.02, 11.14) * mm, "end": v(1.97, 11.1) * mm});
            skLineSegment(sketch, "E2992", {"start": v(1.97, 11.1) * mm, "end": v(1.95, 11.1) * mm});
            skLineSegment(sketch, "E2993", {"start": v(1.99, 11.33) * mm, "end": v(1.97, 11.33) * mm});
            skLineSegment(sketch, "E2994", {"start": v(1.97, 11.33) * mm, "end": v(1.92, 11.38) * mm});
            skLineSegment(sketch, "E2995", {"start": v(1.92, 11.38) * mm, "end": v(1.92, 11.4) * mm});
            skLineSegment(sketch, "E2996", {"start": v(1.92, 11.4) * mm, "end": v(1.92, 11.5) * mm});
            skLineSegment(sketch, "E2997", {"start": v(1.92, 11.5) * mm, "end": v(1.8, 11.79) * mm});
            skLineSegment(sketch, "E2998", {"start": v(1.8, 11.79) * mm, "end": v(1.55, 12.02) * mm});
            skLineSegment(sketch, "E2999", {"start": v(1.55, 12.02) * mm, "end": v(1.48, 12.04) * mm});
            skLineSegment(sketch, "E3000", {"start": v(1.48, 12.04) * mm, "end": v(1.47, 12.05) * mm});
            skLineSegment(sketch, "E3001", {"start": v(1.47, 12.05) * mm, "end": v(1.44, 12.13) * mm});
            skLineSegment(sketch, "E3002", {"start": v(1.44, 12.13) * mm, "end": v(1.44, 12.14) * mm});
            skLineSegment(sketch, "E3003", {"start": v(1.44, 12.14) * mm, "end": v(1.45, 12.14) * mm});
            skLineSegment(sketch, "E3004", {"start": v(1.45, 12.14) * mm, "end": v(1.52, 12.18) * mm});
            skLineSegment(sketch, "E3005", {"start": v(1.52, 12.18) * mm, "end": v(1.53, 12.17) * mm});
            skLineSegment(sketch, "E3006", {"start": v(1.53, 12.17) * mm, "end": v(1.61, 12.14) * mm});
            skLineSegment(sketch, "E3007", {"start": v(1.61, 12.14) * mm, "end": v(1.91, 11.87) * mm});
            skLineSegment(sketch, "E3008", {"start": v(1.91, 11.87) * mm, "end": v(2.06, 11.51) * mm});
            skLineSegment(sketch, "E3009", {"start": v(2.06, 11.51) * mm, "end": v(2.06, 11.4) * mm});
            skLineSegment(sketch, "E3010", {"start": v(2.06, 11.4) * mm, "end": v(2.06, 11.38) * mm});
            skLineSegment(sketch, "E3011", {"start": v(2.06, 11.38) * mm, "end": v(2, 11.33) * mm});
            skLineSegment(sketch, "E3012", {"start": v(2, 11.33) * mm, "end": v(1.99, 11.33) * mm});
            skLineSegment(sketch, "E3013", {"start": v(0.68, 9.85) * mm, "end": v(0.67, 9.85) * mm});
            skLineSegment(sketch, "E3014", {"start": v(0.67, 9.85) * mm, "end": v(0.66, 9.86) * mm});
            skLineSegment(sketch, "E3015", {"start": v(0.66, 9.86) * mm, "end": v(0.65, 9.86) * mm});
            skLineSegment(sketch, "E3016", {"start": v(0.65, 9.86) * mm, "end": v(0.65, 9.86) * mm});
            skLineSegment(sketch, "E3017", {"start": v(0.65, 9.86) * mm, "end": v(0.61, 9.9) * mm});
            skLineSegment(sketch, "E3018", {"start": v(0.61, 9.9) * mm, "end": v(0.61, 9.92) * mm});
            skLineSegment(sketch, "E3019", {"start": v(0.61, 9.92) * mm, "end": v(0.61, 10.9) * mm});
            skLineSegment(sketch, "E3020", {"start": v(0.61, 10.9) * mm, "end": v(0.61, 10.93) * mm});
            skLineSegment(sketch, "E3021", {"start": v(0.61, 10.93) * mm, "end": v(0.66, 10.98) * mm});
            skLineSegment(sketch, "E3022", {"start": v(0.66, 10.98) * mm, "end": v(0.68, 10.98) * mm});
            skLineSegment(sketch, "E3023", {"start": v(0.68, 10.98) * mm, "end": v(0.7, 10.98) * mm});
            skLineSegment(sketch, "E3024", {"start": v(0.7, 10.98) * mm, "end": v(0.75, 10.93) * mm});
            skLineSegment(sketch, "E3025", {"start": v(0.75, 10.93) * mm, "end": v(0.75, 10.9) * mm});
            skLineSegment(sketch, "E3026", {"start": v(0.75, 10.9) * mm, "end": v(0.75, 10.08) * mm});
            skLineSegment(sketch, "E3027", {"start": v(0.75, 10.08) * mm, "end": v(1.05, 10.35) * mm});
            skLineSegment(sketch, "E3028", {"start": v(1.05, 10.35) * mm, "end": v(1.05, 10.36) * mm});
            skLineSegment(sketch, "E3029", {"start": v(1.05, 10.36) * mm, "end": v(1.13, 10.36) * mm});
            skLineSegment(sketch, "E3030", {"start": v(1.13, 10.36) * mm, "end": v(1.14, 10.35) * mm});
            skLineSegment(sketch, "E3031", {"start": v(1.14, 10.35) * mm, "end": v(1.51, 10.07) * mm});
            skLineSegment(sketch, "E3032", {"start": v(1.51, 10.07) * mm, "end": v(1.51, 10.94) * mm});
            skLineSegment(sketch, "E3033", {"start": v(1.51, 10.94) * mm, "end": v(1.51, 10.95) * mm});
            skLineSegment(sketch, "E3034", {"start": v(1.51, 10.95) * mm, "end": v(1.56, 11) * mm});
            skLineSegment(sketch, "E3035", {"start": v(1.56, 11) * mm, "end": v(1.58, 11) * mm});
            skLineSegment(sketch, "E3036", {"start": v(1.58, 11) * mm, "end": v(1.6, 11) * mm});
            skLineSegment(sketch, "E3037", {"start": v(1.6, 11) * mm, "end": v(1.65, 10.95) * mm});
            skLineSegment(sketch, "E3038", {"start": v(1.65, 10.95) * mm, "end": v(1.65, 10.94) * mm});
            skLineSegment(sketch, "E3039", {"start": v(1.65, 10.94) * mm, "end": v(1.65, 9.92) * mm});
            skLineSegment(sketch, "E3040", {"start": v(1.65, 9.92) * mm, "end": v(1.65, 9.9) * mm});
            skLineSegment(sketch, "E3041", {"start": v(1.65, 9.9) * mm, "end": v(1.62, 9.87) * mm});
            skLineSegment(sketch, "E3042", {"start": v(1.62, 9.87) * mm, "end": v(1.61, 9.86) * mm});
            skLineSegment(sketch, "E3043", {"start": v(1.61, 9.86) * mm, "end": v(1.6, 9.86) * mm});
            skLineSegment(sketch, "E3044", {"start": v(1.6, 9.86) * mm, "end": v(1.54, 9.87) * mm});
            skLineSegment(sketch, "E3045", {"start": v(1.54, 9.87) * mm, "end": v(1.54, 9.87) * mm});
            skLineSegment(sketch, "E3046", {"start": v(1.54, 9.87) * mm, "end": v(1.1, 10.2) * mm});
            skLineSegment(sketch, "E3047", {"start": v(1.1, 10.2) * mm, "end": v(0.73, 9.87) * mm});
            skLineSegment(sketch, "E3048", {"start": v(0.73, 9.87) * mm, "end": v(0.73, 9.87) * mm});
            skLineSegment(sketch, "E3049", {"start": v(0.73, 9.87) * mm, "end": v(0.7, 9.85) * mm});
            skLineSegment(sketch, "E3050", {"start": v(0.7, 9.85) * mm, "end": v(0.68, 9.85) * mm});
            skLineSegment(sketch, "E3051", {"start": v(-4.99, 19.6) * mm, "end": v(-4.99, 19.5) * mm});
            skLineSegment(sketch, "E3052", {"start": v(-4.99, 19.5) * mm, "end": v(-5.06, 19.22) * mm});
            skLineSegment(sketch, "E3053", {"start": v(-5.06, 19.22) * mm, "end": v(-5.27, 18.92) * mm});
            skLineSegment(sketch, "E3054", {"start": v(-5.27, 18.92) * mm, "end": v(-5.57, 18.71) * mm});
            skLineSegment(sketch, "E3055", {"start": v(-5.57, 18.71) * mm, "end": v(-5.85, 18.64) * mm});
            skLineSegment(sketch, "E3056", {"start": v(-5.85, 18.64) * mm, "end": v(-5.94, 18.64) * mm});
            skLineSegment(sketch, "E3057", {"start": v(-5.94, 18.64) * mm, "end": v(-6.03, 18.64) * mm});
            skLineSegment(sketch, "E3058", {"start": v(-6.03, 18.64) * mm, "end": v(-6.31, 18.71) * mm});
            skLineSegment(sketch, "E3059", {"start": v(-6.31, 18.71) * mm, "end": v(-6.62, 18.92) * mm});
            skLineSegment(sketch, "E3060", {"start": v(-6.62, 18.92) * mm, "end": v(-6.82, 19.22) * mm});
            skLineSegment(sketch, "E3061", {"start": v(-6.82, 19.22) * mm, "end": v(-6.9, 19.5) * mm});
            skLineSegment(sketch, "E3062", {"start": v(-6.9, 19.5) * mm, "end": v(-6.9, 19.6) * mm});
            skLineSegment(sketch, "E3063", {"start": v(-6.9, 19.6) * mm, "end": v(-6.9, 19.68) * mm});
            skLineSegment(sketch, "E3064", {"start": v(-6.9, 19.68) * mm, "end": v(-6.82, 19.96) * mm});
            skLineSegment(sketch, "E3065", {"start": v(-6.82, 19.96) * mm, "end": v(-6.62, 20.27) * mm});
            skLineSegment(sketch, "E3066", {"start": v(-6.62, 20.27) * mm, "end": v(-6.31, 20.47) * mm});
            skLineSegment(sketch, "E3067", {"start": v(-6.31, 20.47) * mm, "end": v(-6.03, 20.55) * mm});
            skLineSegment(sketch, "E3068", {"start": v(-6.03, 20.55) * mm, "end": v(-5.94, 20.55) * mm});
            skLineSegment(sketch, "E3069", {"start": v(-5.94, 20.55) * mm, "end": v(-5.85, 20.55) * mm});
            skLineSegment(sketch, "E3070", {"start": v(-5.85, 20.55) * mm, "end": v(-5.57, 20.47) * mm});
            skLineSegment(sketch, "E3071", {"start": v(-5.57, 20.47) * mm, "end": v(-5.27, 20.27) * mm});
            skLineSegment(sketch, "E3072", {"start": v(-5.27, 20.27) * mm, "end": v(-5.06, 19.96) * mm});
            skLineSegment(sketch, "E3073", {"start": v(-5.06, 19.96) * mm, "end": v(-4.99, 19.68) * mm});
            skLineSegment(sketch, "E3074", {"start": v(-4.99, 19.68) * mm, "end": v(-4.99, 19.6) * mm});
            skLineSegment(sketch, "E3075", {"start": v(7.18, 19.6) * mm, "end": v(7.18, 19.5) * mm});
            skLineSegment(sketch, "E3076", {"start": v(7.18, 19.5) * mm, "end": v(7.1, 19.22) * mm});
            skLineSegment(sketch, "E3077", {"start": v(7.1, 19.22) * mm, "end": v(6.9, 18.92) * mm});
            skLineSegment(sketch, "E3078", {"start": v(6.9, 18.92) * mm, "end": v(6.6, 18.71) * mm});
            skLineSegment(sketch, "E3079", {"start": v(6.6, 18.71) * mm, "end": v(6.32, 18.64) * mm});
            skLineSegment(sketch, "E3080", {"start": v(6.32, 18.64) * mm, "end": v(6.22, 18.64) * mm});
            skLineSegment(sketch, "E3081", {"start": v(6.22, 18.64) * mm, "end": v(6.13, 18.64) * mm});
            skLineSegment(sketch, "E3082", {"start": v(6.13, 18.64) * mm, "end": v(5.85, 18.71) * mm});
            skLineSegment(sketch, "E3083", {"start": v(5.85, 18.71) * mm, "end": v(5.55, 18.92) * mm});
            skLineSegment(sketch, "E3084", {"start": v(5.55, 18.92) * mm, "end": v(5.34, 19.22) * mm});
            skLineSegment(sketch, "E3085", {"start": v(5.34, 19.22) * mm, "end": v(5.27, 19.5) * mm});
            skLineSegment(sketch, "E3086", {"start": v(5.27, 19.5) * mm, "end": v(5.27, 19.6) * mm});
            skLineSegment(sketch, "E3087", {"start": v(5.27, 19.6) * mm, "end": v(5.27, 19.68) * mm});
            skLineSegment(sketch, "E3088", {"start": v(5.27, 19.68) * mm, "end": v(5.34, 19.96) * mm});
            skLineSegment(sketch, "E3089", {"start": v(5.34, 19.96) * mm, "end": v(5.55, 20.27) * mm});
            skLineSegment(sketch, "E3090", {"start": v(5.55, 20.27) * mm, "end": v(5.85, 20.47) * mm});
            skLineSegment(sketch, "E3091", {"start": v(5.85, 20.47) * mm, "end": v(6.13, 20.55) * mm});
            skLineSegment(sketch, "E3092", {"start": v(6.13, 20.55) * mm, "end": v(6.22, 20.55) * mm});
            skLineSegment(sketch, "E3093", {"start": v(6.22, 20.55) * mm, "end": v(6.32, 20.55) * mm});
            skLineSegment(sketch, "E3094", {"start": v(6.32, 20.55) * mm, "end": v(6.6, 20.47) * mm});
            skLineSegment(sketch, "E3095", {"start": v(6.6, 20.47) * mm, "end": v(6.9, 20.27) * mm});
            skLineSegment(sketch, "E3096", {"start": v(6.9, 20.27) * mm, "end": v(7.1, 19.96) * mm});
            skLineSegment(sketch, "E3097", {"start": v(7.1, 19.96) * mm, "end": v(7.18, 19.68) * mm});
            skLineSegment(sketch, "E3098", {"start": v(7.18, 19.68) * mm, "end": v(7.18, 19.6) * mm});
            skSolve(sketch);
        }
        {
            var Q0;
            Q0 = qSketchRegion(id + "F13", true);
            var Q1;
            {var subQ13=sQuery(id+"F13.wireOp",EDGE,"E2714");Q1=makeQuery(id+"F13.imprint","IMPRINT",FACE,{"disambiguationData":[TD([[makeQuery(id+"F13.imprint","IMPRINT",EDGE,{"derivedFrom":subQ13}),-1.0]])]});}
            var Q2;
            {var subQ4=sQuery(id+"F13.wireOp",EDGE,"E2711");Q2=makeQuery(id+"F13.imprint","IMPRINT",FACE,{"disambiguationData":[TD([[makeQuery(id+"F13.imprint","IMPRINT",EDGE,{"derivedFrom":subQ4}),-1.0]])]});}
            var Q3;
            {var subQ0=sQuery(id+"F13.wireOp",EDGE,"E2711");Q3=makeQuery(id+"F13.imprint","IMPRINT",FACE,{"disambiguationData":[TD([[makeQuery(id+"F13.imprint","IMPRINT",EDGE,{"derivedFrom":subQ0}),1.0]])]});}
            var Q4;
            Q4=makeQuery(id+"F13.imprint","IMPRINT",FACE,{"disambiguationData":[TD([[makeQuery(id+"F13.imprint","IMPRINT",EDGE,{"derivedFrom":sQuery(id+"F13.wireOp",EDGE,"E2745")}),-1.0]])]});
            var Q5;
            Q5=makeQuery(id+"F13.imprint","IMPRINT",FACE,{"disambiguationData":[TD([[makeQuery(id+"F13.imprint","IMPRINT",EDGE,{"derivedFrom":sQuery(id+"F13.wireOp",EDGE,"E2731")}),-1.0]])]});
            var Q6;
            Q6=makeQuery(id+"F13.imprint","IMPRINT",FACE,{"disambiguationData":[TD([[makeQuery(id+"F13.imprint","IMPRINT",EDGE,{"derivedFrom":sQuery(id+"F13.wireOp",EDGE,"E2759")}),-1.0]])]});
            var Q7;
            Q7=makeQuery(id+"F13.imprint","IMPRINT",FACE,{"disambiguationData":[TD([[makeQuery(id+"F13.imprint","IMPRINT",EDGE,{"derivedFrom":sQuery(id+"F13.wireOp",EDGE,"E2773")}),-1.0]])]});
            var Q8;
            Q8=makeQuery(id+"F13.imprint","IMPRINT",FACE,{"disambiguationData":[TD([[makeQuery(id+"F13.imprint","IMPRINT",EDGE,{"derivedFrom":sQuery(id+"F13.wireOp",EDGE,"E2944")}),-1.0]])]});
            var Q9;
            Q9=makeQuery(id+"F13.imprint","IMPRINT",FACE,{"disambiguationData":[TD([[makeQuery(id+"F13.imprint","IMPRINT",EDGE,{"derivedFrom":sQuery(id+"F13.wireOp",EDGE,"E2993")}),-1.0]])]});
            var Q10;
            Q10=makeQuery(id+"F13.imprint","IMPRINT",FACE,{"disambiguationData":[TD([[makeQuery(id+"F13.imprint","IMPRINT",EDGE,{"derivedFrom":sQuery(id+"F13.wireOp",EDGE,"E2976")}),-1.0]])]});
            var Q11;
            Q11=makeQuery(id+"F13.imprint","IMPRINT",FACE,{"disambiguationData":[TD([[makeQuery(id+"F13.imprint","IMPRINT",EDGE,{"derivedFrom":sQuery(id+"F13.wireOp",EDGE,"E2787")}),-1.0]])]});
            var Q12;
            Q12=makeQuery(id+"F13.imprint","IMPRINT",FACE,{"disambiguationData":[TD([[makeQuery(id+"F13.imprint","IMPRINT",EDGE,{"derivedFrom":sQuery(id+"F13.wireOp",EDGE,"E2801")}),-1.0]])]});
            var Q13;
            {var subQ0=sQuery(id+"F13.wireOp",EDGE,"E3022");Q13=makeQuery(id+"F13.imprint","IMPRINT",FACE,{"disambiguationData":[TD([[makeQuery(id+"F13.imprint","IMPRINT",EDGE,{"derivedFrom":subQ0}),-1.0]])]});}
            var Q14;
            {var subQ0=sQuery(id+"F13.wireOp",EDGE,"E3033");Q14=makeQuery(id+"F13.imprint","IMPRINT",FACE,{"disambiguationData":[TD([[makeQuery(id+"F13.imprint","IMPRINT",EDGE,{"derivedFrom":subQ0}),-1.0]])]});}
            extrude(context, id + "F14", {"entities" : qUnion([Q0, Q1, Q2, Q3, Q4, Q5, Q6, Q7, Q8, Q9, Q10, Q11, Q12, Q13, Q14]), "operationType" : NewBodyOperationType.REMOVE, "oppositeDirection" : true, "depth" : 3 * mm});
        }
    });
